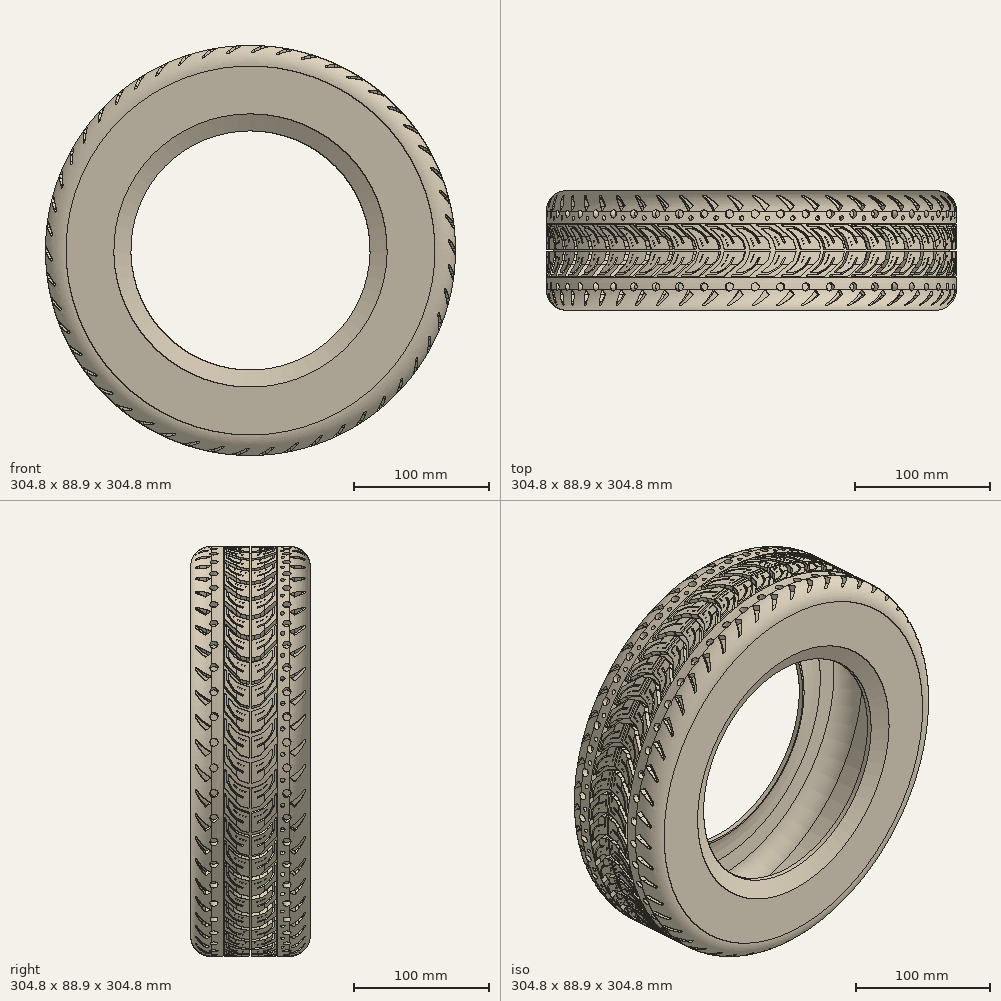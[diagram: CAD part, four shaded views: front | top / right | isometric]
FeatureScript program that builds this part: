
annotation { "Feature Type Name" : "Feature", "Feature Type Description" : "" }
export const myFeature = defineFeature(function(context is Context, id is Id, definition is map)
    precondition{}
    {
        {
            var Q0;
            Q0=qCreatedBy(makeId("Top.planeOp"),FACE);
            var sketch = newSketch(context, id + "F0", { "sketchPlane" : qUnion([Q0])});
            skLineSegment(sketch, "E0", {"start": v(-88.9, 0) * mm, "end": v(-101.6, 6.35) * mm});
            skLineSegment(sketch, "E1", {"start": v(-101.6, 6.35) * mm, "end": v(-152.4, 6.35) * mm});
            skLineSegment(sketch, "E2", {"start": v(-152.4, 6.35) * mm, "end": v(-152.4, -17.78) * mm});
            skLineSegment(sketch, "E3", {"start": v(-152.4, -82.55) * mm, "end": v(-101.6, -82.55) * mm});
            skLineSegment(sketch, "E4", {"start": v(-101.6, -82.55) * mm, "end": v(-88.9, -76.2) * mm});
            skLineSegment(sketch, "E5", {"start": v(-88.9, -76.2) * mm, "end": v(-88.9, -72.4) * mm});
            skLineSegment(sketch, "E6.bottom", {"start": v(-152.4, -37.47) * mm, "end": v(-147.32, -37.47) * mm});
            skLineSegment(sketch, "E6.top", {"start": v(-152.4, -38.74) * mm, "end": v(-147.32, -38.74) * mm});
            skLineSegment(sketch, "E6.left", {"start": v(-152.4, -37.47) * mm, "end": v(-152.4, -38.74) * mm, "construction": true});
            skLineSegment(sketch, "E6.right", {"start": v(-147.32, -37.47) * mm, "end": v(-147.32, -38.74) * mm});
            skLineSegment(sketch, "E7.bottom", {"start": v(-152.4, -57.15) * mm, "end": v(-147.32, -57.15) * mm});
            skLineSegment(sketch, "E7.top", {"start": v(-152.4, -58.42) * mm, "end": v(-147.32, -58.42) * mm});
            skLineSegment(sketch, "E7.left", {"start": v(-152.4, -57.15) * mm, "end": v(-152.4, -58.42) * mm, "construction": true});
            skLineSegment(sketch, "E7.right", {"start": v(-147.32, -57.15) * mm, "end": v(-147.32, -58.42) * mm});
            skLineSegment(sketch, "E8.bottom", {"start": v(-152.4, -17.78) * mm, "end": v(-147.32, -17.78) * mm});
            skLineSegment(sketch, "E8.top", {"start": v(-152.4, -19.05) * mm, "end": v(-147.32, -19.05) * mm});
            skLineSegment(sketch, "E8.left", {"start": v(-152.4, -17.78) * mm, "end": v(-152.4, -19.05) * mm, "construction": true});
            skLineSegment(sketch, "E8.right", {"start": v(-147.32, -17.78) * mm, "end": v(-147.32, -19.05) * mm});
            skPoint(sketch, "E9", {"position": v(-152.4, -38.1) * mm});
            skLineSegment(sketch, "E10.trimOffspring", {"start": v(-152.4, -19.05) * mm, "end": v(-152.4, -37.47) * mm});
            skLineSegment(sketch, "E11.trimOffspring", {"start": v(-152.4, -38.74) * mm, "end": v(-152.4, -57.15) * mm});
            skLineSegment(sketch, "E12.trimOffspring", {"start": v(-152.4, -58.42) * mm, "end": v(-152.4, -82.55) * mm});
            skLineSegment(sketch, "E13", {"start": v(-88.9, -3.81) * mm, "end": v(-91.31, -2.63) * mm});
            skLineSegment(sketch, "E14", {"start": v(-113.64, 2.54) * mm, "end": v(-128.27, 2.54) * mm});
            skLineSegment(sketch, "E15", {"start": v(-143.5, -12.7) * mm, "end": v(-143.5, -63.5) * mm});
            skLineSegment(sketch, "E16", {"start": v(-128.27, -78.74) * mm, "end": v(-113.64, -78.74) * mm});
            skLineSegment(sketch, "E17", {"start": v(-91.32, -73.57) * mm, "end": v(-88.9, -72.4) * mm});
            skPoint(sketch, "E18.visualSharp", {"position": v(-101.88, -78.74) * mm});
            skArc(sketch, "E18.filletArc", {"start": v(-113.64, -78.74) * mm, "mid": v(-102.18, -77.43) * mm, "end": v(-91.32, -73.57) * mm});
            skPoint(sketch, "E19.visualSharp", {"position": v(-101.88, 2.54) * mm});
            skArc(sketch, "E19.filletArc", {"start": v(-91.31, -2.63) * mm, "mid": v(-102.18, 1.23) * mm, "end": v(-113.64, 2.54) * mm});
            skPoint(sketch, "E20.visualSharp", {"position": v(-143.5, 2.54) * mm});
            skArc(sketch, "E20.filletArc", {"start": v(-128.27, 2.54) * mm, "mid": v(-139.05, -1.92) * mm, "end": v(-143.5, -12.7) * mm});
            skPoint(sketch, "E21.visualSharp", {"position": v(-143.5, -78.74) * mm});
            skArc(sketch, "E21.filletArc", {"start": v(-143.5, -63.5) * mm, "mid": v(-139.05, -74.28) * mm, "end": v(-128.27, -78.74) * mm});
            skLineSegment(sketch, "E22.trimOffspring", {"start": v(-88.9, -3.8) * mm, "end": v(-88.9, 0) * mm});
            skSolve(sketch);
        }
        {
            var Q0;
            Q0=qCreatedBy(makeId("Top.planeOp"),FACE);
            var sketch = newSketch(context, id + "F1", { "sketchPlane" : qUnion([Q0])});
            skLineSegment(sketch, "E23", {"start": v(0, 30.8) * mm, "end": v(0, -66.3) * mm});
            skSolve(sketch);
        }
        {
            var Q0;
            Q0=makeQuery(id+"F0.imprint","IMPRINT",FACE,{"disambiguationData":[TD([[makeQuery(id+"F0.imprint","IMPRINT",EDGE,{"derivedFrom":sQuery(id+"F0.wireOp",EDGE,"E0")}),1.0]])]});
            var Q1;
            Q1=sQuery(id+"F1.wireOp",EDGE,"E23");
            revolve(context, id + "F2", {"entities" : qUnion([Q0]), "axis" : qUnion([Q1]), "revolveType" : RevolveType.FULL});
        }
        {
            var Q0;
            Q0=qCreatedBy(makeId("Top.planeOp"),FACE);
            cPlane(context, id + "F3", {"entities" : qUnion([Q0]), "cplaneType" : CPlaneType.OFFSET, "offset" : 152.4 * mm, "width" : 152.4 * mm, "height" : 152.4 * mm});
        }
        {
            var Q0;
            Q0=qCreatedBy(id+"F3.planeOp",FACE);
            var sketch = newSketch(context, id + "F4", { "sketchPlane" : qUnion([Q0])});
            skLineSegment(sketch, "E24", {"start": v(3.28, -18.53) * mm, "end": v(5.87, -20.6) * mm});
            skLineSegment(sketch, "E25", {"start": v(16.2, -31.53) * mm, "end": v(18.35, -38.1) * mm});
            skLineSegment(sketch, "E26", {"start": v(18.35, -38.1) * mm, "end": v(14.54, -38.1) * mm});
            skLineSegment(sketch, "E27", {"start": v(14.54, -38.1) * mm, "end": v(13.73, -35.49) * mm});
            skLineSegment(sketch, "E28", {"start": v(12.18, -30.48) * mm, "end": v(-1.8, -18.53) * mm});
            skLineSegment(sketch, "E29", {"start": v(-1.8, -18.53) * mm, "end": v(3.28, -18.53) * mm});
            skLineSegment(sketch, "E30.0.MirrorCS", {"start": v(14.54, -38.1) * mm, "end": v(13.73, -40.71) * mm});
            skLineSegment(sketch, "E31.0.MirrorCS", {"start": v(12.18, -45.72) * mm, "end": v(-1.8, -57.67) * mm});
            skLineSegment(sketch, "E32.0.MirrorCS", {"start": v(-1.8, -57.67) * mm, "end": v(3.28, -57.67) * mm});
            skLineSegment(sketch, "E33.0.MirrorCS", {"start": v(3.28, -57.67) * mm, "end": v(5.87, -55.6) * mm});
            skLineSegment(sketch, "E34.0.MirrorCS", {"start": v(16.2, -44.67) * mm, "end": v(18.35, -38.1) * mm});
            skPoint(sketch, "E35.visualSharp", {"position": v(15.02, -27.94) * mm});
            skArc(sketch, "E35.filletArc", {"start": v(16.2, -31.53) * mm, "mid": v(14.57, -28.25) * mm, "end": v(12.07, -25.58) * mm});
            skPoint(sketch, "E36.visualSharp", {"position": v(15.02, -48.26) * mm});
            skArc(sketch, "E36.filletArc", {"start": v(12.07, -50.62) * mm, "mid": v(14.57, -47.95) * mm, "end": v(16.2, -44.67) * mm});
            skLineSegment(sketch, "E37", {"start": v(13.73, -35.49) * mm, "end": v(1.75, -35.49) * mm});
            skLineSegment(sketch, "E38", {"start": v(1.75, -35.49) * mm, "end": v(0.57, -32.03) * mm});
            skLineSegment(sketch, "E39", {"start": v(-2.43, -27.2) * mm, "end": v(-4.76, -24.84) * mm});
            skLineSegment(sketch, "E40", {"start": v(-4.76, -24.84) * mm, "end": v(-2.45, -26.92) * mm});
            skLineSegment(sketch, "E41", {"start": v(1.07, -32.25) * mm, "end": v(1.98, -34.92) * mm});
            skLineSegment(sketch, "E42", {"start": v(1.98, -34.92) * mm, "end": v(13.56, -34.92) * mm});
            skPoint(sketch, "E43.visualSharp", {"position": v(-0.38, -29.27) * mm});
            skArc(sketch, "E43.filletArc", {"start": v(0.57, -32.03) * mm, "mid": v(-0.66, -29.45) * mm, "end": v(-2.43, -27.2) * mm});
            skPoint(sketch, "E44.visualSharp", {"position": v(0, -29.13) * mm});
            skArc(sketch, "E44.filletArc", {"start": v(1.07, -32.25) * mm, "mid": v(-0.35, -29.36) * mm, "end": v(-2.45, -26.92) * mm});
            skLineSegment(sketch, "E45.trimOffspring", {"start": v(13.56, -34.92) * mm, "end": v(12.18, -30.48) * mm});
            skLineSegment(sketch, "E46.trimOffspring", {"start": v(7.15, -21.63) * mm, "end": v(12.07, -25.58) * mm});
            skLineSegment(sketch, "E47", {"start": v(7.15, -21.63) * mm, "end": v(9.7, -21.63) * mm});
            skLineSegment(sketch, "E48", {"start": v(16.06, -23.34) * mm, "end": v(17.68, -24.28) * mm});
            skLineSegment(sketch, "E49", {"start": v(22.64, -29.52) * mm, "end": v(24.47, -33.12) * mm});
            skLineSegment(sketch, "E50", {"start": v(24.47, -33.12) * mm, "end": v(25.78, -33.12) * mm});
            skLineSegment(sketch, "E51", {"start": v(25.78, -33.12) * mm, "end": v(23.67, -28.97) * mm});
            skLineSegment(sketch, "E52", {"start": v(18.6, -23.67) * mm, "end": v(13.2, -20.6) * mm});
            skLineSegment(sketch, "E53", {"start": v(13.2, -20.6) * mm, "end": v(5.87, -20.6) * mm});
            skPoint(sketch, "E54.visualSharp", {"position": v(20.94, -26.17) * mm});
            skArc(sketch, "E54.filletArc", {"start": v(22.64, -29.52) * mm, "mid": v(20.54, -26.54) * mm, "end": v(17.68, -24.28) * mm});
            skPoint(sketch, "E55.visualSharp", {"position": v(21.94, -25.56) * mm});
            skArc(sketch, "E55.filletArc", {"start": v(23.67, -28.97) * mm, "mid": v(23.4, -28.45) * mm, "end": v(23.1, -27.95) * mm});
            skPoint(sketch, "E56.visualSharp", {"position": v(13.1, -21.63) * mm});
            skArc(sketch, "E56.filletArc", {"start": v(16.06, -23.34) * mm, "mid": v(12.99, -22.07) * mm, "end": v(9.7, -21.63) * mm});
            skLineSegment(sketch, "E57", {"start": v(23.1, -27.95) * mm, "end": v(29.11, -27.95) * mm});
            skLineSegment(sketch, "E58", {"start": v(29.11, -27.95) * mm, "end": v(29.11, -27.6) * mm});
            skLineSegment(sketch, "E59", {"start": v(29.11, -27.6) * mm, "end": v(22.86, -27.6) * mm});
            skArc(sketch, "E60.trimOffspring", {"start": v(22.86, -27.6) * mm, "mid": v(20.96, -25.39) * mm, "end": v(18.6, -23.67) * mm});
            skLineSegment(sketch, "E61.0.MirrorCS", {"start": v(29.11, -48.25) * mm, "end": v(29.11, -48.6) * mm});
            skLineSegment(sketch, "E61.1.MirrorCS", {"start": v(23.1, -48.25) * mm, "end": v(29.11, -48.25) * mm});
            skLineSegment(sketch, "E61.2.MirrorCS", {"start": v(24.47, -43.08) * mm, "end": v(25.78, -43.08) * mm});
            skArc(sketch, "E61.3.MirrorCS", {"start": v(22.86, -48.6) * mm, "mid": v(20.96, -50.81) * mm, "end": v(18.6, -52.53) * mm});
            skLineSegment(sketch, "E61.4.MirrorCS", {"start": v(25.78, -43.08) * mm, "end": v(23.67, -47.23) * mm});
            skLineSegment(sketch, "E61.5.MirrorCS", {"start": v(29.11, -48.6) * mm, "end": v(22.86, -48.6) * mm});
            skArc(sketch, "E61.6.MirrorCS", {"start": v(22.64, -46.68) * mm, "mid": v(20.54, -49.66) * mm, "end": v(17.68, -51.92) * mm});
            skArc(sketch, "E61.7.MirrorCS", {"start": v(23.67, -47.23) * mm, "mid": v(23.4, -47.75) * mm, "end": v(23.1, -48.25) * mm});
            skPoint(sketch, "E61.8.MirrorP", {"position": v(21.94, -50.64) * mm});
            skPoint(sketch, "E61.9.MirrorP", {"position": v(20.94, -50.03) * mm});
            skLineSegment(sketch, "E61.10.MirrorCS", {"start": v(22.64, -46.68) * mm, "end": v(24.47, -43.08) * mm});
            skLineSegment(sketch, "E62.0.MirrorCS", {"start": v(16.06, -52.86) * mm, "end": v(17.68, -51.92) * mm});
            skPoint(sketch, "E62.1.MirrorP", {"position": v(13.1, -54.57) * mm});
            skLineSegment(sketch, "E62.2.MirrorCS", {"start": v(18.6, -52.53) * mm, "end": v(13.2, -55.6) * mm});
            skLineSegment(sketch, "E62.3.MirrorCS", {"start": v(13.2, -55.6) * mm, "end": v(5.87, -55.6) * mm});
            skArc(sketch, "E62.4.MirrorCS", {"start": v(16.06, -52.86) * mm, "mid": v(12.99, -54.13) * mm, "end": v(9.7, -54.57) * mm});
            skLineSegment(sketch, "E63.0.MirrorCS", {"start": v(7.15, -54.57) * mm, "end": v(9.7, -54.57) * mm});
            skPoint(sketch, "E64.0.MirrorP", {"position": v(0, -47.07) * mm});
            skArc(sketch, "E64.1.MirrorCS", {"start": v(1.07, -43.95) * mm, "mid": v(-0.35, -46.84) * mm, "end": v(-2.45, -49.28) * mm});
            skLineSegment(sketch, "E64.2.MirrorCS", {"start": v(-2.43, -49) * mm, "end": v(-4.76, -51.36) * mm});
            skLineSegment(sketch, "E64.3.MirrorCS", {"start": v(1.75, -40.71) * mm, "end": v(0.57, -44.17) * mm});
            skArc(sketch, "E64.4.MirrorCS", {"start": v(0.57, -44.17) * mm, "mid": v(-0.66, -46.75) * mm, "end": v(-2.43, -49) * mm});
            skLineSegment(sketch, "E64.5.MirrorCS", {"start": v(1.07, -43.95) * mm, "end": v(1.98, -41.28) * mm});
            skLineSegment(sketch, "E64.6.MirrorCS", {"start": v(-4.76, -51.36) * mm, "end": v(-2.45, -49.28) * mm});
            skPoint(sketch, "E64.7.MirrorP", {"position": v(-0.38, -46.93) * mm});
            skLineSegment(sketch, "E65.0.MirrorCS", {"start": v(13.73, -40.71) * mm, "end": v(1.75, -40.71) * mm});
            skLineSegment(sketch, "E66.0.MirrorCS", {"start": v(1.98, -41.28) * mm, "end": v(13.56, -41.28) * mm});
            skLineSegment(sketch, "E67.trimOffspring", {"start": v(13.56, -41.28) * mm, "end": v(12.18, -45.72) * mm});
            skLineSegment(sketch, "E68.trimOffspring", {"start": v(7.15, -54.57) * mm, "end": v(12.07, -50.62) * mm});
            skCircle(sketch, "E69", {"center": v(11.89, -14.08) * mm, "radius": 1.67 * mm});
            skCircle(sketch, "E70", {"center": v(2.74, -10.98) * mm, "radius": 3.03 * mm});
            skLineSegment(sketch, "E71", {"start": v(10.12, -9.06) * mm, "end": v(7.72, -5.31) * mm});
            skLineSegment(sketch, "E72", {"start": v(3.19, 0) * mm, "end": v(-5.38, 7.62) * mm});
            skLineSegment(sketch, "E73", {"start": v(-5.38, 7.62) * mm, "end": v(-4.52, 6.86) * mm});
            skLineSegment(sketch, "E74", {"start": v(-4.52, 6.86) * mm, "end": v(6.4, 0.45) * mm});
            skLineSegment(sketch, "E75", {"start": v(10.3, -2.38) * mm, "end": v(13.22, -4.93) * mm});
            skLineSegment(sketch, "E76", {"start": v(13.22, -4.93) * mm, "end": v(10.12, -9.06) * mm});
            skPoint(sketch, "E77.visualSharp", {"position": v(5.82, -2.34) * mm});
            skArc(sketch, "E77.filletArc", {"start": v(7.72, -5.31) * mm, "mid": v(5.64, -2.5) * mm, "end": v(3.19, 0) * mm});
            skPoint(sketch, "E78.visualSharp", {"position": v(8.49, -0.78) * mm});
            skArc(sketch, "E78.filletArc", {"start": v(10.3, -2.38) * mm, "mid": v(8.42, -0.87) * mm, "end": v(6.4, 0.45) * mm});
            skCircle(sketch, "E79.0.MirrorC", {"center": v(11.89, -62.12) * mm, "radius": 1.67 * mm});
            skCircle(sketch, "E80.0.MirrorC", {"center": v(2.74, -65.22) * mm, "radius": 3.03 * mm});
            skLineSegment(sketch, "E81.0.MirrorCS", {"start": v(13.22, -71.27) * mm, "end": v(10.12, -67.14) * mm});
            skLineSegment(sketch, "E82.0.MirrorCS", {"start": v(10.12, -67.14) * mm, "end": v(7.72, -70.89) * mm});
            skLineSegment(sketch, "E83.0.MirrorCS", {"start": v(10.3, -73.82) * mm, "end": v(13.22, -71.27) * mm});
            skArc(sketch, "E84.0.MirrorCS", {"start": v(10.3, -73.82) * mm, "mid": v(8.42, -75.33) * mm, "end": v(6.4, -76.65) * mm});
            skArc(sketch, "E85.0.MirrorCS", {"start": v(7.72, -70.89) * mm, "mid": v(5.64, -73.7) * mm, "end": v(3.19, -76.2) * mm});
            skLineSegment(sketch, "E86.0.MirrorCS", {"start": v(3.19, -76.2) * mm, "end": v(-5.38, -83.82) * mm});
            skLineSegment(sketch, "E87.0.MirrorCS", {"start": v(-4.52, -83.06) * mm, "end": v(6.4, -76.65) * mm});
            skLineSegment(sketch, "E88.0.MirrorCS", {"start": v(-5.38, -83.82) * mm, "end": v(-4.52, -83.06) * mm});
            skLineSegment(sketch, "E89", {"start": v(2.63, -62.2) * mm, "end": v(2.86, -62.2) * mm});
            skSolve(sketch);
        }
        {
            var Q0;
            Q0=makeQuery(id+"F4.imprint","IMPRINT",FACE,{"disambiguationData":[TD([[makeQuery(id+"F4.imprint","IMPRINT",EDGE,{"derivedFrom":sQuery(id+"F4.wireOp",EDGE,"E24")}),-1.0]])]});
            var Q1;
            Q1=makeQuery(id+"F4.imprint","IMPRINT",FACE,{"disambiguationData":[TD([[makeQuery(id+"F4.imprint","IMPRINT",EDGE,{"derivedFrom":sQuery(id+"F4.wireOp",EDGE,"E26")}),1.0]])]});
            var Q2;
            Q2=makeQuery(id+"F4.imprint","IMPRINT",FACE,{"disambiguationData":[TD([[makeQuery(id+"F4.imprint","IMPRINT",EDGE,{"derivedFrom":sQuery(id+"F4.wireOp",EDGE,"E70")}),1.0]])]});
            var Q3;
            Q3=makeQuery(id+"F4.imprint","IMPRINT",FACE,{"disambiguationData":[TD([[makeQuery(id+"F4.imprint","IMPRINT",EDGE,{"derivedFrom":sQuery(id+"F4.wireOp",EDGE,"E69")}),1.0]])]});
            var Q4;
            Q4=makeQuery(id+"F4.imprint","IMPRINT",FACE,{"disambiguationData":[TD([[makeQuery(id+"F4.imprint","IMPRINT",EDGE,{"derivedFrom":sQuery(id+"F4.wireOp",EDGE,"E71")}),-1.0]])]});
            var Q5;
            Q5=makeQuery(id+"F4.imprint","IMPRINT",FACE,{"disambiguationData":[TD([[makeQuery(id+"F4.imprint","IMPRINT",EDGE,{"derivedFrom":sQuery(id+"F4.wireOp",EDGE,"E79.0.MirrorC")}),-1.0]])]});
            var Q6;
            {var subQ0=sQuery(id+"F4.wireOp",EDGE,"E89");Q6=makeQuery(id+"F4.imprint","IMPRINT",FACE,{"disambiguationData":[TD([[makeQuery(id+"F4.imprint","IMPRINT",EDGE,{"derivedFrom":subQ0}),-1.0]])]});}
            var Q7;
            Q7=makeQuery(id+"F4.imprint","IMPRINT",FACE,{"disambiguationData":[TD([[makeQuery(id+"F4.imprint","IMPRINT",EDGE,{"derivedFrom":sQuery(id+"F4.wireOp",EDGE,"E81.0.MirrorCS")}),1.0]])]});
            var Q8;
            Q8=makeQuery(id+"F2.opRevolve","SWEPT_FACE",FACE,{"disambiguationData":[OSD([sQuery(id+"F0.wireOp",EDGE,"E6.right")])]});
            extrude(context, id + "F5", {"entities" : qUnion([Q0, Q1, Q2, Q3, Q4, Q5, Q6, Q7]), "endBound" : BoundingType.UP_TO_SURFACE, "oppositeDirection" : true, "endBoundEntityFace" : qUnion([Q8]), "depth" : 25.4 * mm});
        }
        {
            var Q0;
            Q0=makeQuery(id+"F5.opExtrude","SWEPT_BODY",BODY,{"disambiguationData":[OSD([sQuery(id+"F4.wireOp",EDGE,"E24"),sQuery(id+"F4.wireOp",EDGE,"E25"),sQuery(id+"F4.wireOp",EDGE,"E26"),sQuery(id+"F4.wireOp",EDGE,"E27"),sQuery(id+"F4.wireOp",EDGE,"E28"),sQuery(id+"F4.wireOp",EDGE,"E29")])]});
            var Q1;
            Q1=makeQuery(id+"F5.opExtrude","SWEPT_BODY",BODY,{"disambiguationData":[OSD([sQuery(id+"F4.wireOp",EDGE,"E71"),sQuery(id+"F4.wireOp",EDGE,"E72"),sQuery(id+"F4.wireOp",EDGE,"E74"),sQuery(id+"F4.wireOp",EDGE,"E75"),sQuery(id+"F4.wireOp",EDGE,"E76"),sQuery(id+"F4.wireOp",EDGE,"E77.filletArc"),sQuery(id+"F4.wireOp",EDGE,"E78.filletArc")])]});
            var Q2;
            Q2=makeQuery(id+"F5.opExtrude","SWEPT_BODY",BODY,{"disambiguationData":[OSD([sQuery(id+"F4.wireOp",EDGE,"E70")])]});
            var Q3;
            Q3=makeQuery(id+"F5.opExtrude","SWEPT_BODY",BODY,{"disambiguationData":[OSD([sQuery(id+"F4.wireOp",EDGE,"E69")])]});
            var Q4;
            Q4=makeQuery(id+"F5.opExtrude","SWEPT_BODY",BODY,{"disambiguationData":[OSD([sQuery(id+"F4.wireOp",EDGE,"E80.0.MirrorC"),sQuery(id+"F4.wireOp",EDGE,"E89")])]});
            var Q5;
            Q5=makeQuery(id+"F5.opExtrude","SWEPT_BODY",BODY,{"disambiguationData":[OSD([sQuery(id+"F4.wireOp",EDGE,"E79.0.MirrorC")])]});
            var Q6;
            Q6=makeQuery(id+"F5.opExtrude","SWEPT_BODY",BODY,{"disambiguationData":[OSD([sQuery(id+"F4.wireOp",EDGE,"E81.0.MirrorCS"),sQuery(id+"F4.wireOp",EDGE,"E82.0.MirrorCS"),sQuery(id+"F4.wireOp",EDGE,"E83.0.MirrorCS"),sQuery(id+"F4.wireOp",EDGE,"E84.0.MirrorCS"),sQuery(id+"F4.wireOp",EDGE,"E85.0.MirrorCS"),sQuery(id+"F4.wireOp",EDGE,"E86.0.MirrorCS"),sQuery(id+"F4.wireOp",EDGE,"E87.0.MirrorCS")])]});
            var Q7;
            Q7=sQuery(id+"F1.wireOp",EDGE,"E23");
            circularPattern(context, id + "F6", {"entities" : qUnion([Q0, Q1, Q2, Q3, Q4, Q5, Q6]), "axis" : qUnion([Q7]), "angle" : 360 * degree, "instanceCount" : 50, "equalSpace" : true});
        }
        {
            var Q0;
            Q0=makeQuery(id+"F5.opExtrude","SWEPT_BODY",BODY,{"disambiguationData":[OSD([sQuery(id+"F4.wireOp",EDGE,"E69")])]});
            var Q1;
            Q1=makeQuery(id+"F5.opExtrude","SWEPT_BODY",BODY,{"disambiguationData":[OSD([sQuery(id+"F4.wireOp",EDGE,"E70")])]});
            var Q2;
            Q2=makeQuery(id+"F5.opExtrude","SWEPT_BODY",BODY,{"disambiguationData":[OSD([sQuery(id+"F4.wireOp",EDGE,"E71"),sQuery(id+"F4.wireOp",EDGE,"E72"),sQuery(id+"F4.wireOp",EDGE,"E74"),sQuery(id+"F4.wireOp",EDGE,"E75"),sQuery(id+"F4.wireOp",EDGE,"E76"),sQuery(id+"F4.wireOp",EDGE,"E77.filletArc"),sQuery(id+"F4.wireOp",EDGE,"E78.filletArc")])]});
            var Q3;
            Q3=makeQuery(id+"F5.opExtrude","SWEPT_BODY",BODY,{"disambiguationData":[OSD([sQuery(id+"F4.wireOp",EDGE,"E79.0.MirrorC")])]});
            var Q4;
            Q4=makeQuery(id+"F5.opExtrude","SWEPT_BODY",BODY,{"disambiguationData":[OSD([sQuery(id+"F4.wireOp",EDGE,"E80.0.MirrorC"),sQuery(id+"F4.wireOp",EDGE,"E89")])]});
            var Q5;
            Q5=makeQuery(id+"F5.opExtrude","SWEPT_BODY",BODY,{"disambiguationData":[OSD([sQuery(id+"F4.wireOp",EDGE,"E81.0.MirrorCS"),sQuery(id+"F4.wireOp",EDGE,"E82.0.MirrorCS"),sQuery(id+"F4.wireOp",EDGE,"E83.0.MirrorCS"),sQuery(id+"F4.wireOp",EDGE,"E84.0.MirrorCS"),sQuery(id+"F4.wireOp",EDGE,"E85.0.MirrorCS"),sQuery(id+"F4.wireOp",EDGE,"E86.0.MirrorCS"),sQuery(id+"F4.wireOp",EDGE,"E87.0.MirrorCS")])]});
            var Q6;
            Q6=makeQuery(id+"F6.opPattern","COPY",BODY,{"derivedFrom":makeQuery(id+"F5.opExtrude","SWEPT_BODY",BODY,{"disambiguationData":[OSD([sQuery(id+"F4.wireOp",EDGE,"E69")])]}),"instanceName":"1"});
            var Q7;
            Q7=makeQuery(id+"F6.opPattern","COPY",BODY,{"derivedFrom":makeQuery(id+"F5.opExtrude","SWEPT_BODY",BODY,{"disambiguationData":[OSD([sQuery(id+"F4.wireOp",EDGE,"E70")])]}),"instanceName":"1"});
            var Q8;
            Q8=makeQuery(id+"F6.opPattern","COPY",BODY,{"derivedFrom":makeQuery(id+"F5.opExtrude","SWEPT_BODY",BODY,{"disambiguationData":[OSD([sQuery(id+"F4.wireOp",EDGE,"E71"),sQuery(id+"F4.wireOp",EDGE,"E72"),sQuery(id+"F4.wireOp",EDGE,"E74"),sQuery(id+"F4.wireOp",EDGE,"E75"),sQuery(id+"F4.wireOp",EDGE,"E76"),sQuery(id+"F4.wireOp",EDGE,"E77.filletArc"),sQuery(id+"F4.wireOp",EDGE,"E78.filletArc")])]}),"instanceName":"1"});
            var Q9;
            Q9=makeQuery(id+"F6.opPattern","COPY",BODY,{"derivedFrom":makeQuery(id+"F5.opExtrude","SWEPT_BODY",BODY,{"disambiguationData":[OSD([sQuery(id+"F4.wireOp",EDGE,"E79.0.MirrorC")])]}),"instanceName":"1"});
            var Q10;
            Q10=makeQuery(id+"F6.opPattern","COPY",BODY,{"derivedFrom":makeQuery(id+"F5.opExtrude","SWEPT_BODY",BODY,{"disambiguationData":[OSD([sQuery(id+"F4.wireOp",EDGE,"E80.0.MirrorC"),sQuery(id+"F4.wireOp",EDGE,"E89")])]}),"instanceName":"1"});
            var Q11;
            Q11=makeQuery(id+"F6.opPattern","COPY",BODY,{"derivedFrom":makeQuery(id+"F5.opExtrude","SWEPT_BODY",BODY,{"disambiguationData":[OSD([sQuery(id+"F4.wireOp",EDGE,"E81.0.MirrorCS"),sQuery(id+"F4.wireOp",EDGE,"E82.0.MirrorCS"),sQuery(id+"F4.wireOp",EDGE,"E83.0.MirrorCS"),sQuery(id+"F4.wireOp",EDGE,"E84.0.MirrorCS"),sQuery(id+"F4.wireOp",EDGE,"E85.0.MirrorCS"),sQuery(id+"F4.wireOp",EDGE,"E86.0.MirrorCS"),sQuery(id+"F4.wireOp",EDGE,"E87.0.MirrorCS")])]}),"instanceName":"1"});
            var Q12;
            Q12=makeQuery(id+"F6.opPattern","COPY",BODY,{"derivedFrom":makeQuery(id+"F5.opExtrude","SWEPT_BODY",BODY,{"disambiguationData":[OSD([sQuery(id+"F4.wireOp",EDGE,"E69")])]}),"instanceName":"2"});
            var Q13;
            Q13=makeQuery(id+"F6.opPattern","COPY",BODY,{"derivedFrom":makeQuery(id+"F5.opExtrude","SWEPT_BODY",BODY,{"disambiguationData":[OSD([sQuery(id+"F4.wireOp",EDGE,"E70")])]}),"instanceName":"2"});
            var Q14;
            Q14=makeQuery(id+"F6.opPattern","COPY",BODY,{"derivedFrom":makeQuery(id+"F5.opExtrude","SWEPT_BODY",BODY,{"disambiguationData":[OSD([sQuery(id+"F4.wireOp",EDGE,"E71"),sQuery(id+"F4.wireOp",EDGE,"E72"),sQuery(id+"F4.wireOp",EDGE,"E74"),sQuery(id+"F4.wireOp",EDGE,"E75"),sQuery(id+"F4.wireOp",EDGE,"E76"),sQuery(id+"F4.wireOp",EDGE,"E77.filletArc"),sQuery(id+"F4.wireOp",EDGE,"E78.filletArc")])]}),"instanceName":"2"});
            var Q15;
            Q15=makeQuery(id+"F6.opPattern","COPY",BODY,{"derivedFrom":makeQuery(id+"F5.opExtrude","SWEPT_BODY",BODY,{"disambiguationData":[OSD([sQuery(id+"F4.wireOp",EDGE,"E79.0.MirrorC")])]}),"instanceName":"2"});
            var Q16;
            Q16=makeQuery(id+"F6.opPattern","COPY",BODY,{"derivedFrom":makeQuery(id+"F5.opExtrude","SWEPT_BODY",BODY,{"disambiguationData":[OSD([sQuery(id+"F4.wireOp",EDGE,"E80.0.MirrorC"),sQuery(id+"F4.wireOp",EDGE,"E89")])]}),"instanceName":"2"});
            var Q17;
            Q17=makeQuery(id+"F6.opPattern","COPY",BODY,{"derivedFrom":makeQuery(id+"F5.opExtrude","SWEPT_BODY",BODY,{"disambiguationData":[OSD([sQuery(id+"F4.wireOp",EDGE,"E81.0.MirrorCS"),sQuery(id+"F4.wireOp",EDGE,"E82.0.MirrorCS"),sQuery(id+"F4.wireOp",EDGE,"E83.0.MirrorCS"),sQuery(id+"F4.wireOp",EDGE,"E84.0.MirrorCS"),sQuery(id+"F4.wireOp",EDGE,"E85.0.MirrorCS"),sQuery(id+"F4.wireOp",EDGE,"E86.0.MirrorCS"),sQuery(id+"F4.wireOp",EDGE,"E87.0.MirrorCS")])]}),"instanceName":"2"});
            var Q18;
            Q18=makeQuery(id+"F6.opPattern","COPY",BODY,{"derivedFrom":makeQuery(id+"F5.opExtrude","SWEPT_BODY",BODY,{"disambiguationData":[OSD([sQuery(id+"F4.wireOp",EDGE,"E69")])]}),"instanceName":"3"});
            var Q19;
            Q19=makeQuery(id+"F6.opPattern","COPY",BODY,{"derivedFrom":makeQuery(id+"F5.opExtrude","SWEPT_BODY",BODY,{"disambiguationData":[OSD([sQuery(id+"F4.wireOp",EDGE,"E70")])]}),"instanceName":"3"});
            var Q20;
            Q20=makeQuery(id+"F6.opPattern","COPY",BODY,{"derivedFrom":makeQuery(id+"F5.opExtrude","SWEPT_BODY",BODY,{"disambiguationData":[OSD([sQuery(id+"F4.wireOp",EDGE,"E71"),sQuery(id+"F4.wireOp",EDGE,"E72"),sQuery(id+"F4.wireOp",EDGE,"E74"),sQuery(id+"F4.wireOp",EDGE,"E75"),sQuery(id+"F4.wireOp",EDGE,"E76"),sQuery(id+"F4.wireOp",EDGE,"E77.filletArc"),sQuery(id+"F4.wireOp",EDGE,"E78.filletArc")])]}),"instanceName":"3"});
            var Q21;
            Q21=makeQuery(id+"F6.opPattern","COPY",BODY,{"derivedFrom":makeQuery(id+"F5.opExtrude","SWEPT_BODY",BODY,{"disambiguationData":[OSD([sQuery(id+"F4.wireOp",EDGE,"E79.0.MirrorC")])]}),"instanceName":"3"});
            var Q22;
            Q22=makeQuery(id+"F6.opPattern","COPY",BODY,{"derivedFrom":makeQuery(id+"F5.opExtrude","SWEPT_BODY",BODY,{"disambiguationData":[OSD([sQuery(id+"F4.wireOp",EDGE,"E80.0.MirrorC"),sQuery(id+"F4.wireOp",EDGE,"E89")])]}),"instanceName":"3"});
            var Q23;
            Q23=makeQuery(id+"F6.opPattern","COPY",BODY,{"derivedFrom":makeQuery(id+"F5.opExtrude","SWEPT_BODY",BODY,{"disambiguationData":[OSD([sQuery(id+"F4.wireOp",EDGE,"E81.0.MirrorCS"),sQuery(id+"F4.wireOp",EDGE,"E82.0.MirrorCS"),sQuery(id+"F4.wireOp",EDGE,"E83.0.MirrorCS"),sQuery(id+"F4.wireOp",EDGE,"E84.0.MirrorCS"),sQuery(id+"F4.wireOp",EDGE,"E85.0.MirrorCS"),sQuery(id+"F4.wireOp",EDGE,"E86.0.MirrorCS"),sQuery(id+"F4.wireOp",EDGE,"E87.0.MirrorCS")])]}),"instanceName":"3"});
            var Q24;
            Q24=makeQuery(id+"F6.opPattern","COPY",BODY,{"derivedFrom":makeQuery(id+"F5.opExtrude","SWEPT_BODY",BODY,{"disambiguationData":[OSD([sQuery(id+"F4.wireOp",EDGE,"E69")])]}),"instanceName":"4"});
            var Q25;
            Q25=makeQuery(id+"F6.opPattern","COPY",BODY,{"derivedFrom":makeQuery(id+"F5.opExtrude","SWEPT_BODY",BODY,{"disambiguationData":[OSD([sQuery(id+"F4.wireOp",EDGE,"E70")])]}),"instanceName":"4"});
            var Q26;
            Q26=makeQuery(id+"F6.opPattern","COPY",BODY,{"derivedFrom":makeQuery(id+"F5.opExtrude","SWEPT_BODY",BODY,{"disambiguationData":[OSD([sQuery(id+"F4.wireOp",EDGE,"E71"),sQuery(id+"F4.wireOp",EDGE,"E72"),sQuery(id+"F4.wireOp",EDGE,"E74"),sQuery(id+"F4.wireOp",EDGE,"E75"),sQuery(id+"F4.wireOp",EDGE,"E76"),sQuery(id+"F4.wireOp",EDGE,"E77.filletArc"),sQuery(id+"F4.wireOp",EDGE,"E78.filletArc")])]}),"instanceName":"4"});
            var Q27;
            Q27=makeQuery(id+"F6.opPattern","COPY",BODY,{"derivedFrom":makeQuery(id+"F5.opExtrude","SWEPT_BODY",BODY,{"disambiguationData":[OSD([sQuery(id+"F4.wireOp",EDGE,"E79.0.MirrorC")])]}),"instanceName":"4"});
            var Q28;
            Q28=makeQuery(id+"F6.opPattern","COPY",BODY,{"derivedFrom":makeQuery(id+"F5.opExtrude","SWEPT_BODY",BODY,{"disambiguationData":[OSD([sQuery(id+"F4.wireOp",EDGE,"E80.0.MirrorC"),sQuery(id+"F4.wireOp",EDGE,"E89")])]}),"instanceName":"4"});
            var Q29;
            Q29=makeQuery(id+"F6.opPattern","COPY",BODY,{"derivedFrom":makeQuery(id+"F5.opExtrude","SWEPT_BODY",BODY,{"disambiguationData":[OSD([sQuery(id+"F4.wireOp",EDGE,"E81.0.MirrorCS"),sQuery(id+"F4.wireOp",EDGE,"E82.0.MirrorCS"),sQuery(id+"F4.wireOp",EDGE,"E83.0.MirrorCS"),sQuery(id+"F4.wireOp",EDGE,"E84.0.MirrorCS"),sQuery(id+"F4.wireOp",EDGE,"E85.0.MirrorCS"),sQuery(id+"F4.wireOp",EDGE,"E86.0.MirrorCS"),sQuery(id+"F4.wireOp",EDGE,"E87.0.MirrorCS")])]}),"instanceName":"4"});
            var Q30;
            Q30=makeQuery(id+"F6.opPattern","COPY",BODY,{"derivedFrom":makeQuery(id+"F5.opExtrude","SWEPT_BODY",BODY,{"disambiguationData":[OSD([sQuery(id+"F4.wireOp",EDGE,"E69")])]}),"instanceName":"5"});
            var Q31;
            Q31=makeQuery(id+"F6.opPattern","COPY",BODY,{"derivedFrom":makeQuery(id+"F5.opExtrude","SWEPT_BODY",BODY,{"disambiguationData":[OSD([sQuery(id+"F4.wireOp",EDGE,"E70")])]}),"instanceName":"5"});
            var Q32;
            Q32=makeQuery(id+"F6.opPattern","COPY",BODY,{"derivedFrom":makeQuery(id+"F5.opExtrude","SWEPT_BODY",BODY,{"disambiguationData":[OSD([sQuery(id+"F4.wireOp",EDGE,"E71"),sQuery(id+"F4.wireOp",EDGE,"E72"),sQuery(id+"F4.wireOp",EDGE,"E74"),sQuery(id+"F4.wireOp",EDGE,"E75"),sQuery(id+"F4.wireOp",EDGE,"E76"),sQuery(id+"F4.wireOp",EDGE,"E77.filletArc"),sQuery(id+"F4.wireOp",EDGE,"E78.filletArc")])]}),"instanceName":"5"});
            var Q33;
            Q33=makeQuery(id+"F6.opPattern","COPY",BODY,{"derivedFrom":makeQuery(id+"F5.opExtrude","SWEPT_BODY",BODY,{"disambiguationData":[OSD([sQuery(id+"F4.wireOp",EDGE,"E79.0.MirrorC")])]}),"instanceName":"5"});
            var Q34;
            Q34=makeQuery(id+"F6.opPattern","COPY",BODY,{"derivedFrom":makeQuery(id+"F5.opExtrude","SWEPT_BODY",BODY,{"disambiguationData":[OSD([sQuery(id+"F4.wireOp",EDGE,"E80.0.MirrorC"),sQuery(id+"F4.wireOp",EDGE,"E89")])]}),"instanceName":"5"});
            var Q35;
            Q35=makeQuery(id+"F6.opPattern","COPY",BODY,{"derivedFrom":makeQuery(id+"F5.opExtrude","SWEPT_BODY",BODY,{"disambiguationData":[OSD([sQuery(id+"F4.wireOp",EDGE,"E81.0.MirrorCS"),sQuery(id+"F4.wireOp",EDGE,"E82.0.MirrorCS"),sQuery(id+"F4.wireOp",EDGE,"E83.0.MirrorCS"),sQuery(id+"F4.wireOp",EDGE,"E84.0.MirrorCS"),sQuery(id+"F4.wireOp",EDGE,"E85.0.MirrorCS"),sQuery(id+"F4.wireOp",EDGE,"E86.0.MirrorCS"),sQuery(id+"F4.wireOp",EDGE,"E87.0.MirrorCS")])]}),"instanceName":"5"});
            var Q36;
            Q36=makeQuery(id+"F6.opPattern","COPY",BODY,{"derivedFrom":makeQuery(id+"F5.opExtrude","SWEPT_BODY",BODY,{"disambiguationData":[OSD([sQuery(id+"F4.wireOp",EDGE,"E69")])]}),"instanceName":"6"});
            var Q37;
            Q37=makeQuery(id+"F6.opPattern","COPY",BODY,{"derivedFrom":makeQuery(id+"F5.opExtrude","SWEPT_BODY",BODY,{"disambiguationData":[OSD([sQuery(id+"F4.wireOp",EDGE,"E70")])]}),"instanceName":"6"});
            var Q38;
            Q38=makeQuery(id+"F6.opPattern","COPY",BODY,{"derivedFrom":makeQuery(id+"F5.opExtrude","SWEPT_BODY",BODY,{"disambiguationData":[OSD([sQuery(id+"F4.wireOp",EDGE,"E71"),sQuery(id+"F4.wireOp",EDGE,"E72"),sQuery(id+"F4.wireOp",EDGE,"E74"),sQuery(id+"F4.wireOp",EDGE,"E75"),sQuery(id+"F4.wireOp",EDGE,"E76"),sQuery(id+"F4.wireOp",EDGE,"E77.filletArc"),sQuery(id+"F4.wireOp",EDGE,"E78.filletArc")])]}),"instanceName":"6"});
            var Q39;
            Q39=makeQuery(id+"F6.opPattern","COPY",BODY,{"derivedFrom":makeQuery(id+"F5.opExtrude","SWEPT_BODY",BODY,{"disambiguationData":[OSD([sQuery(id+"F4.wireOp",EDGE,"E79.0.MirrorC")])]}),"instanceName":"6"});
            var Q40;
            Q40=makeQuery(id+"F6.opPattern","COPY",BODY,{"derivedFrom":makeQuery(id+"F5.opExtrude","SWEPT_BODY",BODY,{"disambiguationData":[OSD([sQuery(id+"F4.wireOp",EDGE,"E80.0.MirrorC"),sQuery(id+"F4.wireOp",EDGE,"E89")])]}),"instanceName":"6"});
            var Q41;
            Q41=makeQuery(id+"F6.opPattern","COPY",BODY,{"derivedFrom":makeQuery(id+"F5.opExtrude","SWEPT_BODY",BODY,{"disambiguationData":[OSD([sQuery(id+"F4.wireOp",EDGE,"E81.0.MirrorCS"),sQuery(id+"F4.wireOp",EDGE,"E82.0.MirrorCS"),sQuery(id+"F4.wireOp",EDGE,"E83.0.MirrorCS"),sQuery(id+"F4.wireOp",EDGE,"E84.0.MirrorCS"),sQuery(id+"F4.wireOp",EDGE,"E85.0.MirrorCS"),sQuery(id+"F4.wireOp",EDGE,"E86.0.MirrorCS"),sQuery(id+"F4.wireOp",EDGE,"E87.0.MirrorCS")])]}),"instanceName":"6"});
            var Q42;
            Q42=makeQuery(id+"F6.opPattern","COPY",BODY,{"derivedFrom":makeQuery(id+"F5.opExtrude","SWEPT_BODY",BODY,{"disambiguationData":[OSD([sQuery(id+"F4.wireOp",EDGE,"E69")])]}),"instanceName":"7"});
            var Q43;
            Q43=makeQuery(id+"F6.opPattern","COPY",BODY,{"derivedFrom":makeQuery(id+"F5.opExtrude","SWEPT_BODY",BODY,{"disambiguationData":[OSD([sQuery(id+"F4.wireOp",EDGE,"E70")])]}),"instanceName":"7"});
            var Q44;
            Q44=makeQuery(id+"F6.opPattern","COPY",BODY,{"derivedFrom":makeQuery(id+"F5.opExtrude","SWEPT_BODY",BODY,{"disambiguationData":[OSD([sQuery(id+"F4.wireOp",EDGE,"E71"),sQuery(id+"F4.wireOp",EDGE,"E72"),sQuery(id+"F4.wireOp",EDGE,"E74"),sQuery(id+"F4.wireOp",EDGE,"E75"),sQuery(id+"F4.wireOp",EDGE,"E76"),sQuery(id+"F4.wireOp",EDGE,"E77.filletArc"),sQuery(id+"F4.wireOp",EDGE,"E78.filletArc")])]}),"instanceName":"7"});
            var Q45;
            Q45=makeQuery(id+"F6.opPattern","COPY",BODY,{"derivedFrom":makeQuery(id+"F5.opExtrude","SWEPT_BODY",BODY,{"disambiguationData":[OSD([sQuery(id+"F4.wireOp",EDGE,"E79.0.MirrorC")])]}),"instanceName":"7"});
            var Q46;
            Q46=makeQuery(id+"F6.opPattern","COPY",BODY,{"derivedFrom":makeQuery(id+"F5.opExtrude","SWEPT_BODY",BODY,{"disambiguationData":[OSD([sQuery(id+"F4.wireOp",EDGE,"E80.0.MirrorC"),sQuery(id+"F4.wireOp",EDGE,"E89")])]}),"instanceName":"7"});
            var Q47;
            Q47=makeQuery(id+"F6.opPattern","COPY",BODY,{"derivedFrom":makeQuery(id+"F5.opExtrude","SWEPT_BODY",BODY,{"disambiguationData":[OSD([sQuery(id+"F4.wireOp",EDGE,"E81.0.MirrorCS"),sQuery(id+"F4.wireOp",EDGE,"E82.0.MirrorCS"),sQuery(id+"F4.wireOp",EDGE,"E83.0.MirrorCS"),sQuery(id+"F4.wireOp",EDGE,"E84.0.MirrorCS"),sQuery(id+"F4.wireOp",EDGE,"E85.0.MirrorCS"),sQuery(id+"F4.wireOp",EDGE,"E86.0.MirrorCS"),sQuery(id+"F4.wireOp",EDGE,"E87.0.MirrorCS")])]}),"instanceName":"7"});
            var Q48;
            Q48=makeQuery(id+"F6.opPattern","COPY",BODY,{"derivedFrom":makeQuery(id+"F5.opExtrude","SWEPT_BODY",BODY,{"disambiguationData":[OSD([sQuery(id+"F4.wireOp",EDGE,"E69")])]}),"instanceName":"8"});
            var Q49;
            Q49=makeQuery(id+"F6.opPattern","COPY",BODY,{"derivedFrom":makeQuery(id+"F5.opExtrude","SWEPT_BODY",BODY,{"disambiguationData":[OSD([sQuery(id+"F4.wireOp",EDGE,"E70")])]}),"instanceName":"8"});
            var Q50;
            Q50=makeQuery(id+"F6.opPattern","COPY",BODY,{"derivedFrom":makeQuery(id+"F5.opExtrude","SWEPT_BODY",BODY,{"disambiguationData":[OSD([sQuery(id+"F4.wireOp",EDGE,"E71"),sQuery(id+"F4.wireOp",EDGE,"E72"),sQuery(id+"F4.wireOp",EDGE,"E74"),sQuery(id+"F4.wireOp",EDGE,"E75"),sQuery(id+"F4.wireOp",EDGE,"E76"),sQuery(id+"F4.wireOp",EDGE,"E77.filletArc"),sQuery(id+"F4.wireOp",EDGE,"E78.filletArc")])]}),"instanceName":"8"});
            var Q51;
            Q51=makeQuery(id+"F6.opPattern","COPY",BODY,{"derivedFrom":makeQuery(id+"F5.opExtrude","SWEPT_BODY",BODY,{"disambiguationData":[OSD([sQuery(id+"F4.wireOp",EDGE,"E79.0.MirrorC")])]}),"instanceName":"8"});
            var Q52;
            Q52=makeQuery(id+"F6.opPattern","COPY",BODY,{"derivedFrom":makeQuery(id+"F5.opExtrude","SWEPT_BODY",BODY,{"disambiguationData":[OSD([sQuery(id+"F4.wireOp",EDGE,"E80.0.MirrorC"),sQuery(id+"F4.wireOp",EDGE,"E89")])]}),"instanceName":"8"});
            var Q53;
            Q53=makeQuery(id+"F6.opPattern","COPY",BODY,{"derivedFrom":makeQuery(id+"F5.opExtrude","SWEPT_BODY",BODY,{"disambiguationData":[OSD([sQuery(id+"F4.wireOp",EDGE,"E81.0.MirrorCS"),sQuery(id+"F4.wireOp",EDGE,"E82.0.MirrorCS"),sQuery(id+"F4.wireOp",EDGE,"E83.0.MirrorCS"),sQuery(id+"F4.wireOp",EDGE,"E84.0.MirrorCS"),sQuery(id+"F4.wireOp",EDGE,"E85.0.MirrorCS"),sQuery(id+"F4.wireOp",EDGE,"E86.0.MirrorCS"),sQuery(id+"F4.wireOp",EDGE,"E87.0.MirrorCS")])]}),"instanceName":"8"});
            var Q54;
            Q54=makeQuery(id+"F6.opPattern","COPY",BODY,{"derivedFrom":makeQuery(id+"F5.opExtrude","SWEPT_BODY",BODY,{"disambiguationData":[OSD([sQuery(id+"F4.wireOp",EDGE,"E69")])]}),"instanceName":"9"});
            var Q55;
            Q55=makeQuery(id+"F6.opPattern","COPY",BODY,{"derivedFrom":makeQuery(id+"F5.opExtrude","SWEPT_BODY",BODY,{"disambiguationData":[OSD([sQuery(id+"F4.wireOp",EDGE,"E70")])]}),"instanceName":"9"});
            var Q56;
            Q56=makeQuery(id+"F6.opPattern","COPY",BODY,{"derivedFrom":makeQuery(id+"F5.opExtrude","SWEPT_BODY",BODY,{"disambiguationData":[OSD([sQuery(id+"F4.wireOp",EDGE,"E71"),sQuery(id+"F4.wireOp",EDGE,"E72"),sQuery(id+"F4.wireOp",EDGE,"E74"),sQuery(id+"F4.wireOp",EDGE,"E75"),sQuery(id+"F4.wireOp",EDGE,"E76"),sQuery(id+"F4.wireOp",EDGE,"E77.filletArc"),sQuery(id+"F4.wireOp",EDGE,"E78.filletArc")])]}),"instanceName":"9"});
            var Q57;
            Q57=makeQuery(id+"F6.opPattern","COPY",BODY,{"derivedFrom":makeQuery(id+"F5.opExtrude","SWEPT_BODY",BODY,{"disambiguationData":[OSD([sQuery(id+"F4.wireOp",EDGE,"E79.0.MirrorC")])]}),"instanceName":"9"});
            var Q58;
            Q58=makeQuery(id+"F6.opPattern","COPY",BODY,{"derivedFrom":makeQuery(id+"F5.opExtrude","SWEPT_BODY",BODY,{"disambiguationData":[OSD([sQuery(id+"F4.wireOp",EDGE,"E80.0.MirrorC"),sQuery(id+"F4.wireOp",EDGE,"E89")])]}),"instanceName":"9"});
            var Q59;
            Q59=makeQuery(id+"F6.opPattern","COPY",BODY,{"derivedFrom":makeQuery(id+"F5.opExtrude","SWEPT_BODY",BODY,{"disambiguationData":[OSD([sQuery(id+"F4.wireOp",EDGE,"E81.0.MirrorCS"),sQuery(id+"F4.wireOp",EDGE,"E82.0.MirrorCS"),sQuery(id+"F4.wireOp",EDGE,"E83.0.MirrorCS"),sQuery(id+"F4.wireOp",EDGE,"E84.0.MirrorCS"),sQuery(id+"F4.wireOp",EDGE,"E85.0.MirrorCS"),sQuery(id+"F4.wireOp",EDGE,"E86.0.MirrorCS"),sQuery(id+"F4.wireOp",EDGE,"E87.0.MirrorCS")])]}),"instanceName":"9"});
            var Q60;
            Q60=makeQuery(id+"F6.opPattern","COPY",BODY,{"derivedFrom":makeQuery(id+"F5.opExtrude","SWEPT_BODY",BODY,{"disambiguationData":[OSD([sQuery(id+"F4.wireOp",EDGE,"E69")])]}),"instanceName":"10"});
            var Q61;
            Q61=makeQuery(id+"F6.opPattern","COPY",BODY,{"derivedFrom":makeQuery(id+"F5.opExtrude","SWEPT_BODY",BODY,{"disambiguationData":[OSD([sQuery(id+"F4.wireOp",EDGE,"E70")])]}),"instanceName":"10"});
            var Q62;
            Q62=makeQuery(id+"F6.opPattern","COPY",BODY,{"derivedFrom":makeQuery(id+"F5.opExtrude","SWEPT_BODY",BODY,{"disambiguationData":[OSD([sQuery(id+"F4.wireOp",EDGE,"E71"),sQuery(id+"F4.wireOp",EDGE,"E72"),sQuery(id+"F4.wireOp",EDGE,"E74"),sQuery(id+"F4.wireOp",EDGE,"E75"),sQuery(id+"F4.wireOp",EDGE,"E76"),sQuery(id+"F4.wireOp",EDGE,"E77.filletArc"),sQuery(id+"F4.wireOp",EDGE,"E78.filletArc")])]}),"instanceName":"10"});
            var Q63;
            Q63=makeQuery(id+"F6.opPattern","COPY",BODY,{"derivedFrom":makeQuery(id+"F5.opExtrude","SWEPT_BODY",BODY,{"disambiguationData":[OSD([sQuery(id+"F4.wireOp",EDGE,"E79.0.MirrorC")])]}),"instanceName":"10"});
            var Q64;
            Q64=makeQuery(id+"F6.opPattern","COPY",BODY,{"derivedFrom":makeQuery(id+"F5.opExtrude","SWEPT_BODY",BODY,{"disambiguationData":[OSD([sQuery(id+"F4.wireOp",EDGE,"E80.0.MirrorC"),sQuery(id+"F4.wireOp",EDGE,"E89")])]}),"instanceName":"10"});
            var Q65;
            Q65=makeQuery(id+"F6.opPattern","COPY",BODY,{"derivedFrom":makeQuery(id+"F5.opExtrude","SWEPT_BODY",BODY,{"disambiguationData":[OSD([sQuery(id+"F4.wireOp",EDGE,"E81.0.MirrorCS"),sQuery(id+"F4.wireOp",EDGE,"E82.0.MirrorCS"),sQuery(id+"F4.wireOp",EDGE,"E83.0.MirrorCS"),sQuery(id+"F4.wireOp",EDGE,"E84.0.MirrorCS"),sQuery(id+"F4.wireOp",EDGE,"E85.0.MirrorCS"),sQuery(id+"F4.wireOp",EDGE,"E86.0.MirrorCS"),sQuery(id+"F4.wireOp",EDGE,"E87.0.MirrorCS")])]}),"instanceName":"10"});
            var Q66;
            Q66=makeQuery(id+"F6.opPattern","COPY",BODY,{"derivedFrom":makeQuery(id+"F5.opExtrude","SWEPT_BODY",BODY,{"disambiguationData":[OSD([sQuery(id+"F4.wireOp",EDGE,"E69")])]}),"instanceName":"11"});
            var Q67;
            Q67=makeQuery(id+"F6.opPattern","COPY",BODY,{"derivedFrom":makeQuery(id+"F5.opExtrude","SWEPT_BODY",BODY,{"disambiguationData":[OSD([sQuery(id+"F4.wireOp",EDGE,"E70")])]}),"instanceName":"11"});
            var Q68;
            Q68=makeQuery(id+"F6.opPattern","COPY",BODY,{"derivedFrom":makeQuery(id+"F5.opExtrude","SWEPT_BODY",BODY,{"disambiguationData":[OSD([sQuery(id+"F4.wireOp",EDGE,"E71"),sQuery(id+"F4.wireOp",EDGE,"E72"),sQuery(id+"F4.wireOp",EDGE,"E74"),sQuery(id+"F4.wireOp",EDGE,"E75"),sQuery(id+"F4.wireOp",EDGE,"E76"),sQuery(id+"F4.wireOp",EDGE,"E77.filletArc"),sQuery(id+"F4.wireOp",EDGE,"E78.filletArc")])]}),"instanceName":"11"});
            var Q69;
            Q69=makeQuery(id+"F6.opPattern","COPY",BODY,{"derivedFrom":makeQuery(id+"F5.opExtrude","SWEPT_BODY",BODY,{"disambiguationData":[OSD([sQuery(id+"F4.wireOp",EDGE,"E79.0.MirrorC")])]}),"instanceName":"11"});
            var Q70;
            Q70=makeQuery(id+"F6.opPattern","COPY",BODY,{"derivedFrom":makeQuery(id+"F5.opExtrude","SWEPT_BODY",BODY,{"disambiguationData":[OSD([sQuery(id+"F4.wireOp",EDGE,"E80.0.MirrorC"),sQuery(id+"F4.wireOp",EDGE,"E89")])]}),"instanceName":"11"});
            var Q71;
            Q71=makeQuery(id+"F6.opPattern","COPY",BODY,{"derivedFrom":makeQuery(id+"F5.opExtrude","SWEPT_BODY",BODY,{"disambiguationData":[OSD([sQuery(id+"F4.wireOp",EDGE,"E81.0.MirrorCS"),sQuery(id+"F4.wireOp",EDGE,"E82.0.MirrorCS"),sQuery(id+"F4.wireOp",EDGE,"E83.0.MirrorCS"),sQuery(id+"F4.wireOp",EDGE,"E84.0.MirrorCS"),sQuery(id+"F4.wireOp",EDGE,"E85.0.MirrorCS"),sQuery(id+"F4.wireOp",EDGE,"E86.0.MirrorCS"),sQuery(id+"F4.wireOp",EDGE,"E87.0.MirrorCS")])]}),"instanceName":"11"});
            var Q72;
            Q72=makeQuery(id+"F6.opPattern","COPY",BODY,{"derivedFrom":makeQuery(id+"F5.opExtrude","SWEPT_BODY",BODY,{"disambiguationData":[OSD([sQuery(id+"F4.wireOp",EDGE,"E69")])]}),"instanceName":"12"});
            var Q73;
            Q73=makeQuery(id+"F6.opPattern","COPY",BODY,{"derivedFrom":makeQuery(id+"F5.opExtrude","SWEPT_BODY",BODY,{"disambiguationData":[OSD([sQuery(id+"F4.wireOp",EDGE,"E70")])]}),"instanceName":"12"});
            var Q74;
            Q74=makeQuery(id+"F6.opPattern","COPY",BODY,{"derivedFrom":makeQuery(id+"F5.opExtrude","SWEPT_BODY",BODY,{"disambiguationData":[OSD([sQuery(id+"F4.wireOp",EDGE,"E71"),sQuery(id+"F4.wireOp",EDGE,"E72"),sQuery(id+"F4.wireOp",EDGE,"E74"),sQuery(id+"F4.wireOp",EDGE,"E75"),sQuery(id+"F4.wireOp",EDGE,"E76"),sQuery(id+"F4.wireOp",EDGE,"E77.filletArc"),sQuery(id+"F4.wireOp",EDGE,"E78.filletArc")])]}),"instanceName":"12"});
            var Q75;
            Q75=makeQuery(id+"F6.opPattern","COPY",BODY,{"derivedFrom":makeQuery(id+"F5.opExtrude","SWEPT_BODY",BODY,{"disambiguationData":[OSD([sQuery(id+"F4.wireOp",EDGE,"E79.0.MirrorC")])]}),"instanceName":"12"});
            var Q76;
            Q76=makeQuery(id+"F6.opPattern","COPY",BODY,{"derivedFrom":makeQuery(id+"F5.opExtrude","SWEPT_BODY",BODY,{"disambiguationData":[OSD([sQuery(id+"F4.wireOp",EDGE,"E80.0.MirrorC"),sQuery(id+"F4.wireOp",EDGE,"E89")])]}),"instanceName":"12"});
            var Q77;
            Q77=makeQuery(id+"F6.opPattern","COPY",BODY,{"derivedFrom":makeQuery(id+"F5.opExtrude","SWEPT_BODY",BODY,{"disambiguationData":[OSD([sQuery(id+"F4.wireOp",EDGE,"E81.0.MirrorCS"),sQuery(id+"F4.wireOp",EDGE,"E82.0.MirrorCS"),sQuery(id+"F4.wireOp",EDGE,"E83.0.MirrorCS"),sQuery(id+"F4.wireOp",EDGE,"E84.0.MirrorCS"),sQuery(id+"F4.wireOp",EDGE,"E85.0.MirrorCS"),sQuery(id+"F4.wireOp",EDGE,"E86.0.MirrorCS"),sQuery(id+"F4.wireOp",EDGE,"E87.0.MirrorCS")])]}),"instanceName":"12"});
            var Q78;
            Q78=makeQuery(id+"F6.opPattern","COPY",BODY,{"derivedFrom":makeQuery(id+"F5.opExtrude","SWEPT_BODY",BODY,{"disambiguationData":[OSD([sQuery(id+"F4.wireOp",EDGE,"E69")])]}),"instanceName":"13"});
            var Q79;
            Q79=makeQuery(id+"F6.opPattern","COPY",BODY,{"derivedFrom":makeQuery(id+"F5.opExtrude","SWEPT_BODY",BODY,{"disambiguationData":[OSD([sQuery(id+"F4.wireOp",EDGE,"E70")])]}),"instanceName":"13"});
            var Q80;
            Q80=makeQuery(id+"F6.opPattern","COPY",BODY,{"derivedFrom":makeQuery(id+"F5.opExtrude","SWEPT_BODY",BODY,{"disambiguationData":[OSD([sQuery(id+"F4.wireOp",EDGE,"E71"),sQuery(id+"F4.wireOp",EDGE,"E72"),sQuery(id+"F4.wireOp",EDGE,"E74"),sQuery(id+"F4.wireOp",EDGE,"E75"),sQuery(id+"F4.wireOp",EDGE,"E76"),sQuery(id+"F4.wireOp",EDGE,"E77.filletArc"),sQuery(id+"F4.wireOp",EDGE,"E78.filletArc")])]}),"instanceName":"13"});
            var Q81;
            Q81=makeQuery(id+"F6.opPattern","COPY",BODY,{"derivedFrom":makeQuery(id+"F5.opExtrude","SWEPT_BODY",BODY,{"disambiguationData":[OSD([sQuery(id+"F4.wireOp",EDGE,"E79.0.MirrorC")])]}),"instanceName":"13"});
            var Q82;
            Q82=makeQuery(id+"F6.opPattern","COPY",BODY,{"derivedFrom":makeQuery(id+"F5.opExtrude","SWEPT_BODY",BODY,{"disambiguationData":[OSD([sQuery(id+"F4.wireOp",EDGE,"E80.0.MirrorC"),sQuery(id+"F4.wireOp",EDGE,"E89")])]}),"instanceName":"13"});
            var Q83;
            Q83=makeQuery(id+"F6.opPattern","COPY",BODY,{"derivedFrom":makeQuery(id+"F5.opExtrude","SWEPT_BODY",BODY,{"disambiguationData":[OSD([sQuery(id+"F4.wireOp",EDGE,"E81.0.MirrorCS"),sQuery(id+"F4.wireOp",EDGE,"E82.0.MirrorCS"),sQuery(id+"F4.wireOp",EDGE,"E83.0.MirrorCS"),sQuery(id+"F4.wireOp",EDGE,"E84.0.MirrorCS"),sQuery(id+"F4.wireOp",EDGE,"E85.0.MirrorCS"),sQuery(id+"F4.wireOp",EDGE,"E86.0.MirrorCS"),sQuery(id+"F4.wireOp",EDGE,"E87.0.MirrorCS")])]}),"instanceName":"13"});
            var Q84;
            Q84=makeQuery(id+"F6.opPattern","COPY",BODY,{"derivedFrom":makeQuery(id+"F5.opExtrude","SWEPT_BODY",BODY,{"disambiguationData":[OSD([sQuery(id+"F4.wireOp",EDGE,"E69")])]}),"instanceName":"14"});
            var Q85;
            Q85=makeQuery(id+"F6.opPattern","COPY",BODY,{"derivedFrom":makeQuery(id+"F5.opExtrude","SWEPT_BODY",BODY,{"disambiguationData":[OSD([sQuery(id+"F4.wireOp",EDGE,"E70")])]}),"instanceName":"14"});
            var Q86;
            Q86=makeQuery(id+"F6.opPattern","COPY",BODY,{"derivedFrom":makeQuery(id+"F5.opExtrude","SWEPT_BODY",BODY,{"disambiguationData":[OSD([sQuery(id+"F4.wireOp",EDGE,"E71"),sQuery(id+"F4.wireOp",EDGE,"E72"),sQuery(id+"F4.wireOp",EDGE,"E74"),sQuery(id+"F4.wireOp",EDGE,"E75"),sQuery(id+"F4.wireOp",EDGE,"E76"),sQuery(id+"F4.wireOp",EDGE,"E77.filletArc"),sQuery(id+"F4.wireOp",EDGE,"E78.filletArc")])]}),"instanceName":"14"});
            var Q87;
            Q87=makeQuery(id+"F6.opPattern","COPY",BODY,{"derivedFrom":makeQuery(id+"F5.opExtrude","SWEPT_BODY",BODY,{"disambiguationData":[OSD([sQuery(id+"F4.wireOp",EDGE,"E79.0.MirrorC")])]}),"instanceName":"14"});
            var Q88;
            Q88=makeQuery(id+"F6.opPattern","COPY",BODY,{"derivedFrom":makeQuery(id+"F5.opExtrude","SWEPT_BODY",BODY,{"disambiguationData":[OSD([sQuery(id+"F4.wireOp",EDGE,"E80.0.MirrorC"),sQuery(id+"F4.wireOp",EDGE,"E89")])]}),"instanceName":"14"});
            var Q89;
            Q89=makeQuery(id+"F6.opPattern","COPY",BODY,{"derivedFrom":makeQuery(id+"F5.opExtrude","SWEPT_BODY",BODY,{"disambiguationData":[OSD([sQuery(id+"F4.wireOp",EDGE,"E81.0.MirrorCS"),sQuery(id+"F4.wireOp",EDGE,"E82.0.MirrorCS"),sQuery(id+"F4.wireOp",EDGE,"E83.0.MirrorCS"),sQuery(id+"F4.wireOp",EDGE,"E84.0.MirrorCS"),sQuery(id+"F4.wireOp",EDGE,"E85.0.MirrorCS"),sQuery(id+"F4.wireOp",EDGE,"E86.0.MirrorCS"),sQuery(id+"F4.wireOp",EDGE,"E87.0.MirrorCS")])]}),"instanceName":"14"});
            var Q90;
            Q90=makeQuery(id+"F6.opPattern","COPY",BODY,{"derivedFrom":makeQuery(id+"F5.opExtrude","SWEPT_BODY",BODY,{"disambiguationData":[OSD([sQuery(id+"F4.wireOp",EDGE,"E69")])]}),"instanceName":"15"});
            var Q91;
            Q91=makeQuery(id+"F6.opPattern","COPY",BODY,{"derivedFrom":makeQuery(id+"F5.opExtrude","SWEPT_BODY",BODY,{"disambiguationData":[OSD([sQuery(id+"F4.wireOp",EDGE,"E70")])]}),"instanceName":"15"});
            var Q92;
            Q92=makeQuery(id+"F6.opPattern","COPY",BODY,{"derivedFrom":makeQuery(id+"F5.opExtrude","SWEPT_BODY",BODY,{"disambiguationData":[OSD([sQuery(id+"F4.wireOp",EDGE,"E71"),sQuery(id+"F4.wireOp",EDGE,"E72"),sQuery(id+"F4.wireOp",EDGE,"E74"),sQuery(id+"F4.wireOp",EDGE,"E75"),sQuery(id+"F4.wireOp",EDGE,"E76"),sQuery(id+"F4.wireOp",EDGE,"E77.filletArc"),sQuery(id+"F4.wireOp",EDGE,"E78.filletArc")])]}),"instanceName":"15"});
            var Q93;
            Q93=makeQuery(id+"F6.opPattern","COPY",BODY,{"derivedFrom":makeQuery(id+"F5.opExtrude","SWEPT_BODY",BODY,{"disambiguationData":[OSD([sQuery(id+"F4.wireOp",EDGE,"E79.0.MirrorC")])]}),"instanceName":"15"});
            var Q94;
            Q94=makeQuery(id+"F6.opPattern","COPY",BODY,{"derivedFrom":makeQuery(id+"F5.opExtrude","SWEPT_BODY",BODY,{"disambiguationData":[OSD([sQuery(id+"F4.wireOp",EDGE,"E80.0.MirrorC"),sQuery(id+"F4.wireOp",EDGE,"E89")])]}),"instanceName":"15"});
            var Q95;
            Q95=makeQuery(id+"F6.opPattern","COPY",BODY,{"derivedFrom":makeQuery(id+"F5.opExtrude","SWEPT_BODY",BODY,{"disambiguationData":[OSD([sQuery(id+"F4.wireOp",EDGE,"E81.0.MirrorCS"),sQuery(id+"F4.wireOp",EDGE,"E82.0.MirrorCS"),sQuery(id+"F4.wireOp",EDGE,"E83.0.MirrorCS"),sQuery(id+"F4.wireOp",EDGE,"E84.0.MirrorCS"),sQuery(id+"F4.wireOp",EDGE,"E85.0.MirrorCS"),sQuery(id+"F4.wireOp",EDGE,"E86.0.MirrorCS"),sQuery(id+"F4.wireOp",EDGE,"E87.0.MirrorCS")])]}),"instanceName":"15"});
            var Q96;
            Q96=makeQuery(id+"F6.opPattern","COPY",BODY,{"derivedFrom":makeQuery(id+"F5.opExtrude","SWEPT_BODY",BODY,{"disambiguationData":[OSD([sQuery(id+"F4.wireOp",EDGE,"E69")])]}),"instanceName":"16"});
            var Q97;
            Q97=makeQuery(id+"F6.opPattern","COPY",BODY,{"derivedFrom":makeQuery(id+"F5.opExtrude","SWEPT_BODY",BODY,{"disambiguationData":[OSD([sQuery(id+"F4.wireOp",EDGE,"E70")])]}),"instanceName":"16"});
            var Q98;
            Q98=makeQuery(id+"F6.opPattern","COPY",BODY,{"derivedFrom":makeQuery(id+"F5.opExtrude","SWEPT_BODY",BODY,{"disambiguationData":[OSD([sQuery(id+"F4.wireOp",EDGE,"E71"),sQuery(id+"F4.wireOp",EDGE,"E72"),sQuery(id+"F4.wireOp",EDGE,"E74"),sQuery(id+"F4.wireOp",EDGE,"E75"),sQuery(id+"F4.wireOp",EDGE,"E76"),sQuery(id+"F4.wireOp",EDGE,"E77.filletArc"),sQuery(id+"F4.wireOp",EDGE,"E78.filletArc")])]}),"instanceName":"16"});
            var Q99;
            Q99=makeQuery(id+"F6.opPattern","COPY",BODY,{"derivedFrom":makeQuery(id+"F5.opExtrude","SWEPT_BODY",BODY,{"disambiguationData":[OSD([sQuery(id+"F4.wireOp",EDGE,"E79.0.MirrorC")])]}),"instanceName":"16"});
            var Q100;
            Q100=makeQuery(id+"F6.opPattern","COPY",BODY,{"derivedFrom":makeQuery(id+"F5.opExtrude","SWEPT_BODY",BODY,{"disambiguationData":[OSD([sQuery(id+"F4.wireOp",EDGE,"E80.0.MirrorC"),sQuery(id+"F4.wireOp",EDGE,"E89")])]}),"instanceName":"16"});
            var Q101;
            Q101=makeQuery(id+"F6.opPattern","COPY",BODY,{"derivedFrom":makeQuery(id+"F5.opExtrude","SWEPT_BODY",BODY,{"disambiguationData":[OSD([sQuery(id+"F4.wireOp",EDGE,"E81.0.MirrorCS"),sQuery(id+"F4.wireOp",EDGE,"E82.0.MirrorCS"),sQuery(id+"F4.wireOp",EDGE,"E83.0.MirrorCS"),sQuery(id+"F4.wireOp",EDGE,"E84.0.MirrorCS"),sQuery(id+"F4.wireOp",EDGE,"E85.0.MirrorCS"),sQuery(id+"F4.wireOp",EDGE,"E86.0.MirrorCS"),sQuery(id+"F4.wireOp",EDGE,"E87.0.MirrorCS")])]}),"instanceName":"16"});
            var Q102;
            Q102=makeQuery(id+"F6.opPattern","COPY",BODY,{"derivedFrom":makeQuery(id+"F5.opExtrude","SWEPT_BODY",BODY,{"disambiguationData":[OSD([sQuery(id+"F4.wireOp",EDGE,"E69")])]}),"instanceName":"17"});
            var Q103;
            Q103=makeQuery(id+"F6.opPattern","COPY",BODY,{"derivedFrom":makeQuery(id+"F5.opExtrude","SWEPT_BODY",BODY,{"disambiguationData":[OSD([sQuery(id+"F4.wireOp",EDGE,"E70")])]}),"instanceName":"17"});
            var Q104;
            Q104=makeQuery(id+"F6.opPattern","COPY",BODY,{"derivedFrom":makeQuery(id+"F5.opExtrude","SWEPT_BODY",BODY,{"disambiguationData":[OSD([sQuery(id+"F4.wireOp",EDGE,"E71"),sQuery(id+"F4.wireOp",EDGE,"E72"),sQuery(id+"F4.wireOp",EDGE,"E74"),sQuery(id+"F4.wireOp",EDGE,"E75"),sQuery(id+"F4.wireOp",EDGE,"E76"),sQuery(id+"F4.wireOp",EDGE,"E77.filletArc"),sQuery(id+"F4.wireOp",EDGE,"E78.filletArc")])]}),"instanceName":"17"});
            var Q105;
            Q105=makeQuery(id+"F6.opPattern","COPY",BODY,{"derivedFrom":makeQuery(id+"F5.opExtrude","SWEPT_BODY",BODY,{"disambiguationData":[OSD([sQuery(id+"F4.wireOp",EDGE,"E79.0.MirrorC")])]}),"instanceName":"17"});
            var Q106;
            Q106=makeQuery(id+"F6.opPattern","COPY",BODY,{"derivedFrom":makeQuery(id+"F5.opExtrude","SWEPT_BODY",BODY,{"disambiguationData":[OSD([sQuery(id+"F4.wireOp",EDGE,"E80.0.MirrorC"),sQuery(id+"F4.wireOp",EDGE,"E89")])]}),"instanceName":"17"});
            var Q107;
            Q107=makeQuery(id+"F6.opPattern","COPY",BODY,{"derivedFrom":makeQuery(id+"F5.opExtrude","SWEPT_BODY",BODY,{"disambiguationData":[OSD([sQuery(id+"F4.wireOp",EDGE,"E81.0.MirrorCS"),sQuery(id+"F4.wireOp",EDGE,"E82.0.MirrorCS"),sQuery(id+"F4.wireOp",EDGE,"E83.0.MirrorCS"),sQuery(id+"F4.wireOp",EDGE,"E84.0.MirrorCS"),sQuery(id+"F4.wireOp",EDGE,"E85.0.MirrorCS"),sQuery(id+"F4.wireOp",EDGE,"E86.0.MirrorCS"),sQuery(id+"F4.wireOp",EDGE,"E87.0.MirrorCS")])]}),"instanceName":"17"});
            var Q108;
            Q108=makeQuery(id+"F6.opPattern","COPY",BODY,{"derivedFrom":makeQuery(id+"F5.opExtrude","SWEPT_BODY",BODY,{"disambiguationData":[OSD([sQuery(id+"F4.wireOp",EDGE,"E69")])]}),"instanceName":"18"});
            var Q109;
            Q109=makeQuery(id+"F6.opPattern","COPY",BODY,{"derivedFrom":makeQuery(id+"F5.opExtrude","SWEPT_BODY",BODY,{"disambiguationData":[OSD([sQuery(id+"F4.wireOp",EDGE,"E70")])]}),"instanceName":"18"});
            var Q110;
            Q110=makeQuery(id+"F6.opPattern","COPY",BODY,{"derivedFrom":makeQuery(id+"F5.opExtrude","SWEPT_BODY",BODY,{"disambiguationData":[OSD([sQuery(id+"F4.wireOp",EDGE,"E71"),sQuery(id+"F4.wireOp",EDGE,"E72"),sQuery(id+"F4.wireOp",EDGE,"E74"),sQuery(id+"F4.wireOp",EDGE,"E75"),sQuery(id+"F4.wireOp",EDGE,"E76"),sQuery(id+"F4.wireOp",EDGE,"E77.filletArc"),sQuery(id+"F4.wireOp",EDGE,"E78.filletArc")])]}),"instanceName":"18"});
            var Q111;
            Q111=makeQuery(id+"F6.opPattern","COPY",BODY,{"derivedFrom":makeQuery(id+"F5.opExtrude","SWEPT_BODY",BODY,{"disambiguationData":[OSD([sQuery(id+"F4.wireOp",EDGE,"E79.0.MirrorC")])]}),"instanceName":"18"});
            var Q112;
            Q112=makeQuery(id+"F6.opPattern","COPY",BODY,{"derivedFrom":makeQuery(id+"F5.opExtrude","SWEPT_BODY",BODY,{"disambiguationData":[OSD([sQuery(id+"F4.wireOp",EDGE,"E80.0.MirrorC"),sQuery(id+"F4.wireOp",EDGE,"E89")])]}),"instanceName":"18"});
            var Q113;
            Q113=makeQuery(id+"F6.opPattern","COPY",BODY,{"derivedFrom":makeQuery(id+"F5.opExtrude","SWEPT_BODY",BODY,{"disambiguationData":[OSD([sQuery(id+"F4.wireOp",EDGE,"E81.0.MirrorCS"),sQuery(id+"F4.wireOp",EDGE,"E82.0.MirrorCS"),sQuery(id+"F4.wireOp",EDGE,"E83.0.MirrorCS"),sQuery(id+"F4.wireOp",EDGE,"E84.0.MirrorCS"),sQuery(id+"F4.wireOp",EDGE,"E85.0.MirrorCS"),sQuery(id+"F4.wireOp",EDGE,"E86.0.MirrorCS"),sQuery(id+"F4.wireOp",EDGE,"E87.0.MirrorCS")])]}),"instanceName":"18"});
            var Q114;
            Q114=makeQuery(id+"F6.opPattern","COPY",BODY,{"derivedFrom":makeQuery(id+"F5.opExtrude","SWEPT_BODY",BODY,{"disambiguationData":[OSD([sQuery(id+"F4.wireOp",EDGE,"E69")])]}),"instanceName":"19"});
            var Q115;
            Q115=makeQuery(id+"F6.opPattern","COPY",BODY,{"derivedFrom":makeQuery(id+"F5.opExtrude","SWEPT_BODY",BODY,{"disambiguationData":[OSD([sQuery(id+"F4.wireOp",EDGE,"E70")])]}),"instanceName":"19"});
            var Q116;
            Q116=makeQuery(id+"F6.opPattern","COPY",BODY,{"derivedFrom":makeQuery(id+"F5.opExtrude","SWEPT_BODY",BODY,{"disambiguationData":[OSD([sQuery(id+"F4.wireOp",EDGE,"E71"),sQuery(id+"F4.wireOp",EDGE,"E72"),sQuery(id+"F4.wireOp",EDGE,"E74"),sQuery(id+"F4.wireOp",EDGE,"E75"),sQuery(id+"F4.wireOp",EDGE,"E76"),sQuery(id+"F4.wireOp",EDGE,"E77.filletArc"),sQuery(id+"F4.wireOp",EDGE,"E78.filletArc")])]}),"instanceName":"19"});
            var Q117;
            Q117=makeQuery(id+"F6.opPattern","COPY",BODY,{"derivedFrom":makeQuery(id+"F5.opExtrude","SWEPT_BODY",BODY,{"disambiguationData":[OSD([sQuery(id+"F4.wireOp",EDGE,"E79.0.MirrorC")])]}),"instanceName":"19"});
            var Q118;
            Q118=makeQuery(id+"F6.opPattern","COPY",BODY,{"derivedFrom":makeQuery(id+"F5.opExtrude","SWEPT_BODY",BODY,{"disambiguationData":[OSD([sQuery(id+"F4.wireOp",EDGE,"E80.0.MirrorC"),sQuery(id+"F4.wireOp",EDGE,"E89")])]}),"instanceName":"19"});
            var Q119;
            Q119=makeQuery(id+"F6.opPattern","COPY",BODY,{"derivedFrom":makeQuery(id+"F5.opExtrude","SWEPT_BODY",BODY,{"disambiguationData":[OSD([sQuery(id+"F4.wireOp",EDGE,"E81.0.MirrorCS"),sQuery(id+"F4.wireOp",EDGE,"E82.0.MirrorCS"),sQuery(id+"F4.wireOp",EDGE,"E83.0.MirrorCS"),sQuery(id+"F4.wireOp",EDGE,"E84.0.MirrorCS"),sQuery(id+"F4.wireOp",EDGE,"E85.0.MirrorCS"),sQuery(id+"F4.wireOp",EDGE,"E86.0.MirrorCS"),sQuery(id+"F4.wireOp",EDGE,"E87.0.MirrorCS")])]}),"instanceName":"19"});
            var Q120;
            Q120=makeQuery(id+"F6.opPattern","COPY",BODY,{"derivedFrom":makeQuery(id+"F5.opExtrude","SWEPT_BODY",BODY,{"disambiguationData":[OSD([sQuery(id+"F4.wireOp",EDGE,"E69")])]}),"instanceName":"20"});
            var Q121;
            Q121=makeQuery(id+"F6.opPattern","COPY",BODY,{"derivedFrom":makeQuery(id+"F5.opExtrude","SWEPT_BODY",BODY,{"disambiguationData":[OSD([sQuery(id+"F4.wireOp",EDGE,"E70")])]}),"instanceName":"20"});
            var Q122;
            Q122=makeQuery(id+"F6.opPattern","COPY",BODY,{"derivedFrom":makeQuery(id+"F5.opExtrude","SWEPT_BODY",BODY,{"disambiguationData":[OSD([sQuery(id+"F4.wireOp",EDGE,"E71"),sQuery(id+"F4.wireOp",EDGE,"E72"),sQuery(id+"F4.wireOp",EDGE,"E74"),sQuery(id+"F4.wireOp",EDGE,"E75"),sQuery(id+"F4.wireOp",EDGE,"E76"),sQuery(id+"F4.wireOp",EDGE,"E77.filletArc"),sQuery(id+"F4.wireOp",EDGE,"E78.filletArc")])]}),"instanceName":"20"});
            var Q123;
            Q123=makeQuery(id+"F6.opPattern","COPY",BODY,{"derivedFrom":makeQuery(id+"F5.opExtrude","SWEPT_BODY",BODY,{"disambiguationData":[OSD([sQuery(id+"F4.wireOp",EDGE,"E79.0.MirrorC")])]}),"instanceName":"20"});
            var Q124;
            Q124=makeQuery(id+"F6.opPattern","COPY",BODY,{"derivedFrom":makeQuery(id+"F5.opExtrude","SWEPT_BODY",BODY,{"disambiguationData":[OSD([sQuery(id+"F4.wireOp",EDGE,"E80.0.MirrorC"),sQuery(id+"F4.wireOp",EDGE,"E89")])]}),"instanceName":"20"});
            var Q125;
            Q125=makeQuery(id+"F6.opPattern","COPY",BODY,{"derivedFrom":makeQuery(id+"F5.opExtrude","SWEPT_BODY",BODY,{"disambiguationData":[OSD([sQuery(id+"F4.wireOp",EDGE,"E81.0.MirrorCS"),sQuery(id+"F4.wireOp",EDGE,"E82.0.MirrorCS"),sQuery(id+"F4.wireOp",EDGE,"E83.0.MirrorCS"),sQuery(id+"F4.wireOp",EDGE,"E84.0.MirrorCS"),sQuery(id+"F4.wireOp",EDGE,"E85.0.MirrorCS"),sQuery(id+"F4.wireOp",EDGE,"E86.0.MirrorCS"),sQuery(id+"F4.wireOp",EDGE,"E87.0.MirrorCS")])]}),"instanceName":"20"});
            var Q126;
            Q126=makeQuery(id+"F6.opPattern","COPY",BODY,{"derivedFrom":makeQuery(id+"F5.opExtrude","SWEPT_BODY",BODY,{"disambiguationData":[OSD([sQuery(id+"F4.wireOp",EDGE,"E69")])]}),"instanceName":"21"});
            var Q127;
            Q127=makeQuery(id+"F6.opPattern","COPY",BODY,{"derivedFrom":makeQuery(id+"F5.opExtrude","SWEPT_BODY",BODY,{"disambiguationData":[OSD([sQuery(id+"F4.wireOp",EDGE,"E70")])]}),"instanceName":"21"});
            var Q128;
            Q128=makeQuery(id+"F6.opPattern","COPY",BODY,{"derivedFrom":makeQuery(id+"F5.opExtrude","SWEPT_BODY",BODY,{"disambiguationData":[OSD([sQuery(id+"F4.wireOp",EDGE,"E71"),sQuery(id+"F4.wireOp",EDGE,"E72"),sQuery(id+"F4.wireOp",EDGE,"E74"),sQuery(id+"F4.wireOp",EDGE,"E75"),sQuery(id+"F4.wireOp",EDGE,"E76"),sQuery(id+"F4.wireOp",EDGE,"E77.filletArc"),sQuery(id+"F4.wireOp",EDGE,"E78.filletArc")])]}),"instanceName":"21"});
            var Q129;
            Q129=makeQuery(id+"F6.opPattern","COPY",BODY,{"derivedFrom":makeQuery(id+"F5.opExtrude","SWEPT_BODY",BODY,{"disambiguationData":[OSD([sQuery(id+"F4.wireOp",EDGE,"E79.0.MirrorC")])]}),"instanceName":"21"});
            var Q130;
            Q130=makeQuery(id+"F6.opPattern","COPY",BODY,{"derivedFrom":makeQuery(id+"F5.opExtrude","SWEPT_BODY",BODY,{"disambiguationData":[OSD([sQuery(id+"F4.wireOp",EDGE,"E80.0.MirrorC"),sQuery(id+"F4.wireOp",EDGE,"E89")])]}),"instanceName":"21"});
            var Q131;
            Q131=makeQuery(id+"F6.opPattern","COPY",BODY,{"derivedFrom":makeQuery(id+"F5.opExtrude","SWEPT_BODY",BODY,{"disambiguationData":[OSD([sQuery(id+"F4.wireOp",EDGE,"E81.0.MirrorCS"),sQuery(id+"F4.wireOp",EDGE,"E82.0.MirrorCS"),sQuery(id+"F4.wireOp",EDGE,"E83.0.MirrorCS"),sQuery(id+"F4.wireOp",EDGE,"E84.0.MirrorCS"),sQuery(id+"F4.wireOp",EDGE,"E85.0.MirrorCS"),sQuery(id+"F4.wireOp",EDGE,"E86.0.MirrorCS"),sQuery(id+"F4.wireOp",EDGE,"E87.0.MirrorCS")])]}),"instanceName":"21"});
            var Q132;
            Q132=makeQuery(id+"F6.opPattern","COPY",BODY,{"derivedFrom":makeQuery(id+"F5.opExtrude","SWEPT_BODY",BODY,{"disambiguationData":[OSD([sQuery(id+"F4.wireOp",EDGE,"E69")])]}),"instanceName":"22"});
            var Q133;
            Q133=makeQuery(id+"F6.opPattern","COPY",BODY,{"derivedFrom":makeQuery(id+"F5.opExtrude","SWEPT_BODY",BODY,{"disambiguationData":[OSD([sQuery(id+"F4.wireOp",EDGE,"E70")])]}),"instanceName":"22"});
            var Q134;
            Q134=makeQuery(id+"F6.opPattern","COPY",BODY,{"derivedFrom":makeQuery(id+"F5.opExtrude","SWEPT_BODY",BODY,{"disambiguationData":[OSD([sQuery(id+"F4.wireOp",EDGE,"E71"),sQuery(id+"F4.wireOp",EDGE,"E72"),sQuery(id+"F4.wireOp",EDGE,"E74"),sQuery(id+"F4.wireOp",EDGE,"E75"),sQuery(id+"F4.wireOp",EDGE,"E76"),sQuery(id+"F4.wireOp",EDGE,"E77.filletArc"),sQuery(id+"F4.wireOp",EDGE,"E78.filletArc")])]}),"instanceName":"22"});
            var Q135;
            Q135=makeQuery(id+"F6.opPattern","COPY",BODY,{"derivedFrom":makeQuery(id+"F5.opExtrude","SWEPT_BODY",BODY,{"disambiguationData":[OSD([sQuery(id+"F4.wireOp",EDGE,"E79.0.MirrorC")])]}),"instanceName":"22"});
            var Q136;
            Q136=makeQuery(id+"F6.opPattern","COPY",BODY,{"derivedFrom":makeQuery(id+"F5.opExtrude","SWEPT_BODY",BODY,{"disambiguationData":[OSD([sQuery(id+"F4.wireOp",EDGE,"E80.0.MirrorC"),sQuery(id+"F4.wireOp",EDGE,"E89")])]}),"instanceName":"22"});
            var Q137;
            Q137=makeQuery(id+"F6.opPattern","COPY",BODY,{"derivedFrom":makeQuery(id+"F5.opExtrude","SWEPT_BODY",BODY,{"disambiguationData":[OSD([sQuery(id+"F4.wireOp",EDGE,"E81.0.MirrorCS"),sQuery(id+"F4.wireOp",EDGE,"E82.0.MirrorCS"),sQuery(id+"F4.wireOp",EDGE,"E83.0.MirrorCS"),sQuery(id+"F4.wireOp",EDGE,"E84.0.MirrorCS"),sQuery(id+"F4.wireOp",EDGE,"E85.0.MirrorCS"),sQuery(id+"F4.wireOp",EDGE,"E86.0.MirrorCS"),sQuery(id+"F4.wireOp",EDGE,"E87.0.MirrorCS")])]}),"instanceName":"22"});
            var Q138;
            Q138=makeQuery(id+"F6.opPattern","COPY",BODY,{"derivedFrom":makeQuery(id+"F5.opExtrude","SWEPT_BODY",BODY,{"disambiguationData":[OSD([sQuery(id+"F4.wireOp",EDGE,"E69")])]}),"instanceName":"23"});
            var Q139;
            Q139=makeQuery(id+"F6.opPattern","COPY",BODY,{"derivedFrom":makeQuery(id+"F5.opExtrude","SWEPT_BODY",BODY,{"disambiguationData":[OSD([sQuery(id+"F4.wireOp",EDGE,"E70")])]}),"instanceName":"23"});
            var Q140;
            Q140=makeQuery(id+"F6.opPattern","COPY",BODY,{"derivedFrom":makeQuery(id+"F5.opExtrude","SWEPT_BODY",BODY,{"disambiguationData":[OSD([sQuery(id+"F4.wireOp",EDGE,"E71"),sQuery(id+"F4.wireOp",EDGE,"E72"),sQuery(id+"F4.wireOp",EDGE,"E74"),sQuery(id+"F4.wireOp",EDGE,"E75"),sQuery(id+"F4.wireOp",EDGE,"E76"),sQuery(id+"F4.wireOp",EDGE,"E77.filletArc"),sQuery(id+"F4.wireOp",EDGE,"E78.filletArc")])]}),"instanceName":"23"});
            var Q141;
            Q141=makeQuery(id+"F6.opPattern","COPY",BODY,{"derivedFrom":makeQuery(id+"F5.opExtrude","SWEPT_BODY",BODY,{"disambiguationData":[OSD([sQuery(id+"F4.wireOp",EDGE,"E79.0.MirrorC")])]}),"instanceName":"23"});
            var Q142;
            Q142=makeQuery(id+"F6.opPattern","COPY",BODY,{"derivedFrom":makeQuery(id+"F5.opExtrude","SWEPT_BODY",BODY,{"disambiguationData":[OSD([sQuery(id+"F4.wireOp",EDGE,"E80.0.MirrorC"),sQuery(id+"F4.wireOp",EDGE,"E89")])]}),"instanceName":"23"});
            var Q143;
            Q143=makeQuery(id+"F6.opPattern","COPY",BODY,{"derivedFrom":makeQuery(id+"F5.opExtrude","SWEPT_BODY",BODY,{"disambiguationData":[OSD([sQuery(id+"F4.wireOp",EDGE,"E81.0.MirrorCS"),sQuery(id+"F4.wireOp",EDGE,"E82.0.MirrorCS"),sQuery(id+"F4.wireOp",EDGE,"E83.0.MirrorCS"),sQuery(id+"F4.wireOp",EDGE,"E84.0.MirrorCS"),sQuery(id+"F4.wireOp",EDGE,"E85.0.MirrorCS"),sQuery(id+"F4.wireOp",EDGE,"E86.0.MirrorCS"),sQuery(id+"F4.wireOp",EDGE,"E87.0.MirrorCS")])]}),"instanceName":"23"});
            var Q144;
            Q144=makeQuery(id+"F6.opPattern","COPY",BODY,{"derivedFrom":makeQuery(id+"F5.opExtrude","SWEPT_BODY",BODY,{"disambiguationData":[OSD([sQuery(id+"F4.wireOp",EDGE,"E69")])]}),"instanceName":"24"});
            var Q145;
            Q145=makeQuery(id+"F6.opPattern","COPY",BODY,{"derivedFrom":makeQuery(id+"F5.opExtrude","SWEPT_BODY",BODY,{"disambiguationData":[OSD([sQuery(id+"F4.wireOp",EDGE,"E70")])]}),"instanceName":"24"});
            var Q146;
            Q146=makeQuery(id+"F6.opPattern","COPY",BODY,{"derivedFrom":makeQuery(id+"F5.opExtrude","SWEPT_BODY",BODY,{"disambiguationData":[OSD([sQuery(id+"F4.wireOp",EDGE,"E71"),sQuery(id+"F4.wireOp",EDGE,"E72"),sQuery(id+"F4.wireOp",EDGE,"E74"),sQuery(id+"F4.wireOp",EDGE,"E75"),sQuery(id+"F4.wireOp",EDGE,"E76"),sQuery(id+"F4.wireOp",EDGE,"E77.filletArc"),sQuery(id+"F4.wireOp",EDGE,"E78.filletArc")])]}),"instanceName":"24"});
            var Q147;
            Q147=makeQuery(id+"F6.opPattern","COPY",BODY,{"derivedFrom":makeQuery(id+"F5.opExtrude","SWEPT_BODY",BODY,{"disambiguationData":[OSD([sQuery(id+"F4.wireOp",EDGE,"E79.0.MirrorC")])]}),"instanceName":"24"});
            var Q148;
            Q148=makeQuery(id+"F6.opPattern","COPY",BODY,{"derivedFrom":makeQuery(id+"F5.opExtrude","SWEPT_BODY",BODY,{"disambiguationData":[OSD([sQuery(id+"F4.wireOp",EDGE,"E80.0.MirrorC"),sQuery(id+"F4.wireOp",EDGE,"E89")])]}),"instanceName":"24"});
            var Q149;
            Q149=makeQuery(id+"F6.opPattern","COPY",BODY,{"derivedFrom":makeQuery(id+"F5.opExtrude","SWEPT_BODY",BODY,{"disambiguationData":[OSD([sQuery(id+"F4.wireOp",EDGE,"E81.0.MirrorCS"),sQuery(id+"F4.wireOp",EDGE,"E82.0.MirrorCS"),sQuery(id+"F4.wireOp",EDGE,"E83.0.MirrorCS"),sQuery(id+"F4.wireOp",EDGE,"E84.0.MirrorCS"),sQuery(id+"F4.wireOp",EDGE,"E85.0.MirrorCS"),sQuery(id+"F4.wireOp",EDGE,"E86.0.MirrorCS"),sQuery(id+"F4.wireOp",EDGE,"E87.0.MirrorCS")])]}),"instanceName":"24"});
            var Q150;
            Q150=makeQuery(id+"F6.opPattern","COPY",BODY,{"derivedFrom":makeQuery(id+"F5.opExtrude","SWEPT_BODY",BODY,{"disambiguationData":[OSD([sQuery(id+"F4.wireOp",EDGE,"E69")])]}),"instanceName":"25"});
            var Q151;
            Q151=makeQuery(id+"F6.opPattern","COPY",BODY,{"derivedFrom":makeQuery(id+"F5.opExtrude","SWEPT_BODY",BODY,{"disambiguationData":[OSD([sQuery(id+"F4.wireOp",EDGE,"E70")])]}),"instanceName":"25"});
            var Q152;
            Q152=makeQuery(id+"F6.opPattern","COPY",BODY,{"derivedFrom":makeQuery(id+"F5.opExtrude","SWEPT_BODY",BODY,{"disambiguationData":[OSD([sQuery(id+"F4.wireOp",EDGE,"E71"),sQuery(id+"F4.wireOp",EDGE,"E72"),sQuery(id+"F4.wireOp",EDGE,"E74"),sQuery(id+"F4.wireOp",EDGE,"E75"),sQuery(id+"F4.wireOp",EDGE,"E76"),sQuery(id+"F4.wireOp",EDGE,"E77.filletArc"),sQuery(id+"F4.wireOp",EDGE,"E78.filletArc")])]}),"instanceName":"25"});
            var Q153;
            Q153=makeQuery(id+"F6.opPattern","COPY",BODY,{"derivedFrom":makeQuery(id+"F5.opExtrude","SWEPT_BODY",BODY,{"disambiguationData":[OSD([sQuery(id+"F4.wireOp",EDGE,"E79.0.MirrorC")])]}),"instanceName":"25"});
            var Q154;
            Q154=makeQuery(id+"F6.opPattern","COPY",BODY,{"derivedFrom":makeQuery(id+"F5.opExtrude","SWEPT_BODY",BODY,{"disambiguationData":[OSD([sQuery(id+"F4.wireOp",EDGE,"E80.0.MirrorC"),sQuery(id+"F4.wireOp",EDGE,"E89")])]}),"instanceName":"25"});
            var Q155;
            Q155=makeQuery(id+"F6.opPattern","COPY",BODY,{"derivedFrom":makeQuery(id+"F5.opExtrude","SWEPT_BODY",BODY,{"disambiguationData":[OSD([sQuery(id+"F4.wireOp",EDGE,"E81.0.MirrorCS"),sQuery(id+"F4.wireOp",EDGE,"E82.0.MirrorCS"),sQuery(id+"F4.wireOp",EDGE,"E83.0.MirrorCS"),sQuery(id+"F4.wireOp",EDGE,"E84.0.MirrorCS"),sQuery(id+"F4.wireOp",EDGE,"E85.0.MirrorCS"),sQuery(id+"F4.wireOp",EDGE,"E86.0.MirrorCS"),sQuery(id+"F4.wireOp",EDGE,"E87.0.MirrorCS")])]}),"instanceName":"25"});
            var Q156;
            Q156=makeQuery(id+"F6.opPattern","COPY",BODY,{"derivedFrom":makeQuery(id+"F5.opExtrude","SWEPT_BODY",BODY,{"disambiguationData":[OSD([sQuery(id+"F4.wireOp",EDGE,"E69")])]}),"instanceName":"26"});
            var Q157;
            Q157=makeQuery(id+"F6.opPattern","COPY",BODY,{"derivedFrom":makeQuery(id+"F5.opExtrude","SWEPT_BODY",BODY,{"disambiguationData":[OSD([sQuery(id+"F4.wireOp",EDGE,"E70")])]}),"instanceName":"26"});
            var Q158;
            Q158=makeQuery(id+"F6.opPattern","COPY",BODY,{"derivedFrom":makeQuery(id+"F5.opExtrude","SWEPT_BODY",BODY,{"disambiguationData":[OSD([sQuery(id+"F4.wireOp",EDGE,"E71"),sQuery(id+"F4.wireOp",EDGE,"E72"),sQuery(id+"F4.wireOp",EDGE,"E74"),sQuery(id+"F4.wireOp",EDGE,"E75"),sQuery(id+"F4.wireOp",EDGE,"E76"),sQuery(id+"F4.wireOp",EDGE,"E77.filletArc"),sQuery(id+"F4.wireOp",EDGE,"E78.filletArc")])]}),"instanceName":"26"});
            var Q159;
            Q159=makeQuery(id+"F6.opPattern","COPY",BODY,{"derivedFrom":makeQuery(id+"F5.opExtrude","SWEPT_BODY",BODY,{"disambiguationData":[OSD([sQuery(id+"F4.wireOp",EDGE,"E79.0.MirrorC")])]}),"instanceName":"26"});
            var Q160;
            Q160=makeQuery(id+"F6.opPattern","COPY",BODY,{"derivedFrom":makeQuery(id+"F5.opExtrude","SWEPT_BODY",BODY,{"disambiguationData":[OSD([sQuery(id+"F4.wireOp",EDGE,"E80.0.MirrorC"),sQuery(id+"F4.wireOp",EDGE,"E89")])]}),"instanceName":"26"});
            var Q161;
            Q161=makeQuery(id+"F6.opPattern","COPY",BODY,{"derivedFrom":makeQuery(id+"F5.opExtrude","SWEPT_BODY",BODY,{"disambiguationData":[OSD([sQuery(id+"F4.wireOp",EDGE,"E81.0.MirrorCS"),sQuery(id+"F4.wireOp",EDGE,"E82.0.MirrorCS"),sQuery(id+"F4.wireOp",EDGE,"E83.0.MirrorCS"),sQuery(id+"F4.wireOp",EDGE,"E84.0.MirrorCS"),sQuery(id+"F4.wireOp",EDGE,"E85.0.MirrorCS"),sQuery(id+"F4.wireOp",EDGE,"E86.0.MirrorCS"),sQuery(id+"F4.wireOp",EDGE,"E87.0.MirrorCS")])]}),"instanceName":"26"});
            var Q162;
            Q162=makeQuery(id+"F6.opPattern","COPY",BODY,{"derivedFrom":makeQuery(id+"F5.opExtrude","SWEPT_BODY",BODY,{"disambiguationData":[OSD([sQuery(id+"F4.wireOp",EDGE,"E69")])]}),"instanceName":"27"});
            var Q163;
            Q163=makeQuery(id+"F6.opPattern","COPY",BODY,{"derivedFrom":makeQuery(id+"F5.opExtrude","SWEPT_BODY",BODY,{"disambiguationData":[OSD([sQuery(id+"F4.wireOp",EDGE,"E70")])]}),"instanceName":"27"});
            var Q164;
            Q164=makeQuery(id+"F6.opPattern","COPY",BODY,{"derivedFrom":makeQuery(id+"F5.opExtrude","SWEPT_BODY",BODY,{"disambiguationData":[OSD([sQuery(id+"F4.wireOp",EDGE,"E71"),sQuery(id+"F4.wireOp",EDGE,"E72"),sQuery(id+"F4.wireOp",EDGE,"E74"),sQuery(id+"F4.wireOp",EDGE,"E75"),sQuery(id+"F4.wireOp",EDGE,"E76"),sQuery(id+"F4.wireOp",EDGE,"E77.filletArc"),sQuery(id+"F4.wireOp",EDGE,"E78.filletArc")])]}),"instanceName":"27"});
            var Q165;
            Q165=makeQuery(id+"F6.opPattern","COPY",BODY,{"derivedFrom":makeQuery(id+"F5.opExtrude","SWEPT_BODY",BODY,{"disambiguationData":[OSD([sQuery(id+"F4.wireOp",EDGE,"E79.0.MirrorC")])]}),"instanceName":"27"});
            var Q166;
            Q166=makeQuery(id+"F6.opPattern","COPY",BODY,{"derivedFrom":makeQuery(id+"F5.opExtrude","SWEPT_BODY",BODY,{"disambiguationData":[OSD([sQuery(id+"F4.wireOp",EDGE,"E80.0.MirrorC"),sQuery(id+"F4.wireOp",EDGE,"E89")])]}),"instanceName":"27"});
            var Q167;
            Q167=makeQuery(id+"F6.opPattern","COPY",BODY,{"derivedFrom":makeQuery(id+"F5.opExtrude","SWEPT_BODY",BODY,{"disambiguationData":[OSD([sQuery(id+"F4.wireOp",EDGE,"E81.0.MirrorCS"),sQuery(id+"F4.wireOp",EDGE,"E82.0.MirrorCS"),sQuery(id+"F4.wireOp",EDGE,"E83.0.MirrorCS"),sQuery(id+"F4.wireOp",EDGE,"E84.0.MirrorCS"),sQuery(id+"F4.wireOp",EDGE,"E85.0.MirrorCS"),sQuery(id+"F4.wireOp",EDGE,"E86.0.MirrorCS"),sQuery(id+"F4.wireOp",EDGE,"E87.0.MirrorCS")])]}),"instanceName":"27"});
            var Q168;
            Q168=makeQuery(id+"F6.opPattern","COPY",BODY,{"derivedFrom":makeQuery(id+"F5.opExtrude","SWEPT_BODY",BODY,{"disambiguationData":[OSD([sQuery(id+"F4.wireOp",EDGE,"E69")])]}),"instanceName":"28"});
            var Q169;
            Q169=makeQuery(id+"F6.opPattern","COPY",BODY,{"derivedFrom":makeQuery(id+"F5.opExtrude","SWEPT_BODY",BODY,{"disambiguationData":[OSD([sQuery(id+"F4.wireOp",EDGE,"E70")])]}),"instanceName":"28"});
            var Q170;
            Q170=makeQuery(id+"F6.opPattern","COPY",BODY,{"derivedFrom":makeQuery(id+"F5.opExtrude","SWEPT_BODY",BODY,{"disambiguationData":[OSD([sQuery(id+"F4.wireOp",EDGE,"E71"),sQuery(id+"F4.wireOp",EDGE,"E72"),sQuery(id+"F4.wireOp",EDGE,"E74"),sQuery(id+"F4.wireOp",EDGE,"E75"),sQuery(id+"F4.wireOp",EDGE,"E76"),sQuery(id+"F4.wireOp",EDGE,"E77.filletArc"),sQuery(id+"F4.wireOp",EDGE,"E78.filletArc")])]}),"instanceName":"28"});
            var Q171;
            Q171=makeQuery(id+"F6.opPattern","COPY",BODY,{"derivedFrom":makeQuery(id+"F5.opExtrude","SWEPT_BODY",BODY,{"disambiguationData":[OSD([sQuery(id+"F4.wireOp",EDGE,"E79.0.MirrorC")])]}),"instanceName":"28"});
            var Q172;
            Q172=makeQuery(id+"F6.opPattern","COPY",BODY,{"derivedFrom":makeQuery(id+"F5.opExtrude","SWEPT_BODY",BODY,{"disambiguationData":[OSD([sQuery(id+"F4.wireOp",EDGE,"E80.0.MirrorC"),sQuery(id+"F4.wireOp",EDGE,"E89")])]}),"instanceName":"28"});
            var Q173;
            Q173=makeQuery(id+"F6.opPattern","COPY",BODY,{"derivedFrom":makeQuery(id+"F5.opExtrude","SWEPT_BODY",BODY,{"disambiguationData":[OSD([sQuery(id+"F4.wireOp",EDGE,"E81.0.MirrorCS"),sQuery(id+"F4.wireOp",EDGE,"E82.0.MirrorCS"),sQuery(id+"F4.wireOp",EDGE,"E83.0.MirrorCS"),sQuery(id+"F4.wireOp",EDGE,"E84.0.MirrorCS"),sQuery(id+"F4.wireOp",EDGE,"E85.0.MirrorCS"),sQuery(id+"F4.wireOp",EDGE,"E86.0.MirrorCS"),sQuery(id+"F4.wireOp",EDGE,"E87.0.MirrorCS")])]}),"instanceName":"28"});
            var Q174;
            Q174=makeQuery(id+"F6.opPattern","COPY",BODY,{"derivedFrom":makeQuery(id+"F5.opExtrude","SWEPT_BODY",BODY,{"disambiguationData":[OSD([sQuery(id+"F4.wireOp",EDGE,"E69")])]}),"instanceName":"29"});
            var Q175;
            Q175=makeQuery(id+"F6.opPattern","COPY",BODY,{"derivedFrom":makeQuery(id+"F5.opExtrude","SWEPT_BODY",BODY,{"disambiguationData":[OSD([sQuery(id+"F4.wireOp",EDGE,"E70")])]}),"instanceName":"29"});
            var Q176;
            Q176=makeQuery(id+"F6.opPattern","COPY",BODY,{"derivedFrom":makeQuery(id+"F5.opExtrude","SWEPT_BODY",BODY,{"disambiguationData":[OSD([sQuery(id+"F4.wireOp",EDGE,"E71"),sQuery(id+"F4.wireOp",EDGE,"E72"),sQuery(id+"F4.wireOp",EDGE,"E74"),sQuery(id+"F4.wireOp",EDGE,"E75"),sQuery(id+"F4.wireOp",EDGE,"E76"),sQuery(id+"F4.wireOp",EDGE,"E77.filletArc"),sQuery(id+"F4.wireOp",EDGE,"E78.filletArc")])]}),"instanceName":"29"});
            var Q177;
            Q177=makeQuery(id+"F6.opPattern","COPY",BODY,{"derivedFrom":makeQuery(id+"F5.opExtrude","SWEPT_BODY",BODY,{"disambiguationData":[OSD([sQuery(id+"F4.wireOp",EDGE,"E79.0.MirrorC")])]}),"instanceName":"29"});
            var Q178;
            Q178=makeQuery(id+"F6.opPattern","COPY",BODY,{"derivedFrom":makeQuery(id+"F5.opExtrude","SWEPT_BODY",BODY,{"disambiguationData":[OSD([sQuery(id+"F4.wireOp",EDGE,"E80.0.MirrorC"),sQuery(id+"F4.wireOp",EDGE,"E89")])]}),"instanceName":"29"});
            var Q179;
            Q179=makeQuery(id+"F6.opPattern","COPY",BODY,{"derivedFrom":makeQuery(id+"F5.opExtrude","SWEPT_BODY",BODY,{"disambiguationData":[OSD([sQuery(id+"F4.wireOp",EDGE,"E81.0.MirrorCS"),sQuery(id+"F4.wireOp",EDGE,"E82.0.MirrorCS"),sQuery(id+"F4.wireOp",EDGE,"E83.0.MirrorCS"),sQuery(id+"F4.wireOp",EDGE,"E84.0.MirrorCS"),sQuery(id+"F4.wireOp",EDGE,"E85.0.MirrorCS"),sQuery(id+"F4.wireOp",EDGE,"E86.0.MirrorCS"),sQuery(id+"F4.wireOp",EDGE,"E87.0.MirrorCS")])]}),"instanceName":"29"});
            var Q180;
            Q180=makeQuery(id+"F6.opPattern","COPY",BODY,{"derivedFrom":makeQuery(id+"F5.opExtrude","SWEPT_BODY",BODY,{"disambiguationData":[OSD([sQuery(id+"F4.wireOp",EDGE,"E69")])]}),"instanceName":"30"});
            var Q181;
            Q181=makeQuery(id+"F6.opPattern","COPY",BODY,{"derivedFrom":makeQuery(id+"F5.opExtrude","SWEPT_BODY",BODY,{"disambiguationData":[OSD([sQuery(id+"F4.wireOp",EDGE,"E70")])]}),"instanceName":"30"});
            var Q182;
            Q182=makeQuery(id+"F6.opPattern","COPY",BODY,{"derivedFrom":makeQuery(id+"F5.opExtrude","SWEPT_BODY",BODY,{"disambiguationData":[OSD([sQuery(id+"F4.wireOp",EDGE,"E71"),sQuery(id+"F4.wireOp",EDGE,"E72"),sQuery(id+"F4.wireOp",EDGE,"E74"),sQuery(id+"F4.wireOp",EDGE,"E75"),sQuery(id+"F4.wireOp",EDGE,"E76"),sQuery(id+"F4.wireOp",EDGE,"E77.filletArc"),sQuery(id+"F4.wireOp",EDGE,"E78.filletArc")])]}),"instanceName":"30"});
            var Q183;
            Q183=makeQuery(id+"F6.opPattern","COPY",BODY,{"derivedFrom":makeQuery(id+"F5.opExtrude","SWEPT_BODY",BODY,{"disambiguationData":[OSD([sQuery(id+"F4.wireOp",EDGE,"E79.0.MirrorC")])]}),"instanceName":"30"});
            var Q184;
            Q184=makeQuery(id+"F6.opPattern","COPY",BODY,{"derivedFrom":makeQuery(id+"F5.opExtrude","SWEPT_BODY",BODY,{"disambiguationData":[OSD([sQuery(id+"F4.wireOp",EDGE,"E80.0.MirrorC"),sQuery(id+"F4.wireOp",EDGE,"E89")])]}),"instanceName":"30"});
            var Q185;
            Q185=makeQuery(id+"F6.opPattern","COPY",BODY,{"derivedFrom":makeQuery(id+"F5.opExtrude","SWEPT_BODY",BODY,{"disambiguationData":[OSD([sQuery(id+"F4.wireOp",EDGE,"E81.0.MirrorCS"),sQuery(id+"F4.wireOp",EDGE,"E82.0.MirrorCS"),sQuery(id+"F4.wireOp",EDGE,"E83.0.MirrorCS"),sQuery(id+"F4.wireOp",EDGE,"E84.0.MirrorCS"),sQuery(id+"F4.wireOp",EDGE,"E85.0.MirrorCS"),sQuery(id+"F4.wireOp",EDGE,"E86.0.MirrorCS"),sQuery(id+"F4.wireOp",EDGE,"E87.0.MirrorCS")])]}),"instanceName":"30"});
            var Q186;
            Q186=makeQuery(id+"F6.opPattern","COPY",BODY,{"derivedFrom":makeQuery(id+"F5.opExtrude","SWEPT_BODY",BODY,{"disambiguationData":[OSD([sQuery(id+"F4.wireOp",EDGE,"E69")])]}),"instanceName":"31"});
            var Q187;
            Q187=makeQuery(id+"F6.opPattern","COPY",BODY,{"derivedFrom":makeQuery(id+"F5.opExtrude","SWEPT_BODY",BODY,{"disambiguationData":[OSD([sQuery(id+"F4.wireOp",EDGE,"E70")])]}),"instanceName":"31"});
            var Q188;
            Q188=makeQuery(id+"F6.opPattern","COPY",BODY,{"derivedFrom":makeQuery(id+"F5.opExtrude","SWEPT_BODY",BODY,{"disambiguationData":[OSD([sQuery(id+"F4.wireOp",EDGE,"E71"),sQuery(id+"F4.wireOp",EDGE,"E72"),sQuery(id+"F4.wireOp",EDGE,"E74"),sQuery(id+"F4.wireOp",EDGE,"E75"),sQuery(id+"F4.wireOp",EDGE,"E76"),sQuery(id+"F4.wireOp",EDGE,"E77.filletArc"),sQuery(id+"F4.wireOp",EDGE,"E78.filletArc")])]}),"instanceName":"31"});
            var Q189;
            Q189=makeQuery(id+"F6.opPattern","COPY",BODY,{"derivedFrom":makeQuery(id+"F5.opExtrude","SWEPT_BODY",BODY,{"disambiguationData":[OSD([sQuery(id+"F4.wireOp",EDGE,"E79.0.MirrorC")])]}),"instanceName":"31"});
            var Q190;
            Q190=makeQuery(id+"F6.opPattern","COPY",BODY,{"derivedFrom":makeQuery(id+"F5.opExtrude","SWEPT_BODY",BODY,{"disambiguationData":[OSD([sQuery(id+"F4.wireOp",EDGE,"E80.0.MirrorC"),sQuery(id+"F4.wireOp",EDGE,"E89")])]}),"instanceName":"31"});
            var Q191;
            Q191=makeQuery(id+"F6.opPattern","COPY",BODY,{"derivedFrom":makeQuery(id+"F5.opExtrude","SWEPT_BODY",BODY,{"disambiguationData":[OSD([sQuery(id+"F4.wireOp",EDGE,"E81.0.MirrorCS"),sQuery(id+"F4.wireOp",EDGE,"E82.0.MirrorCS"),sQuery(id+"F4.wireOp",EDGE,"E83.0.MirrorCS"),sQuery(id+"F4.wireOp",EDGE,"E84.0.MirrorCS"),sQuery(id+"F4.wireOp",EDGE,"E85.0.MirrorCS"),sQuery(id+"F4.wireOp",EDGE,"E86.0.MirrorCS"),sQuery(id+"F4.wireOp",EDGE,"E87.0.MirrorCS")])]}),"instanceName":"31"});
            var Q192;
            Q192=makeQuery(id+"F6.opPattern","COPY",BODY,{"derivedFrom":makeQuery(id+"F5.opExtrude","SWEPT_BODY",BODY,{"disambiguationData":[OSD([sQuery(id+"F4.wireOp",EDGE,"E69")])]}),"instanceName":"32"});
            var Q193;
            Q193=makeQuery(id+"F6.opPattern","COPY",BODY,{"derivedFrom":makeQuery(id+"F5.opExtrude","SWEPT_BODY",BODY,{"disambiguationData":[OSD([sQuery(id+"F4.wireOp",EDGE,"E70")])]}),"instanceName":"32"});
            var Q194;
            Q194=makeQuery(id+"F6.opPattern","COPY",BODY,{"derivedFrom":makeQuery(id+"F5.opExtrude","SWEPT_BODY",BODY,{"disambiguationData":[OSD([sQuery(id+"F4.wireOp",EDGE,"E71"),sQuery(id+"F4.wireOp",EDGE,"E72"),sQuery(id+"F4.wireOp",EDGE,"E74"),sQuery(id+"F4.wireOp",EDGE,"E75"),sQuery(id+"F4.wireOp",EDGE,"E76"),sQuery(id+"F4.wireOp",EDGE,"E77.filletArc"),sQuery(id+"F4.wireOp",EDGE,"E78.filletArc")])]}),"instanceName":"32"});
            var Q195;
            Q195=makeQuery(id+"F6.opPattern","COPY",BODY,{"derivedFrom":makeQuery(id+"F5.opExtrude","SWEPT_BODY",BODY,{"disambiguationData":[OSD([sQuery(id+"F4.wireOp",EDGE,"E79.0.MirrorC")])]}),"instanceName":"32"});
            var Q196;
            Q196=makeQuery(id+"F6.opPattern","COPY",BODY,{"derivedFrom":makeQuery(id+"F5.opExtrude","SWEPT_BODY",BODY,{"disambiguationData":[OSD([sQuery(id+"F4.wireOp",EDGE,"E80.0.MirrorC"),sQuery(id+"F4.wireOp",EDGE,"E89")])]}),"instanceName":"32"});
            var Q197;
            Q197=makeQuery(id+"F6.opPattern","COPY",BODY,{"derivedFrom":makeQuery(id+"F5.opExtrude","SWEPT_BODY",BODY,{"disambiguationData":[OSD([sQuery(id+"F4.wireOp",EDGE,"E81.0.MirrorCS"),sQuery(id+"F4.wireOp",EDGE,"E82.0.MirrorCS"),sQuery(id+"F4.wireOp",EDGE,"E83.0.MirrorCS"),sQuery(id+"F4.wireOp",EDGE,"E84.0.MirrorCS"),sQuery(id+"F4.wireOp",EDGE,"E85.0.MirrorCS"),sQuery(id+"F4.wireOp",EDGE,"E86.0.MirrorCS"),sQuery(id+"F4.wireOp",EDGE,"E87.0.MirrorCS")])]}),"instanceName":"32"});
            var Q198;
            Q198=makeQuery(id+"F6.opPattern","COPY",BODY,{"derivedFrom":makeQuery(id+"F5.opExtrude","SWEPT_BODY",BODY,{"disambiguationData":[OSD([sQuery(id+"F4.wireOp",EDGE,"E69")])]}),"instanceName":"33"});
            var Q199;
            Q199=makeQuery(id+"F6.opPattern","COPY",BODY,{"derivedFrom":makeQuery(id+"F5.opExtrude","SWEPT_BODY",BODY,{"disambiguationData":[OSD([sQuery(id+"F4.wireOp",EDGE,"E70")])]}),"instanceName":"33"});
            var Q200;
            Q200=makeQuery(id+"F6.opPattern","COPY",BODY,{"derivedFrom":makeQuery(id+"F5.opExtrude","SWEPT_BODY",BODY,{"disambiguationData":[OSD([sQuery(id+"F4.wireOp",EDGE,"E71"),sQuery(id+"F4.wireOp",EDGE,"E72"),sQuery(id+"F4.wireOp",EDGE,"E74"),sQuery(id+"F4.wireOp",EDGE,"E75"),sQuery(id+"F4.wireOp",EDGE,"E76"),sQuery(id+"F4.wireOp",EDGE,"E77.filletArc"),sQuery(id+"F4.wireOp",EDGE,"E78.filletArc")])]}),"instanceName":"33"});
            var Q201;
            Q201=makeQuery(id+"F6.opPattern","COPY",BODY,{"derivedFrom":makeQuery(id+"F5.opExtrude","SWEPT_BODY",BODY,{"disambiguationData":[OSD([sQuery(id+"F4.wireOp",EDGE,"E79.0.MirrorC")])]}),"instanceName":"33"});
            var Q202;
            Q202=makeQuery(id+"F6.opPattern","COPY",BODY,{"derivedFrom":makeQuery(id+"F5.opExtrude","SWEPT_BODY",BODY,{"disambiguationData":[OSD([sQuery(id+"F4.wireOp",EDGE,"E80.0.MirrorC"),sQuery(id+"F4.wireOp",EDGE,"E89")])]}),"instanceName":"33"});
            var Q203;
            Q203=makeQuery(id+"F6.opPattern","COPY",BODY,{"derivedFrom":makeQuery(id+"F5.opExtrude","SWEPT_BODY",BODY,{"disambiguationData":[OSD([sQuery(id+"F4.wireOp",EDGE,"E81.0.MirrorCS"),sQuery(id+"F4.wireOp",EDGE,"E82.0.MirrorCS"),sQuery(id+"F4.wireOp",EDGE,"E83.0.MirrorCS"),sQuery(id+"F4.wireOp",EDGE,"E84.0.MirrorCS"),sQuery(id+"F4.wireOp",EDGE,"E85.0.MirrorCS"),sQuery(id+"F4.wireOp",EDGE,"E86.0.MirrorCS"),sQuery(id+"F4.wireOp",EDGE,"E87.0.MirrorCS")])]}),"instanceName":"33"});
            var Q204;
            Q204=makeQuery(id+"F6.opPattern","COPY",BODY,{"derivedFrom":makeQuery(id+"F5.opExtrude","SWEPT_BODY",BODY,{"disambiguationData":[OSD([sQuery(id+"F4.wireOp",EDGE,"E69")])]}),"instanceName":"34"});
            var Q205;
            Q205=makeQuery(id+"F6.opPattern","COPY",BODY,{"derivedFrom":makeQuery(id+"F5.opExtrude","SWEPT_BODY",BODY,{"disambiguationData":[OSD([sQuery(id+"F4.wireOp",EDGE,"E70")])]}),"instanceName":"34"});
            var Q206;
            Q206=makeQuery(id+"F6.opPattern","COPY",BODY,{"derivedFrom":makeQuery(id+"F5.opExtrude","SWEPT_BODY",BODY,{"disambiguationData":[OSD([sQuery(id+"F4.wireOp",EDGE,"E71"),sQuery(id+"F4.wireOp",EDGE,"E72"),sQuery(id+"F4.wireOp",EDGE,"E74"),sQuery(id+"F4.wireOp",EDGE,"E75"),sQuery(id+"F4.wireOp",EDGE,"E76"),sQuery(id+"F4.wireOp",EDGE,"E77.filletArc"),sQuery(id+"F4.wireOp",EDGE,"E78.filletArc")])]}),"instanceName":"34"});
            var Q207;
            Q207=makeQuery(id+"F6.opPattern","COPY",BODY,{"derivedFrom":makeQuery(id+"F5.opExtrude","SWEPT_BODY",BODY,{"disambiguationData":[OSD([sQuery(id+"F4.wireOp",EDGE,"E79.0.MirrorC")])]}),"instanceName":"34"});
            var Q208;
            Q208=makeQuery(id+"F6.opPattern","COPY",BODY,{"derivedFrom":makeQuery(id+"F5.opExtrude","SWEPT_BODY",BODY,{"disambiguationData":[OSD([sQuery(id+"F4.wireOp",EDGE,"E80.0.MirrorC"),sQuery(id+"F4.wireOp",EDGE,"E89")])]}),"instanceName":"34"});
            var Q209;
            Q209=makeQuery(id+"F6.opPattern","COPY",BODY,{"derivedFrom":makeQuery(id+"F5.opExtrude","SWEPT_BODY",BODY,{"disambiguationData":[OSD([sQuery(id+"F4.wireOp",EDGE,"E81.0.MirrorCS"),sQuery(id+"F4.wireOp",EDGE,"E82.0.MirrorCS"),sQuery(id+"F4.wireOp",EDGE,"E83.0.MirrorCS"),sQuery(id+"F4.wireOp",EDGE,"E84.0.MirrorCS"),sQuery(id+"F4.wireOp",EDGE,"E85.0.MirrorCS"),sQuery(id+"F4.wireOp",EDGE,"E86.0.MirrorCS"),sQuery(id+"F4.wireOp",EDGE,"E87.0.MirrorCS")])]}),"instanceName":"34"});
            var Q210;
            Q210=makeQuery(id+"F6.opPattern","COPY",BODY,{"derivedFrom":makeQuery(id+"F5.opExtrude","SWEPT_BODY",BODY,{"disambiguationData":[OSD([sQuery(id+"F4.wireOp",EDGE,"E69")])]}),"instanceName":"35"});
            var Q211;
            Q211=makeQuery(id+"F6.opPattern","COPY",BODY,{"derivedFrom":makeQuery(id+"F5.opExtrude","SWEPT_BODY",BODY,{"disambiguationData":[OSD([sQuery(id+"F4.wireOp",EDGE,"E70")])]}),"instanceName":"35"});
            var Q212;
            Q212=makeQuery(id+"F6.opPattern","COPY",BODY,{"derivedFrom":makeQuery(id+"F5.opExtrude","SWEPT_BODY",BODY,{"disambiguationData":[OSD([sQuery(id+"F4.wireOp",EDGE,"E71"),sQuery(id+"F4.wireOp",EDGE,"E72"),sQuery(id+"F4.wireOp",EDGE,"E74"),sQuery(id+"F4.wireOp",EDGE,"E75"),sQuery(id+"F4.wireOp",EDGE,"E76"),sQuery(id+"F4.wireOp",EDGE,"E77.filletArc"),sQuery(id+"F4.wireOp",EDGE,"E78.filletArc")])]}),"instanceName":"35"});
            var Q213;
            Q213=makeQuery(id+"F6.opPattern","COPY",BODY,{"derivedFrom":makeQuery(id+"F5.opExtrude","SWEPT_BODY",BODY,{"disambiguationData":[OSD([sQuery(id+"F4.wireOp",EDGE,"E79.0.MirrorC")])]}),"instanceName":"35"});
            var Q214;
            Q214=makeQuery(id+"F6.opPattern","COPY",BODY,{"derivedFrom":makeQuery(id+"F5.opExtrude","SWEPT_BODY",BODY,{"disambiguationData":[OSD([sQuery(id+"F4.wireOp",EDGE,"E80.0.MirrorC"),sQuery(id+"F4.wireOp",EDGE,"E89")])]}),"instanceName":"35"});
            var Q215;
            Q215=makeQuery(id+"F6.opPattern","COPY",BODY,{"derivedFrom":makeQuery(id+"F5.opExtrude","SWEPT_BODY",BODY,{"disambiguationData":[OSD([sQuery(id+"F4.wireOp",EDGE,"E81.0.MirrorCS"),sQuery(id+"F4.wireOp",EDGE,"E82.0.MirrorCS"),sQuery(id+"F4.wireOp",EDGE,"E83.0.MirrorCS"),sQuery(id+"F4.wireOp",EDGE,"E84.0.MirrorCS"),sQuery(id+"F4.wireOp",EDGE,"E85.0.MirrorCS"),sQuery(id+"F4.wireOp",EDGE,"E86.0.MirrorCS"),sQuery(id+"F4.wireOp",EDGE,"E87.0.MirrorCS")])]}),"instanceName":"35"});
            var Q216;
            Q216=makeQuery(id+"F6.opPattern","COPY",BODY,{"derivedFrom":makeQuery(id+"F5.opExtrude","SWEPT_BODY",BODY,{"disambiguationData":[OSD([sQuery(id+"F4.wireOp",EDGE,"E69")])]}),"instanceName":"36"});
            var Q217;
            Q217=makeQuery(id+"F6.opPattern","COPY",BODY,{"derivedFrom":makeQuery(id+"F5.opExtrude","SWEPT_BODY",BODY,{"disambiguationData":[OSD([sQuery(id+"F4.wireOp",EDGE,"E70")])]}),"instanceName":"36"});
            var Q218;
            Q218=makeQuery(id+"F6.opPattern","COPY",BODY,{"derivedFrom":makeQuery(id+"F5.opExtrude","SWEPT_BODY",BODY,{"disambiguationData":[OSD([sQuery(id+"F4.wireOp",EDGE,"E71"),sQuery(id+"F4.wireOp",EDGE,"E72"),sQuery(id+"F4.wireOp",EDGE,"E74"),sQuery(id+"F4.wireOp",EDGE,"E75"),sQuery(id+"F4.wireOp",EDGE,"E76"),sQuery(id+"F4.wireOp",EDGE,"E77.filletArc"),sQuery(id+"F4.wireOp",EDGE,"E78.filletArc")])]}),"instanceName":"36"});
            var Q219;
            Q219=makeQuery(id+"F6.opPattern","COPY",BODY,{"derivedFrom":makeQuery(id+"F5.opExtrude","SWEPT_BODY",BODY,{"disambiguationData":[OSD([sQuery(id+"F4.wireOp",EDGE,"E79.0.MirrorC")])]}),"instanceName":"36"});
            var Q220;
            Q220=makeQuery(id+"F6.opPattern","COPY",BODY,{"derivedFrom":makeQuery(id+"F5.opExtrude","SWEPT_BODY",BODY,{"disambiguationData":[OSD([sQuery(id+"F4.wireOp",EDGE,"E80.0.MirrorC"),sQuery(id+"F4.wireOp",EDGE,"E89")])]}),"instanceName":"36"});
            var Q221;
            Q221=makeQuery(id+"F6.opPattern","COPY",BODY,{"derivedFrom":makeQuery(id+"F5.opExtrude","SWEPT_BODY",BODY,{"disambiguationData":[OSD([sQuery(id+"F4.wireOp",EDGE,"E81.0.MirrorCS"),sQuery(id+"F4.wireOp",EDGE,"E82.0.MirrorCS"),sQuery(id+"F4.wireOp",EDGE,"E83.0.MirrorCS"),sQuery(id+"F4.wireOp",EDGE,"E84.0.MirrorCS"),sQuery(id+"F4.wireOp",EDGE,"E85.0.MirrorCS"),sQuery(id+"F4.wireOp",EDGE,"E86.0.MirrorCS"),sQuery(id+"F4.wireOp",EDGE,"E87.0.MirrorCS")])]}),"instanceName":"36"});
            var Q222;
            Q222=makeQuery(id+"F6.opPattern","COPY",BODY,{"derivedFrom":makeQuery(id+"F5.opExtrude","SWEPT_BODY",BODY,{"disambiguationData":[OSD([sQuery(id+"F4.wireOp",EDGE,"E69")])]}),"instanceName":"37"});
            var Q223;
            Q223=makeQuery(id+"F6.opPattern","COPY",BODY,{"derivedFrom":makeQuery(id+"F5.opExtrude","SWEPT_BODY",BODY,{"disambiguationData":[OSD([sQuery(id+"F4.wireOp",EDGE,"E70")])]}),"instanceName":"37"});
            var Q224;
            Q224=makeQuery(id+"F6.opPattern","COPY",BODY,{"derivedFrom":makeQuery(id+"F5.opExtrude","SWEPT_BODY",BODY,{"disambiguationData":[OSD([sQuery(id+"F4.wireOp",EDGE,"E71"),sQuery(id+"F4.wireOp",EDGE,"E72"),sQuery(id+"F4.wireOp",EDGE,"E74"),sQuery(id+"F4.wireOp",EDGE,"E75"),sQuery(id+"F4.wireOp",EDGE,"E76"),sQuery(id+"F4.wireOp",EDGE,"E77.filletArc"),sQuery(id+"F4.wireOp",EDGE,"E78.filletArc")])]}),"instanceName":"37"});
            var Q225;
            Q225=makeQuery(id+"F6.opPattern","COPY",BODY,{"derivedFrom":makeQuery(id+"F5.opExtrude","SWEPT_BODY",BODY,{"disambiguationData":[OSD([sQuery(id+"F4.wireOp",EDGE,"E79.0.MirrorC")])]}),"instanceName":"37"});
            var Q226;
            Q226=makeQuery(id+"F6.opPattern","COPY",BODY,{"derivedFrom":makeQuery(id+"F5.opExtrude","SWEPT_BODY",BODY,{"disambiguationData":[OSD([sQuery(id+"F4.wireOp",EDGE,"E80.0.MirrorC"),sQuery(id+"F4.wireOp",EDGE,"E89")])]}),"instanceName":"37"});
            var Q227;
            Q227=makeQuery(id+"F6.opPattern","COPY",BODY,{"derivedFrom":makeQuery(id+"F5.opExtrude","SWEPT_BODY",BODY,{"disambiguationData":[OSD([sQuery(id+"F4.wireOp",EDGE,"E81.0.MirrorCS"),sQuery(id+"F4.wireOp",EDGE,"E82.0.MirrorCS"),sQuery(id+"F4.wireOp",EDGE,"E83.0.MirrorCS"),sQuery(id+"F4.wireOp",EDGE,"E84.0.MirrorCS"),sQuery(id+"F4.wireOp",EDGE,"E85.0.MirrorCS"),sQuery(id+"F4.wireOp",EDGE,"E86.0.MirrorCS"),sQuery(id+"F4.wireOp",EDGE,"E87.0.MirrorCS")])]}),"instanceName":"37"});
            var Q228;
            Q228=makeQuery(id+"F6.opPattern","COPY",BODY,{"derivedFrom":makeQuery(id+"F5.opExtrude","SWEPT_BODY",BODY,{"disambiguationData":[OSD([sQuery(id+"F4.wireOp",EDGE,"E69")])]}),"instanceName":"38"});
            var Q229;
            Q229=makeQuery(id+"F6.opPattern","COPY",BODY,{"derivedFrom":makeQuery(id+"F5.opExtrude","SWEPT_BODY",BODY,{"disambiguationData":[OSD([sQuery(id+"F4.wireOp",EDGE,"E70")])]}),"instanceName":"38"});
            var Q230;
            Q230=makeQuery(id+"F6.opPattern","COPY",BODY,{"derivedFrom":makeQuery(id+"F5.opExtrude","SWEPT_BODY",BODY,{"disambiguationData":[OSD([sQuery(id+"F4.wireOp",EDGE,"E71"),sQuery(id+"F4.wireOp",EDGE,"E72"),sQuery(id+"F4.wireOp",EDGE,"E74"),sQuery(id+"F4.wireOp",EDGE,"E75"),sQuery(id+"F4.wireOp",EDGE,"E76"),sQuery(id+"F4.wireOp",EDGE,"E77.filletArc"),sQuery(id+"F4.wireOp",EDGE,"E78.filletArc")])]}),"instanceName":"38"});
            var Q231;
            Q231=makeQuery(id+"F6.opPattern","COPY",BODY,{"derivedFrom":makeQuery(id+"F5.opExtrude","SWEPT_BODY",BODY,{"disambiguationData":[OSD([sQuery(id+"F4.wireOp",EDGE,"E79.0.MirrorC")])]}),"instanceName":"38"});
            var Q232;
            Q232=makeQuery(id+"F6.opPattern","COPY",BODY,{"derivedFrom":makeQuery(id+"F5.opExtrude","SWEPT_BODY",BODY,{"disambiguationData":[OSD([sQuery(id+"F4.wireOp",EDGE,"E80.0.MirrorC"),sQuery(id+"F4.wireOp",EDGE,"E89")])]}),"instanceName":"38"});
            var Q233;
            Q233=makeQuery(id+"F6.opPattern","COPY",BODY,{"derivedFrom":makeQuery(id+"F5.opExtrude","SWEPT_BODY",BODY,{"disambiguationData":[OSD([sQuery(id+"F4.wireOp",EDGE,"E81.0.MirrorCS"),sQuery(id+"F4.wireOp",EDGE,"E82.0.MirrorCS"),sQuery(id+"F4.wireOp",EDGE,"E83.0.MirrorCS"),sQuery(id+"F4.wireOp",EDGE,"E84.0.MirrorCS"),sQuery(id+"F4.wireOp",EDGE,"E85.0.MirrorCS"),sQuery(id+"F4.wireOp",EDGE,"E86.0.MirrorCS"),sQuery(id+"F4.wireOp",EDGE,"E87.0.MirrorCS")])]}),"instanceName":"38"});
            var Q234;
            Q234=makeQuery(id+"F6.opPattern","COPY",BODY,{"derivedFrom":makeQuery(id+"F5.opExtrude","SWEPT_BODY",BODY,{"disambiguationData":[OSD([sQuery(id+"F4.wireOp",EDGE,"E69")])]}),"instanceName":"39"});
            var Q235;
            Q235=makeQuery(id+"F6.opPattern","COPY",BODY,{"derivedFrom":makeQuery(id+"F5.opExtrude","SWEPT_BODY",BODY,{"disambiguationData":[OSD([sQuery(id+"F4.wireOp",EDGE,"E70")])]}),"instanceName":"39"});
            var Q236;
            Q236=makeQuery(id+"F6.opPattern","COPY",BODY,{"derivedFrom":makeQuery(id+"F5.opExtrude","SWEPT_BODY",BODY,{"disambiguationData":[OSD([sQuery(id+"F4.wireOp",EDGE,"E71"),sQuery(id+"F4.wireOp",EDGE,"E72"),sQuery(id+"F4.wireOp",EDGE,"E74"),sQuery(id+"F4.wireOp",EDGE,"E75"),sQuery(id+"F4.wireOp",EDGE,"E76"),sQuery(id+"F4.wireOp",EDGE,"E77.filletArc"),sQuery(id+"F4.wireOp",EDGE,"E78.filletArc")])]}),"instanceName":"39"});
            var Q237;
            Q237=makeQuery(id+"F6.opPattern","COPY",BODY,{"derivedFrom":makeQuery(id+"F5.opExtrude","SWEPT_BODY",BODY,{"disambiguationData":[OSD([sQuery(id+"F4.wireOp",EDGE,"E79.0.MirrorC")])]}),"instanceName":"39"});
            var Q238;
            Q238=makeQuery(id+"F6.opPattern","COPY",BODY,{"derivedFrom":makeQuery(id+"F5.opExtrude","SWEPT_BODY",BODY,{"disambiguationData":[OSD([sQuery(id+"F4.wireOp",EDGE,"E80.0.MirrorC"),sQuery(id+"F4.wireOp",EDGE,"E89")])]}),"instanceName":"39"});
            var Q239;
            Q239=makeQuery(id+"F6.opPattern","COPY",BODY,{"derivedFrom":makeQuery(id+"F5.opExtrude","SWEPT_BODY",BODY,{"disambiguationData":[OSD([sQuery(id+"F4.wireOp",EDGE,"E81.0.MirrorCS"),sQuery(id+"F4.wireOp",EDGE,"E82.0.MirrorCS"),sQuery(id+"F4.wireOp",EDGE,"E83.0.MirrorCS"),sQuery(id+"F4.wireOp",EDGE,"E84.0.MirrorCS"),sQuery(id+"F4.wireOp",EDGE,"E85.0.MirrorCS"),sQuery(id+"F4.wireOp",EDGE,"E86.0.MirrorCS"),sQuery(id+"F4.wireOp",EDGE,"E87.0.MirrorCS")])]}),"instanceName":"39"});
            var Q240;
            Q240=makeQuery(id+"F6.opPattern","COPY",BODY,{"derivedFrom":makeQuery(id+"F5.opExtrude","SWEPT_BODY",BODY,{"disambiguationData":[OSD([sQuery(id+"F4.wireOp",EDGE,"E69")])]}),"instanceName":"40"});
            var Q241;
            Q241=makeQuery(id+"F6.opPattern","COPY",BODY,{"derivedFrom":makeQuery(id+"F5.opExtrude","SWEPT_BODY",BODY,{"disambiguationData":[OSD([sQuery(id+"F4.wireOp",EDGE,"E70")])]}),"instanceName":"40"});
            var Q242;
            Q242=makeQuery(id+"F6.opPattern","COPY",BODY,{"derivedFrom":makeQuery(id+"F5.opExtrude","SWEPT_BODY",BODY,{"disambiguationData":[OSD([sQuery(id+"F4.wireOp",EDGE,"E71"),sQuery(id+"F4.wireOp",EDGE,"E72"),sQuery(id+"F4.wireOp",EDGE,"E74"),sQuery(id+"F4.wireOp",EDGE,"E75"),sQuery(id+"F4.wireOp",EDGE,"E76"),sQuery(id+"F4.wireOp",EDGE,"E77.filletArc"),sQuery(id+"F4.wireOp",EDGE,"E78.filletArc")])]}),"instanceName":"40"});
            var Q243;
            Q243=makeQuery(id+"F6.opPattern","COPY",BODY,{"derivedFrom":makeQuery(id+"F5.opExtrude","SWEPT_BODY",BODY,{"disambiguationData":[OSD([sQuery(id+"F4.wireOp",EDGE,"E79.0.MirrorC")])]}),"instanceName":"40"});
            var Q244;
            Q244=makeQuery(id+"F6.opPattern","COPY",BODY,{"derivedFrom":makeQuery(id+"F5.opExtrude","SWEPT_BODY",BODY,{"disambiguationData":[OSD([sQuery(id+"F4.wireOp",EDGE,"E80.0.MirrorC"),sQuery(id+"F4.wireOp",EDGE,"E89")])]}),"instanceName":"40"});
            var Q245;
            Q245=makeQuery(id+"F6.opPattern","COPY",BODY,{"derivedFrom":makeQuery(id+"F5.opExtrude","SWEPT_BODY",BODY,{"disambiguationData":[OSD([sQuery(id+"F4.wireOp",EDGE,"E81.0.MirrorCS"),sQuery(id+"F4.wireOp",EDGE,"E82.0.MirrorCS"),sQuery(id+"F4.wireOp",EDGE,"E83.0.MirrorCS"),sQuery(id+"F4.wireOp",EDGE,"E84.0.MirrorCS"),sQuery(id+"F4.wireOp",EDGE,"E85.0.MirrorCS"),sQuery(id+"F4.wireOp",EDGE,"E86.0.MirrorCS"),sQuery(id+"F4.wireOp",EDGE,"E87.0.MirrorCS")])]}),"instanceName":"40"});
            var Q246;
            Q246=makeQuery(id+"F6.opPattern","COPY",BODY,{"derivedFrom":makeQuery(id+"F5.opExtrude","SWEPT_BODY",BODY,{"disambiguationData":[OSD([sQuery(id+"F4.wireOp",EDGE,"E69")])]}),"instanceName":"41"});
            var Q247;
            Q247=makeQuery(id+"F6.opPattern","COPY",BODY,{"derivedFrom":makeQuery(id+"F5.opExtrude","SWEPT_BODY",BODY,{"disambiguationData":[OSD([sQuery(id+"F4.wireOp",EDGE,"E70")])]}),"instanceName":"41"});
            var Q248;
            Q248=makeQuery(id+"F6.opPattern","COPY",BODY,{"derivedFrom":makeQuery(id+"F5.opExtrude","SWEPT_BODY",BODY,{"disambiguationData":[OSD([sQuery(id+"F4.wireOp",EDGE,"E71"),sQuery(id+"F4.wireOp",EDGE,"E72"),sQuery(id+"F4.wireOp",EDGE,"E74"),sQuery(id+"F4.wireOp",EDGE,"E75"),sQuery(id+"F4.wireOp",EDGE,"E76"),sQuery(id+"F4.wireOp",EDGE,"E77.filletArc"),sQuery(id+"F4.wireOp",EDGE,"E78.filletArc")])]}),"instanceName":"41"});
            var Q249;
            Q249=makeQuery(id+"F6.opPattern","COPY",BODY,{"derivedFrom":makeQuery(id+"F5.opExtrude","SWEPT_BODY",BODY,{"disambiguationData":[OSD([sQuery(id+"F4.wireOp",EDGE,"E79.0.MirrorC")])]}),"instanceName":"41"});
            var Q250;
            Q250=makeQuery(id+"F6.opPattern","COPY",BODY,{"derivedFrom":makeQuery(id+"F5.opExtrude","SWEPT_BODY",BODY,{"disambiguationData":[OSD([sQuery(id+"F4.wireOp",EDGE,"E80.0.MirrorC"),sQuery(id+"F4.wireOp",EDGE,"E89")])]}),"instanceName":"41"});
            var Q251;
            Q251=makeQuery(id+"F6.opPattern","COPY",BODY,{"derivedFrom":makeQuery(id+"F5.opExtrude","SWEPT_BODY",BODY,{"disambiguationData":[OSD([sQuery(id+"F4.wireOp",EDGE,"E81.0.MirrorCS"),sQuery(id+"F4.wireOp",EDGE,"E82.0.MirrorCS"),sQuery(id+"F4.wireOp",EDGE,"E83.0.MirrorCS"),sQuery(id+"F4.wireOp",EDGE,"E84.0.MirrorCS"),sQuery(id+"F4.wireOp",EDGE,"E85.0.MirrorCS"),sQuery(id+"F4.wireOp",EDGE,"E86.0.MirrorCS"),sQuery(id+"F4.wireOp",EDGE,"E87.0.MirrorCS")])]}),"instanceName":"41"});
            var Q252;
            Q252=makeQuery(id+"F6.opPattern","COPY",BODY,{"derivedFrom":makeQuery(id+"F5.opExtrude","SWEPT_BODY",BODY,{"disambiguationData":[OSD([sQuery(id+"F4.wireOp",EDGE,"E69")])]}),"instanceName":"42"});
            var Q253;
            Q253=makeQuery(id+"F6.opPattern","COPY",BODY,{"derivedFrom":makeQuery(id+"F5.opExtrude","SWEPT_BODY",BODY,{"disambiguationData":[OSD([sQuery(id+"F4.wireOp",EDGE,"E70")])]}),"instanceName":"42"});
            var Q254;
            Q254=makeQuery(id+"F6.opPattern","COPY",BODY,{"derivedFrom":makeQuery(id+"F5.opExtrude","SWEPT_BODY",BODY,{"disambiguationData":[OSD([sQuery(id+"F4.wireOp",EDGE,"E71"),sQuery(id+"F4.wireOp",EDGE,"E72"),sQuery(id+"F4.wireOp",EDGE,"E74"),sQuery(id+"F4.wireOp",EDGE,"E75"),sQuery(id+"F4.wireOp",EDGE,"E76"),sQuery(id+"F4.wireOp",EDGE,"E77.filletArc"),sQuery(id+"F4.wireOp",EDGE,"E78.filletArc")])]}),"instanceName":"42"});
            var Q255;
            Q255=makeQuery(id+"F6.opPattern","COPY",BODY,{"derivedFrom":makeQuery(id+"F5.opExtrude","SWEPT_BODY",BODY,{"disambiguationData":[OSD([sQuery(id+"F4.wireOp",EDGE,"E79.0.MirrorC")])]}),"instanceName":"42"});
            var Q256;
            Q256=makeQuery(id+"F6.opPattern","COPY",BODY,{"derivedFrom":makeQuery(id+"F5.opExtrude","SWEPT_BODY",BODY,{"disambiguationData":[OSD([sQuery(id+"F4.wireOp",EDGE,"E80.0.MirrorC"),sQuery(id+"F4.wireOp",EDGE,"E89")])]}),"instanceName":"42"});
            var Q257;
            Q257=makeQuery(id+"F6.opPattern","COPY",BODY,{"derivedFrom":makeQuery(id+"F5.opExtrude","SWEPT_BODY",BODY,{"disambiguationData":[OSD([sQuery(id+"F4.wireOp",EDGE,"E81.0.MirrorCS"),sQuery(id+"F4.wireOp",EDGE,"E82.0.MirrorCS"),sQuery(id+"F4.wireOp",EDGE,"E83.0.MirrorCS"),sQuery(id+"F4.wireOp",EDGE,"E84.0.MirrorCS"),sQuery(id+"F4.wireOp",EDGE,"E85.0.MirrorCS"),sQuery(id+"F4.wireOp",EDGE,"E86.0.MirrorCS"),sQuery(id+"F4.wireOp",EDGE,"E87.0.MirrorCS")])]}),"instanceName":"42"});
            var Q258;
            Q258=makeQuery(id+"F6.opPattern","COPY",BODY,{"derivedFrom":makeQuery(id+"F5.opExtrude","SWEPT_BODY",BODY,{"disambiguationData":[OSD([sQuery(id+"F4.wireOp",EDGE,"E69")])]}),"instanceName":"43"});
            var Q259;
            Q259=makeQuery(id+"F6.opPattern","COPY",BODY,{"derivedFrom":makeQuery(id+"F5.opExtrude","SWEPT_BODY",BODY,{"disambiguationData":[OSD([sQuery(id+"F4.wireOp",EDGE,"E70")])]}),"instanceName":"43"});
            var Q260;
            Q260=makeQuery(id+"F6.opPattern","COPY",BODY,{"derivedFrom":makeQuery(id+"F5.opExtrude","SWEPT_BODY",BODY,{"disambiguationData":[OSD([sQuery(id+"F4.wireOp",EDGE,"E71"),sQuery(id+"F4.wireOp",EDGE,"E72"),sQuery(id+"F4.wireOp",EDGE,"E74"),sQuery(id+"F4.wireOp",EDGE,"E75"),sQuery(id+"F4.wireOp",EDGE,"E76"),sQuery(id+"F4.wireOp",EDGE,"E77.filletArc"),sQuery(id+"F4.wireOp",EDGE,"E78.filletArc")])]}),"instanceName":"43"});
            var Q261;
            Q261=makeQuery(id+"F6.opPattern","COPY",BODY,{"derivedFrom":makeQuery(id+"F5.opExtrude","SWEPT_BODY",BODY,{"disambiguationData":[OSD([sQuery(id+"F4.wireOp",EDGE,"E79.0.MirrorC")])]}),"instanceName":"43"});
            var Q262;
            Q262=makeQuery(id+"F6.opPattern","COPY",BODY,{"derivedFrom":makeQuery(id+"F5.opExtrude","SWEPT_BODY",BODY,{"disambiguationData":[OSD([sQuery(id+"F4.wireOp",EDGE,"E80.0.MirrorC"),sQuery(id+"F4.wireOp",EDGE,"E89")])]}),"instanceName":"43"});
            var Q263;
            Q263=makeQuery(id+"F6.opPattern","COPY",BODY,{"derivedFrom":makeQuery(id+"F5.opExtrude","SWEPT_BODY",BODY,{"disambiguationData":[OSD([sQuery(id+"F4.wireOp",EDGE,"E81.0.MirrorCS"),sQuery(id+"F4.wireOp",EDGE,"E82.0.MirrorCS"),sQuery(id+"F4.wireOp",EDGE,"E83.0.MirrorCS"),sQuery(id+"F4.wireOp",EDGE,"E84.0.MirrorCS"),sQuery(id+"F4.wireOp",EDGE,"E85.0.MirrorCS"),sQuery(id+"F4.wireOp",EDGE,"E86.0.MirrorCS"),sQuery(id+"F4.wireOp",EDGE,"E87.0.MirrorCS")])]}),"instanceName":"43"});
            var Q264;
            Q264=makeQuery(id+"F6.opPattern","COPY",BODY,{"derivedFrom":makeQuery(id+"F5.opExtrude","SWEPT_BODY",BODY,{"disambiguationData":[OSD([sQuery(id+"F4.wireOp",EDGE,"E69")])]}),"instanceName":"44"});
            var Q265;
            Q265=makeQuery(id+"F6.opPattern","COPY",BODY,{"derivedFrom":makeQuery(id+"F5.opExtrude","SWEPT_BODY",BODY,{"disambiguationData":[OSD([sQuery(id+"F4.wireOp",EDGE,"E70")])]}),"instanceName":"44"});
            var Q266;
            Q266=makeQuery(id+"F6.opPattern","COPY",BODY,{"derivedFrom":makeQuery(id+"F5.opExtrude","SWEPT_BODY",BODY,{"disambiguationData":[OSD([sQuery(id+"F4.wireOp",EDGE,"E71"),sQuery(id+"F4.wireOp",EDGE,"E72"),sQuery(id+"F4.wireOp",EDGE,"E74"),sQuery(id+"F4.wireOp",EDGE,"E75"),sQuery(id+"F4.wireOp",EDGE,"E76"),sQuery(id+"F4.wireOp",EDGE,"E77.filletArc"),sQuery(id+"F4.wireOp",EDGE,"E78.filletArc")])]}),"instanceName":"44"});
            var Q267;
            Q267=makeQuery(id+"F6.opPattern","COPY",BODY,{"derivedFrom":makeQuery(id+"F5.opExtrude","SWEPT_BODY",BODY,{"disambiguationData":[OSD([sQuery(id+"F4.wireOp",EDGE,"E79.0.MirrorC")])]}),"instanceName":"44"});
            var Q268;
            Q268=makeQuery(id+"F6.opPattern","COPY",BODY,{"derivedFrom":makeQuery(id+"F5.opExtrude","SWEPT_BODY",BODY,{"disambiguationData":[OSD([sQuery(id+"F4.wireOp",EDGE,"E80.0.MirrorC"),sQuery(id+"F4.wireOp",EDGE,"E89")])]}),"instanceName":"44"});
            var Q269;
            Q269=makeQuery(id+"F6.opPattern","COPY",BODY,{"derivedFrom":makeQuery(id+"F5.opExtrude","SWEPT_BODY",BODY,{"disambiguationData":[OSD([sQuery(id+"F4.wireOp",EDGE,"E81.0.MirrorCS"),sQuery(id+"F4.wireOp",EDGE,"E82.0.MirrorCS"),sQuery(id+"F4.wireOp",EDGE,"E83.0.MirrorCS"),sQuery(id+"F4.wireOp",EDGE,"E84.0.MirrorCS"),sQuery(id+"F4.wireOp",EDGE,"E85.0.MirrorCS"),sQuery(id+"F4.wireOp",EDGE,"E86.0.MirrorCS"),sQuery(id+"F4.wireOp",EDGE,"E87.0.MirrorCS")])]}),"instanceName":"44"});
            var Q270;
            Q270=makeQuery(id+"F6.opPattern","COPY",BODY,{"derivedFrom":makeQuery(id+"F5.opExtrude","SWEPT_BODY",BODY,{"disambiguationData":[OSD([sQuery(id+"F4.wireOp",EDGE,"E69")])]}),"instanceName":"45"});
            var Q271;
            Q271=makeQuery(id+"F6.opPattern","COPY",BODY,{"derivedFrom":makeQuery(id+"F5.opExtrude","SWEPT_BODY",BODY,{"disambiguationData":[OSD([sQuery(id+"F4.wireOp",EDGE,"E70")])]}),"instanceName":"45"});
            var Q272;
            Q272=makeQuery(id+"F6.opPattern","COPY",BODY,{"derivedFrom":makeQuery(id+"F5.opExtrude","SWEPT_BODY",BODY,{"disambiguationData":[OSD([sQuery(id+"F4.wireOp",EDGE,"E71"),sQuery(id+"F4.wireOp",EDGE,"E72"),sQuery(id+"F4.wireOp",EDGE,"E74"),sQuery(id+"F4.wireOp",EDGE,"E75"),sQuery(id+"F4.wireOp",EDGE,"E76"),sQuery(id+"F4.wireOp",EDGE,"E77.filletArc"),sQuery(id+"F4.wireOp",EDGE,"E78.filletArc")])]}),"instanceName":"45"});
            var Q273;
            Q273=makeQuery(id+"F6.opPattern","COPY",BODY,{"derivedFrom":makeQuery(id+"F5.opExtrude","SWEPT_BODY",BODY,{"disambiguationData":[OSD([sQuery(id+"F4.wireOp",EDGE,"E79.0.MirrorC")])]}),"instanceName":"45"});
            var Q274;
            Q274=makeQuery(id+"F6.opPattern","COPY",BODY,{"derivedFrom":makeQuery(id+"F5.opExtrude","SWEPT_BODY",BODY,{"disambiguationData":[OSD([sQuery(id+"F4.wireOp",EDGE,"E80.0.MirrorC"),sQuery(id+"F4.wireOp",EDGE,"E89")])]}),"instanceName":"45"});
            var Q275;
            Q275=makeQuery(id+"F6.opPattern","COPY",BODY,{"derivedFrom":makeQuery(id+"F5.opExtrude","SWEPT_BODY",BODY,{"disambiguationData":[OSD([sQuery(id+"F4.wireOp",EDGE,"E81.0.MirrorCS"),sQuery(id+"F4.wireOp",EDGE,"E82.0.MirrorCS"),sQuery(id+"F4.wireOp",EDGE,"E83.0.MirrorCS"),sQuery(id+"F4.wireOp",EDGE,"E84.0.MirrorCS"),sQuery(id+"F4.wireOp",EDGE,"E85.0.MirrorCS"),sQuery(id+"F4.wireOp",EDGE,"E86.0.MirrorCS"),sQuery(id+"F4.wireOp",EDGE,"E87.0.MirrorCS")])]}),"instanceName":"45"});
            var Q276;
            Q276=makeQuery(id+"F6.opPattern","COPY",BODY,{"derivedFrom":makeQuery(id+"F5.opExtrude","SWEPT_BODY",BODY,{"disambiguationData":[OSD([sQuery(id+"F4.wireOp",EDGE,"E69")])]}),"instanceName":"46"});
            var Q277;
            Q277=makeQuery(id+"F6.opPattern","COPY",BODY,{"derivedFrom":makeQuery(id+"F5.opExtrude","SWEPT_BODY",BODY,{"disambiguationData":[OSD([sQuery(id+"F4.wireOp",EDGE,"E70")])]}),"instanceName":"46"});
            var Q278;
            Q278=makeQuery(id+"F6.opPattern","COPY",BODY,{"derivedFrom":makeQuery(id+"F5.opExtrude","SWEPT_BODY",BODY,{"disambiguationData":[OSD([sQuery(id+"F4.wireOp",EDGE,"E71"),sQuery(id+"F4.wireOp",EDGE,"E72"),sQuery(id+"F4.wireOp",EDGE,"E74"),sQuery(id+"F4.wireOp",EDGE,"E75"),sQuery(id+"F4.wireOp",EDGE,"E76"),sQuery(id+"F4.wireOp",EDGE,"E77.filletArc"),sQuery(id+"F4.wireOp",EDGE,"E78.filletArc")])]}),"instanceName":"46"});
            var Q279;
            Q279=makeQuery(id+"F6.opPattern","COPY",BODY,{"derivedFrom":makeQuery(id+"F5.opExtrude","SWEPT_BODY",BODY,{"disambiguationData":[OSD([sQuery(id+"F4.wireOp",EDGE,"E79.0.MirrorC")])]}),"instanceName":"46"});
            var Q280;
            Q280=makeQuery(id+"F6.opPattern","COPY",BODY,{"derivedFrom":makeQuery(id+"F5.opExtrude","SWEPT_BODY",BODY,{"disambiguationData":[OSD([sQuery(id+"F4.wireOp",EDGE,"E80.0.MirrorC"),sQuery(id+"F4.wireOp",EDGE,"E89")])]}),"instanceName":"46"});
            var Q281;
            Q281=makeQuery(id+"F6.opPattern","COPY",BODY,{"derivedFrom":makeQuery(id+"F5.opExtrude","SWEPT_BODY",BODY,{"disambiguationData":[OSD([sQuery(id+"F4.wireOp",EDGE,"E81.0.MirrorCS"),sQuery(id+"F4.wireOp",EDGE,"E82.0.MirrorCS"),sQuery(id+"F4.wireOp",EDGE,"E83.0.MirrorCS"),sQuery(id+"F4.wireOp",EDGE,"E84.0.MirrorCS"),sQuery(id+"F4.wireOp",EDGE,"E85.0.MirrorCS"),sQuery(id+"F4.wireOp",EDGE,"E86.0.MirrorCS"),sQuery(id+"F4.wireOp",EDGE,"E87.0.MirrorCS")])]}),"instanceName":"46"});
            var Q282;
            Q282=makeQuery(id+"F6.opPattern","COPY",BODY,{"derivedFrom":makeQuery(id+"F5.opExtrude","SWEPT_BODY",BODY,{"disambiguationData":[OSD([sQuery(id+"F4.wireOp",EDGE,"E69")])]}),"instanceName":"47"});
            var Q283;
            Q283=makeQuery(id+"F6.opPattern","COPY",BODY,{"derivedFrom":makeQuery(id+"F5.opExtrude","SWEPT_BODY",BODY,{"disambiguationData":[OSD([sQuery(id+"F4.wireOp",EDGE,"E70")])]}),"instanceName":"47"});
            var Q284;
            Q284=makeQuery(id+"F6.opPattern","COPY",BODY,{"derivedFrom":makeQuery(id+"F5.opExtrude","SWEPT_BODY",BODY,{"disambiguationData":[OSD([sQuery(id+"F4.wireOp",EDGE,"E71"),sQuery(id+"F4.wireOp",EDGE,"E72"),sQuery(id+"F4.wireOp",EDGE,"E74"),sQuery(id+"F4.wireOp",EDGE,"E75"),sQuery(id+"F4.wireOp",EDGE,"E76"),sQuery(id+"F4.wireOp",EDGE,"E77.filletArc"),sQuery(id+"F4.wireOp",EDGE,"E78.filletArc")])]}),"instanceName":"47"});
            var Q285;
            Q285=makeQuery(id+"F6.opPattern","COPY",BODY,{"derivedFrom":makeQuery(id+"F5.opExtrude","SWEPT_BODY",BODY,{"disambiguationData":[OSD([sQuery(id+"F4.wireOp",EDGE,"E79.0.MirrorC")])]}),"instanceName":"47"});
            var Q286;
            Q286=makeQuery(id+"F6.opPattern","COPY",BODY,{"derivedFrom":makeQuery(id+"F5.opExtrude","SWEPT_BODY",BODY,{"disambiguationData":[OSD([sQuery(id+"F4.wireOp",EDGE,"E80.0.MirrorC"),sQuery(id+"F4.wireOp",EDGE,"E89")])]}),"instanceName":"47"});
            var Q287;
            Q287=makeQuery(id+"F6.opPattern","COPY",BODY,{"derivedFrom":makeQuery(id+"F5.opExtrude","SWEPT_BODY",BODY,{"disambiguationData":[OSD([sQuery(id+"F4.wireOp",EDGE,"E81.0.MirrorCS"),sQuery(id+"F4.wireOp",EDGE,"E82.0.MirrorCS"),sQuery(id+"F4.wireOp",EDGE,"E83.0.MirrorCS"),sQuery(id+"F4.wireOp",EDGE,"E84.0.MirrorCS"),sQuery(id+"F4.wireOp",EDGE,"E85.0.MirrorCS"),sQuery(id+"F4.wireOp",EDGE,"E86.0.MirrorCS"),sQuery(id+"F4.wireOp",EDGE,"E87.0.MirrorCS")])]}),"instanceName":"47"});
            var Q288;
            Q288=makeQuery(id+"F6.opPattern","COPY",BODY,{"derivedFrom":makeQuery(id+"F5.opExtrude","SWEPT_BODY",BODY,{"disambiguationData":[OSD([sQuery(id+"F4.wireOp",EDGE,"E69")])]}),"instanceName":"48"});
            var Q289;
            Q289=makeQuery(id+"F6.opPattern","COPY",BODY,{"derivedFrom":makeQuery(id+"F5.opExtrude","SWEPT_BODY",BODY,{"disambiguationData":[OSD([sQuery(id+"F4.wireOp",EDGE,"E70")])]}),"instanceName":"48"});
            var Q290;
            Q290=makeQuery(id+"F6.opPattern","COPY",BODY,{"derivedFrom":makeQuery(id+"F5.opExtrude","SWEPT_BODY",BODY,{"disambiguationData":[OSD([sQuery(id+"F4.wireOp",EDGE,"E71"),sQuery(id+"F4.wireOp",EDGE,"E72"),sQuery(id+"F4.wireOp",EDGE,"E74"),sQuery(id+"F4.wireOp",EDGE,"E75"),sQuery(id+"F4.wireOp",EDGE,"E76"),sQuery(id+"F4.wireOp",EDGE,"E77.filletArc"),sQuery(id+"F4.wireOp",EDGE,"E78.filletArc")])]}),"instanceName":"48"});
            var Q291;
            Q291=makeQuery(id+"F6.opPattern","COPY",BODY,{"derivedFrom":makeQuery(id+"F5.opExtrude","SWEPT_BODY",BODY,{"disambiguationData":[OSD([sQuery(id+"F4.wireOp",EDGE,"E79.0.MirrorC")])]}),"instanceName":"48"});
            var Q292;
            Q292=makeQuery(id+"F6.opPattern","COPY",BODY,{"derivedFrom":makeQuery(id+"F5.opExtrude","SWEPT_BODY",BODY,{"disambiguationData":[OSD([sQuery(id+"F4.wireOp",EDGE,"E80.0.MirrorC"),sQuery(id+"F4.wireOp",EDGE,"E89")])]}),"instanceName":"48"});
            var Q293;
            Q293=makeQuery(id+"F6.opPattern","COPY",BODY,{"derivedFrom":makeQuery(id+"F5.opExtrude","SWEPT_BODY",BODY,{"disambiguationData":[OSD([sQuery(id+"F4.wireOp",EDGE,"E81.0.MirrorCS"),sQuery(id+"F4.wireOp",EDGE,"E82.0.MirrorCS"),sQuery(id+"F4.wireOp",EDGE,"E83.0.MirrorCS"),sQuery(id+"F4.wireOp",EDGE,"E84.0.MirrorCS"),sQuery(id+"F4.wireOp",EDGE,"E85.0.MirrorCS"),sQuery(id+"F4.wireOp",EDGE,"E86.0.MirrorCS"),sQuery(id+"F4.wireOp",EDGE,"E87.0.MirrorCS")])]}),"instanceName":"48"});
            var Q294;
            Q294=makeQuery(id+"F6.opPattern","COPY",BODY,{"derivedFrom":makeQuery(id+"F5.opExtrude","SWEPT_BODY",BODY,{"disambiguationData":[OSD([sQuery(id+"F4.wireOp",EDGE,"E69")])]}),"instanceName":"49"});
            var Q295;
            Q295=makeQuery(id+"F6.opPattern","COPY",BODY,{"derivedFrom":makeQuery(id+"F5.opExtrude","SWEPT_BODY",BODY,{"disambiguationData":[OSD([sQuery(id+"F4.wireOp",EDGE,"E70")])]}),"instanceName":"49"});
            var Q296;
            Q296=makeQuery(id+"F6.opPattern","COPY",BODY,{"derivedFrom":makeQuery(id+"F5.opExtrude","SWEPT_BODY",BODY,{"disambiguationData":[OSD([sQuery(id+"F4.wireOp",EDGE,"E71"),sQuery(id+"F4.wireOp",EDGE,"E72"),sQuery(id+"F4.wireOp",EDGE,"E74"),sQuery(id+"F4.wireOp",EDGE,"E75"),sQuery(id+"F4.wireOp",EDGE,"E76"),sQuery(id+"F4.wireOp",EDGE,"E77.filletArc"),sQuery(id+"F4.wireOp",EDGE,"E78.filletArc")])]}),"instanceName":"49"});
            var Q297;
            Q297=makeQuery(id+"F6.opPattern","COPY",BODY,{"derivedFrom":makeQuery(id+"F5.opExtrude","SWEPT_BODY",BODY,{"disambiguationData":[OSD([sQuery(id+"F4.wireOp",EDGE,"E79.0.MirrorC")])]}),"instanceName":"49"});
            var Q298;
            Q298=makeQuery(id+"F6.opPattern","COPY",BODY,{"derivedFrom":makeQuery(id+"F5.opExtrude","SWEPT_BODY",BODY,{"disambiguationData":[OSD([sQuery(id+"F4.wireOp",EDGE,"E80.0.MirrorC"),sQuery(id+"F4.wireOp",EDGE,"E89")])]}),"instanceName":"49"});
            var Q299;
            Q299=makeQuery(id+"F6.opPattern","COPY",BODY,{"derivedFrom":makeQuery(id+"F5.opExtrude","SWEPT_BODY",BODY,{"disambiguationData":[OSD([sQuery(id+"F4.wireOp",EDGE,"E81.0.MirrorCS"),sQuery(id+"F4.wireOp",EDGE,"E82.0.MirrorCS"),sQuery(id+"F4.wireOp",EDGE,"E83.0.MirrorCS"),sQuery(id+"F4.wireOp",EDGE,"E84.0.MirrorCS"),sQuery(id+"F4.wireOp",EDGE,"E85.0.MirrorCS"),sQuery(id+"F4.wireOp",EDGE,"E86.0.MirrorCS"),sQuery(id+"F4.wireOp",EDGE,"E87.0.MirrorCS")])]}),"instanceName":"49"});
            var Q300;
            Q300=makeQuery(id+"F6.opPattern","COPY",BODY,{"derivedFrom":makeQuery(id+"F5.opExtrude","SWEPT_BODY",BODY,{"disambiguationData":[OSD([sQuery(id+"F4.wireOp",EDGE,"E24"),sQuery(id+"F4.wireOp",EDGE,"E25"),sQuery(id+"F4.wireOp",EDGE,"E27"),sQuery(id+"F4.wireOp",EDGE,"E28"),sQuery(id+"F4.wireOp",EDGE,"E29"),sQuery(id+"F4.wireOp",EDGE,"E30.0.MirrorCS"),sQuery(id+"F4.wireOp",EDGE,"E31.0.MirrorCS"),sQuery(id+"F4.wireOp",EDGE,"E32.0.MirrorCS"),sQuery(id+"F4.wireOp",EDGE,"E33.0.MirrorCS"),sQuery(id+"F4.wireOp",EDGE,"E34.0.MirrorCS"),sQuery(id+"F4.wireOp",EDGE,"E35.filletArc"),sQuery(id+"F4.wireOp",EDGE,"E36.filletArc"),sQuery(id+"F4.wireOp",EDGE,"E37"),sQuery(id+"F4.wireOp",EDGE,"E38"),sQuery(id+"F4.wireOp",EDGE,"E39"),sQuery(id+"F4.wireOp",EDGE,"E40"),sQuery(id+"F4.wireOp",EDGE,"E41"),sQuery(id+"F4.wireOp",EDGE,"E42"),sQuery(id+"F4.wireOp",EDGE,"E43.filletArc"),sQuery(id+"F4.wireOp",EDGE,"E44.filletArc"),sQuery(id+"F4.wireOp",EDGE,"E45.trimOffspring"),sQuery(id+"F4.wireOp",EDGE,"E46.trimOffspring"),sQuery(id+"F4.wireOp",EDGE,"E47"),sQuery(id+"F4.wireOp",EDGE,"E48"),sQuery(id+"F4.wireOp",EDGE,"E49"),sQuery(id+"F4.wireOp",EDGE,"E50"),sQuery(id+"F4.wireOp",EDGE,"E51"),sQuery(id+"F4.wireOp",EDGE,"E52"),sQuery(id+"F4.wireOp",EDGE,"E53"),sQuery(id+"F4.wireOp",EDGE,"E54.filletArc"),sQuery(id+"F4.wireOp",EDGE,"E55.filletArc"),sQuery(id+"F4.wireOp",EDGE,"E56.filletArc"),sQuery(id+"F4.wireOp",EDGE,"E57"),sQuery(id+"F4.wireOp",EDGE,"E58"),sQuery(id+"F4.wireOp",EDGE,"E59"),sQuery(id+"F4.wireOp",EDGE,"E60.trimOffspring"),sQuery(id+"F4.wireOp",EDGE,"E61.0.MirrorCS"),sQuery(id+"F4.wireOp",EDGE,"E61.1.MirrorCS"),sQuery(id+"F4.wireOp",EDGE,"E61.2.MirrorCS"),sQuery(id+"F4.wireOp",EDGE,"E61.4.MirrorCS"),sQuery(id+"F4.wireOp",EDGE,"E61.5.MirrorCS"),sQuery(id+"F4.wireOp",EDGE,"E61.7.MirrorCS"),sQuery(id+"F4.wireOp",EDGE,"E61.10.MirrorCS"),sQuery(id+"F4.wireOp",EDGE,"E62.0.MirrorCS"),sQuery(id+"F4.wireOp",EDGE,"E62.2.MirrorCS"),sQuery(id+"F4.wireOp",EDGE,"E62.3.MirrorCS"),sQuery(id+"F4.wireOp",EDGE,"E62.4.MirrorCS"),sQuery(id+"F4.wireOp",EDGE,"E61.3.MirrorCS"),sQuery(id+"F4.wireOp",EDGE,"E61.6.MirrorCS"),sQuery(id+"F4.wireOp",EDGE,"E63.0.MirrorCS"),sQuery(id+"F4.wireOp",EDGE,"E64.1.MirrorCS"),sQuery(id+"F4.wireOp",EDGE,"E64.2.MirrorCS"),sQuery(id+"F4.wireOp",EDGE,"E64.3.MirrorCS"),sQuery(id+"F4.wireOp",EDGE,"E64.4.MirrorCS"),sQuery(id+"F4.wireOp",EDGE,"E64.5.MirrorCS"),sQuery(id+"F4.wireOp",EDGE,"E64.6.MirrorCS"),sQuery(id+"F4.wireOp",EDGE,"E65.0.MirrorCS"),sQuery(id+"F4.wireOp",EDGE,"E66.0.MirrorCS"),sQuery(id+"F4.wireOp",EDGE,"E67.trimOffspring"),sQuery(id+"F4.wireOp",EDGE,"E68.trimOffspring")])]}),"instanceName":"1"});
            var Q301;
            Q301=makeQuery(id+"F5.opExtrude","SWEPT_BODY",BODY,{"disambiguationData":[OSD([sQuery(id+"F4.wireOp",EDGE,"E24"),sQuery(id+"F4.wireOp",EDGE,"E25"),sQuery(id+"F4.wireOp",EDGE,"E27"),sQuery(id+"F4.wireOp",EDGE,"E28"),sQuery(id+"F4.wireOp",EDGE,"E29"),sQuery(id+"F4.wireOp",EDGE,"E30.0.MirrorCS"),sQuery(id+"F4.wireOp",EDGE,"E31.0.MirrorCS"),sQuery(id+"F4.wireOp",EDGE,"E32.0.MirrorCS"),sQuery(id+"F4.wireOp",EDGE,"E33.0.MirrorCS"),sQuery(id+"F4.wireOp",EDGE,"E34.0.MirrorCS"),sQuery(id+"F4.wireOp",EDGE,"E35.filletArc"),sQuery(id+"F4.wireOp",EDGE,"E36.filletArc"),sQuery(id+"F4.wireOp",EDGE,"E37"),sQuery(id+"F4.wireOp",EDGE,"E38"),sQuery(id+"F4.wireOp",EDGE,"E39"),sQuery(id+"F4.wireOp",EDGE,"E40"),sQuery(id+"F4.wireOp",EDGE,"E41"),sQuery(id+"F4.wireOp",EDGE,"E42"),sQuery(id+"F4.wireOp",EDGE,"E43.filletArc"),sQuery(id+"F4.wireOp",EDGE,"E44.filletArc"),sQuery(id+"F4.wireOp",EDGE,"E45.trimOffspring"),sQuery(id+"F4.wireOp",EDGE,"E46.trimOffspring"),sQuery(id+"F4.wireOp",EDGE,"E47"),sQuery(id+"F4.wireOp",EDGE,"E48"),sQuery(id+"F4.wireOp",EDGE,"E49"),sQuery(id+"F4.wireOp",EDGE,"E50"),sQuery(id+"F4.wireOp",EDGE,"E51"),sQuery(id+"F4.wireOp",EDGE,"E52"),sQuery(id+"F4.wireOp",EDGE,"E53"),sQuery(id+"F4.wireOp",EDGE,"E54.filletArc"),sQuery(id+"F4.wireOp",EDGE,"E55.filletArc"),sQuery(id+"F4.wireOp",EDGE,"E56.filletArc"),sQuery(id+"F4.wireOp",EDGE,"E57"),sQuery(id+"F4.wireOp",EDGE,"E58"),sQuery(id+"F4.wireOp",EDGE,"E59"),sQuery(id+"F4.wireOp",EDGE,"E60.trimOffspring"),sQuery(id+"F4.wireOp",EDGE,"E61.0.MirrorCS"),sQuery(id+"F4.wireOp",EDGE,"E61.1.MirrorCS"),sQuery(id+"F4.wireOp",EDGE,"E61.2.MirrorCS"),sQuery(id+"F4.wireOp",EDGE,"E61.4.MirrorCS"),sQuery(id+"F4.wireOp",EDGE,"E61.5.MirrorCS"),sQuery(id+"F4.wireOp",EDGE,"E61.7.MirrorCS"),sQuery(id+"F4.wireOp",EDGE,"E61.10.MirrorCS"),sQuery(id+"F4.wireOp",EDGE,"E62.0.MirrorCS"),sQuery(id+"F4.wireOp",EDGE,"E62.2.MirrorCS"),sQuery(id+"F4.wireOp",EDGE,"E62.3.MirrorCS"),sQuery(id+"F4.wireOp",EDGE,"E62.4.MirrorCS"),sQuery(id+"F4.wireOp",EDGE,"E61.3.MirrorCS"),sQuery(id+"F4.wireOp",EDGE,"E61.6.MirrorCS"),sQuery(id+"F4.wireOp",EDGE,"E63.0.MirrorCS"),sQuery(id+"F4.wireOp",EDGE,"E64.1.MirrorCS"),sQuery(id+"F4.wireOp",EDGE,"E64.2.MirrorCS"),sQuery(id+"F4.wireOp",EDGE,"E64.3.MirrorCS"),sQuery(id+"F4.wireOp",EDGE,"E64.4.MirrorCS"),sQuery(id+"F4.wireOp",EDGE,"E64.5.MirrorCS"),sQuery(id+"F4.wireOp",EDGE,"E64.6.MirrorCS"),sQuery(id+"F4.wireOp",EDGE,"E65.0.MirrorCS"),sQuery(id+"F4.wireOp",EDGE,"E66.0.MirrorCS"),sQuery(id+"F4.wireOp",EDGE,"E67.trimOffspring"),sQuery(id+"F4.wireOp",EDGE,"E68.trimOffspring")])]});
            var Q302;
            Q302=makeQuery(id+"F6.opPattern","COPY",BODY,{"derivedFrom":makeQuery(id+"F5.opExtrude","SWEPT_BODY",BODY,{"disambiguationData":[OSD([sQuery(id+"F4.wireOp",EDGE,"E24"),sQuery(id+"F4.wireOp",EDGE,"E25"),sQuery(id+"F4.wireOp",EDGE,"E27"),sQuery(id+"F4.wireOp",EDGE,"E28"),sQuery(id+"F4.wireOp",EDGE,"E29"),sQuery(id+"F4.wireOp",EDGE,"E30.0.MirrorCS"),sQuery(id+"F4.wireOp",EDGE,"E31.0.MirrorCS"),sQuery(id+"F4.wireOp",EDGE,"E32.0.MirrorCS"),sQuery(id+"F4.wireOp",EDGE,"E33.0.MirrorCS"),sQuery(id+"F4.wireOp",EDGE,"E34.0.MirrorCS"),sQuery(id+"F4.wireOp",EDGE,"E35.filletArc"),sQuery(id+"F4.wireOp",EDGE,"E36.filletArc"),sQuery(id+"F4.wireOp",EDGE,"E37"),sQuery(id+"F4.wireOp",EDGE,"E38"),sQuery(id+"F4.wireOp",EDGE,"E39"),sQuery(id+"F4.wireOp",EDGE,"E40"),sQuery(id+"F4.wireOp",EDGE,"E41"),sQuery(id+"F4.wireOp",EDGE,"E42"),sQuery(id+"F4.wireOp",EDGE,"E43.filletArc"),sQuery(id+"F4.wireOp",EDGE,"E44.filletArc"),sQuery(id+"F4.wireOp",EDGE,"E45.trimOffspring"),sQuery(id+"F4.wireOp",EDGE,"E46.trimOffspring"),sQuery(id+"F4.wireOp",EDGE,"E47"),sQuery(id+"F4.wireOp",EDGE,"E48"),sQuery(id+"F4.wireOp",EDGE,"E49"),sQuery(id+"F4.wireOp",EDGE,"E50"),sQuery(id+"F4.wireOp",EDGE,"E51"),sQuery(id+"F4.wireOp",EDGE,"E52"),sQuery(id+"F4.wireOp",EDGE,"E53"),sQuery(id+"F4.wireOp",EDGE,"E54.filletArc"),sQuery(id+"F4.wireOp",EDGE,"E55.filletArc"),sQuery(id+"F4.wireOp",EDGE,"E56.filletArc"),sQuery(id+"F4.wireOp",EDGE,"E57"),sQuery(id+"F4.wireOp",EDGE,"E58"),sQuery(id+"F4.wireOp",EDGE,"E59"),sQuery(id+"F4.wireOp",EDGE,"E60.trimOffspring"),sQuery(id+"F4.wireOp",EDGE,"E61.0.MirrorCS"),sQuery(id+"F4.wireOp",EDGE,"E61.1.MirrorCS"),sQuery(id+"F4.wireOp",EDGE,"E61.2.MirrorCS"),sQuery(id+"F4.wireOp",EDGE,"E61.4.MirrorCS"),sQuery(id+"F4.wireOp",EDGE,"E61.5.MirrorCS"),sQuery(id+"F4.wireOp",EDGE,"E61.7.MirrorCS"),sQuery(id+"F4.wireOp",EDGE,"E61.10.MirrorCS"),sQuery(id+"F4.wireOp",EDGE,"E62.0.MirrorCS"),sQuery(id+"F4.wireOp",EDGE,"E62.2.MirrorCS"),sQuery(id+"F4.wireOp",EDGE,"E62.3.MirrorCS"),sQuery(id+"F4.wireOp",EDGE,"E62.4.MirrorCS"),sQuery(id+"F4.wireOp",EDGE,"E61.3.MirrorCS"),sQuery(id+"F4.wireOp",EDGE,"E61.6.MirrorCS"),sQuery(id+"F4.wireOp",EDGE,"E63.0.MirrorCS"),sQuery(id+"F4.wireOp",EDGE,"E64.1.MirrorCS"),sQuery(id+"F4.wireOp",EDGE,"E64.2.MirrorCS"),sQuery(id+"F4.wireOp",EDGE,"E64.3.MirrorCS"),sQuery(id+"F4.wireOp",EDGE,"E64.4.MirrorCS"),sQuery(id+"F4.wireOp",EDGE,"E64.5.MirrorCS"),sQuery(id+"F4.wireOp",EDGE,"E64.6.MirrorCS"),sQuery(id+"F4.wireOp",EDGE,"E65.0.MirrorCS"),sQuery(id+"F4.wireOp",EDGE,"E66.0.MirrorCS"),sQuery(id+"F4.wireOp",EDGE,"E67.trimOffspring"),sQuery(id+"F4.wireOp",EDGE,"E68.trimOffspring")])]}),"instanceName":"49"});
            var Q303;
            Q303=makeQuery(id+"F6.opPattern","COPY",BODY,{"derivedFrom":makeQuery(id+"F5.opExtrude","SWEPT_BODY",BODY,{"disambiguationData":[OSD([sQuery(id+"F4.wireOp",EDGE,"E24"),sQuery(id+"F4.wireOp",EDGE,"E25"),sQuery(id+"F4.wireOp",EDGE,"E27"),sQuery(id+"F4.wireOp",EDGE,"E28"),sQuery(id+"F4.wireOp",EDGE,"E29"),sQuery(id+"F4.wireOp",EDGE,"E30.0.MirrorCS"),sQuery(id+"F4.wireOp",EDGE,"E31.0.MirrorCS"),sQuery(id+"F4.wireOp",EDGE,"E32.0.MirrorCS"),sQuery(id+"F4.wireOp",EDGE,"E33.0.MirrorCS"),sQuery(id+"F4.wireOp",EDGE,"E34.0.MirrorCS"),sQuery(id+"F4.wireOp",EDGE,"E35.filletArc"),sQuery(id+"F4.wireOp",EDGE,"E36.filletArc"),sQuery(id+"F4.wireOp",EDGE,"E37"),sQuery(id+"F4.wireOp",EDGE,"E38"),sQuery(id+"F4.wireOp",EDGE,"E39"),sQuery(id+"F4.wireOp",EDGE,"E40"),sQuery(id+"F4.wireOp",EDGE,"E41"),sQuery(id+"F4.wireOp",EDGE,"E42"),sQuery(id+"F4.wireOp",EDGE,"E43.filletArc"),sQuery(id+"F4.wireOp",EDGE,"E44.filletArc"),sQuery(id+"F4.wireOp",EDGE,"E45.trimOffspring"),sQuery(id+"F4.wireOp",EDGE,"E46.trimOffspring"),sQuery(id+"F4.wireOp",EDGE,"E47"),sQuery(id+"F4.wireOp",EDGE,"E48"),sQuery(id+"F4.wireOp",EDGE,"E49"),sQuery(id+"F4.wireOp",EDGE,"E50"),sQuery(id+"F4.wireOp",EDGE,"E51"),sQuery(id+"F4.wireOp",EDGE,"E52"),sQuery(id+"F4.wireOp",EDGE,"E53"),sQuery(id+"F4.wireOp",EDGE,"E54.filletArc"),sQuery(id+"F4.wireOp",EDGE,"E55.filletArc"),sQuery(id+"F4.wireOp",EDGE,"E56.filletArc"),sQuery(id+"F4.wireOp",EDGE,"E57"),sQuery(id+"F4.wireOp",EDGE,"E58"),sQuery(id+"F4.wireOp",EDGE,"E59"),sQuery(id+"F4.wireOp",EDGE,"E60.trimOffspring"),sQuery(id+"F4.wireOp",EDGE,"E61.0.MirrorCS"),sQuery(id+"F4.wireOp",EDGE,"E61.1.MirrorCS"),sQuery(id+"F4.wireOp",EDGE,"E61.2.MirrorCS"),sQuery(id+"F4.wireOp",EDGE,"E61.4.MirrorCS"),sQuery(id+"F4.wireOp",EDGE,"E61.5.MirrorCS"),sQuery(id+"F4.wireOp",EDGE,"E61.7.MirrorCS"),sQuery(id+"F4.wireOp",EDGE,"E61.10.MirrorCS"),sQuery(id+"F4.wireOp",EDGE,"E62.0.MirrorCS"),sQuery(id+"F4.wireOp",EDGE,"E62.2.MirrorCS"),sQuery(id+"F4.wireOp",EDGE,"E62.3.MirrorCS"),sQuery(id+"F4.wireOp",EDGE,"E62.4.MirrorCS"),sQuery(id+"F4.wireOp",EDGE,"E61.3.MirrorCS"),sQuery(id+"F4.wireOp",EDGE,"E61.6.MirrorCS"),sQuery(id+"F4.wireOp",EDGE,"E63.0.MirrorCS"),sQuery(id+"F4.wireOp",EDGE,"E64.1.MirrorCS"),sQuery(id+"F4.wireOp",EDGE,"E64.2.MirrorCS"),sQuery(id+"F4.wireOp",EDGE,"E64.3.MirrorCS"),sQuery(id+"F4.wireOp",EDGE,"E64.4.MirrorCS"),sQuery(id+"F4.wireOp",EDGE,"E64.5.MirrorCS"),sQuery(id+"F4.wireOp",EDGE,"E64.6.MirrorCS"),sQuery(id+"F4.wireOp",EDGE,"E65.0.MirrorCS"),sQuery(id+"F4.wireOp",EDGE,"E66.0.MirrorCS"),sQuery(id+"F4.wireOp",EDGE,"E67.trimOffspring"),sQuery(id+"F4.wireOp",EDGE,"E68.trimOffspring")])]}),"instanceName":"48"});
            var Q304;
            Q304=makeQuery(id+"F6.opPattern","COPY",BODY,{"derivedFrom":makeQuery(id+"F5.opExtrude","SWEPT_BODY",BODY,{"disambiguationData":[OSD([sQuery(id+"F4.wireOp",EDGE,"E24"),sQuery(id+"F4.wireOp",EDGE,"E25"),sQuery(id+"F4.wireOp",EDGE,"E27"),sQuery(id+"F4.wireOp",EDGE,"E28"),sQuery(id+"F4.wireOp",EDGE,"E29"),sQuery(id+"F4.wireOp",EDGE,"E30.0.MirrorCS"),sQuery(id+"F4.wireOp",EDGE,"E31.0.MirrorCS"),sQuery(id+"F4.wireOp",EDGE,"E32.0.MirrorCS"),sQuery(id+"F4.wireOp",EDGE,"E33.0.MirrorCS"),sQuery(id+"F4.wireOp",EDGE,"E34.0.MirrorCS"),sQuery(id+"F4.wireOp",EDGE,"E35.filletArc"),sQuery(id+"F4.wireOp",EDGE,"E36.filletArc"),sQuery(id+"F4.wireOp",EDGE,"E37"),sQuery(id+"F4.wireOp",EDGE,"E38"),sQuery(id+"F4.wireOp",EDGE,"E39"),sQuery(id+"F4.wireOp",EDGE,"E40"),sQuery(id+"F4.wireOp",EDGE,"E41"),sQuery(id+"F4.wireOp",EDGE,"E42"),sQuery(id+"F4.wireOp",EDGE,"E43.filletArc"),sQuery(id+"F4.wireOp",EDGE,"E44.filletArc"),sQuery(id+"F4.wireOp",EDGE,"E45.trimOffspring"),sQuery(id+"F4.wireOp",EDGE,"E46.trimOffspring"),sQuery(id+"F4.wireOp",EDGE,"E47"),sQuery(id+"F4.wireOp",EDGE,"E48"),sQuery(id+"F4.wireOp",EDGE,"E49"),sQuery(id+"F4.wireOp",EDGE,"E50"),sQuery(id+"F4.wireOp",EDGE,"E51"),sQuery(id+"F4.wireOp",EDGE,"E52"),sQuery(id+"F4.wireOp",EDGE,"E53"),sQuery(id+"F4.wireOp",EDGE,"E54.filletArc"),sQuery(id+"F4.wireOp",EDGE,"E55.filletArc"),sQuery(id+"F4.wireOp",EDGE,"E56.filletArc"),sQuery(id+"F4.wireOp",EDGE,"E57"),sQuery(id+"F4.wireOp",EDGE,"E58"),sQuery(id+"F4.wireOp",EDGE,"E59"),sQuery(id+"F4.wireOp",EDGE,"E60.trimOffspring"),sQuery(id+"F4.wireOp",EDGE,"E61.0.MirrorCS"),sQuery(id+"F4.wireOp",EDGE,"E61.1.MirrorCS"),sQuery(id+"F4.wireOp",EDGE,"E61.2.MirrorCS"),sQuery(id+"F4.wireOp",EDGE,"E61.4.MirrorCS"),sQuery(id+"F4.wireOp",EDGE,"E61.5.MirrorCS"),sQuery(id+"F4.wireOp",EDGE,"E61.7.MirrorCS"),sQuery(id+"F4.wireOp",EDGE,"E61.10.MirrorCS"),sQuery(id+"F4.wireOp",EDGE,"E62.0.MirrorCS"),sQuery(id+"F4.wireOp",EDGE,"E62.2.MirrorCS"),sQuery(id+"F4.wireOp",EDGE,"E62.3.MirrorCS"),sQuery(id+"F4.wireOp",EDGE,"E62.4.MirrorCS"),sQuery(id+"F4.wireOp",EDGE,"E61.3.MirrorCS"),sQuery(id+"F4.wireOp",EDGE,"E61.6.MirrorCS"),sQuery(id+"F4.wireOp",EDGE,"E63.0.MirrorCS"),sQuery(id+"F4.wireOp",EDGE,"E64.1.MirrorCS"),sQuery(id+"F4.wireOp",EDGE,"E64.2.MirrorCS"),sQuery(id+"F4.wireOp",EDGE,"E64.3.MirrorCS"),sQuery(id+"F4.wireOp",EDGE,"E64.4.MirrorCS"),sQuery(id+"F4.wireOp",EDGE,"E64.5.MirrorCS"),sQuery(id+"F4.wireOp",EDGE,"E64.6.MirrorCS"),sQuery(id+"F4.wireOp",EDGE,"E65.0.MirrorCS"),sQuery(id+"F4.wireOp",EDGE,"E66.0.MirrorCS"),sQuery(id+"F4.wireOp",EDGE,"E67.trimOffspring"),sQuery(id+"F4.wireOp",EDGE,"E68.trimOffspring")])]}),"instanceName":"47"});
            var Q305;
            Q305=makeQuery(id+"F6.opPattern","COPY",BODY,{"derivedFrom":makeQuery(id+"F5.opExtrude","SWEPT_BODY",BODY,{"disambiguationData":[OSD([sQuery(id+"F4.wireOp",EDGE,"E24"),sQuery(id+"F4.wireOp",EDGE,"E25"),sQuery(id+"F4.wireOp",EDGE,"E27"),sQuery(id+"F4.wireOp",EDGE,"E28"),sQuery(id+"F4.wireOp",EDGE,"E29"),sQuery(id+"F4.wireOp",EDGE,"E30.0.MirrorCS"),sQuery(id+"F4.wireOp",EDGE,"E31.0.MirrorCS"),sQuery(id+"F4.wireOp",EDGE,"E32.0.MirrorCS"),sQuery(id+"F4.wireOp",EDGE,"E33.0.MirrorCS"),sQuery(id+"F4.wireOp",EDGE,"E34.0.MirrorCS"),sQuery(id+"F4.wireOp",EDGE,"E35.filletArc"),sQuery(id+"F4.wireOp",EDGE,"E36.filletArc"),sQuery(id+"F4.wireOp",EDGE,"E37"),sQuery(id+"F4.wireOp",EDGE,"E38"),sQuery(id+"F4.wireOp",EDGE,"E39"),sQuery(id+"F4.wireOp",EDGE,"E40"),sQuery(id+"F4.wireOp",EDGE,"E41"),sQuery(id+"F4.wireOp",EDGE,"E42"),sQuery(id+"F4.wireOp",EDGE,"E43.filletArc"),sQuery(id+"F4.wireOp",EDGE,"E44.filletArc"),sQuery(id+"F4.wireOp",EDGE,"E45.trimOffspring"),sQuery(id+"F4.wireOp",EDGE,"E46.trimOffspring"),sQuery(id+"F4.wireOp",EDGE,"E47"),sQuery(id+"F4.wireOp",EDGE,"E48"),sQuery(id+"F4.wireOp",EDGE,"E49"),sQuery(id+"F4.wireOp",EDGE,"E50"),sQuery(id+"F4.wireOp",EDGE,"E51"),sQuery(id+"F4.wireOp",EDGE,"E52"),sQuery(id+"F4.wireOp",EDGE,"E53"),sQuery(id+"F4.wireOp",EDGE,"E54.filletArc"),sQuery(id+"F4.wireOp",EDGE,"E55.filletArc"),sQuery(id+"F4.wireOp",EDGE,"E56.filletArc"),sQuery(id+"F4.wireOp",EDGE,"E57"),sQuery(id+"F4.wireOp",EDGE,"E58"),sQuery(id+"F4.wireOp",EDGE,"E59"),sQuery(id+"F4.wireOp",EDGE,"E60.trimOffspring"),sQuery(id+"F4.wireOp",EDGE,"E61.0.MirrorCS"),sQuery(id+"F4.wireOp",EDGE,"E61.1.MirrorCS"),sQuery(id+"F4.wireOp",EDGE,"E61.2.MirrorCS"),sQuery(id+"F4.wireOp",EDGE,"E61.4.MirrorCS"),sQuery(id+"F4.wireOp",EDGE,"E61.5.MirrorCS"),sQuery(id+"F4.wireOp",EDGE,"E61.7.MirrorCS"),sQuery(id+"F4.wireOp",EDGE,"E61.10.MirrorCS"),sQuery(id+"F4.wireOp",EDGE,"E62.0.MirrorCS"),sQuery(id+"F4.wireOp",EDGE,"E62.2.MirrorCS"),sQuery(id+"F4.wireOp",EDGE,"E62.3.MirrorCS"),sQuery(id+"F4.wireOp",EDGE,"E62.4.MirrorCS"),sQuery(id+"F4.wireOp",EDGE,"E61.3.MirrorCS"),sQuery(id+"F4.wireOp",EDGE,"E61.6.MirrorCS"),sQuery(id+"F4.wireOp",EDGE,"E63.0.MirrorCS"),sQuery(id+"F4.wireOp",EDGE,"E64.1.MirrorCS"),sQuery(id+"F4.wireOp",EDGE,"E64.2.MirrorCS"),sQuery(id+"F4.wireOp",EDGE,"E64.3.MirrorCS"),sQuery(id+"F4.wireOp",EDGE,"E64.4.MirrorCS"),sQuery(id+"F4.wireOp",EDGE,"E64.5.MirrorCS"),sQuery(id+"F4.wireOp",EDGE,"E64.6.MirrorCS"),sQuery(id+"F4.wireOp",EDGE,"E65.0.MirrorCS"),sQuery(id+"F4.wireOp",EDGE,"E66.0.MirrorCS"),sQuery(id+"F4.wireOp",EDGE,"E67.trimOffspring"),sQuery(id+"F4.wireOp",EDGE,"E68.trimOffspring")])]}),"instanceName":"46"});
            var Q306;
            Q306=makeQuery(id+"F6.opPattern","COPY",BODY,{"derivedFrom":makeQuery(id+"F5.opExtrude","SWEPT_BODY",BODY,{"disambiguationData":[OSD([sQuery(id+"F4.wireOp",EDGE,"E24"),sQuery(id+"F4.wireOp",EDGE,"E25"),sQuery(id+"F4.wireOp",EDGE,"E27"),sQuery(id+"F4.wireOp",EDGE,"E28"),sQuery(id+"F4.wireOp",EDGE,"E29"),sQuery(id+"F4.wireOp",EDGE,"E30.0.MirrorCS"),sQuery(id+"F4.wireOp",EDGE,"E31.0.MirrorCS"),sQuery(id+"F4.wireOp",EDGE,"E32.0.MirrorCS"),sQuery(id+"F4.wireOp",EDGE,"E33.0.MirrorCS"),sQuery(id+"F4.wireOp",EDGE,"E34.0.MirrorCS"),sQuery(id+"F4.wireOp",EDGE,"E35.filletArc"),sQuery(id+"F4.wireOp",EDGE,"E36.filletArc"),sQuery(id+"F4.wireOp",EDGE,"E37"),sQuery(id+"F4.wireOp",EDGE,"E38"),sQuery(id+"F4.wireOp",EDGE,"E39"),sQuery(id+"F4.wireOp",EDGE,"E40"),sQuery(id+"F4.wireOp",EDGE,"E41"),sQuery(id+"F4.wireOp",EDGE,"E42"),sQuery(id+"F4.wireOp",EDGE,"E43.filletArc"),sQuery(id+"F4.wireOp",EDGE,"E44.filletArc"),sQuery(id+"F4.wireOp",EDGE,"E45.trimOffspring"),sQuery(id+"F4.wireOp",EDGE,"E46.trimOffspring"),sQuery(id+"F4.wireOp",EDGE,"E47"),sQuery(id+"F4.wireOp",EDGE,"E48"),sQuery(id+"F4.wireOp",EDGE,"E49"),sQuery(id+"F4.wireOp",EDGE,"E50"),sQuery(id+"F4.wireOp",EDGE,"E51"),sQuery(id+"F4.wireOp",EDGE,"E52"),sQuery(id+"F4.wireOp",EDGE,"E53"),sQuery(id+"F4.wireOp",EDGE,"E54.filletArc"),sQuery(id+"F4.wireOp",EDGE,"E55.filletArc"),sQuery(id+"F4.wireOp",EDGE,"E56.filletArc"),sQuery(id+"F4.wireOp",EDGE,"E57"),sQuery(id+"F4.wireOp",EDGE,"E58"),sQuery(id+"F4.wireOp",EDGE,"E59"),sQuery(id+"F4.wireOp",EDGE,"E60.trimOffspring"),sQuery(id+"F4.wireOp",EDGE,"E61.0.MirrorCS"),sQuery(id+"F4.wireOp",EDGE,"E61.1.MirrorCS"),sQuery(id+"F4.wireOp",EDGE,"E61.2.MirrorCS"),sQuery(id+"F4.wireOp",EDGE,"E61.4.MirrorCS"),sQuery(id+"F4.wireOp",EDGE,"E61.5.MirrorCS"),sQuery(id+"F4.wireOp",EDGE,"E61.7.MirrorCS"),sQuery(id+"F4.wireOp",EDGE,"E61.10.MirrorCS"),sQuery(id+"F4.wireOp",EDGE,"E62.0.MirrorCS"),sQuery(id+"F4.wireOp",EDGE,"E62.2.MirrorCS"),sQuery(id+"F4.wireOp",EDGE,"E62.3.MirrorCS"),sQuery(id+"F4.wireOp",EDGE,"E62.4.MirrorCS"),sQuery(id+"F4.wireOp",EDGE,"E61.3.MirrorCS"),sQuery(id+"F4.wireOp",EDGE,"E61.6.MirrorCS"),sQuery(id+"F4.wireOp",EDGE,"E63.0.MirrorCS"),sQuery(id+"F4.wireOp",EDGE,"E64.1.MirrorCS"),sQuery(id+"F4.wireOp",EDGE,"E64.2.MirrorCS"),sQuery(id+"F4.wireOp",EDGE,"E64.3.MirrorCS"),sQuery(id+"F4.wireOp",EDGE,"E64.4.MirrorCS"),sQuery(id+"F4.wireOp",EDGE,"E64.5.MirrorCS"),sQuery(id+"F4.wireOp",EDGE,"E64.6.MirrorCS"),sQuery(id+"F4.wireOp",EDGE,"E65.0.MirrorCS"),sQuery(id+"F4.wireOp",EDGE,"E66.0.MirrorCS"),sQuery(id+"F4.wireOp",EDGE,"E67.trimOffspring"),sQuery(id+"F4.wireOp",EDGE,"E68.trimOffspring")])]}),"instanceName":"45"});
            var Q307;
            Q307=makeQuery(id+"F6.opPattern","COPY",BODY,{"derivedFrom":makeQuery(id+"F5.opExtrude","SWEPT_BODY",BODY,{"disambiguationData":[OSD([sQuery(id+"F4.wireOp",EDGE,"E24"),sQuery(id+"F4.wireOp",EDGE,"E25"),sQuery(id+"F4.wireOp",EDGE,"E27"),sQuery(id+"F4.wireOp",EDGE,"E28"),sQuery(id+"F4.wireOp",EDGE,"E29"),sQuery(id+"F4.wireOp",EDGE,"E30.0.MirrorCS"),sQuery(id+"F4.wireOp",EDGE,"E31.0.MirrorCS"),sQuery(id+"F4.wireOp",EDGE,"E32.0.MirrorCS"),sQuery(id+"F4.wireOp",EDGE,"E33.0.MirrorCS"),sQuery(id+"F4.wireOp",EDGE,"E34.0.MirrorCS"),sQuery(id+"F4.wireOp",EDGE,"E35.filletArc"),sQuery(id+"F4.wireOp",EDGE,"E36.filletArc"),sQuery(id+"F4.wireOp",EDGE,"E37"),sQuery(id+"F4.wireOp",EDGE,"E38"),sQuery(id+"F4.wireOp",EDGE,"E39"),sQuery(id+"F4.wireOp",EDGE,"E40"),sQuery(id+"F4.wireOp",EDGE,"E41"),sQuery(id+"F4.wireOp",EDGE,"E42"),sQuery(id+"F4.wireOp",EDGE,"E43.filletArc"),sQuery(id+"F4.wireOp",EDGE,"E44.filletArc"),sQuery(id+"F4.wireOp",EDGE,"E45.trimOffspring"),sQuery(id+"F4.wireOp",EDGE,"E46.trimOffspring"),sQuery(id+"F4.wireOp",EDGE,"E47"),sQuery(id+"F4.wireOp",EDGE,"E48"),sQuery(id+"F4.wireOp",EDGE,"E49"),sQuery(id+"F4.wireOp",EDGE,"E50"),sQuery(id+"F4.wireOp",EDGE,"E51"),sQuery(id+"F4.wireOp",EDGE,"E52"),sQuery(id+"F4.wireOp",EDGE,"E53"),sQuery(id+"F4.wireOp",EDGE,"E54.filletArc"),sQuery(id+"F4.wireOp",EDGE,"E55.filletArc"),sQuery(id+"F4.wireOp",EDGE,"E56.filletArc"),sQuery(id+"F4.wireOp",EDGE,"E57"),sQuery(id+"F4.wireOp",EDGE,"E58"),sQuery(id+"F4.wireOp",EDGE,"E59"),sQuery(id+"F4.wireOp",EDGE,"E60.trimOffspring"),sQuery(id+"F4.wireOp",EDGE,"E61.0.MirrorCS"),sQuery(id+"F4.wireOp",EDGE,"E61.1.MirrorCS"),sQuery(id+"F4.wireOp",EDGE,"E61.2.MirrorCS"),sQuery(id+"F4.wireOp",EDGE,"E61.4.MirrorCS"),sQuery(id+"F4.wireOp",EDGE,"E61.5.MirrorCS"),sQuery(id+"F4.wireOp",EDGE,"E61.7.MirrorCS"),sQuery(id+"F4.wireOp",EDGE,"E61.10.MirrorCS"),sQuery(id+"F4.wireOp",EDGE,"E62.0.MirrorCS"),sQuery(id+"F4.wireOp",EDGE,"E62.2.MirrorCS"),sQuery(id+"F4.wireOp",EDGE,"E62.3.MirrorCS"),sQuery(id+"F4.wireOp",EDGE,"E62.4.MirrorCS"),sQuery(id+"F4.wireOp",EDGE,"E61.3.MirrorCS"),sQuery(id+"F4.wireOp",EDGE,"E61.6.MirrorCS"),sQuery(id+"F4.wireOp",EDGE,"E63.0.MirrorCS"),sQuery(id+"F4.wireOp",EDGE,"E64.1.MirrorCS"),sQuery(id+"F4.wireOp",EDGE,"E64.2.MirrorCS"),sQuery(id+"F4.wireOp",EDGE,"E64.3.MirrorCS"),sQuery(id+"F4.wireOp",EDGE,"E64.4.MirrorCS"),sQuery(id+"F4.wireOp",EDGE,"E64.5.MirrorCS"),sQuery(id+"F4.wireOp",EDGE,"E64.6.MirrorCS"),sQuery(id+"F4.wireOp",EDGE,"E65.0.MirrorCS"),sQuery(id+"F4.wireOp",EDGE,"E66.0.MirrorCS"),sQuery(id+"F4.wireOp",EDGE,"E67.trimOffspring"),sQuery(id+"F4.wireOp",EDGE,"E68.trimOffspring")])]}),"instanceName":"44"});
            var Q308;
            Q308=makeQuery(id+"F6.opPattern","COPY",BODY,{"derivedFrom":makeQuery(id+"F5.opExtrude","SWEPT_BODY",BODY,{"disambiguationData":[OSD([sQuery(id+"F4.wireOp",EDGE,"E24"),sQuery(id+"F4.wireOp",EDGE,"E25"),sQuery(id+"F4.wireOp",EDGE,"E27"),sQuery(id+"F4.wireOp",EDGE,"E28"),sQuery(id+"F4.wireOp",EDGE,"E29"),sQuery(id+"F4.wireOp",EDGE,"E30.0.MirrorCS"),sQuery(id+"F4.wireOp",EDGE,"E31.0.MirrorCS"),sQuery(id+"F4.wireOp",EDGE,"E32.0.MirrorCS"),sQuery(id+"F4.wireOp",EDGE,"E33.0.MirrorCS"),sQuery(id+"F4.wireOp",EDGE,"E34.0.MirrorCS"),sQuery(id+"F4.wireOp",EDGE,"E35.filletArc"),sQuery(id+"F4.wireOp",EDGE,"E36.filletArc"),sQuery(id+"F4.wireOp",EDGE,"E37"),sQuery(id+"F4.wireOp",EDGE,"E38"),sQuery(id+"F4.wireOp",EDGE,"E39"),sQuery(id+"F4.wireOp",EDGE,"E40"),sQuery(id+"F4.wireOp",EDGE,"E41"),sQuery(id+"F4.wireOp",EDGE,"E42"),sQuery(id+"F4.wireOp",EDGE,"E43.filletArc"),sQuery(id+"F4.wireOp",EDGE,"E44.filletArc"),sQuery(id+"F4.wireOp",EDGE,"E45.trimOffspring"),sQuery(id+"F4.wireOp",EDGE,"E46.trimOffspring"),sQuery(id+"F4.wireOp",EDGE,"E47"),sQuery(id+"F4.wireOp",EDGE,"E48"),sQuery(id+"F4.wireOp",EDGE,"E49"),sQuery(id+"F4.wireOp",EDGE,"E50"),sQuery(id+"F4.wireOp",EDGE,"E51"),sQuery(id+"F4.wireOp",EDGE,"E52"),sQuery(id+"F4.wireOp",EDGE,"E53"),sQuery(id+"F4.wireOp",EDGE,"E54.filletArc"),sQuery(id+"F4.wireOp",EDGE,"E55.filletArc"),sQuery(id+"F4.wireOp",EDGE,"E56.filletArc"),sQuery(id+"F4.wireOp",EDGE,"E57"),sQuery(id+"F4.wireOp",EDGE,"E58"),sQuery(id+"F4.wireOp",EDGE,"E59"),sQuery(id+"F4.wireOp",EDGE,"E60.trimOffspring"),sQuery(id+"F4.wireOp",EDGE,"E61.0.MirrorCS"),sQuery(id+"F4.wireOp",EDGE,"E61.1.MirrorCS"),sQuery(id+"F4.wireOp",EDGE,"E61.2.MirrorCS"),sQuery(id+"F4.wireOp",EDGE,"E61.4.MirrorCS"),sQuery(id+"F4.wireOp",EDGE,"E61.5.MirrorCS"),sQuery(id+"F4.wireOp",EDGE,"E61.7.MirrorCS"),sQuery(id+"F4.wireOp",EDGE,"E61.10.MirrorCS"),sQuery(id+"F4.wireOp",EDGE,"E62.0.MirrorCS"),sQuery(id+"F4.wireOp",EDGE,"E62.2.MirrorCS"),sQuery(id+"F4.wireOp",EDGE,"E62.3.MirrorCS"),sQuery(id+"F4.wireOp",EDGE,"E62.4.MirrorCS"),sQuery(id+"F4.wireOp",EDGE,"E61.3.MirrorCS"),sQuery(id+"F4.wireOp",EDGE,"E61.6.MirrorCS"),sQuery(id+"F4.wireOp",EDGE,"E63.0.MirrorCS"),sQuery(id+"F4.wireOp",EDGE,"E64.1.MirrorCS"),sQuery(id+"F4.wireOp",EDGE,"E64.2.MirrorCS"),sQuery(id+"F4.wireOp",EDGE,"E64.3.MirrorCS"),sQuery(id+"F4.wireOp",EDGE,"E64.4.MirrorCS"),sQuery(id+"F4.wireOp",EDGE,"E64.5.MirrorCS"),sQuery(id+"F4.wireOp",EDGE,"E64.6.MirrorCS"),sQuery(id+"F4.wireOp",EDGE,"E65.0.MirrorCS"),sQuery(id+"F4.wireOp",EDGE,"E66.0.MirrorCS"),sQuery(id+"F4.wireOp",EDGE,"E67.trimOffspring"),sQuery(id+"F4.wireOp",EDGE,"E68.trimOffspring")])]}),"instanceName":"43"});
            var Q309;
            Q309=makeQuery(id+"F6.opPattern","COPY",BODY,{"derivedFrom":makeQuery(id+"F5.opExtrude","SWEPT_BODY",BODY,{"disambiguationData":[OSD([sQuery(id+"F4.wireOp",EDGE,"E24"),sQuery(id+"F4.wireOp",EDGE,"E25"),sQuery(id+"F4.wireOp",EDGE,"E27"),sQuery(id+"F4.wireOp",EDGE,"E28"),sQuery(id+"F4.wireOp",EDGE,"E29"),sQuery(id+"F4.wireOp",EDGE,"E30.0.MirrorCS"),sQuery(id+"F4.wireOp",EDGE,"E31.0.MirrorCS"),sQuery(id+"F4.wireOp",EDGE,"E32.0.MirrorCS"),sQuery(id+"F4.wireOp",EDGE,"E33.0.MirrorCS"),sQuery(id+"F4.wireOp",EDGE,"E34.0.MirrorCS"),sQuery(id+"F4.wireOp",EDGE,"E35.filletArc"),sQuery(id+"F4.wireOp",EDGE,"E36.filletArc"),sQuery(id+"F4.wireOp",EDGE,"E37"),sQuery(id+"F4.wireOp",EDGE,"E38"),sQuery(id+"F4.wireOp",EDGE,"E39"),sQuery(id+"F4.wireOp",EDGE,"E40"),sQuery(id+"F4.wireOp",EDGE,"E41"),sQuery(id+"F4.wireOp",EDGE,"E42"),sQuery(id+"F4.wireOp",EDGE,"E43.filletArc"),sQuery(id+"F4.wireOp",EDGE,"E44.filletArc"),sQuery(id+"F4.wireOp",EDGE,"E45.trimOffspring"),sQuery(id+"F4.wireOp",EDGE,"E46.trimOffspring"),sQuery(id+"F4.wireOp",EDGE,"E47"),sQuery(id+"F4.wireOp",EDGE,"E48"),sQuery(id+"F4.wireOp",EDGE,"E49"),sQuery(id+"F4.wireOp",EDGE,"E50"),sQuery(id+"F4.wireOp",EDGE,"E51"),sQuery(id+"F4.wireOp",EDGE,"E52"),sQuery(id+"F4.wireOp",EDGE,"E53"),sQuery(id+"F4.wireOp",EDGE,"E54.filletArc"),sQuery(id+"F4.wireOp",EDGE,"E55.filletArc"),sQuery(id+"F4.wireOp",EDGE,"E56.filletArc"),sQuery(id+"F4.wireOp",EDGE,"E57"),sQuery(id+"F4.wireOp",EDGE,"E58"),sQuery(id+"F4.wireOp",EDGE,"E59"),sQuery(id+"F4.wireOp",EDGE,"E60.trimOffspring"),sQuery(id+"F4.wireOp",EDGE,"E61.0.MirrorCS"),sQuery(id+"F4.wireOp",EDGE,"E61.1.MirrorCS"),sQuery(id+"F4.wireOp",EDGE,"E61.2.MirrorCS"),sQuery(id+"F4.wireOp",EDGE,"E61.4.MirrorCS"),sQuery(id+"F4.wireOp",EDGE,"E61.5.MirrorCS"),sQuery(id+"F4.wireOp",EDGE,"E61.7.MirrorCS"),sQuery(id+"F4.wireOp",EDGE,"E61.10.MirrorCS"),sQuery(id+"F4.wireOp",EDGE,"E62.0.MirrorCS"),sQuery(id+"F4.wireOp",EDGE,"E62.2.MirrorCS"),sQuery(id+"F4.wireOp",EDGE,"E62.3.MirrorCS"),sQuery(id+"F4.wireOp",EDGE,"E62.4.MirrorCS"),sQuery(id+"F4.wireOp",EDGE,"E61.3.MirrorCS"),sQuery(id+"F4.wireOp",EDGE,"E61.6.MirrorCS"),sQuery(id+"F4.wireOp",EDGE,"E63.0.MirrorCS"),sQuery(id+"F4.wireOp",EDGE,"E64.1.MirrorCS"),sQuery(id+"F4.wireOp",EDGE,"E64.2.MirrorCS"),sQuery(id+"F4.wireOp",EDGE,"E64.3.MirrorCS"),sQuery(id+"F4.wireOp",EDGE,"E64.4.MirrorCS"),sQuery(id+"F4.wireOp",EDGE,"E64.5.MirrorCS"),sQuery(id+"F4.wireOp",EDGE,"E64.6.MirrorCS"),sQuery(id+"F4.wireOp",EDGE,"E65.0.MirrorCS"),sQuery(id+"F4.wireOp",EDGE,"E66.0.MirrorCS"),sQuery(id+"F4.wireOp",EDGE,"E67.trimOffspring"),sQuery(id+"F4.wireOp",EDGE,"E68.trimOffspring")])]}),"instanceName":"42"});
            var Q310;
            Q310=makeQuery(id+"F6.opPattern","COPY",BODY,{"derivedFrom":makeQuery(id+"F5.opExtrude","SWEPT_BODY",BODY,{"disambiguationData":[OSD([sQuery(id+"F4.wireOp",EDGE,"E24"),sQuery(id+"F4.wireOp",EDGE,"E25"),sQuery(id+"F4.wireOp",EDGE,"E27"),sQuery(id+"F4.wireOp",EDGE,"E28"),sQuery(id+"F4.wireOp",EDGE,"E29"),sQuery(id+"F4.wireOp",EDGE,"E30.0.MirrorCS"),sQuery(id+"F4.wireOp",EDGE,"E31.0.MirrorCS"),sQuery(id+"F4.wireOp",EDGE,"E32.0.MirrorCS"),sQuery(id+"F4.wireOp",EDGE,"E33.0.MirrorCS"),sQuery(id+"F4.wireOp",EDGE,"E34.0.MirrorCS"),sQuery(id+"F4.wireOp",EDGE,"E35.filletArc"),sQuery(id+"F4.wireOp",EDGE,"E36.filletArc"),sQuery(id+"F4.wireOp",EDGE,"E37"),sQuery(id+"F4.wireOp",EDGE,"E38"),sQuery(id+"F4.wireOp",EDGE,"E39"),sQuery(id+"F4.wireOp",EDGE,"E40"),sQuery(id+"F4.wireOp",EDGE,"E41"),sQuery(id+"F4.wireOp",EDGE,"E42"),sQuery(id+"F4.wireOp",EDGE,"E43.filletArc"),sQuery(id+"F4.wireOp",EDGE,"E44.filletArc"),sQuery(id+"F4.wireOp",EDGE,"E45.trimOffspring"),sQuery(id+"F4.wireOp",EDGE,"E46.trimOffspring"),sQuery(id+"F4.wireOp",EDGE,"E47"),sQuery(id+"F4.wireOp",EDGE,"E48"),sQuery(id+"F4.wireOp",EDGE,"E49"),sQuery(id+"F4.wireOp",EDGE,"E50"),sQuery(id+"F4.wireOp",EDGE,"E51"),sQuery(id+"F4.wireOp",EDGE,"E52"),sQuery(id+"F4.wireOp",EDGE,"E53"),sQuery(id+"F4.wireOp",EDGE,"E54.filletArc"),sQuery(id+"F4.wireOp",EDGE,"E55.filletArc"),sQuery(id+"F4.wireOp",EDGE,"E56.filletArc"),sQuery(id+"F4.wireOp",EDGE,"E57"),sQuery(id+"F4.wireOp",EDGE,"E58"),sQuery(id+"F4.wireOp",EDGE,"E59"),sQuery(id+"F4.wireOp",EDGE,"E60.trimOffspring"),sQuery(id+"F4.wireOp",EDGE,"E61.0.MirrorCS"),sQuery(id+"F4.wireOp",EDGE,"E61.1.MirrorCS"),sQuery(id+"F4.wireOp",EDGE,"E61.2.MirrorCS"),sQuery(id+"F4.wireOp",EDGE,"E61.4.MirrorCS"),sQuery(id+"F4.wireOp",EDGE,"E61.5.MirrorCS"),sQuery(id+"F4.wireOp",EDGE,"E61.7.MirrorCS"),sQuery(id+"F4.wireOp",EDGE,"E61.10.MirrorCS"),sQuery(id+"F4.wireOp",EDGE,"E62.0.MirrorCS"),sQuery(id+"F4.wireOp",EDGE,"E62.2.MirrorCS"),sQuery(id+"F4.wireOp",EDGE,"E62.3.MirrorCS"),sQuery(id+"F4.wireOp",EDGE,"E62.4.MirrorCS"),sQuery(id+"F4.wireOp",EDGE,"E61.3.MirrorCS"),sQuery(id+"F4.wireOp",EDGE,"E61.6.MirrorCS"),sQuery(id+"F4.wireOp",EDGE,"E63.0.MirrorCS"),sQuery(id+"F4.wireOp",EDGE,"E64.1.MirrorCS"),sQuery(id+"F4.wireOp",EDGE,"E64.2.MirrorCS"),sQuery(id+"F4.wireOp",EDGE,"E64.3.MirrorCS"),sQuery(id+"F4.wireOp",EDGE,"E64.4.MirrorCS"),sQuery(id+"F4.wireOp",EDGE,"E64.5.MirrorCS"),sQuery(id+"F4.wireOp",EDGE,"E64.6.MirrorCS"),sQuery(id+"F4.wireOp",EDGE,"E65.0.MirrorCS"),sQuery(id+"F4.wireOp",EDGE,"E66.0.MirrorCS"),sQuery(id+"F4.wireOp",EDGE,"E67.trimOffspring"),sQuery(id+"F4.wireOp",EDGE,"E68.trimOffspring")])]}),"instanceName":"41"});
            var Q311;
            Q311=makeQuery(id+"F6.opPattern","COPY",BODY,{"derivedFrom":makeQuery(id+"F5.opExtrude","SWEPT_BODY",BODY,{"disambiguationData":[OSD([sQuery(id+"F4.wireOp",EDGE,"E24"),sQuery(id+"F4.wireOp",EDGE,"E25"),sQuery(id+"F4.wireOp",EDGE,"E27"),sQuery(id+"F4.wireOp",EDGE,"E28"),sQuery(id+"F4.wireOp",EDGE,"E29"),sQuery(id+"F4.wireOp",EDGE,"E30.0.MirrorCS"),sQuery(id+"F4.wireOp",EDGE,"E31.0.MirrorCS"),sQuery(id+"F4.wireOp",EDGE,"E32.0.MirrorCS"),sQuery(id+"F4.wireOp",EDGE,"E33.0.MirrorCS"),sQuery(id+"F4.wireOp",EDGE,"E34.0.MirrorCS"),sQuery(id+"F4.wireOp",EDGE,"E35.filletArc"),sQuery(id+"F4.wireOp",EDGE,"E36.filletArc"),sQuery(id+"F4.wireOp",EDGE,"E37"),sQuery(id+"F4.wireOp",EDGE,"E38"),sQuery(id+"F4.wireOp",EDGE,"E39"),sQuery(id+"F4.wireOp",EDGE,"E40"),sQuery(id+"F4.wireOp",EDGE,"E41"),sQuery(id+"F4.wireOp",EDGE,"E42"),sQuery(id+"F4.wireOp",EDGE,"E43.filletArc"),sQuery(id+"F4.wireOp",EDGE,"E44.filletArc"),sQuery(id+"F4.wireOp",EDGE,"E45.trimOffspring"),sQuery(id+"F4.wireOp",EDGE,"E46.trimOffspring"),sQuery(id+"F4.wireOp",EDGE,"E47"),sQuery(id+"F4.wireOp",EDGE,"E48"),sQuery(id+"F4.wireOp",EDGE,"E49"),sQuery(id+"F4.wireOp",EDGE,"E50"),sQuery(id+"F4.wireOp",EDGE,"E51"),sQuery(id+"F4.wireOp",EDGE,"E52"),sQuery(id+"F4.wireOp",EDGE,"E53"),sQuery(id+"F4.wireOp",EDGE,"E54.filletArc"),sQuery(id+"F4.wireOp",EDGE,"E55.filletArc"),sQuery(id+"F4.wireOp",EDGE,"E56.filletArc"),sQuery(id+"F4.wireOp",EDGE,"E57"),sQuery(id+"F4.wireOp",EDGE,"E58"),sQuery(id+"F4.wireOp",EDGE,"E59"),sQuery(id+"F4.wireOp",EDGE,"E60.trimOffspring"),sQuery(id+"F4.wireOp",EDGE,"E61.0.MirrorCS"),sQuery(id+"F4.wireOp",EDGE,"E61.1.MirrorCS"),sQuery(id+"F4.wireOp",EDGE,"E61.2.MirrorCS"),sQuery(id+"F4.wireOp",EDGE,"E61.4.MirrorCS"),sQuery(id+"F4.wireOp",EDGE,"E61.5.MirrorCS"),sQuery(id+"F4.wireOp",EDGE,"E61.7.MirrorCS"),sQuery(id+"F4.wireOp",EDGE,"E61.10.MirrorCS"),sQuery(id+"F4.wireOp",EDGE,"E62.0.MirrorCS"),sQuery(id+"F4.wireOp",EDGE,"E62.2.MirrorCS"),sQuery(id+"F4.wireOp",EDGE,"E62.3.MirrorCS"),sQuery(id+"F4.wireOp",EDGE,"E62.4.MirrorCS"),sQuery(id+"F4.wireOp",EDGE,"E61.3.MirrorCS"),sQuery(id+"F4.wireOp",EDGE,"E61.6.MirrorCS"),sQuery(id+"F4.wireOp",EDGE,"E63.0.MirrorCS"),sQuery(id+"F4.wireOp",EDGE,"E64.1.MirrorCS"),sQuery(id+"F4.wireOp",EDGE,"E64.2.MirrorCS"),sQuery(id+"F4.wireOp",EDGE,"E64.3.MirrorCS"),sQuery(id+"F4.wireOp",EDGE,"E64.4.MirrorCS"),sQuery(id+"F4.wireOp",EDGE,"E64.5.MirrorCS"),sQuery(id+"F4.wireOp",EDGE,"E64.6.MirrorCS"),sQuery(id+"F4.wireOp",EDGE,"E65.0.MirrorCS"),sQuery(id+"F4.wireOp",EDGE,"E66.0.MirrorCS"),sQuery(id+"F4.wireOp",EDGE,"E67.trimOffspring"),sQuery(id+"F4.wireOp",EDGE,"E68.trimOffspring")])]}),"instanceName":"40"});
            var Q312;
            Q312=makeQuery(id+"F6.opPattern","COPY",BODY,{"derivedFrom":makeQuery(id+"F5.opExtrude","SWEPT_BODY",BODY,{"disambiguationData":[OSD([sQuery(id+"F4.wireOp",EDGE,"E24"),sQuery(id+"F4.wireOp",EDGE,"E25"),sQuery(id+"F4.wireOp",EDGE,"E27"),sQuery(id+"F4.wireOp",EDGE,"E28"),sQuery(id+"F4.wireOp",EDGE,"E29"),sQuery(id+"F4.wireOp",EDGE,"E30.0.MirrorCS"),sQuery(id+"F4.wireOp",EDGE,"E31.0.MirrorCS"),sQuery(id+"F4.wireOp",EDGE,"E32.0.MirrorCS"),sQuery(id+"F4.wireOp",EDGE,"E33.0.MirrorCS"),sQuery(id+"F4.wireOp",EDGE,"E34.0.MirrorCS"),sQuery(id+"F4.wireOp",EDGE,"E35.filletArc"),sQuery(id+"F4.wireOp",EDGE,"E36.filletArc"),sQuery(id+"F4.wireOp",EDGE,"E37"),sQuery(id+"F4.wireOp",EDGE,"E38"),sQuery(id+"F4.wireOp",EDGE,"E39"),sQuery(id+"F4.wireOp",EDGE,"E40"),sQuery(id+"F4.wireOp",EDGE,"E41"),sQuery(id+"F4.wireOp",EDGE,"E42"),sQuery(id+"F4.wireOp",EDGE,"E43.filletArc"),sQuery(id+"F4.wireOp",EDGE,"E44.filletArc"),sQuery(id+"F4.wireOp",EDGE,"E45.trimOffspring"),sQuery(id+"F4.wireOp",EDGE,"E46.trimOffspring"),sQuery(id+"F4.wireOp",EDGE,"E47"),sQuery(id+"F4.wireOp",EDGE,"E48"),sQuery(id+"F4.wireOp",EDGE,"E49"),sQuery(id+"F4.wireOp",EDGE,"E50"),sQuery(id+"F4.wireOp",EDGE,"E51"),sQuery(id+"F4.wireOp",EDGE,"E52"),sQuery(id+"F4.wireOp",EDGE,"E53"),sQuery(id+"F4.wireOp",EDGE,"E54.filletArc"),sQuery(id+"F4.wireOp",EDGE,"E55.filletArc"),sQuery(id+"F4.wireOp",EDGE,"E56.filletArc"),sQuery(id+"F4.wireOp",EDGE,"E57"),sQuery(id+"F4.wireOp",EDGE,"E58"),sQuery(id+"F4.wireOp",EDGE,"E59"),sQuery(id+"F4.wireOp",EDGE,"E60.trimOffspring"),sQuery(id+"F4.wireOp",EDGE,"E61.0.MirrorCS"),sQuery(id+"F4.wireOp",EDGE,"E61.1.MirrorCS"),sQuery(id+"F4.wireOp",EDGE,"E61.2.MirrorCS"),sQuery(id+"F4.wireOp",EDGE,"E61.4.MirrorCS"),sQuery(id+"F4.wireOp",EDGE,"E61.5.MirrorCS"),sQuery(id+"F4.wireOp",EDGE,"E61.7.MirrorCS"),sQuery(id+"F4.wireOp",EDGE,"E61.10.MirrorCS"),sQuery(id+"F4.wireOp",EDGE,"E62.0.MirrorCS"),sQuery(id+"F4.wireOp",EDGE,"E62.2.MirrorCS"),sQuery(id+"F4.wireOp",EDGE,"E62.3.MirrorCS"),sQuery(id+"F4.wireOp",EDGE,"E62.4.MirrorCS"),sQuery(id+"F4.wireOp",EDGE,"E61.3.MirrorCS"),sQuery(id+"F4.wireOp",EDGE,"E61.6.MirrorCS"),sQuery(id+"F4.wireOp",EDGE,"E63.0.MirrorCS"),sQuery(id+"F4.wireOp",EDGE,"E64.1.MirrorCS"),sQuery(id+"F4.wireOp",EDGE,"E64.2.MirrorCS"),sQuery(id+"F4.wireOp",EDGE,"E64.3.MirrorCS"),sQuery(id+"F4.wireOp",EDGE,"E64.4.MirrorCS"),sQuery(id+"F4.wireOp",EDGE,"E64.5.MirrorCS"),sQuery(id+"F4.wireOp",EDGE,"E64.6.MirrorCS"),sQuery(id+"F4.wireOp",EDGE,"E65.0.MirrorCS"),sQuery(id+"F4.wireOp",EDGE,"E66.0.MirrorCS"),sQuery(id+"F4.wireOp",EDGE,"E67.trimOffspring"),sQuery(id+"F4.wireOp",EDGE,"E68.trimOffspring")])]}),"instanceName":"38"});
            var Q313;
            Q313=makeQuery(id+"F6.opPattern","COPY",BODY,{"derivedFrom":makeQuery(id+"F5.opExtrude","SWEPT_BODY",BODY,{"disambiguationData":[OSD([sQuery(id+"F4.wireOp",EDGE,"E24"),sQuery(id+"F4.wireOp",EDGE,"E25"),sQuery(id+"F4.wireOp",EDGE,"E27"),sQuery(id+"F4.wireOp",EDGE,"E28"),sQuery(id+"F4.wireOp",EDGE,"E29"),sQuery(id+"F4.wireOp",EDGE,"E30.0.MirrorCS"),sQuery(id+"F4.wireOp",EDGE,"E31.0.MirrorCS"),sQuery(id+"F4.wireOp",EDGE,"E32.0.MirrorCS"),sQuery(id+"F4.wireOp",EDGE,"E33.0.MirrorCS"),sQuery(id+"F4.wireOp",EDGE,"E34.0.MirrorCS"),sQuery(id+"F4.wireOp",EDGE,"E35.filletArc"),sQuery(id+"F4.wireOp",EDGE,"E36.filletArc"),sQuery(id+"F4.wireOp",EDGE,"E37"),sQuery(id+"F4.wireOp",EDGE,"E38"),sQuery(id+"F4.wireOp",EDGE,"E39"),sQuery(id+"F4.wireOp",EDGE,"E40"),sQuery(id+"F4.wireOp",EDGE,"E41"),sQuery(id+"F4.wireOp",EDGE,"E42"),sQuery(id+"F4.wireOp",EDGE,"E43.filletArc"),sQuery(id+"F4.wireOp",EDGE,"E44.filletArc"),sQuery(id+"F4.wireOp",EDGE,"E45.trimOffspring"),sQuery(id+"F4.wireOp",EDGE,"E46.trimOffspring"),sQuery(id+"F4.wireOp",EDGE,"E47"),sQuery(id+"F4.wireOp",EDGE,"E48"),sQuery(id+"F4.wireOp",EDGE,"E49"),sQuery(id+"F4.wireOp",EDGE,"E50"),sQuery(id+"F4.wireOp",EDGE,"E51"),sQuery(id+"F4.wireOp",EDGE,"E52"),sQuery(id+"F4.wireOp",EDGE,"E53"),sQuery(id+"F4.wireOp",EDGE,"E54.filletArc"),sQuery(id+"F4.wireOp",EDGE,"E55.filletArc"),sQuery(id+"F4.wireOp",EDGE,"E56.filletArc"),sQuery(id+"F4.wireOp",EDGE,"E57"),sQuery(id+"F4.wireOp",EDGE,"E58"),sQuery(id+"F4.wireOp",EDGE,"E59"),sQuery(id+"F4.wireOp",EDGE,"E60.trimOffspring"),sQuery(id+"F4.wireOp",EDGE,"E61.0.MirrorCS"),sQuery(id+"F4.wireOp",EDGE,"E61.1.MirrorCS"),sQuery(id+"F4.wireOp",EDGE,"E61.2.MirrorCS"),sQuery(id+"F4.wireOp",EDGE,"E61.4.MirrorCS"),sQuery(id+"F4.wireOp",EDGE,"E61.5.MirrorCS"),sQuery(id+"F4.wireOp",EDGE,"E61.7.MirrorCS"),sQuery(id+"F4.wireOp",EDGE,"E61.10.MirrorCS"),sQuery(id+"F4.wireOp",EDGE,"E62.0.MirrorCS"),sQuery(id+"F4.wireOp",EDGE,"E62.2.MirrorCS"),sQuery(id+"F4.wireOp",EDGE,"E62.3.MirrorCS"),sQuery(id+"F4.wireOp",EDGE,"E62.4.MirrorCS"),sQuery(id+"F4.wireOp",EDGE,"E61.3.MirrorCS"),sQuery(id+"F4.wireOp",EDGE,"E61.6.MirrorCS"),sQuery(id+"F4.wireOp",EDGE,"E63.0.MirrorCS"),sQuery(id+"F4.wireOp",EDGE,"E64.1.MirrorCS"),sQuery(id+"F4.wireOp",EDGE,"E64.2.MirrorCS"),sQuery(id+"F4.wireOp",EDGE,"E64.3.MirrorCS"),sQuery(id+"F4.wireOp",EDGE,"E64.4.MirrorCS"),sQuery(id+"F4.wireOp",EDGE,"E64.5.MirrorCS"),sQuery(id+"F4.wireOp",EDGE,"E64.6.MirrorCS"),sQuery(id+"F4.wireOp",EDGE,"E65.0.MirrorCS"),sQuery(id+"F4.wireOp",EDGE,"E66.0.MirrorCS"),sQuery(id+"F4.wireOp",EDGE,"E67.trimOffspring"),sQuery(id+"F4.wireOp",EDGE,"E68.trimOffspring")])]}),"instanceName":"37"});
            var Q314;
            Q314=makeQuery(id+"F6.opPattern","COPY",BODY,{"derivedFrom":makeQuery(id+"F5.opExtrude","SWEPT_BODY",BODY,{"disambiguationData":[OSD([sQuery(id+"F4.wireOp",EDGE,"E24"),sQuery(id+"F4.wireOp",EDGE,"E25"),sQuery(id+"F4.wireOp",EDGE,"E27"),sQuery(id+"F4.wireOp",EDGE,"E28"),sQuery(id+"F4.wireOp",EDGE,"E29"),sQuery(id+"F4.wireOp",EDGE,"E30.0.MirrorCS"),sQuery(id+"F4.wireOp",EDGE,"E31.0.MirrorCS"),sQuery(id+"F4.wireOp",EDGE,"E32.0.MirrorCS"),sQuery(id+"F4.wireOp",EDGE,"E33.0.MirrorCS"),sQuery(id+"F4.wireOp",EDGE,"E34.0.MirrorCS"),sQuery(id+"F4.wireOp",EDGE,"E35.filletArc"),sQuery(id+"F4.wireOp",EDGE,"E36.filletArc"),sQuery(id+"F4.wireOp",EDGE,"E37"),sQuery(id+"F4.wireOp",EDGE,"E38"),sQuery(id+"F4.wireOp",EDGE,"E39"),sQuery(id+"F4.wireOp",EDGE,"E40"),sQuery(id+"F4.wireOp",EDGE,"E41"),sQuery(id+"F4.wireOp",EDGE,"E42"),sQuery(id+"F4.wireOp",EDGE,"E43.filletArc"),sQuery(id+"F4.wireOp",EDGE,"E44.filletArc"),sQuery(id+"F4.wireOp",EDGE,"E45.trimOffspring"),sQuery(id+"F4.wireOp",EDGE,"E46.trimOffspring"),sQuery(id+"F4.wireOp",EDGE,"E47"),sQuery(id+"F4.wireOp",EDGE,"E48"),sQuery(id+"F4.wireOp",EDGE,"E49"),sQuery(id+"F4.wireOp",EDGE,"E50"),sQuery(id+"F4.wireOp",EDGE,"E51"),sQuery(id+"F4.wireOp",EDGE,"E52"),sQuery(id+"F4.wireOp",EDGE,"E53"),sQuery(id+"F4.wireOp",EDGE,"E54.filletArc"),sQuery(id+"F4.wireOp",EDGE,"E55.filletArc"),sQuery(id+"F4.wireOp",EDGE,"E56.filletArc"),sQuery(id+"F4.wireOp",EDGE,"E57"),sQuery(id+"F4.wireOp",EDGE,"E58"),sQuery(id+"F4.wireOp",EDGE,"E59"),sQuery(id+"F4.wireOp",EDGE,"E60.trimOffspring"),sQuery(id+"F4.wireOp",EDGE,"E61.0.MirrorCS"),sQuery(id+"F4.wireOp",EDGE,"E61.1.MirrorCS"),sQuery(id+"F4.wireOp",EDGE,"E61.2.MirrorCS"),sQuery(id+"F4.wireOp",EDGE,"E61.4.MirrorCS"),sQuery(id+"F4.wireOp",EDGE,"E61.5.MirrorCS"),sQuery(id+"F4.wireOp",EDGE,"E61.7.MirrorCS"),sQuery(id+"F4.wireOp",EDGE,"E61.10.MirrorCS"),sQuery(id+"F4.wireOp",EDGE,"E62.0.MirrorCS"),sQuery(id+"F4.wireOp",EDGE,"E62.2.MirrorCS"),sQuery(id+"F4.wireOp",EDGE,"E62.3.MirrorCS"),sQuery(id+"F4.wireOp",EDGE,"E62.4.MirrorCS"),sQuery(id+"F4.wireOp",EDGE,"E61.3.MirrorCS"),sQuery(id+"F4.wireOp",EDGE,"E61.6.MirrorCS"),sQuery(id+"F4.wireOp",EDGE,"E63.0.MirrorCS"),sQuery(id+"F4.wireOp",EDGE,"E64.1.MirrorCS"),sQuery(id+"F4.wireOp",EDGE,"E64.2.MirrorCS"),sQuery(id+"F4.wireOp",EDGE,"E64.3.MirrorCS"),sQuery(id+"F4.wireOp",EDGE,"E64.4.MirrorCS"),sQuery(id+"F4.wireOp",EDGE,"E64.5.MirrorCS"),sQuery(id+"F4.wireOp",EDGE,"E64.6.MirrorCS"),sQuery(id+"F4.wireOp",EDGE,"E65.0.MirrorCS"),sQuery(id+"F4.wireOp",EDGE,"E66.0.MirrorCS"),sQuery(id+"F4.wireOp",EDGE,"E67.trimOffspring"),sQuery(id+"F4.wireOp",EDGE,"E68.trimOffspring")])]}),"instanceName":"36"});
            var Q315;
            Q315=makeQuery(id+"F6.opPattern","COPY",BODY,{"derivedFrom":makeQuery(id+"F5.opExtrude","SWEPT_BODY",BODY,{"disambiguationData":[OSD([sQuery(id+"F4.wireOp",EDGE,"E24"),sQuery(id+"F4.wireOp",EDGE,"E25"),sQuery(id+"F4.wireOp",EDGE,"E27"),sQuery(id+"F4.wireOp",EDGE,"E28"),sQuery(id+"F4.wireOp",EDGE,"E29"),sQuery(id+"F4.wireOp",EDGE,"E30.0.MirrorCS"),sQuery(id+"F4.wireOp",EDGE,"E31.0.MirrorCS"),sQuery(id+"F4.wireOp",EDGE,"E32.0.MirrorCS"),sQuery(id+"F4.wireOp",EDGE,"E33.0.MirrorCS"),sQuery(id+"F4.wireOp",EDGE,"E34.0.MirrorCS"),sQuery(id+"F4.wireOp",EDGE,"E35.filletArc"),sQuery(id+"F4.wireOp",EDGE,"E36.filletArc"),sQuery(id+"F4.wireOp",EDGE,"E37"),sQuery(id+"F4.wireOp",EDGE,"E38"),sQuery(id+"F4.wireOp",EDGE,"E39"),sQuery(id+"F4.wireOp",EDGE,"E40"),sQuery(id+"F4.wireOp",EDGE,"E41"),sQuery(id+"F4.wireOp",EDGE,"E42"),sQuery(id+"F4.wireOp",EDGE,"E43.filletArc"),sQuery(id+"F4.wireOp",EDGE,"E44.filletArc"),sQuery(id+"F4.wireOp",EDGE,"E45.trimOffspring"),sQuery(id+"F4.wireOp",EDGE,"E46.trimOffspring"),sQuery(id+"F4.wireOp",EDGE,"E47"),sQuery(id+"F4.wireOp",EDGE,"E48"),sQuery(id+"F4.wireOp",EDGE,"E49"),sQuery(id+"F4.wireOp",EDGE,"E50"),sQuery(id+"F4.wireOp",EDGE,"E51"),sQuery(id+"F4.wireOp",EDGE,"E52"),sQuery(id+"F4.wireOp",EDGE,"E53"),sQuery(id+"F4.wireOp",EDGE,"E54.filletArc"),sQuery(id+"F4.wireOp",EDGE,"E55.filletArc"),sQuery(id+"F4.wireOp",EDGE,"E56.filletArc"),sQuery(id+"F4.wireOp",EDGE,"E57"),sQuery(id+"F4.wireOp",EDGE,"E58"),sQuery(id+"F4.wireOp",EDGE,"E59"),sQuery(id+"F4.wireOp",EDGE,"E60.trimOffspring"),sQuery(id+"F4.wireOp",EDGE,"E61.0.MirrorCS"),sQuery(id+"F4.wireOp",EDGE,"E61.1.MirrorCS"),sQuery(id+"F4.wireOp",EDGE,"E61.2.MirrorCS"),sQuery(id+"F4.wireOp",EDGE,"E61.4.MirrorCS"),sQuery(id+"F4.wireOp",EDGE,"E61.5.MirrorCS"),sQuery(id+"F4.wireOp",EDGE,"E61.7.MirrorCS"),sQuery(id+"F4.wireOp",EDGE,"E61.10.MirrorCS"),sQuery(id+"F4.wireOp",EDGE,"E62.0.MirrorCS"),sQuery(id+"F4.wireOp",EDGE,"E62.2.MirrorCS"),sQuery(id+"F4.wireOp",EDGE,"E62.3.MirrorCS"),sQuery(id+"F4.wireOp",EDGE,"E62.4.MirrorCS"),sQuery(id+"F4.wireOp",EDGE,"E61.3.MirrorCS"),sQuery(id+"F4.wireOp",EDGE,"E61.6.MirrorCS"),sQuery(id+"F4.wireOp",EDGE,"E63.0.MirrorCS"),sQuery(id+"F4.wireOp",EDGE,"E64.1.MirrorCS"),sQuery(id+"F4.wireOp",EDGE,"E64.2.MirrorCS"),sQuery(id+"F4.wireOp",EDGE,"E64.3.MirrorCS"),sQuery(id+"F4.wireOp",EDGE,"E64.4.MirrorCS"),sQuery(id+"F4.wireOp",EDGE,"E64.5.MirrorCS"),sQuery(id+"F4.wireOp",EDGE,"E64.6.MirrorCS"),sQuery(id+"F4.wireOp",EDGE,"E65.0.MirrorCS"),sQuery(id+"F4.wireOp",EDGE,"E66.0.MirrorCS"),sQuery(id+"F4.wireOp",EDGE,"E67.trimOffspring"),sQuery(id+"F4.wireOp",EDGE,"E68.trimOffspring")])]}),"instanceName":"35"});
            var Q316;
            Q316=makeQuery(id+"F6.opPattern","COPY",BODY,{"derivedFrom":makeQuery(id+"F5.opExtrude","SWEPT_BODY",BODY,{"disambiguationData":[OSD([sQuery(id+"F4.wireOp",EDGE,"E24"),sQuery(id+"F4.wireOp",EDGE,"E25"),sQuery(id+"F4.wireOp",EDGE,"E27"),sQuery(id+"F4.wireOp",EDGE,"E28"),sQuery(id+"F4.wireOp",EDGE,"E29"),sQuery(id+"F4.wireOp",EDGE,"E30.0.MirrorCS"),sQuery(id+"F4.wireOp",EDGE,"E31.0.MirrorCS"),sQuery(id+"F4.wireOp",EDGE,"E32.0.MirrorCS"),sQuery(id+"F4.wireOp",EDGE,"E33.0.MirrorCS"),sQuery(id+"F4.wireOp",EDGE,"E34.0.MirrorCS"),sQuery(id+"F4.wireOp",EDGE,"E35.filletArc"),sQuery(id+"F4.wireOp",EDGE,"E36.filletArc"),sQuery(id+"F4.wireOp",EDGE,"E37"),sQuery(id+"F4.wireOp",EDGE,"E38"),sQuery(id+"F4.wireOp",EDGE,"E39"),sQuery(id+"F4.wireOp",EDGE,"E40"),sQuery(id+"F4.wireOp",EDGE,"E41"),sQuery(id+"F4.wireOp",EDGE,"E42"),sQuery(id+"F4.wireOp",EDGE,"E43.filletArc"),sQuery(id+"F4.wireOp",EDGE,"E44.filletArc"),sQuery(id+"F4.wireOp",EDGE,"E45.trimOffspring"),sQuery(id+"F4.wireOp",EDGE,"E46.trimOffspring"),sQuery(id+"F4.wireOp",EDGE,"E47"),sQuery(id+"F4.wireOp",EDGE,"E48"),sQuery(id+"F4.wireOp",EDGE,"E49"),sQuery(id+"F4.wireOp",EDGE,"E50"),sQuery(id+"F4.wireOp",EDGE,"E51"),sQuery(id+"F4.wireOp",EDGE,"E52"),sQuery(id+"F4.wireOp",EDGE,"E53"),sQuery(id+"F4.wireOp",EDGE,"E54.filletArc"),sQuery(id+"F4.wireOp",EDGE,"E55.filletArc"),sQuery(id+"F4.wireOp",EDGE,"E56.filletArc"),sQuery(id+"F4.wireOp",EDGE,"E57"),sQuery(id+"F4.wireOp",EDGE,"E58"),sQuery(id+"F4.wireOp",EDGE,"E59"),sQuery(id+"F4.wireOp",EDGE,"E60.trimOffspring"),sQuery(id+"F4.wireOp",EDGE,"E61.0.MirrorCS"),sQuery(id+"F4.wireOp",EDGE,"E61.1.MirrorCS"),sQuery(id+"F4.wireOp",EDGE,"E61.2.MirrorCS"),sQuery(id+"F4.wireOp",EDGE,"E61.4.MirrorCS"),sQuery(id+"F4.wireOp",EDGE,"E61.5.MirrorCS"),sQuery(id+"F4.wireOp",EDGE,"E61.7.MirrorCS"),sQuery(id+"F4.wireOp",EDGE,"E61.10.MirrorCS"),sQuery(id+"F4.wireOp",EDGE,"E62.0.MirrorCS"),sQuery(id+"F4.wireOp",EDGE,"E62.2.MirrorCS"),sQuery(id+"F4.wireOp",EDGE,"E62.3.MirrorCS"),sQuery(id+"F4.wireOp",EDGE,"E62.4.MirrorCS"),sQuery(id+"F4.wireOp",EDGE,"E61.3.MirrorCS"),sQuery(id+"F4.wireOp",EDGE,"E61.6.MirrorCS"),sQuery(id+"F4.wireOp",EDGE,"E63.0.MirrorCS"),sQuery(id+"F4.wireOp",EDGE,"E64.1.MirrorCS"),sQuery(id+"F4.wireOp",EDGE,"E64.2.MirrorCS"),sQuery(id+"F4.wireOp",EDGE,"E64.3.MirrorCS"),sQuery(id+"F4.wireOp",EDGE,"E64.4.MirrorCS"),sQuery(id+"F4.wireOp",EDGE,"E64.5.MirrorCS"),sQuery(id+"F4.wireOp",EDGE,"E64.6.MirrorCS"),sQuery(id+"F4.wireOp",EDGE,"E65.0.MirrorCS"),sQuery(id+"F4.wireOp",EDGE,"E66.0.MirrorCS"),sQuery(id+"F4.wireOp",EDGE,"E67.trimOffspring"),sQuery(id+"F4.wireOp",EDGE,"E68.trimOffspring")])]}),"instanceName":"34"});
            var Q317;
            Q317=makeQuery(id+"F6.opPattern","COPY",BODY,{"derivedFrom":makeQuery(id+"F5.opExtrude","SWEPT_BODY",BODY,{"disambiguationData":[OSD([sQuery(id+"F4.wireOp",EDGE,"E24"),sQuery(id+"F4.wireOp",EDGE,"E25"),sQuery(id+"F4.wireOp",EDGE,"E27"),sQuery(id+"F4.wireOp",EDGE,"E28"),sQuery(id+"F4.wireOp",EDGE,"E29"),sQuery(id+"F4.wireOp",EDGE,"E30.0.MirrorCS"),sQuery(id+"F4.wireOp",EDGE,"E31.0.MirrorCS"),sQuery(id+"F4.wireOp",EDGE,"E32.0.MirrorCS"),sQuery(id+"F4.wireOp",EDGE,"E33.0.MirrorCS"),sQuery(id+"F4.wireOp",EDGE,"E34.0.MirrorCS"),sQuery(id+"F4.wireOp",EDGE,"E35.filletArc"),sQuery(id+"F4.wireOp",EDGE,"E36.filletArc"),sQuery(id+"F4.wireOp",EDGE,"E37"),sQuery(id+"F4.wireOp",EDGE,"E38"),sQuery(id+"F4.wireOp",EDGE,"E39"),sQuery(id+"F4.wireOp",EDGE,"E40"),sQuery(id+"F4.wireOp",EDGE,"E41"),sQuery(id+"F4.wireOp",EDGE,"E42"),sQuery(id+"F4.wireOp",EDGE,"E43.filletArc"),sQuery(id+"F4.wireOp",EDGE,"E44.filletArc"),sQuery(id+"F4.wireOp",EDGE,"E45.trimOffspring"),sQuery(id+"F4.wireOp",EDGE,"E46.trimOffspring"),sQuery(id+"F4.wireOp",EDGE,"E47"),sQuery(id+"F4.wireOp",EDGE,"E48"),sQuery(id+"F4.wireOp",EDGE,"E49"),sQuery(id+"F4.wireOp",EDGE,"E50"),sQuery(id+"F4.wireOp",EDGE,"E51"),sQuery(id+"F4.wireOp",EDGE,"E52"),sQuery(id+"F4.wireOp",EDGE,"E53"),sQuery(id+"F4.wireOp",EDGE,"E54.filletArc"),sQuery(id+"F4.wireOp",EDGE,"E55.filletArc"),sQuery(id+"F4.wireOp",EDGE,"E56.filletArc"),sQuery(id+"F4.wireOp",EDGE,"E57"),sQuery(id+"F4.wireOp",EDGE,"E58"),sQuery(id+"F4.wireOp",EDGE,"E59"),sQuery(id+"F4.wireOp",EDGE,"E60.trimOffspring"),sQuery(id+"F4.wireOp",EDGE,"E61.0.MirrorCS"),sQuery(id+"F4.wireOp",EDGE,"E61.1.MirrorCS"),sQuery(id+"F4.wireOp",EDGE,"E61.2.MirrorCS"),sQuery(id+"F4.wireOp",EDGE,"E61.4.MirrorCS"),sQuery(id+"F4.wireOp",EDGE,"E61.5.MirrorCS"),sQuery(id+"F4.wireOp",EDGE,"E61.7.MirrorCS"),sQuery(id+"F4.wireOp",EDGE,"E61.10.MirrorCS"),sQuery(id+"F4.wireOp",EDGE,"E62.0.MirrorCS"),sQuery(id+"F4.wireOp",EDGE,"E62.2.MirrorCS"),sQuery(id+"F4.wireOp",EDGE,"E62.3.MirrorCS"),sQuery(id+"F4.wireOp",EDGE,"E62.4.MirrorCS"),sQuery(id+"F4.wireOp",EDGE,"E61.3.MirrorCS"),sQuery(id+"F4.wireOp",EDGE,"E61.6.MirrorCS"),sQuery(id+"F4.wireOp",EDGE,"E63.0.MirrorCS"),sQuery(id+"F4.wireOp",EDGE,"E64.1.MirrorCS"),sQuery(id+"F4.wireOp",EDGE,"E64.2.MirrorCS"),sQuery(id+"F4.wireOp",EDGE,"E64.3.MirrorCS"),sQuery(id+"F4.wireOp",EDGE,"E64.4.MirrorCS"),sQuery(id+"F4.wireOp",EDGE,"E64.5.MirrorCS"),sQuery(id+"F4.wireOp",EDGE,"E64.6.MirrorCS"),sQuery(id+"F4.wireOp",EDGE,"E65.0.MirrorCS"),sQuery(id+"F4.wireOp",EDGE,"E66.0.MirrorCS"),sQuery(id+"F4.wireOp",EDGE,"E67.trimOffspring"),sQuery(id+"F4.wireOp",EDGE,"E68.trimOffspring")])]}),"instanceName":"33"});
            var Q318;
            Q318=makeQuery(id+"F6.opPattern","COPY",BODY,{"derivedFrom":makeQuery(id+"F5.opExtrude","SWEPT_BODY",BODY,{"disambiguationData":[OSD([sQuery(id+"F4.wireOp",EDGE,"E24"),sQuery(id+"F4.wireOp",EDGE,"E25"),sQuery(id+"F4.wireOp",EDGE,"E27"),sQuery(id+"F4.wireOp",EDGE,"E28"),sQuery(id+"F4.wireOp",EDGE,"E29"),sQuery(id+"F4.wireOp",EDGE,"E30.0.MirrorCS"),sQuery(id+"F4.wireOp",EDGE,"E31.0.MirrorCS"),sQuery(id+"F4.wireOp",EDGE,"E32.0.MirrorCS"),sQuery(id+"F4.wireOp",EDGE,"E33.0.MirrorCS"),sQuery(id+"F4.wireOp",EDGE,"E34.0.MirrorCS"),sQuery(id+"F4.wireOp",EDGE,"E35.filletArc"),sQuery(id+"F4.wireOp",EDGE,"E36.filletArc"),sQuery(id+"F4.wireOp",EDGE,"E37"),sQuery(id+"F4.wireOp",EDGE,"E38"),sQuery(id+"F4.wireOp",EDGE,"E39"),sQuery(id+"F4.wireOp",EDGE,"E40"),sQuery(id+"F4.wireOp",EDGE,"E41"),sQuery(id+"F4.wireOp",EDGE,"E42"),sQuery(id+"F4.wireOp",EDGE,"E43.filletArc"),sQuery(id+"F4.wireOp",EDGE,"E44.filletArc"),sQuery(id+"F4.wireOp",EDGE,"E45.trimOffspring"),sQuery(id+"F4.wireOp",EDGE,"E46.trimOffspring"),sQuery(id+"F4.wireOp",EDGE,"E47"),sQuery(id+"F4.wireOp",EDGE,"E48"),sQuery(id+"F4.wireOp",EDGE,"E49"),sQuery(id+"F4.wireOp",EDGE,"E50"),sQuery(id+"F4.wireOp",EDGE,"E51"),sQuery(id+"F4.wireOp",EDGE,"E52"),sQuery(id+"F4.wireOp",EDGE,"E53"),sQuery(id+"F4.wireOp",EDGE,"E54.filletArc"),sQuery(id+"F4.wireOp",EDGE,"E55.filletArc"),sQuery(id+"F4.wireOp",EDGE,"E56.filletArc"),sQuery(id+"F4.wireOp",EDGE,"E57"),sQuery(id+"F4.wireOp",EDGE,"E58"),sQuery(id+"F4.wireOp",EDGE,"E59"),sQuery(id+"F4.wireOp",EDGE,"E60.trimOffspring"),sQuery(id+"F4.wireOp",EDGE,"E61.0.MirrorCS"),sQuery(id+"F4.wireOp",EDGE,"E61.1.MirrorCS"),sQuery(id+"F4.wireOp",EDGE,"E61.2.MirrorCS"),sQuery(id+"F4.wireOp",EDGE,"E61.4.MirrorCS"),sQuery(id+"F4.wireOp",EDGE,"E61.5.MirrorCS"),sQuery(id+"F4.wireOp",EDGE,"E61.7.MirrorCS"),sQuery(id+"F4.wireOp",EDGE,"E61.10.MirrorCS"),sQuery(id+"F4.wireOp",EDGE,"E62.0.MirrorCS"),sQuery(id+"F4.wireOp",EDGE,"E62.2.MirrorCS"),sQuery(id+"F4.wireOp",EDGE,"E62.3.MirrorCS"),sQuery(id+"F4.wireOp",EDGE,"E62.4.MirrorCS"),sQuery(id+"F4.wireOp",EDGE,"E61.3.MirrorCS"),sQuery(id+"F4.wireOp",EDGE,"E61.6.MirrorCS"),sQuery(id+"F4.wireOp",EDGE,"E63.0.MirrorCS"),sQuery(id+"F4.wireOp",EDGE,"E64.1.MirrorCS"),sQuery(id+"F4.wireOp",EDGE,"E64.2.MirrorCS"),sQuery(id+"F4.wireOp",EDGE,"E64.3.MirrorCS"),sQuery(id+"F4.wireOp",EDGE,"E64.4.MirrorCS"),sQuery(id+"F4.wireOp",EDGE,"E64.5.MirrorCS"),sQuery(id+"F4.wireOp",EDGE,"E64.6.MirrorCS"),sQuery(id+"F4.wireOp",EDGE,"E65.0.MirrorCS"),sQuery(id+"F4.wireOp",EDGE,"E66.0.MirrorCS"),sQuery(id+"F4.wireOp",EDGE,"E67.trimOffspring"),sQuery(id+"F4.wireOp",EDGE,"E68.trimOffspring")])]}),"instanceName":"32"});
            var Q319;
            Q319=makeQuery(id+"F6.opPattern","COPY",BODY,{"derivedFrom":makeQuery(id+"F5.opExtrude","SWEPT_BODY",BODY,{"disambiguationData":[OSD([sQuery(id+"F4.wireOp",EDGE,"E24"),sQuery(id+"F4.wireOp",EDGE,"E25"),sQuery(id+"F4.wireOp",EDGE,"E27"),sQuery(id+"F4.wireOp",EDGE,"E28"),sQuery(id+"F4.wireOp",EDGE,"E29"),sQuery(id+"F4.wireOp",EDGE,"E30.0.MirrorCS"),sQuery(id+"F4.wireOp",EDGE,"E31.0.MirrorCS"),sQuery(id+"F4.wireOp",EDGE,"E32.0.MirrorCS"),sQuery(id+"F4.wireOp",EDGE,"E33.0.MirrorCS"),sQuery(id+"F4.wireOp",EDGE,"E34.0.MirrorCS"),sQuery(id+"F4.wireOp",EDGE,"E35.filletArc"),sQuery(id+"F4.wireOp",EDGE,"E36.filletArc"),sQuery(id+"F4.wireOp",EDGE,"E37"),sQuery(id+"F4.wireOp",EDGE,"E38"),sQuery(id+"F4.wireOp",EDGE,"E39"),sQuery(id+"F4.wireOp",EDGE,"E40"),sQuery(id+"F4.wireOp",EDGE,"E41"),sQuery(id+"F4.wireOp",EDGE,"E42"),sQuery(id+"F4.wireOp",EDGE,"E43.filletArc"),sQuery(id+"F4.wireOp",EDGE,"E44.filletArc"),sQuery(id+"F4.wireOp",EDGE,"E45.trimOffspring"),sQuery(id+"F4.wireOp",EDGE,"E46.trimOffspring"),sQuery(id+"F4.wireOp",EDGE,"E47"),sQuery(id+"F4.wireOp",EDGE,"E48"),sQuery(id+"F4.wireOp",EDGE,"E49"),sQuery(id+"F4.wireOp",EDGE,"E50"),sQuery(id+"F4.wireOp",EDGE,"E51"),sQuery(id+"F4.wireOp",EDGE,"E52"),sQuery(id+"F4.wireOp",EDGE,"E53"),sQuery(id+"F4.wireOp",EDGE,"E54.filletArc"),sQuery(id+"F4.wireOp",EDGE,"E55.filletArc"),sQuery(id+"F4.wireOp",EDGE,"E56.filletArc"),sQuery(id+"F4.wireOp",EDGE,"E57"),sQuery(id+"F4.wireOp",EDGE,"E58"),sQuery(id+"F4.wireOp",EDGE,"E59"),sQuery(id+"F4.wireOp",EDGE,"E60.trimOffspring"),sQuery(id+"F4.wireOp",EDGE,"E61.0.MirrorCS"),sQuery(id+"F4.wireOp",EDGE,"E61.1.MirrorCS"),sQuery(id+"F4.wireOp",EDGE,"E61.2.MirrorCS"),sQuery(id+"F4.wireOp",EDGE,"E61.4.MirrorCS"),sQuery(id+"F4.wireOp",EDGE,"E61.5.MirrorCS"),sQuery(id+"F4.wireOp",EDGE,"E61.7.MirrorCS"),sQuery(id+"F4.wireOp",EDGE,"E61.10.MirrorCS"),sQuery(id+"F4.wireOp",EDGE,"E62.0.MirrorCS"),sQuery(id+"F4.wireOp",EDGE,"E62.2.MirrorCS"),sQuery(id+"F4.wireOp",EDGE,"E62.3.MirrorCS"),sQuery(id+"F4.wireOp",EDGE,"E62.4.MirrorCS"),sQuery(id+"F4.wireOp",EDGE,"E61.3.MirrorCS"),sQuery(id+"F4.wireOp",EDGE,"E61.6.MirrorCS"),sQuery(id+"F4.wireOp",EDGE,"E63.0.MirrorCS"),sQuery(id+"F4.wireOp",EDGE,"E64.1.MirrorCS"),sQuery(id+"F4.wireOp",EDGE,"E64.2.MirrorCS"),sQuery(id+"F4.wireOp",EDGE,"E64.3.MirrorCS"),sQuery(id+"F4.wireOp",EDGE,"E64.4.MirrorCS"),sQuery(id+"F4.wireOp",EDGE,"E64.5.MirrorCS"),sQuery(id+"F4.wireOp",EDGE,"E64.6.MirrorCS"),sQuery(id+"F4.wireOp",EDGE,"E65.0.MirrorCS"),sQuery(id+"F4.wireOp",EDGE,"E66.0.MirrorCS"),sQuery(id+"F4.wireOp",EDGE,"E67.trimOffspring"),sQuery(id+"F4.wireOp",EDGE,"E68.trimOffspring")])]}),"instanceName":"31"});
            var Q320;
            Q320=makeQuery(id+"F6.opPattern","COPY",BODY,{"derivedFrom":makeQuery(id+"F5.opExtrude","SWEPT_BODY",BODY,{"disambiguationData":[OSD([sQuery(id+"F4.wireOp",EDGE,"E24"),sQuery(id+"F4.wireOp",EDGE,"E25"),sQuery(id+"F4.wireOp",EDGE,"E27"),sQuery(id+"F4.wireOp",EDGE,"E28"),sQuery(id+"F4.wireOp",EDGE,"E29"),sQuery(id+"F4.wireOp",EDGE,"E30.0.MirrorCS"),sQuery(id+"F4.wireOp",EDGE,"E31.0.MirrorCS"),sQuery(id+"F4.wireOp",EDGE,"E32.0.MirrorCS"),sQuery(id+"F4.wireOp",EDGE,"E33.0.MirrorCS"),sQuery(id+"F4.wireOp",EDGE,"E34.0.MirrorCS"),sQuery(id+"F4.wireOp",EDGE,"E35.filletArc"),sQuery(id+"F4.wireOp",EDGE,"E36.filletArc"),sQuery(id+"F4.wireOp",EDGE,"E37"),sQuery(id+"F4.wireOp",EDGE,"E38"),sQuery(id+"F4.wireOp",EDGE,"E39"),sQuery(id+"F4.wireOp",EDGE,"E40"),sQuery(id+"F4.wireOp",EDGE,"E41"),sQuery(id+"F4.wireOp",EDGE,"E42"),sQuery(id+"F4.wireOp",EDGE,"E43.filletArc"),sQuery(id+"F4.wireOp",EDGE,"E44.filletArc"),sQuery(id+"F4.wireOp",EDGE,"E45.trimOffspring"),sQuery(id+"F4.wireOp",EDGE,"E46.trimOffspring"),sQuery(id+"F4.wireOp",EDGE,"E47"),sQuery(id+"F4.wireOp",EDGE,"E48"),sQuery(id+"F4.wireOp",EDGE,"E49"),sQuery(id+"F4.wireOp",EDGE,"E50"),sQuery(id+"F4.wireOp",EDGE,"E51"),sQuery(id+"F4.wireOp",EDGE,"E52"),sQuery(id+"F4.wireOp",EDGE,"E53"),sQuery(id+"F4.wireOp",EDGE,"E54.filletArc"),sQuery(id+"F4.wireOp",EDGE,"E55.filletArc"),sQuery(id+"F4.wireOp",EDGE,"E56.filletArc"),sQuery(id+"F4.wireOp",EDGE,"E57"),sQuery(id+"F4.wireOp",EDGE,"E58"),sQuery(id+"F4.wireOp",EDGE,"E59"),sQuery(id+"F4.wireOp",EDGE,"E60.trimOffspring"),sQuery(id+"F4.wireOp",EDGE,"E61.0.MirrorCS"),sQuery(id+"F4.wireOp",EDGE,"E61.1.MirrorCS"),sQuery(id+"F4.wireOp",EDGE,"E61.2.MirrorCS"),sQuery(id+"F4.wireOp",EDGE,"E61.4.MirrorCS"),sQuery(id+"F4.wireOp",EDGE,"E61.5.MirrorCS"),sQuery(id+"F4.wireOp",EDGE,"E61.7.MirrorCS"),sQuery(id+"F4.wireOp",EDGE,"E61.10.MirrorCS"),sQuery(id+"F4.wireOp",EDGE,"E62.0.MirrorCS"),sQuery(id+"F4.wireOp",EDGE,"E62.2.MirrorCS"),sQuery(id+"F4.wireOp",EDGE,"E62.3.MirrorCS"),sQuery(id+"F4.wireOp",EDGE,"E62.4.MirrorCS"),sQuery(id+"F4.wireOp",EDGE,"E61.3.MirrorCS"),sQuery(id+"F4.wireOp",EDGE,"E61.6.MirrorCS"),sQuery(id+"F4.wireOp",EDGE,"E63.0.MirrorCS"),sQuery(id+"F4.wireOp",EDGE,"E64.1.MirrorCS"),sQuery(id+"F4.wireOp",EDGE,"E64.2.MirrorCS"),sQuery(id+"F4.wireOp",EDGE,"E64.3.MirrorCS"),sQuery(id+"F4.wireOp",EDGE,"E64.4.MirrorCS"),sQuery(id+"F4.wireOp",EDGE,"E64.5.MirrorCS"),sQuery(id+"F4.wireOp",EDGE,"E64.6.MirrorCS"),sQuery(id+"F4.wireOp",EDGE,"E65.0.MirrorCS"),sQuery(id+"F4.wireOp",EDGE,"E66.0.MirrorCS"),sQuery(id+"F4.wireOp",EDGE,"E67.trimOffspring"),sQuery(id+"F4.wireOp",EDGE,"E68.trimOffspring")])]}),"instanceName":"30"});
            var Q321;
            Q321=makeQuery(id+"F6.opPattern","COPY",BODY,{"derivedFrom":makeQuery(id+"F5.opExtrude","SWEPT_BODY",BODY,{"disambiguationData":[OSD([sQuery(id+"F4.wireOp",EDGE,"E24"),sQuery(id+"F4.wireOp",EDGE,"E25"),sQuery(id+"F4.wireOp",EDGE,"E27"),sQuery(id+"F4.wireOp",EDGE,"E28"),sQuery(id+"F4.wireOp",EDGE,"E29"),sQuery(id+"F4.wireOp",EDGE,"E30.0.MirrorCS"),sQuery(id+"F4.wireOp",EDGE,"E31.0.MirrorCS"),sQuery(id+"F4.wireOp",EDGE,"E32.0.MirrorCS"),sQuery(id+"F4.wireOp",EDGE,"E33.0.MirrorCS"),sQuery(id+"F4.wireOp",EDGE,"E34.0.MirrorCS"),sQuery(id+"F4.wireOp",EDGE,"E35.filletArc"),sQuery(id+"F4.wireOp",EDGE,"E36.filletArc"),sQuery(id+"F4.wireOp",EDGE,"E37"),sQuery(id+"F4.wireOp",EDGE,"E38"),sQuery(id+"F4.wireOp",EDGE,"E39"),sQuery(id+"F4.wireOp",EDGE,"E40"),sQuery(id+"F4.wireOp",EDGE,"E41"),sQuery(id+"F4.wireOp",EDGE,"E42"),sQuery(id+"F4.wireOp",EDGE,"E43.filletArc"),sQuery(id+"F4.wireOp",EDGE,"E44.filletArc"),sQuery(id+"F4.wireOp",EDGE,"E45.trimOffspring"),sQuery(id+"F4.wireOp",EDGE,"E46.trimOffspring"),sQuery(id+"F4.wireOp",EDGE,"E47"),sQuery(id+"F4.wireOp",EDGE,"E48"),sQuery(id+"F4.wireOp",EDGE,"E49"),sQuery(id+"F4.wireOp",EDGE,"E50"),sQuery(id+"F4.wireOp",EDGE,"E51"),sQuery(id+"F4.wireOp",EDGE,"E52"),sQuery(id+"F4.wireOp",EDGE,"E53"),sQuery(id+"F4.wireOp",EDGE,"E54.filletArc"),sQuery(id+"F4.wireOp",EDGE,"E55.filletArc"),sQuery(id+"F4.wireOp",EDGE,"E56.filletArc"),sQuery(id+"F4.wireOp",EDGE,"E57"),sQuery(id+"F4.wireOp",EDGE,"E58"),sQuery(id+"F4.wireOp",EDGE,"E59"),sQuery(id+"F4.wireOp",EDGE,"E60.trimOffspring"),sQuery(id+"F4.wireOp",EDGE,"E61.0.MirrorCS"),sQuery(id+"F4.wireOp",EDGE,"E61.1.MirrorCS"),sQuery(id+"F4.wireOp",EDGE,"E61.2.MirrorCS"),sQuery(id+"F4.wireOp",EDGE,"E61.4.MirrorCS"),sQuery(id+"F4.wireOp",EDGE,"E61.5.MirrorCS"),sQuery(id+"F4.wireOp",EDGE,"E61.7.MirrorCS"),sQuery(id+"F4.wireOp",EDGE,"E61.10.MirrorCS"),sQuery(id+"F4.wireOp",EDGE,"E62.0.MirrorCS"),sQuery(id+"F4.wireOp",EDGE,"E62.2.MirrorCS"),sQuery(id+"F4.wireOp",EDGE,"E62.3.MirrorCS"),sQuery(id+"F4.wireOp",EDGE,"E62.4.MirrorCS"),sQuery(id+"F4.wireOp",EDGE,"E61.3.MirrorCS"),sQuery(id+"F4.wireOp",EDGE,"E61.6.MirrorCS"),sQuery(id+"F4.wireOp",EDGE,"E63.0.MirrorCS"),sQuery(id+"F4.wireOp",EDGE,"E64.1.MirrorCS"),sQuery(id+"F4.wireOp",EDGE,"E64.2.MirrorCS"),sQuery(id+"F4.wireOp",EDGE,"E64.3.MirrorCS"),sQuery(id+"F4.wireOp",EDGE,"E64.4.MirrorCS"),sQuery(id+"F4.wireOp",EDGE,"E64.5.MirrorCS"),sQuery(id+"F4.wireOp",EDGE,"E64.6.MirrorCS"),sQuery(id+"F4.wireOp",EDGE,"E65.0.MirrorCS"),sQuery(id+"F4.wireOp",EDGE,"E66.0.MirrorCS"),sQuery(id+"F4.wireOp",EDGE,"E67.trimOffspring"),sQuery(id+"F4.wireOp",EDGE,"E68.trimOffspring")])]}),"instanceName":"29"});
            var Q322;
            Q322=makeQuery(id+"F6.opPattern","COPY",BODY,{"derivedFrom":makeQuery(id+"F5.opExtrude","SWEPT_BODY",BODY,{"disambiguationData":[OSD([sQuery(id+"F4.wireOp",EDGE,"E24"),sQuery(id+"F4.wireOp",EDGE,"E25"),sQuery(id+"F4.wireOp",EDGE,"E27"),sQuery(id+"F4.wireOp",EDGE,"E28"),sQuery(id+"F4.wireOp",EDGE,"E29"),sQuery(id+"F4.wireOp",EDGE,"E30.0.MirrorCS"),sQuery(id+"F4.wireOp",EDGE,"E31.0.MirrorCS"),sQuery(id+"F4.wireOp",EDGE,"E32.0.MirrorCS"),sQuery(id+"F4.wireOp",EDGE,"E33.0.MirrorCS"),sQuery(id+"F4.wireOp",EDGE,"E34.0.MirrorCS"),sQuery(id+"F4.wireOp",EDGE,"E35.filletArc"),sQuery(id+"F4.wireOp",EDGE,"E36.filletArc"),sQuery(id+"F4.wireOp",EDGE,"E37"),sQuery(id+"F4.wireOp",EDGE,"E38"),sQuery(id+"F4.wireOp",EDGE,"E39"),sQuery(id+"F4.wireOp",EDGE,"E40"),sQuery(id+"F4.wireOp",EDGE,"E41"),sQuery(id+"F4.wireOp",EDGE,"E42"),sQuery(id+"F4.wireOp",EDGE,"E43.filletArc"),sQuery(id+"F4.wireOp",EDGE,"E44.filletArc"),sQuery(id+"F4.wireOp",EDGE,"E45.trimOffspring"),sQuery(id+"F4.wireOp",EDGE,"E46.trimOffspring"),sQuery(id+"F4.wireOp",EDGE,"E47"),sQuery(id+"F4.wireOp",EDGE,"E48"),sQuery(id+"F4.wireOp",EDGE,"E49"),sQuery(id+"F4.wireOp",EDGE,"E50"),sQuery(id+"F4.wireOp",EDGE,"E51"),sQuery(id+"F4.wireOp",EDGE,"E52"),sQuery(id+"F4.wireOp",EDGE,"E53"),sQuery(id+"F4.wireOp",EDGE,"E54.filletArc"),sQuery(id+"F4.wireOp",EDGE,"E55.filletArc"),sQuery(id+"F4.wireOp",EDGE,"E56.filletArc"),sQuery(id+"F4.wireOp",EDGE,"E57"),sQuery(id+"F4.wireOp",EDGE,"E58"),sQuery(id+"F4.wireOp",EDGE,"E59"),sQuery(id+"F4.wireOp",EDGE,"E60.trimOffspring"),sQuery(id+"F4.wireOp",EDGE,"E61.0.MirrorCS"),sQuery(id+"F4.wireOp",EDGE,"E61.1.MirrorCS"),sQuery(id+"F4.wireOp",EDGE,"E61.2.MirrorCS"),sQuery(id+"F4.wireOp",EDGE,"E61.4.MirrorCS"),sQuery(id+"F4.wireOp",EDGE,"E61.5.MirrorCS"),sQuery(id+"F4.wireOp",EDGE,"E61.7.MirrorCS"),sQuery(id+"F4.wireOp",EDGE,"E61.10.MirrorCS"),sQuery(id+"F4.wireOp",EDGE,"E62.0.MirrorCS"),sQuery(id+"F4.wireOp",EDGE,"E62.2.MirrorCS"),sQuery(id+"F4.wireOp",EDGE,"E62.3.MirrorCS"),sQuery(id+"F4.wireOp",EDGE,"E62.4.MirrorCS"),sQuery(id+"F4.wireOp",EDGE,"E61.3.MirrorCS"),sQuery(id+"F4.wireOp",EDGE,"E61.6.MirrorCS"),sQuery(id+"F4.wireOp",EDGE,"E63.0.MirrorCS"),sQuery(id+"F4.wireOp",EDGE,"E64.1.MirrorCS"),sQuery(id+"F4.wireOp",EDGE,"E64.2.MirrorCS"),sQuery(id+"F4.wireOp",EDGE,"E64.3.MirrorCS"),sQuery(id+"F4.wireOp",EDGE,"E64.4.MirrorCS"),sQuery(id+"F4.wireOp",EDGE,"E64.5.MirrorCS"),sQuery(id+"F4.wireOp",EDGE,"E64.6.MirrorCS"),sQuery(id+"F4.wireOp",EDGE,"E65.0.MirrorCS"),sQuery(id+"F4.wireOp",EDGE,"E66.0.MirrorCS"),sQuery(id+"F4.wireOp",EDGE,"E67.trimOffspring"),sQuery(id+"F4.wireOp",EDGE,"E68.trimOffspring")])]}),"instanceName":"28"});
            var Q323;
            Q323=makeQuery(id+"F6.opPattern","COPY",BODY,{"derivedFrom":makeQuery(id+"F5.opExtrude","SWEPT_BODY",BODY,{"disambiguationData":[OSD([sQuery(id+"F4.wireOp",EDGE,"E24"),sQuery(id+"F4.wireOp",EDGE,"E25"),sQuery(id+"F4.wireOp",EDGE,"E27"),sQuery(id+"F4.wireOp",EDGE,"E28"),sQuery(id+"F4.wireOp",EDGE,"E29"),sQuery(id+"F4.wireOp",EDGE,"E30.0.MirrorCS"),sQuery(id+"F4.wireOp",EDGE,"E31.0.MirrorCS"),sQuery(id+"F4.wireOp",EDGE,"E32.0.MirrorCS"),sQuery(id+"F4.wireOp",EDGE,"E33.0.MirrorCS"),sQuery(id+"F4.wireOp",EDGE,"E34.0.MirrorCS"),sQuery(id+"F4.wireOp",EDGE,"E35.filletArc"),sQuery(id+"F4.wireOp",EDGE,"E36.filletArc"),sQuery(id+"F4.wireOp",EDGE,"E37"),sQuery(id+"F4.wireOp",EDGE,"E38"),sQuery(id+"F4.wireOp",EDGE,"E39"),sQuery(id+"F4.wireOp",EDGE,"E40"),sQuery(id+"F4.wireOp",EDGE,"E41"),sQuery(id+"F4.wireOp",EDGE,"E42"),sQuery(id+"F4.wireOp",EDGE,"E43.filletArc"),sQuery(id+"F4.wireOp",EDGE,"E44.filletArc"),sQuery(id+"F4.wireOp",EDGE,"E45.trimOffspring"),sQuery(id+"F4.wireOp",EDGE,"E46.trimOffspring"),sQuery(id+"F4.wireOp",EDGE,"E47"),sQuery(id+"F4.wireOp",EDGE,"E48"),sQuery(id+"F4.wireOp",EDGE,"E49"),sQuery(id+"F4.wireOp",EDGE,"E50"),sQuery(id+"F4.wireOp",EDGE,"E51"),sQuery(id+"F4.wireOp",EDGE,"E52"),sQuery(id+"F4.wireOp",EDGE,"E53"),sQuery(id+"F4.wireOp",EDGE,"E54.filletArc"),sQuery(id+"F4.wireOp",EDGE,"E55.filletArc"),sQuery(id+"F4.wireOp",EDGE,"E56.filletArc"),sQuery(id+"F4.wireOp",EDGE,"E57"),sQuery(id+"F4.wireOp",EDGE,"E58"),sQuery(id+"F4.wireOp",EDGE,"E59"),sQuery(id+"F4.wireOp",EDGE,"E60.trimOffspring"),sQuery(id+"F4.wireOp",EDGE,"E61.0.MirrorCS"),sQuery(id+"F4.wireOp",EDGE,"E61.1.MirrorCS"),sQuery(id+"F4.wireOp",EDGE,"E61.2.MirrorCS"),sQuery(id+"F4.wireOp",EDGE,"E61.4.MirrorCS"),sQuery(id+"F4.wireOp",EDGE,"E61.5.MirrorCS"),sQuery(id+"F4.wireOp",EDGE,"E61.7.MirrorCS"),sQuery(id+"F4.wireOp",EDGE,"E61.10.MirrorCS"),sQuery(id+"F4.wireOp",EDGE,"E62.0.MirrorCS"),sQuery(id+"F4.wireOp",EDGE,"E62.2.MirrorCS"),sQuery(id+"F4.wireOp",EDGE,"E62.3.MirrorCS"),sQuery(id+"F4.wireOp",EDGE,"E62.4.MirrorCS"),sQuery(id+"F4.wireOp",EDGE,"E61.3.MirrorCS"),sQuery(id+"F4.wireOp",EDGE,"E61.6.MirrorCS"),sQuery(id+"F4.wireOp",EDGE,"E63.0.MirrorCS"),sQuery(id+"F4.wireOp",EDGE,"E64.1.MirrorCS"),sQuery(id+"F4.wireOp",EDGE,"E64.2.MirrorCS"),sQuery(id+"F4.wireOp",EDGE,"E64.3.MirrorCS"),sQuery(id+"F4.wireOp",EDGE,"E64.4.MirrorCS"),sQuery(id+"F4.wireOp",EDGE,"E64.5.MirrorCS"),sQuery(id+"F4.wireOp",EDGE,"E64.6.MirrorCS"),sQuery(id+"F4.wireOp",EDGE,"E65.0.MirrorCS"),sQuery(id+"F4.wireOp",EDGE,"E66.0.MirrorCS"),sQuery(id+"F4.wireOp",EDGE,"E67.trimOffspring"),sQuery(id+"F4.wireOp",EDGE,"E68.trimOffspring")])]}),"instanceName":"27"});
            var Q324;
            Q324=makeQuery(id+"F6.opPattern","COPY",BODY,{"derivedFrom":makeQuery(id+"F5.opExtrude","SWEPT_BODY",BODY,{"disambiguationData":[OSD([sQuery(id+"F4.wireOp",EDGE,"E24"),sQuery(id+"F4.wireOp",EDGE,"E25"),sQuery(id+"F4.wireOp",EDGE,"E27"),sQuery(id+"F4.wireOp",EDGE,"E28"),sQuery(id+"F4.wireOp",EDGE,"E29"),sQuery(id+"F4.wireOp",EDGE,"E30.0.MirrorCS"),sQuery(id+"F4.wireOp",EDGE,"E31.0.MirrorCS"),sQuery(id+"F4.wireOp",EDGE,"E32.0.MirrorCS"),sQuery(id+"F4.wireOp",EDGE,"E33.0.MirrorCS"),sQuery(id+"F4.wireOp",EDGE,"E34.0.MirrorCS"),sQuery(id+"F4.wireOp",EDGE,"E35.filletArc"),sQuery(id+"F4.wireOp",EDGE,"E36.filletArc"),sQuery(id+"F4.wireOp",EDGE,"E37"),sQuery(id+"F4.wireOp",EDGE,"E38"),sQuery(id+"F4.wireOp",EDGE,"E39"),sQuery(id+"F4.wireOp",EDGE,"E40"),sQuery(id+"F4.wireOp",EDGE,"E41"),sQuery(id+"F4.wireOp",EDGE,"E42"),sQuery(id+"F4.wireOp",EDGE,"E43.filletArc"),sQuery(id+"F4.wireOp",EDGE,"E44.filletArc"),sQuery(id+"F4.wireOp",EDGE,"E45.trimOffspring"),sQuery(id+"F4.wireOp",EDGE,"E46.trimOffspring"),sQuery(id+"F4.wireOp",EDGE,"E47"),sQuery(id+"F4.wireOp",EDGE,"E48"),sQuery(id+"F4.wireOp",EDGE,"E49"),sQuery(id+"F4.wireOp",EDGE,"E50"),sQuery(id+"F4.wireOp",EDGE,"E51"),sQuery(id+"F4.wireOp",EDGE,"E52"),sQuery(id+"F4.wireOp",EDGE,"E53"),sQuery(id+"F4.wireOp",EDGE,"E54.filletArc"),sQuery(id+"F4.wireOp",EDGE,"E55.filletArc"),sQuery(id+"F4.wireOp",EDGE,"E56.filletArc"),sQuery(id+"F4.wireOp",EDGE,"E57"),sQuery(id+"F4.wireOp",EDGE,"E58"),sQuery(id+"F4.wireOp",EDGE,"E59"),sQuery(id+"F4.wireOp",EDGE,"E60.trimOffspring"),sQuery(id+"F4.wireOp",EDGE,"E61.0.MirrorCS"),sQuery(id+"F4.wireOp",EDGE,"E61.1.MirrorCS"),sQuery(id+"F4.wireOp",EDGE,"E61.2.MirrorCS"),sQuery(id+"F4.wireOp",EDGE,"E61.4.MirrorCS"),sQuery(id+"F4.wireOp",EDGE,"E61.5.MirrorCS"),sQuery(id+"F4.wireOp",EDGE,"E61.7.MirrorCS"),sQuery(id+"F4.wireOp",EDGE,"E61.10.MirrorCS"),sQuery(id+"F4.wireOp",EDGE,"E62.0.MirrorCS"),sQuery(id+"F4.wireOp",EDGE,"E62.2.MirrorCS"),sQuery(id+"F4.wireOp",EDGE,"E62.3.MirrorCS"),sQuery(id+"F4.wireOp",EDGE,"E62.4.MirrorCS"),sQuery(id+"F4.wireOp",EDGE,"E61.3.MirrorCS"),sQuery(id+"F4.wireOp",EDGE,"E61.6.MirrorCS"),sQuery(id+"F4.wireOp",EDGE,"E63.0.MirrorCS"),sQuery(id+"F4.wireOp",EDGE,"E64.1.MirrorCS"),sQuery(id+"F4.wireOp",EDGE,"E64.2.MirrorCS"),sQuery(id+"F4.wireOp",EDGE,"E64.3.MirrorCS"),sQuery(id+"F4.wireOp",EDGE,"E64.4.MirrorCS"),sQuery(id+"F4.wireOp",EDGE,"E64.5.MirrorCS"),sQuery(id+"F4.wireOp",EDGE,"E64.6.MirrorCS"),sQuery(id+"F4.wireOp",EDGE,"E65.0.MirrorCS"),sQuery(id+"F4.wireOp",EDGE,"E66.0.MirrorCS"),sQuery(id+"F4.wireOp",EDGE,"E67.trimOffspring"),sQuery(id+"F4.wireOp",EDGE,"E68.trimOffspring")])]}),"instanceName":"26"});
            var Q325;
            Q325=makeQuery(id+"F6.opPattern","COPY",BODY,{"derivedFrom":makeQuery(id+"F5.opExtrude","SWEPT_BODY",BODY,{"disambiguationData":[OSD([sQuery(id+"F4.wireOp",EDGE,"E24"),sQuery(id+"F4.wireOp",EDGE,"E25"),sQuery(id+"F4.wireOp",EDGE,"E27"),sQuery(id+"F4.wireOp",EDGE,"E28"),sQuery(id+"F4.wireOp",EDGE,"E29"),sQuery(id+"F4.wireOp",EDGE,"E30.0.MirrorCS"),sQuery(id+"F4.wireOp",EDGE,"E31.0.MirrorCS"),sQuery(id+"F4.wireOp",EDGE,"E32.0.MirrorCS"),sQuery(id+"F4.wireOp",EDGE,"E33.0.MirrorCS"),sQuery(id+"F4.wireOp",EDGE,"E34.0.MirrorCS"),sQuery(id+"F4.wireOp",EDGE,"E35.filletArc"),sQuery(id+"F4.wireOp",EDGE,"E36.filletArc"),sQuery(id+"F4.wireOp",EDGE,"E37"),sQuery(id+"F4.wireOp",EDGE,"E38"),sQuery(id+"F4.wireOp",EDGE,"E39"),sQuery(id+"F4.wireOp",EDGE,"E40"),sQuery(id+"F4.wireOp",EDGE,"E41"),sQuery(id+"F4.wireOp",EDGE,"E42"),sQuery(id+"F4.wireOp",EDGE,"E43.filletArc"),sQuery(id+"F4.wireOp",EDGE,"E44.filletArc"),sQuery(id+"F4.wireOp",EDGE,"E45.trimOffspring"),sQuery(id+"F4.wireOp",EDGE,"E46.trimOffspring"),sQuery(id+"F4.wireOp",EDGE,"E47"),sQuery(id+"F4.wireOp",EDGE,"E48"),sQuery(id+"F4.wireOp",EDGE,"E49"),sQuery(id+"F4.wireOp",EDGE,"E50"),sQuery(id+"F4.wireOp",EDGE,"E51"),sQuery(id+"F4.wireOp",EDGE,"E52"),sQuery(id+"F4.wireOp",EDGE,"E53"),sQuery(id+"F4.wireOp",EDGE,"E54.filletArc"),sQuery(id+"F4.wireOp",EDGE,"E55.filletArc"),sQuery(id+"F4.wireOp",EDGE,"E56.filletArc"),sQuery(id+"F4.wireOp",EDGE,"E57"),sQuery(id+"F4.wireOp",EDGE,"E58"),sQuery(id+"F4.wireOp",EDGE,"E59"),sQuery(id+"F4.wireOp",EDGE,"E60.trimOffspring"),sQuery(id+"F4.wireOp",EDGE,"E61.0.MirrorCS"),sQuery(id+"F4.wireOp",EDGE,"E61.1.MirrorCS"),sQuery(id+"F4.wireOp",EDGE,"E61.2.MirrorCS"),sQuery(id+"F4.wireOp",EDGE,"E61.4.MirrorCS"),sQuery(id+"F4.wireOp",EDGE,"E61.5.MirrorCS"),sQuery(id+"F4.wireOp",EDGE,"E61.7.MirrorCS"),sQuery(id+"F4.wireOp",EDGE,"E61.10.MirrorCS"),sQuery(id+"F4.wireOp",EDGE,"E62.0.MirrorCS"),sQuery(id+"F4.wireOp",EDGE,"E62.2.MirrorCS"),sQuery(id+"F4.wireOp",EDGE,"E62.3.MirrorCS"),sQuery(id+"F4.wireOp",EDGE,"E62.4.MirrorCS"),sQuery(id+"F4.wireOp",EDGE,"E61.3.MirrorCS"),sQuery(id+"F4.wireOp",EDGE,"E61.6.MirrorCS"),sQuery(id+"F4.wireOp",EDGE,"E63.0.MirrorCS"),sQuery(id+"F4.wireOp",EDGE,"E64.1.MirrorCS"),sQuery(id+"F4.wireOp",EDGE,"E64.2.MirrorCS"),sQuery(id+"F4.wireOp",EDGE,"E64.3.MirrorCS"),sQuery(id+"F4.wireOp",EDGE,"E64.4.MirrorCS"),sQuery(id+"F4.wireOp",EDGE,"E64.5.MirrorCS"),sQuery(id+"F4.wireOp",EDGE,"E64.6.MirrorCS"),sQuery(id+"F4.wireOp",EDGE,"E65.0.MirrorCS"),sQuery(id+"F4.wireOp",EDGE,"E66.0.MirrorCS"),sQuery(id+"F4.wireOp",EDGE,"E67.trimOffspring"),sQuery(id+"F4.wireOp",EDGE,"E68.trimOffspring")])]}),"instanceName":"25"});
            var Q326;
            Q326=makeQuery(id+"F6.opPattern","COPY",BODY,{"derivedFrom":makeQuery(id+"F5.opExtrude","SWEPT_BODY",BODY,{"disambiguationData":[OSD([sQuery(id+"F4.wireOp",EDGE,"E24"),sQuery(id+"F4.wireOp",EDGE,"E25"),sQuery(id+"F4.wireOp",EDGE,"E27"),sQuery(id+"F4.wireOp",EDGE,"E28"),sQuery(id+"F4.wireOp",EDGE,"E29"),sQuery(id+"F4.wireOp",EDGE,"E30.0.MirrorCS"),sQuery(id+"F4.wireOp",EDGE,"E31.0.MirrorCS"),sQuery(id+"F4.wireOp",EDGE,"E32.0.MirrorCS"),sQuery(id+"F4.wireOp",EDGE,"E33.0.MirrorCS"),sQuery(id+"F4.wireOp",EDGE,"E34.0.MirrorCS"),sQuery(id+"F4.wireOp",EDGE,"E35.filletArc"),sQuery(id+"F4.wireOp",EDGE,"E36.filletArc"),sQuery(id+"F4.wireOp",EDGE,"E37"),sQuery(id+"F4.wireOp",EDGE,"E38"),sQuery(id+"F4.wireOp",EDGE,"E39"),sQuery(id+"F4.wireOp",EDGE,"E40"),sQuery(id+"F4.wireOp",EDGE,"E41"),sQuery(id+"F4.wireOp",EDGE,"E42"),sQuery(id+"F4.wireOp",EDGE,"E43.filletArc"),sQuery(id+"F4.wireOp",EDGE,"E44.filletArc"),sQuery(id+"F4.wireOp",EDGE,"E45.trimOffspring"),sQuery(id+"F4.wireOp",EDGE,"E46.trimOffspring"),sQuery(id+"F4.wireOp",EDGE,"E47"),sQuery(id+"F4.wireOp",EDGE,"E48"),sQuery(id+"F4.wireOp",EDGE,"E49"),sQuery(id+"F4.wireOp",EDGE,"E50"),sQuery(id+"F4.wireOp",EDGE,"E51"),sQuery(id+"F4.wireOp",EDGE,"E52"),sQuery(id+"F4.wireOp",EDGE,"E53"),sQuery(id+"F4.wireOp",EDGE,"E54.filletArc"),sQuery(id+"F4.wireOp",EDGE,"E55.filletArc"),sQuery(id+"F4.wireOp",EDGE,"E56.filletArc"),sQuery(id+"F4.wireOp",EDGE,"E57"),sQuery(id+"F4.wireOp",EDGE,"E58"),sQuery(id+"F4.wireOp",EDGE,"E59"),sQuery(id+"F4.wireOp",EDGE,"E60.trimOffspring"),sQuery(id+"F4.wireOp",EDGE,"E61.0.MirrorCS"),sQuery(id+"F4.wireOp",EDGE,"E61.1.MirrorCS"),sQuery(id+"F4.wireOp",EDGE,"E61.2.MirrorCS"),sQuery(id+"F4.wireOp",EDGE,"E61.4.MirrorCS"),sQuery(id+"F4.wireOp",EDGE,"E61.5.MirrorCS"),sQuery(id+"F4.wireOp",EDGE,"E61.7.MirrorCS"),sQuery(id+"F4.wireOp",EDGE,"E61.10.MirrorCS"),sQuery(id+"F4.wireOp",EDGE,"E62.0.MirrorCS"),sQuery(id+"F4.wireOp",EDGE,"E62.2.MirrorCS"),sQuery(id+"F4.wireOp",EDGE,"E62.3.MirrorCS"),sQuery(id+"F4.wireOp",EDGE,"E62.4.MirrorCS"),sQuery(id+"F4.wireOp",EDGE,"E61.3.MirrorCS"),sQuery(id+"F4.wireOp",EDGE,"E61.6.MirrorCS"),sQuery(id+"F4.wireOp",EDGE,"E63.0.MirrorCS"),sQuery(id+"F4.wireOp",EDGE,"E64.1.MirrorCS"),sQuery(id+"F4.wireOp",EDGE,"E64.2.MirrorCS"),sQuery(id+"F4.wireOp",EDGE,"E64.3.MirrorCS"),sQuery(id+"F4.wireOp",EDGE,"E64.4.MirrorCS"),sQuery(id+"F4.wireOp",EDGE,"E64.5.MirrorCS"),sQuery(id+"F4.wireOp",EDGE,"E64.6.MirrorCS"),sQuery(id+"F4.wireOp",EDGE,"E65.0.MirrorCS"),sQuery(id+"F4.wireOp",EDGE,"E66.0.MirrorCS"),sQuery(id+"F4.wireOp",EDGE,"E67.trimOffspring"),sQuery(id+"F4.wireOp",EDGE,"E68.trimOffspring")])]}),"instanceName":"24"});
            var Q327;
            Q327=makeQuery(id+"F6.opPattern","COPY",BODY,{"derivedFrom":makeQuery(id+"F5.opExtrude","SWEPT_BODY",BODY,{"disambiguationData":[OSD([sQuery(id+"F4.wireOp",EDGE,"E24"),sQuery(id+"F4.wireOp",EDGE,"E25"),sQuery(id+"F4.wireOp",EDGE,"E27"),sQuery(id+"F4.wireOp",EDGE,"E28"),sQuery(id+"F4.wireOp",EDGE,"E29"),sQuery(id+"F4.wireOp",EDGE,"E30.0.MirrorCS"),sQuery(id+"F4.wireOp",EDGE,"E31.0.MirrorCS"),sQuery(id+"F4.wireOp",EDGE,"E32.0.MirrorCS"),sQuery(id+"F4.wireOp",EDGE,"E33.0.MirrorCS"),sQuery(id+"F4.wireOp",EDGE,"E34.0.MirrorCS"),sQuery(id+"F4.wireOp",EDGE,"E35.filletArc"),sQuery(id+"F4.wireOp",EDGE,"E36.filletArc"),sQuery(id+"F4.wireOp",EDGE,"E37"),sQuery(id+"F4.wireOp",EDGE,"E38"),sQuery(id+"F4.wireOp",EDGE,"E39"),sQuery(id+"F4.wireOp",EDGE,"E40"),sQuery(id+"F4.wireOp",EDGE,"E41"),sQuery(id+"F4.wireOp",EDGE,"E42"),sQuery(id+"F4.wireOp",EDGE,"E43.filletArc"),sQuery(id+"F4.wireOp",EDGE,"E44.filletArc"),sQuery(id+"F4.wireOp",EDGE,"E45.trimOffspring"),sQuery(id+"F4.wireOp",EDGE,"E46.trimOffspring"),sQuery(id+"F4.wireOp",EDGE,"E47"),sQuery(id+"F4.wireOp",EDGE,"E48"),sQuery(id+"F4.wireOp",EDGE,"E49"),sQuery(id+"F4.wireOp",EDGE,"E50"),sQuery(id+"F4.wireOp",EDGE,"E51"),sQuery(id+"F4.wireOp",EDGE,"E52"),sQuery(id+"F4.wireOp",EDGE,"E53"),sQuery(id+"F4.wireOp",EDGE,"E54.filletArc"),sQuery(id+"F4.wireOp",EDGE,"E55.filletArc"),sQuery(id+"F4.wireOp",EDGE,"E56.filletArc"),sQuery(id+"F4.wireOp",EDGE,"E57"),sQuery(id+"F4.wireOp",EDGE,"E58"),sQuery(id+"F4.wireOp",EDGE,"E59"),sQuery(id+"F4.wireOp",EDGE,"E60.trimOffspring"),sQuery(id+"F4.wireOp",EDGE,"E61.0.MirrorCS"),sQuery(id+"F4.wireOp",EDGE,"E61.1.MirrorCS"),sQuery(id+"F4.wireOp",EDGE,"E61.2.MirrorCS"),sQuery(id+"F4.wireOp",EDGE,"E61.4.MirrorCS"),sQuery(id+"F4.wireOp",EDGE,"E61.5.MirrorCS"),sQuery(id+"F4.wireOp",EDGE,"E61.7.MirrorCS"),sQuery(id+"F4.wireOp",EDGE,"E61.10.MirrorCS"),sQuery(id+"F4.wireOp",EDGE,"E62.0.MirrorCS"),sQuery(id+"F4.wireOp",EDGE,"E62.2.MirrorCS"),sQuery(id+"F4.wireOp",EDGE,"E62.3.MirrorCS"),sQuery(id+"F4.wireOp",EDGE,"E62.4.MirrorCS"),sQuery(id+"F4.wireOp",EDGE,"E61.3.MirrorCS"),sQuery(id+"F4.wireOp",EDGE,"E61.6.MirrorCS"),sQuery(id+"F4.wireOp",EDGE,"E63.0.MirrorCS"),sQuery(id+"F4.wireOp",EDGE,"E64.1.MirrorCS"),sQuery(id+"F4.wireOp",EDGE,"E64.2.MirrorCS"),sQuery(id+"F4.wireOp",EDGE,"E64.3.MirrorCS"),sQuery(id+"F4.wireOp",EDGE,"E64.4.MirrorCS"),sQuery(id+"F4.wireOp",EDGE,"E64.5.MirrorCS"),sQuery(id+"F4.wireOp",EDGE,"E64.6.MirrorCS"),sQuery(id+"F4.wireOp",EDGE,"E65.0.MirrorCS"),sQuery(id+"F4.wireOp",EDGE,"E66.0.MirrorCS"),sQuery(id+"F4.wireOp",EDGE,"E67.trimOffspring"),sQuery(id+"F4.wireOp",EDGE,"E68.trimOffspring")])]}),"instanceName":"23"});
            var Q328;
            Q328=makeQuery(id+"F6.opPattern","COPY",BODY,{"derivedFrom":makeQuery(id+"F5.opExtrude","SWEPT_BODY",BODY,{"disambiguationData":[OSD([sQuery(id+"F4.wireOp",EDGE,"E24"),sQuery(id+"F4.wireOp",EDGE,"E25"),sQuery(id+"F4.wireOp",EDGE,"E27"),sQuery(id+"F4.wireOp",EDGE,"E28"),sQuery(id+"F4.wireOp",EDGE,"E29"),sQuery(id+"F4.wireOp",EDGE,"E30.0.MirrorCS"),sQuery(id+"F4.wireOp",EDGE,"E31.0.MirrorCS"),sQuery(id+"F4.wireOp",EDGE,"E32.0.MirrorCS"),sQuery(id+"F4.wireOp",EDGE,"E33.0.MirrorCS"),sQuery(id+"F4.wireOp",EDGE,"E34.0.MirrorCS"),sQuery(id+"F4.wireOp",EDGE,"E35.filletArc"),sQuery(id+"F4.wireOp",EDGE,"E36.filletArc"),sQuery(id+"F4.wireOp",EDGE,"E37"),sQuery(id+"F4.wireOp",EDGE,"E38"),sQuery(id+"F4.wireOp",EDGE,"E39"),sQuery(id+"F4.wireOp",EDGE,"E40"),sQuery(id+"F4.wireOp",EDGE,"E41"),sQuery(id+"F4.wireOp",EDGE,"E42"),sQuery(id+"F4.wireOp",EDGE,"E43.filletArc"),sQuery(id+"F4.wireOp",EDGE,"E44.filletArc"),sQuery(id+"F4.wireOp",EDGE,"E45.trimOffspring"),sQuery(id+"F4.wireOp",EDGE,"E46.trimOffspring"),sQuery(id+"F4.wireOp",EDGE,"E47"),sQuery(id+"F4.wireOp",EDGE,"E48"),sQuery(id+"F4.wireOp",EDGE,"E49"),sQuery(id+"F4.wireOp",EDGE,"E50"),sQuery(id+"F4.wireOp",EDGE,"E51"),sQuery(id+"F4.wireOp",EDGE,"E52"),sQuery(id+"F4.wireOp",EDGE,"E53"),sQuery(id+"F4.wireOp",EDGE,"E54.filletArc"),sQuery(id+"F4.wireOp",EDGE,"E55.filletArc"),sQuery(id+"F4.wireOp",EDGE,"E56.filletArc"),sQuery(id+"F4.wireOp",EDGE,"E57"),sQuery(id+"F4.wireOp",EDGE,"E58"),sQuery(id+"F4.wireOp",EDGE,"E59"),sQuery(id+"F4.wireOp",EDGE,"E60.trimOffspring"),sQuery(id+"F4.wireOp",EDGE,"E61.0.MirrorCS"),sQuery(id+"F4.wireOp",EDGE,"E61.1.MirrorCS"),sQuery(id+"F4.wireOp",EDGE,"E61.2.MirrorCS"),sQuery(id+"F4.wireOp",EDGE,"E61.4.MirrorCS"),sQuery(id+"F4.wireOp",EDGE,"E61.5.MirrorCS"),sQuery(id+"F4.wireOp",EDGE,"E61.7.MirrorCS"),sQuery(id+"F4.wireOp",EDGE,"E61.10.MirrorCS"),sQuery(id+"F4.wireOp",EDGE,"E62.0.MirrorCS"),sQuery(id+"F4.wireOp",EDGE,"E62.2.MirrorCS"),sQuery(id+"F4.wireOp",EDGE,"E62.3.MirrorCS"),sQuery(id+"F4.wireOp",EDGE,"E62.4.MirrorCS"),sQuery(id+"F4.wireOp",EDGE,"E61.3.MirrorCS"),sQuery(id+"F4.wireOp",EDGE,"E61.6.MirrorCS"),sQuery(id+"F4.wireOp",EDGE,"E63.0.MirrorCS"),sQuery(id+"F4.wireOp",EDGE,"E64.1.MirrorCS"),sQuery(id+"F4.wireOp",EDGE,"E64.2.MirrorCS"),sQuery(id+"F4.wireOp",EDGE,"E64.3.MirrorCS"),sQuery(id+"F4.wireOp",EDGE,"E64.4.MirrorCS"),sQuery(id+"F4.wireOp",EDGE,"E64.5.MirrorCS"),sQuery(id+"F4.wireOp",EDGE,"E64.6.MirrorCS"),sQuery(id+"F4.wireOp",EDGE,"E65.0.MirrorCS"),sQuery(id+"F4.wireOp",EDGE,"E66.0.MirrorCS"),sQuery(id+"F4.wireOp",EDGE,"E67.trimOffspring"),sQuery(id+"F4.wireOp",EDGE,"E68.trimOffspring")])]}),"instanceName":"22"});
            var Q329;
            Q329=makeQuery(id+"F6.opPattern","COPY",BODY,{"derivedFrom":makeQuery(id+"F5.opExtrude","SWEPT_BODY",BODY,{"disambiguationData":[OSD([sQuery(id+"F4.wireOp",EDGE,"E24"),sQuery(id+"F4.wireOp",EDGE,"E25"),sQuery(id+"F4.wireOp",EDGE,"E27"),sQuery(id+"F4.wireOp",EDGE,"E28"),sQuery(id+"F4.wireOp",EDGE,"E29"),sQuery(id+"F4.wireOp",EDGE,"E30.0.MirrorCS"),sQuery(id+"F4.wireOp",EDGE,"E31.0.MirrorCS"),sQuery(id+"F4.wireOp",EDGE,"E32.0.MirrorCS"),sQuery(id+"F4.wireOp",EDGE,"E33.0.MirrorCS"),sQuery(id+"F4.wireOp",EDGE,"E34.0.MirrorCS"),sQuery(id+"F4.wireOp",EDGE,"E35.filletArc"),sQuery(id+"F4.wireOp",EDGE,"E36.filletArc"),sQuery(id+"F4.wireOp",EDGE,"E37"),sQuery(id+"F4.wireOp",EDGE,"E38"),sQuery(id+"F4.wireOp",EDGE,"E39"),sQuery(id+"F4.wireOp",EDGE,"E40"),sQuery(id+"F4.wireOp",EDGE,"E41"),sQuery(id+"F4.wireOp",EDGE,"E42"),sQuery(id+"F4.wireOp",EDGE,"E43.filletArc"),sQuery(id+"F4.wireOp",EDGE,"E44.filletArc"),sQuery(id+"F4.wireOp",EDGE,"E45.trimOffspring"),sQuery(id+"F4.wireOp",EDGE,"E46.trimOffspring"),sQuery(id+"F4.wireOp",EDGE,"E47"),sQuery(id+"F4.wireOp",EDGE,"E48"),sQuery(id+"F4.wireOp",EDGE,"E49"),sQuery(id+"F4.wireOp",EDGE,"E50"),sQuery(id+"F4.wireOp",EDGE,"E51"),sQuery(id+"F4.wireOp",EDGE,"E52"),sQuery(id+"F4.wireOp",EDGE,"E53"),sQuery(id+"F4.wireOp",EDGE,"E54.filletArc"),sQuery(id+"F4.wireOp",EDGE,"E55.filletArc"),sQuery(id+"F4.wireOp",EDGE,"E56.filletArc"),sQuery(id+"F4.wireOp",EDGE,"E57"),sQuery(id+"F4.wireOp",EDGE,"E58"),sQuery(id+"F4.wireOp",EDGE,"E59"),sQuery(id+"F4.wireOp",EDGE,"E60.trimOffspring"),sQuery(id+"F4.wireOp",EDGE,"E61.0.MirrorCS"),sQuery(id+"F4.wireOp",EDGE,"E61.1.MirrorCS"),sQuery(id+"F4.wireOp",EDGE,"E61.2.MirrorCS"),sQuery(id+"F4.wireOp",EDGE,"E61.4.MirrorCS"),sQuery(id+"F4.wireOp",EDGE,"E61.5.MirrorCS"),sQuery(id+"F4.wireOp",EDGE,"E61.7.MirrorCS"),sQuery(id+"F4.wireOp",EDGE,"E61.10.MirrorCS"),sQuery(id+"F4.wireOp",EDGE,"E62.0.MirrorCS"),sQuery(id+"F4.wireOp",EDGE,"E62.2.MirrorCS"),sQuery(id+"F4.wireOp",EDGE,"E62.3.MirrorCS"),sQuery(id+"F4.wireOp",EDGE,"E62.4.MirrorCS"),sQuery(id+"F4.wireOp",EDGE,"E61.3.MirrorCS"),sQuery(id+"F4.wireOp",EDGE,"E61.6.MirrorCS"),sQuery(id+"F4.wireOp",EDGE,"E63.0.MirrorCS"),sQuery(id+"F4.wireOp",EDGE,"E64.1.MirrorCS"),sQuery(id+"F4.wireOp",EDGE,"E64.2.MirrorCS"),sQuery(id+"F4.wireOp",EDGE,"E64.3.MirrorCS"),sQuery(id+"F4.wireOp",EDGE,"E64.4.MirrorCS"),sQuery(id+"F4.wireOp",EDGE,"E64.5.MirrorCS"),sQuery(id+"F4.wireOp",EDGE,"E64.6.MirrorCS"),sQuery(id+"F4.wireOp",EDGE,"E65.0.MirrorCS"),sQuery(id+"F4.wireOp",EDGE,"E66.0.MirrorCS"),sQuery(id+"F4.wireOp",EDGE,"E67.trimOffspring"),sQuery(id+"F4.wireOp",EDGE,"E68.trimOffspring")])]}),"instanceName":"21"});
            var Q330;
            Q330=makeQuery(id+"F6.opPattern","COPY",BODY,{"derivedFrom":makeQuery(id+"F5.opExtrude","SWEPT_BODY",BODY,{"disambiguationData":[OSD([sQuery(id+"F4.wireOp",EDGE,"E24"),sQuery(id+"F4.wireOp",EDGE,"E25"),sQuery(id+"F4.wireOp",EDGE,"E27"),sQuery(id+"F4.wireOp",EDGE,"E28"),sQuery(id+"F4.wireOp",EDGE,"E29"),sQuery(id+"F4.wireOp",EDGE,"E30.0.MirrorCS"),sQuery(id+"F4.wireOp",EDGE,"E31.0.MirrorCS"),sQuery(id+"F4.wireOp",EDGE,"E32.0.MirrorCS"),sQuery(id+"F4.wireOp",EDGE,"E33.0.MirrorCS"),sQuery(id+"F4.wireOp",EDGE,"E34.0.MirrorCS"),sQuery(id+"F4.wireOp",EDGE,"E35.filletArc"),sQuery(id+"F4.wireOp",EDGE,"E36.filletArc"),sQuery(id+"F4.wireOp",EDGE,"E37"),sQuery(id+"F4.wireOp",EDGE,"E38"),sQuery(id+"F4.wireOp",EDGE,"E39"),sQuery(id+"F4.wireOp",EDGE,"E40"),sQuery(id+"F4.wireOp",EDGE,"E41"),sQuery(id+"F4.wireOp",EDGE,"E42"),sQuery(id+"F4.wireOp",EDGE,"E43.filletArc"),sQuery(id+"F4.wireOp",EDGE,"E44.filletArc"),sQuery(id+"F4.wireOp",EDGE,"E45.trimOffspring"),sQuery(id+"F4.wireOp",EDGE,"E46.trimOffspring"),sQuery(id+"F4.wireOp",EDGE,"E47"),sQuery(id+"F4.wireOp",EDGE,"E48"),sQuery(id+"F4.wireOp",EDGE,"E49"),sQuery(id+"F4.wireOp",EDGE,"E50"),sQuery(id+"F4.wireOp",EDGE,"E51"),sQuery(id+"F4.wireOp",EDGE,"E52"),sQuery(id+"F4.wireOp",EDGE,"E53"),sQuery(id+"F4.wireOp",EDGE,"E54.filletArc"),sQuery(id+"F4.wireOp",EDGE,"E55.filletArc"),sQuery(id+"F4.wireOp",EDGE,"E56.filletArc"),sQuery(id+"F4.wireOp",EDGE,"E57"),sQuery(id+"F4.wireOp",EDGE,"E58"),sQuery(id+"F4.wireOp",EDGE,"E59"),sQuery(id+"F4.wireOp",EDGE,"E60.trimOffspring"),sQuery(id+"F4.wireOp",EDGE,"E61.0.MirrorCS"),sQuery(id+"F4.wireOp",EDGE,"E61.1.MirrorCS"),sQuery(id+"F4.wireOp",EDGE,"E61.2.MirrorCS"),sQuery(id+"F4.wireOp",EDGE,"E61.4.MirrorCS"),sQuery(id+"F4.wireOp",EDGE,"E61.5.MirrorCS"),sQuery(id+"F4.wireOp",EDGE,"E61.7.MirrorCS"),sQuery(id+"F4.wireOp",EDGE,"E61.10.MirrorCS"),sQuery(id+"F4.wireOp",EDGE,"E62.0.MirrorCS"),sQuery(id+"F4.wireOp",EDGE,"E62.2.MirrorCS"),sQuery(id+"F4.wireOp",EDGE,"E62.3.MirrorCS"),sQuery(id+"F4.wireOp",EDGE,"E62.4.MirrorCS"),sQuery(id+"F4.wireOp",EDGE,"E61.3.MirrorCS"),sQuery(id+"F4.wireOp",EDGE,"E61.6.MirrorCS"),sQuery(id+"F4.wireOp",EDGE,"E63.0.MirrorCS"),sQuery(id+"F4.wireOp",EDGE,"E64.1.MirrorCS"),sQuery(id+"F4.wireOp",EDGE,"E64.2.MirrorCS"),sQuery(id+"F4.wireOp",EDGE,"E64.3.MirrorCS"),sQuery(id+"F4.wireOp",EDGE,"E64.4.MirrorCS"),sQuery(id+"F4.wireOp",EDGE,"E64.5.MirrorCS"),sQuery(id+"F4.wireOp",EDGE,"E64.6.MirrorCS"),sQuery(id+"F4.wireOp",EDGE,"E65.0.MirrorCS"),sQuery(id+"F4.wireOp",EDGE,"E66.0.MirrorCS"),sQuery(id+"F4.wireOp",EDGE,"E67.trimOffspring"),sQuery(id+"F4.wireOp",EDGE,"E68.trimOffspring")])]}),"instanceName":"20"});
            var Q331;
            Q331=makeQuery(id+"F6.opPattern","COPY",BODY,{"derivedFrom":makeQuery(id+"F5.opExtrude","SWEPT_BODY",BODY,{"disambiguationData":[OSD([sQuery(id+"F4.wireOp",EDGE,"E24"),sQuery(id+"F4.wireOp",EDGE,"E25"),sQuery(id+"F4.wireOp",EDGE,"E27"),sQuery(id+"F4.wireOp",EDGE,"E28"),sQuery(id+"F4.wireOp",EDGE,"E29"),sQuery(id+"F4.wireOp",EDGE,"E30.0.MirrorCS"),sQuery(id+"F4.wireOp",EDGE,"E31.0.MirrorCS"),sQuery(id+"F4.wireOp",EDGE,"E32.0.MirrorCS"),sQuery(id+"F4.wireOp",EDGE,"E33.0.MirrorCS"),sQuery(id+"F4.wireOp",EDGE,"E34.0.MirrorCS"),sQuery(id+"F4.wireOp",EDGE,"E35.filletArc"),sQuery(id+"F4.wireOp",EDGE,"E36.filletArc"),sQuery(id+"F4.wireOp",EDGE,"E37"),sQuery(id+"F4.wireOp",EDGE,"E38"),sQuery(id+"F4.wireOp",EDGE,"E39"),sQuery(id+"F4.wireOp",EDGE,"E40"),sQuery(id+"F4.wireOp",EDGE,"E41"),sQuery(id+"F4.wireOp",EDGE,"E42"),sQuery(id+"F4.wireOp",EDGE,"E43.filletArc"),sQuery(id+"F4.wireOp",EDGE,"E44.filletArc"),sQuery(id+"F4.wireOp",EDGE,"E45.trimOffspring"),sQuery(id+"F4.wireOp",EDGE,"E46.trimOffspring"),sQuery(id+"F4.wireOp",EDGE,"E47"),sQuery(id+"F4.wireOp",EDGE,"E48"),sQuery(id+"F4.wireOp",EDGE,"E49"),sQuery(id+"F4.wireOp",EDGE,"E50"),sQuery(id+"F4.wireOp",EDGE,"E51"),sQuery(id+"F4.wireOp",EDGE,"E52"),sQuery(id+"F4.wireOp",EDGE,"E53"),sQuery(id+"F4.wireOp",EDGE,"E54.filletArc"),sQuery(id+"F4.wireOp",EDGE,"E55.filletArc"),sQuery(id+"F4.wireOp",EDGE,"E56.filletArc"),sQuery(id+"F4.wireOp",EDGE,"E57"),sQuery(id+"F4.wireOp",EDGE,"E58"),sQuery(id+"F4.wireOp",EDGE,"E59"),sQuery(id+"F4.wireOp",EDGE,"E60.trimOffspring"),sQuery(id+"F4.wireOp",EDGE,"E61.0.MirrorCS"),sQuery(id+"F4.wireOp",EDGE,"E61.1.MirrorCS"),sQuery(id+"F4.wireOp",EDGE,"E61.2.MirrorCS"),sQuery(id+"F4.wireOp",EDGE,"E61.4.MirrorCS"),sQuery(id+"F4.wireOp",EDGE,"E61.5.MirrorCS"),sQuery(id+"F4.wireOp",EDGE,"E61.7.MirrorCS"),sQuery(id+"F4.wireOp",EDGE,"E61.10.MirrorCS"),sQuery(id+"F4.wireOp",EDGE,"E62.0.MirrorCS"),sQuery(id+"F4.wireOp",EDGE,"E62.2.MirrorCS"),sQuery(id+"F4.wireOp",EDGE,"E62.3.MirrorCS"),sQuery(id+"F4.wireOp",EDGE,"E62.4.MirrorCS"),sQuery(id+"F4.wireOp",EDGE,"E61.3.MirrorCS"),sQuery(id+"F4.wireOp",EDGE,"E61.6.MirrorCS"),sQuery(id+"F4.wireOp",EDGE,"E63.0.MirrorCS"),sQuery(id+"F4.wireOp",EDGE,"E64.1.MirrorCS"),sQuery(id+"F4.wireOp",EDGE,"E64.2.MirrorCS"),sQuery(id+"F4.wireOp",EDGE,"E64.3.MirrorCS"),sQuery(id+"F4.wireOp",EDGE,"E64.4.MirrorCS"),sQuery(id+"F4.wireOp",EDGE,"E64.5.MirrorCS"),sQuery(id+"F4.wireOp",EDGE,"E64.6.MirrorCS"),sQuery(id+"F4.wireOp",EDGE,"E65.0.MirrorCS"),sQuery(id+"F4.wireOp",EDGE,"E66.0.MirrorCS"),sQuery(id+"F4.wireOp",EDGE,"E67.trimOffspring"),sQuery(id+"F4.wireOp",EDGE,"E68.trimOffspring")])]}),"instanceName":"19"});
            var Q332;
            Q332=makeQuery(id+"F6.opPattern","COPY",BODY,{"derivedFrom":makeQuery(id+"F5.opExtrude","SWEPT_BODY",BODY,{"disambiguationData":[OSD([sQuery(id+"F4.wireOp",EDGE,"E24"),sQuery(id+"F4.wireOp",EDGE,"E25"),sQuery(id+"F4.wireOp",EDGE,"E27"),sQuery(id+"F4.wireOp",EDGE,"E28"),sQuery(id+"F4.wireOp",EDGE,"E29"),sQuery(id+"F4.wireOp",EDGE,"E30.0.MirrorCS"),sQuery(id+"F4.wireOp",EDGE,"E31.0.MirrorCS"),sQuery(id+"F4.wireOp",EDGE,"E32.0.MirrorCS"),sQuery(id+"F4.wireOp",EDGE,"E33.0.MirrorCS"),sQuery(id+"F4.wireOp",EDGE,"E34.0.MirrorCS"),sQuery(id+"F4.wireOp",EDGE,"E35.filletArc"),sQuery(id+"F4.wireOp",EDGE,"E36.filletArc"),sQuery(id+"F4.wireOp",EDGE,"E37"),sQuery(id+"F4.wireOp",EDGE,"E38"),sQuery(id+"F4.wireOp",EDGE,"E39"),sQuery(id+"F4.wireOp",EDGE,"E40"),sQuery(id+"F4.wireOp",EDGE,"E41"),sQuery(id+"F4.wireOp",EDGE,"E42"),sQuery(id+"F4.wireOp",EDGE,"E43.filletArc"),sQuery(id+"F4.wireOp",EDGE,"E44.filletArc"),sQuery(id+"F4.wireOp",EDGE,"E45.trimOffspring"),sQuery(id+"F4.wireOp",EDGE,"E46.trimOffspring"),sQuery(id+"F4.wireOp",EDGE,"E47"),sQuery(id+"F4.wireOp",EDGE,"E48"),sQuery(id+"F4.wireOp",EDGE,"E49"),sQuery(id+"F4.wireOp",EDGE,"E50"),sQuery(id+"F4.wireOp",EDGE,"E51"),sQuery(id+"F4.wireOp",EDGE,"E52"),sQuery(id+"F4.wireOp",EDGE,"E53"),sQuery(id+"F4.wireOp",EDGE,"E54.filletArc"),sQuery(id+"F4.wireOp",EDGE,"E55.filletArc"),sQuery(id+"F4.wireOp",EDGE,"E56.filletArc"),sQuery(id+"F4.wireOp",EDGE,"E57"),sQuery(id+"F4.wireOp",EDGE,"E58"),sQuery(id+"F4.wireOp",EDGE,"E59"),sQuery(id+"F4.wireOp",EDGE,"E60.trimOffspring"),sQuery(id+"F4.wireOp",EDGE,"E61.0.MirrorCS"),sQuery(id+"F4.wireOp",EDGE,"E61.1.MirrorCS"),sQuery(id+"F4.wireOp",EDGE,"E61.2.MirrorCS"),sQuery(id+"F4.wireOp",EDGE,"E61.4.MirrorCS"),sQuery(id+"F4.wireOp",EDGE,"E61.5.MirrorCS"),sQuery(id+"F4.wireOp",EDGE,"E61.7.MirrorCS"),sQuery(id+"F4.wireOp",EDGE,"E61.10.MirrorCS"),sQuery(id+"F4.wireOp",EDGE,"E62.0.MirrorCS"),sQuery(id+"F4.wireOp",EDGE,"E62.2.MirrorCS"),sQuery(id+"F4.wireOp",EDGE,"E62.3.MirrorCS"),sQuery(id+"F4.wireOp",EDGE,"E62.4.MirrorCS"),sQuery(id+"F4.wireOp",EDGE,"E61.3.MirrorCS"),sQuery(id+"F4.wireOp",EDGE,"E61.6.MirrorCS"),sQuery(id+"F4.wireOp",EDGE,"E63.0.MirrorCS"),sQuery(id+"F4.wireOp",EDGE,"E64.1.MirrorCS"),sQuery(id+"F4.wireOp",EDGE,"E64.2.MirrorCS"),sQuery(id+"F4.wireOp",EDGE,"E64.3.MirrorCS"),sQuery(id+"F4.wireOp",EDGE,"E64.4.MirrorCS"),sQuery(id+"F4.wireOp",EDGE,"E64.5.MirrorCS"),sQuery(id+"F4.wireOp",EDGE,"E64.6.MirrorCS"),sQuery(id+"F4.wireOp",EDGE,"E65.0.MirrorCS"),sQuery(id+"F4.wireOp",EDGE,"E66.0.MirrorCS"),sQuery(id+"F4.wireOp",EDGE,"E67.trimOffspring"),sQuery(id+"F4.wireOp",EDGE,"E68.trimOffspring")])]}),"instanceName":"18"});
            var Q333;
            Q333=makeQuery(id+"F6.opPattern","COPY",BODY,{"derivedFrom":makeQuery(id+"F5.opExtrude","SWEPT_BODY",BODY,{"disambiguationData":[OSD([sQuery(id+"F4.wireOp",EDGE,"E24"),sQuery(id+"F4.wireOp",EDGE,"E25"),sQuery(id+"F4.wireOp",EDGE,"E27"),sQuery(id+"F4.wireOp",EDGE,"E28"),sQuery(id+"F4.wireOp",EDGE,"E29"),sQuery(id+"F4.wireOp",EDGE,"E30.0.MirrorCS"),sQuery(id+"F4.wireOp",EDGE,"E31.0.MirrorCS"),sQuery(id+"F4.wireOp",EDGE,"E32.0.MirrorCS"),sQuery(id+"F4.wireOp",EDGE,"E33.0.MirrorCS"),sQuery(id+"F4.wireOp",EDGE,"E34.0.MirrorCS"),sQuery(id+"F4.wireOp",EDGE,"E35.filletArc"),sQuery(id+"F4.wireOp",EDGE,"E36.filletArc"),sQuery(id+"F4.wireOp",EDGE,"E37"),sQuery(id+"F4.wireOp",EDGE,"E38"),sQuery(id+"F4.wireOp",EDGE,"E39"),sQuery(id+"F4.wireOp",EDGE,"E40"),sQuery(id+"F4.wireOp",EDGE,"E41"),sQuery(id+"F4.wireOp",EDGE,"E42"),sQuery(id+"F4.wireOp",EDGE,"E43.filletArc"),sQuery(id+"F4.wireOp",EDGE,"E44.filletArc"),sQuery(id+"F4.wireOp",EDGE,"E45.trimOffspring"),sQuery(id+"F4.wireOp",EDGE,"E46.trimOffspring"),sQuery(id+"F4.wireOp",EDGE,"E47"),sQuery(id+"F4.wireOp",EDGE,"E48"),sQuery(id+"F4.wireOp",EDGE,"E49"),sQuery(id+"F4.wireOp",EDGE,"E50"),sQuery(id+"F4.wireOp",EDGE,"E51"),sQuery(id+"F4.wireOp",EDGE,"E52"),sQuery(id+"F4.wireOp",EDGE,"E53"),sQuery(id+"F4.wireOp",EDGE,"E54.filletArc"),sQuery(id+"F4.wireOp",EDGE,"E55.filletArc"),sQuery(id+"F4.wireOp",EDGE,"E56.filletArc"),sQuery(id+"F4.wireOp",EDGE,"E57"),sQuery(id+"F4.wireOp",EDGE,"E58"),sQuery(id+"F4.wireOp",EDGE,"E59"),sQuery(id+"F4.wireOp",EDGE,"E60.trimOffspring"),sQuery(id+"F4.wireOp",EDGE,"E61.0.MirrorCS"),sQuery(id+"F4.wireOp",EDGE,"E61.1.MirrorCS"),sQuery(id+"F4.wireOp",EDGE,"E61.2.MirrorCS"),sQuery(id+"F4.wireOp",EDGE,"E61.4.MirrorCS"),sQuery(id+"F4.wireOp",EDGE,"E61.5.MirrorCS"),sQuery(id+"F4.wireOp",EDGE,"E61.7.MirrorCS"),sQuery(id+"F4.wireOp",EDGE,"E61.10.MirrorCS"),sQuery(id+"F4.wireOp",EDGE,"E62.0.MirrorCS"),sQuery(id+"F4.wireOp",EDGE,"E62.2.MirrorCS"),sQuery(id+"F4.wireOp",EDGE,"E62.3.MirrorCS"),sQuery(id+"F4.wireOp",EDGE,"E62.4.MirrorCS"),sQuery(id+"F4.wireOp",EDGE,"E61.3.MirrorCS"),sQuery(id+"F4.wireOp",EDGE,"E61.6.MirrorCS"),sQuery(id+"F4.wireOp",EDGE,"E63.0.MirrorCS"),sQuery(id+"F4.wireOp",EDGE,"E64.1.MirrorCS"),sQuery(id+"F4.wireOp",EDGE,"E64.2.MirrorCS"),sQuery(id+"F4.wireOp",EDGE,"E64.3.MirrorCS"),sQuery(id+"F4.wireOp",EDGE,"E64.4.MirrorCS"),sQuery(id+"F4.wireOp",EDGE,"E64.5.MirrorCS"),sQuery(id+"F4.wireOp",EDGE,"E64.6.MirrorCS"),sQuery(id+"F4.wireOp",EDGE,"E65.0.MirrorCS"),sQuery(id+"F4.wireOp",EDGE,"E66.0.MirrorCS"),sQuery(id+"F4.wireOp",EDGE,"E67.trimOffspring"),sQuery(id+"F4.wireOp",EDGE,"E68.trimOffspring")])]}),"instanceName":"17"});
            var Q334;
            Q334=makeQuery(id+"F6.opPattern","COPY",BODY,{"derivedFrom":makeQuery(id+"F5.opExtrude","SWEPT_BODY",BODY,{"disambiguationData":[OSD([sQuery(id+"F4.wireOp",EDGE,"E24"),sQuery(id+"F4.wireOp",EDGE,"E25"),sQuery(id+"F4.wireOp",EDGE,"E27"),sQuery(id+"F4.wireOp",EDGE,"E28"),sQuery(id+"F4.wireOp",EDGE,"E29"),sQuery(id+"F4.wireOp",EDGE,"E30.0.MirrorCS"),sQuery(id+"F4.wireOp",EDGE,"E31.0.MirrorCS"),sQuery(id+"F4.wireOp",EDGE,"E32.0.MirrorCS"),sQuery(id+"F4.wireOp",EDGE,"E33.0.MirrorCS"),sQuery(id+"F4.wireOp",EDGE,"E34.0.MirrorCS"),sQuery(id+"F4.wireOp",EDGE,"E35.filletArc"),sQuery(id+"F4.wireOp",EDGE,"E36.filletArc"),sQuery(id+"F4.wireOp",EDGE,"E37"),sQuery(id+"F4.wireOp",EDGE,"E38"),sQuery(id+"F4.wireOp",EDGE,"E39"),sQuery(id+"F4.wireOp",EDGE,"E40"),sQuery(id+"F4.wireOp",EDGE,"E41"),sQuery(id+"F4.wireOp",EDGE,"E42"),sQuery(id+"F4.wireOp",EDGE,"E43.filletArc"),sQuery(id+"F4.wireOp",EDGE,"E44.filletArc"),sQuery(id+"F4.wireOp",EDGE,"E45.trimOffspring"),sQuery(id+"F4.wireOp",EDGE,"E46.trimOffspring"),sQuery(id+"F4.wireOp",EDGE,"E47"),sQuery(id+"F4.wireOp",EDGE,"E48"),sQuery(id+"F4.wireOp",EDGE,"E49"),sQuery(id+"F4.wireOp",EDGE,"E50"),sQuery(id+"F4.wireOp",EDGE,"E51"),sQuery(id+"F4.wireOp",EDGE,"E52"),sQuery(id+"F4.wireOp",EDGE,"E53"),sQuery(id+"F4.wireOp",EDGE,"E54.filletArc"),sQuery(id+"F4.wireOp",EDGE,"E55.filletArc"),sQuery(id+"F4.wireOp",EDGE,"E56.filletArc"),sQuery(id+"F4.wireOp",EDGE,"E57"),sQuery(id+"F4.wireOp",EDGE,"E58"),sQuery(id+"F4.wireOp",EDGE,"E59"),sQuery(id+"F4.wireOp",EDGE,"E60.trimOffspring"),sQuery(id+"F4.wireOp",EDGE,"E61.0.MirrorCS"),sQuery(id+"F4.wireOp",EDGE,"E61.1.MirrorCS"),sQuery(id+"F4.wireOp",EDGE,"E61.2.MirrorCS"),sQuery(id+"F4.wireOp",EDGE,"E61.4.MirrorCS"),sQuery(id+"F4.wireOp",EDGE,"E61.5.MirrorCS"),sQuery(id+"F4.wireOp",EDGE,"E61.7.MirrorCS"),sQuery(id+"F4.wireOp",EDGE,"E61.10.MirrorCS"),sQuery(id+"F4.wireOp",EDGE,"E62.0.MirrorCS"),sQuery(id+"F4.wireOp",EDGE,"E62.2.MirrorCS"),sQuery(id+"F4.wireOp",EDGE,"E62.3.MirrorCS"),sQuery(id+"F4.wireOp",EDGE,"E62.4.MirrorCS"),sQuery(id+"F4.wireOp",EDGE,"E61.3.MirrorCS"),sQuery(id+"F4.wireOp",EDGE,"E61.6.MirrorCS"),sQuery(id+"F4.wireOp",EDGE,"E63.0.MirrorCS"),sQuery(id+"F4.wireOp",EDGE,"E64.1.MirrorCS"),sQuery(id+"F4.wireOp",EDGE,"E64.2.MirrorCS"),sQuery(id+"F4.wireOp",EDGE,"E64.3.MirrorCS"),sQuery(id+"F4.wireOp",EDGE,"E64.4.MirrorCS"),sQuery(id+"F4.wireOp",EDGE,"E64.5.MirrorCS"),sQuery(id+"F4.wireOp",EDGE,"E64.6.MirrorCS"),sQuery(id+"F4.wireOp",EDGE,"E65.0.MirrorCS"),sQuery(id+"F4.wireOp",EDGE,"E66.0.MirrorCS"),sQuery(id+"F4.wireOp",EDGE,"E67.trimOffspring"),sQuery(id+"F4.wireOp",EDGE,"E68.trimOffspring")])]}),"instanceName":"16"});
            var Q335;
            Q335=makeQuery(id+"F6.opPattern","COPY",BODY,{"derivedFrom":makeQuery(id+"F5.opExtrude","SWEPT_BODY",BODY,{"disambiguationData":[OSD([sQuery(id+"F4.wireOp",EDGE,"E24"),sQuery(id+"F4.wireOp",EDGE,"E25"),sQuery(id+"F4.wireOp",EDGE,"E27"),sQuery(id+"F4.wireOp",EDGE,"E28"),sQuery(id+"F4.wireOp",EDGE,"E29"),sQuery(id+"F4.wireOp",EDGE,"E30.0.MirrorCS"),sQuery(id+"F4.wireOp",EDGE,"E31.0.MirrorCS"),sQuery(id+"F4.wireOp",EDGE,"E32.0.MirrorCS"),sQuery(id+"F4.wireOp",EDGE,"E33.0.MirrorCS"),sQuery(id+"F4.wireOp",EDGE,"E34.0.MirrorCS"),sQuery(id+"F4.wireOp",EDGE,"E35.filletArc"),sQuery(id+"F4.wireOp",EDGE,"E36.filletArc"),sQuery(id+"F4.wireOp",EDGE,"E37"),sQuery(id+"F4.wireOp",EDGE,"E38"),sQuery(id+"F4.wireOp",EDGE,"E39"),sQuery(id+"F4.wireOp",EDGE,"E40"),sQuery(id+"F4.wireOp",EDGE,"E41"),sQuery(id+"F4.wireOp",EDGE,"E42"),sQuery(id+"F4.wireOp",EDGE,"E43.filletArc"),sQuery(id+"F4.wireOp",EDGE,"E44.filletArc"),sQuery(id+"F4.wireOp",EDGE,"E45.trimOffspring"),sQuery(id+"F4.wireOp",EDGE,"E46.trimOffspring"),sQuery(id+"F4.wireOp",EDGE,"E47"),sQuery(id+"F4.wireOp",EDGE,"E48"),sQuery(id+"F4.wireOp",EDGE,"E49"),sQuery(id+"F4.wireOp",EDGE,"E50"),sQuery(id+"F4.wireOp",EDGE,"E51"),sQuery(id+"F4.wireOp",EDGE,"E52"),sQuery(id+"F4.wireOp",EDGE,"E53"),sQuery(id+"F4.wireOp",EDGE,"E54.filletArc"),sQuery(id+"F4.wireOp",EDGE,"E55.filletArc"),sQuery(id+"F4.wireOp",EDGE,"E56.filletArc"),sQuery(id+"F4.wireOp",EDGE,"E57"),sQuery(id+"F4.wireOp",EDGE,"E58"),sQuery(id+"F4.wireOp",EDGE,"E59"),sQuery(id+"F4.wireOp",EDGE,"E60.trimOffspring"),sQuery(id+"F4.wireOp",EDGE,"E61.0.MirrorCS"),sQuery(id+"F4.wireOp",EDGE,"E61.1.MirrorCS"),sQuery(id+"F4.wireOp",EDGE,"E61.2.MirrorCS"),sQuery(id+"F4.wireOp",EDGE,"E61.4.MirrorCS"),sQuery(id+"F4.wireOp",EDGE,"E61.5.MirrorCS"),sQuery(id+"F4.wireOp",EDGE,"E61.7.MirrorCS"),sQuery(id+"F4.wireOp",EDGE,"E61.10.MirrorCS"),sQuery(id+"F4.wireOp",EDGE,"E62.0.MirrorCS"),sQuery(id+"F4.wireOp",EDGE,"E62.2.MirrorCS"),sQuery(id+"F4.wireOp",EDGE,"E62.3.MirrorCS"),sQuery(id+"F4.wireOp",EDGE,"E62.4.MirrorCS"),sQuery(id+"F4.wireOp",EDGE,"E61.3.MirrorCS"),sQuery(id+"F4.wireOp",EDGE,"E61.6.MirrorCS"),sQuery(id+"F4.wireOp",EDGE,"E63.0.MirrorCS"),sQuery(id+"F4.wireOp",EDGE,"E64.1.MirrorCS"),sQuery(id+"F4.wireOp",EDGE,"E64.2.MirrorCS"),sQuery(id+"F4.wireOp",EDGE,"E64.3.MirrorCS"),sQuery(id+"F4.wireOp",EDGE,"E64.4.MirrorCS"),sQuery(id+"F4.wireOp",EDGE,"E64.5.MirrorCS"),sQuery(id+"F4.wireOp",EDGE,"E64.6.MirrorCS"),sQuery(id+"F4.wireOp",EDGE,"E65.0.MirrorCS"),sQuery(id+"F4.wireOp",EDGE,"E66.0.MirrorCS"),sQuery(id+"F4.wireOp",EDGE,"E67.trimOffspring"),sQuery(id+"F4.wireOp",EDGE,"E68.trimOffspring")])]}),"instanceName":"15"});
            var Q336;
            Q336=makeQuery(id+"F6.opPattern","COPY",BODY,{"derivedFrom":makeQuery(id+"F5.opExtrude","SWEPT_BODY",BODY,{"disambiguationData":[OSD([sQuery(id+"F4.wireOp",EDGE,"E24"),sQuery(id+"F4.wireOp",EDGE,"E25"),sQuery(id+"F4.wireOp",EDGE,"E27"),sQuery(id+"F4.wireOp",EDGE,"E28"),sQuery(id+"F4.wireOp",EDGE,"E29"),sQuery(id+"F4.wireOp",EDGE,"E30.0.MirrorCS"),sQuery(id+"F4.wireOp",EDGE,"E31.0.MirrorCS"),sQuery(id+"F4.wireOp",EDGE,"E32.0.MirrorCS"),sQuery(id+"F4.wireOp",EDGE,"E33.0.MirrorCS"),sQuery(id+"F4.wireOp",EDGE,"E34.0.MirrorCS"),sQuery(id+"F4.wireOp",EDGE,"E35.filletArc"),sQuery(id+"F4.wireOp",EDGE,"E36.filletArc"),sQuery(id+"F4.wireOp",EDGE,"E37"),sQuery(id+"F4.wireOp",EDGE,"E38"),sQuery(id+"F4.wireOp",EDGE,"E39"),sQuery(id+"F4.wireOp",EDGE,"E40"),sQuery(id+"F4.wireOp",EDGE,"E41"),sQuery(id+"F4.wireOp",EDGE,"E42"),sQuery(id+"F4.wireOp",EDGE,"E43.filletArc"),sQuery(id+"F4.wireOp",EDGE,"E44.filletArc"),sQuery(id+"F4.wireOp",EDGE,"E45.trimOffspring"),sQuery(id+"F4.wireOp",EDGE,"E46.trimOffspring"),sQuery(id+"F4.wireOp",EDGE,"E47"),sQuery(id+"F4.wireOp",EDGE,"E48"),sQuery(id+"F4.wireOp",EDGE,"E49"),sQuery(id+"F4.wireOp",EDGE,"E50"),sQuery(id+"F4.wireOp",EDGE,"E51"),sQuery(id+"F4.wireOp",EDGE,"E52"),sQuery(id+"F4.wireOp",EDGE,"E53"),sQuery(id+"F4.wireOp",EDGE,"E54.filletArc"),sQuery(id+"F4.wireOp",EDGE,"E55.filletArc"),sQuery(id+"F4.wireOp",EDGE,"E56.filletArc"),sQuery(id+"F4.wireOp",EDGE,"E57"),sQuery(id+"F4.wireOp",EDGE,"E58"),sQuery(id+"F4.wireOp",EDGE,"E59"),sQuery(id+"F4.wireOp",EDGE,"E60.trimOffspring"),sQuery(id+"F4.wireOp",EDGE,"E61.0.MirrorCS"),sQuery(id+"F4.wireOp",EDGE,"E61.1.MirrorCS"),sQuery(id+"F4.wireOp",EDGE,"E61.2.MirrorCS"),sQuery(id+"F4.wireOp",EDGE,"E61.4.MirrorCS"),sQuery(id+"F4.wireOp",EDGE,"E61.5.MirrorCS"),sQuery(id+"F4.wireOp",EDGE,"E61.7.MirrorCS"),sQuery(id+"F4.wireOp",EDGE,"E61.10.MirrorCS"),sQuery(id+"F4.wireOp",EDGE,"E62.0.MirrorCS"),sQuery(id+"F4.wireOp",EDGE,"E62.2.MirrorCS"),sQuery(id+"F4.wireOp",EDGE,"E62.3.MirrorCS"),sQuery(id+"F4.wireOp",EDGE,"E62.4.MirrorCS"),sQuery(id+"F4.wireOp",EDGE,"E61.3.MirrorCS"),sQuery(id+"F4.wireOp",EDGE,"E61.6.MirrorCS"),sQuery(id+"F4.wireOp",EDGE,"E63.0.MirrorCS"),sQuery(id+"F4.wireOp",EDGE,"E64.1.MirrorCS"),sQuery(id+"F4.wireOp",EDGE,"E64.2.MirrorCS"),sQuery(id+"F4.wireOp",EDGE,"E64.3.MirrorCS"),sQuery(id+"F4.wireOp",EDGE,"E64.4.MirrorCS"),sQuery(id+"F4.wireOp",EDGE,"E64.5.MirrorCS"),sQuery(id+"F4.wireOp",EDGE,"E64.6.MirrorCS"),sQuery(id+"F4.wireOp",EDGE,"E65.0.MirrorCS"),sQuery(id+"F4.wireOp",EDGE,"E66.0.MirrorCS"),sQuery(id+"F4.wireOp",EDGE,"E67.trimOffspring"),sQuery(id+"F4.wireOp",EDGE,"E68.trimOffspring")])]}),"instanceName":"14"});
            var Q337;
            Q337=makeQuery(id+"F6.opPattern","COPY",BODY,{"derivedFrom":makeQuery(id+"F5.opExtrude","SWEPT_BODY",BODY,{"disambiguationData":[OSD([sQuery(id+"F4.wireOp",EDGE,"E24"),sQuery(id+"F4.wireOp",EDGE,"E25"),sQuery(id+"F4.wireOp",EDGE,"E27"),sQuery(id+"F4.wireOp",EDGE,"E28"),sQuery(id+"F4.wireOp",EDGE,"E29"),sQuery(id+"F4.wireOp",EDGE,"E30.0.MirrorCS"),sQuery(id+"F4.wireOp",EDGE,"E31.0.MirrorCS"),sQuery(id+"F4.wireOp",EDGE,"E32.0.MirrorCS"),sQuery(id+"F4.wireOp",EDGE,"E33.0.MirrorCS"),sQuery(id+"F4.wireOp",EDGE,"E34.0.MirrorCS"),sQuery(id+"F4.wireOp",EDGE,"E35.filletArc"),sQuery(id+"F4.wireOp",EDGE,"E36.filletArc"),sQuery(id+"F4.wireOp",EDGE,"E37"),sQuery(id+"F4.wireOp",EDGE,"E38"),sQuery(id+"F4.wireOp",EDGE,"E39"),sQuery(id+"F4.wireOp",EDGE,"E40"),sQuery(id+"F4.wireOp",EDGE,"E41"),sQuery(id+"F4.wireOp",EDGE,"E42"),sQuery(id+"F4.wireOp",EDGE,"E43.filletArc"),sQuery(id+"F4.wireOp",EDGE,"E44.filletArc"),sQuery(id+"F4.wireOp",EDGE,"E45.trimOffspring"),sQuery(id+"F4.wireOp",EDGE,"E46.trimOffspring"),sQuery(id+"F4.wireOp",EDGE,"E47"),sQuery(id+"F4.wireOp",EDGE,"E48"),sQuery(id+"F4.wireOp",EDGE,"E49"),sQuery(id+"F4.wireOp",EDGE,"E50"),sQuery(id+"F4.wireOp",EDGE,"E51"),sQuery(id+"F4.wireOp",EDGE,"E52"),sQuery(id+"F4.wireOp",EDGE,"E53"),sQuery(id+"F4.wireOp",EDGE,"E54.filletArc"),sQuery(id+"F4.wireOp",EDGE,"E55.filletArc"),sQuery(id+"F4.wireOp",EDGE,"E56.filletArc"),sQuery(id+"F4.wireOp",EDGE,"E57"),sQuery(id+"F4.wireOp",EDGE,"E58"),sQuery(id+"F4.wireOp",EDGE,"E59"),sQuery(id+"F4.wireOp",EDGE,"E60.trimOffspring"),sQuery(id+"F4.wireOp",EDGE,"E61.0.MirrorCS"),sQuery(id+"F4.wireOp",EDGE,"E61.1.MirrorCS"),sQuery(id+"F4.wireOp",EDGE,"E61.2.MirrorCS"),sQuery(id+"F4.wireOp",EDGE,"E61.4.MirrorCS"),sQuery(id+"F4.wireOp",EDGE,"E61.5.MirrorCS"),sQuery(id+"F4.wireOp",EDGE,"E61.7.MirrorCS"),sQuery(id+"F4.wireOp",EDGE,"E61.10.MirrorCS"),sQuery(id+"F4.wireOp",EDGE,"E62.0.MirrorCS"),sQuery(id+"F4.wireOp",EDGE,"E62.2.MirrorCS"),sQuery(id+"F4.wireOp",EDGE,"E62.3.MirrorCS"),sQuery(id+"F4.wireOp",EDGE,"E62.4.MirrorCS"),sQuery(id+"F4.wireOp",EDGE,"E61.3.MirrorCS"),sQuery(id+"F4.wireOp",EDGE,"E61.6.MirrorCS"),sQuery(id+"F4.wireOp",EDGE,"E63.0.MirrorCS"),sQuery(id+"F4.wireOp",EDGE,"E64.1.MirrorCS"),sQuery(id+"F4.wireOp",EDGE,"E64.2.MirrorCS"),sQuery(id+"F4.wireOp",EDGE,"E64.3.MirrorCS"),sQuery(id+"F4.wireOp",EDGE,"E64.4.MirrorCS"),sQuery(id+"F4.wireOp",EDGE,"E64.5.MirrorCS"),sQuery(id+"F4.wireOp",EDGE,"E64.6.MirrorCS"),sQuery(id+"F4.wireOp",EDGE,"E65.0.MirrorCS"),sQuery(id+"F4.wireOp",EDGE,"E66.0.MirrorCS"),sQuery(id+"F4.wireOp",EDGE,"E67.trimOffspring"),sQuery(id+"F4.wireOp",EDGE,"E68.trimOffspring")])]}),"instanceName":"13"});
            var Q338;
            Q338=makeQuery(id+"F6.opPattern","COPY",BODY,{"derivedFrom":makeQuery(id+"F5.opExtrude","SWEPT_BODY",BODY,{"disambiguationData":[OSD([sQuery(id+"F4.wireOp",EDGE,"E24"),sQuery(id+"F4.wireOp",EDGE,"E25"),sQuery(id+"F4.wireOp",EDGE,"E27"),sQuery(id+"F4.wireOp",EDGE,"E28"),sQuery(id+"F4.wireOp",EDGE,"E29"),sQuery(id+"F4.wireOp",EDGE,"E30.0.MirrorCS"),sQuery(id+"F4.wireOp",EDGE,"E31.0.MirrorCS"),sQuery(id+"F4.wireOp",EDGE,"E32.0.MirrorCS"),sQuery(id+"F4.wireOp",EDGE,"E33.0.MirrorCS"),sQuery(id+"F4.wireOp",EDGE,"E34.0.MirrorCS"),sQuery(id+"F4.wireOp",EDGE,"E35.filletArc"),sQuery(id+"F4.wireOp",EDGE,"E36.filletArc"),sQuery(id+"F4.wireOp",EDGE,"E37"),sQuery(id+"F4.wireOp",EDGE,"E38"),sQuery(id+"F4.wireOp",EDGE,"E39"),sQuery(id+"F4.wireOp",EDGE,"E40"),sQuery(id+"F4.wireOp",EDGE,"E41"),sQuery(id+"F4.wireOp",EDGE,"E42"),sQuery(id+"F4.wireOp",EDGE,"E43.filletArc"),sQuery(id+"F4.wireOp",EDGE,"E44.filletArc"),sQuery(id+"F4.wireOp",EDGE,"E45.trimOffspring"),sQuery(id+"F4.wireOp",EDGE,"E46.trimOffspring"),sQuery(id+"F4.wireOp",EDGE,"E47"),sQuery(id+"F4.wireOp",EDGE,"E48"),sQuery(id+"F4.wireOp",EDGE,"E49"),sQuery(id+"F4.wireOp",EDGE,"E50"),sQuery(id+"F4.wireOp",EDGE,"E51"),sQuery(id+"F4.wireOp",EDGE,"E52"),sQuery(id+"F4.wireOp",EDGE,"E53"),sQuery(id+"F4.wireOp",EDGE,"E54.filletArc"),sQuery(id+"F4.wireOp",EDGE,"E55.filletArc"),sQuery(id+"F4.wireOp",EDGE,"E56.filletArc"),sQuery(id+"F4.wireOp",EDGE,"E57"),sQuery(id+"F4.wireOp",EDGE,"E58"),sQuery(id+"F4.wireOp",EDGE,"E59"),sQuery(id+"F4.wireOp",EDGE,"E60.trimOffspring"),sQuery(id+"F4.wireOp",EDGE,"E61.0.MirrorCS"),sQuery(id+"F4.wireOp",EDGE,"E61.1.MirrorCS"),sQuery(id+"F4.wireOp",EDGE,"E61.2.MirrorCS"),sQuery(id+"F4.wireOp",EDGE,"E61.4.MirrorCS"),sQuery(id+"F4.wireOp",EDGE,"E61.5.MirrorCS"),sQuery(id+"F4.wireOp",EDGE,"E61.7.MirrorCS"),sQuery(id+"F4.wireOp",EDGE,"E61.10.MirrorCS"),sQuery(id+"F4.wireOp",EDGE,"E62.0.MirrorCS"),sQuery(id+"F4.wireOp",EDGE,"E62.2.MirrorCS"),sQuery(id+"F4.wireOp",EDGE,"E62.3.MirrorCS"),sQuery(id+"F4.wireOp",EDGE,"E62.4.MirrorCS"),sQuery(id+"F4.wireOp",EDGE,"E61.3.MirrorCS"),sQuery(id+"F4.wireOp",EDGE,"E61.6.MirrorCS"),sQuery(id+"F4.wireOp",EDGE,"E63.0.MirrorCS"),sQuery(id+"F4.wireOp",EDGE,"E64.1.MirrorCS"),sQuery(id+"F4.wireOp",EDGE,"E64.2.MirrorCS"),sQuery(id+"F4.wireOp",EDGE,"E64.3.MirrorCS"),sQuery(id+"F4.wireOp",EDGE,"E64.4.MirrorCS"),sQuery(id+"F4.wireOp",EDGE,"E64.5.MirrorCS"),sQuery(id+"F4.wireOp",EDGE,"E64.6.MirrorCS"),sQuery(id+"F4.wireOp",EDGE,"E65.0.MirrorCS"),sQuery(id+"F4.wireOp",EDGE,"E66.0.MirrorCS"),sQuery(id+"F4.wireOp",EDGE,"E67.trimOffspring"),sQuery(id+"F4.wireOp",EDGE,"E68.trimOffspring")])]}),"instanceName":"12"});
            var Q339;
            Q339=makeQuery(id+"F6.opPattern","COPY",BODY,{"derivedFrom":makeQuery(id+"F5.opExtrude","SWEPT_BODY",BODY,{"disambiguationData":[OSD([sQuery(id+"F4.wireOp",EDGE,"E24"),sQuery(id+"F4.wireOp",EDGE,"E25"),sQuery(id+"F4.wireOp",EDGE,"E27"),sQuery(id+"F4.wireOp",EDGE,"E28"),sQuery(id+"F4.wireOp",EDGE,"E29"),sQuery(id+"F4.wireOp",EDGE,"E30.0.MirrorCS"),sQuery(id+"F4.wireOp",EDGE,"E31.0.MirrorCS"),sQuery(id+"F4.wireOp",EDGE,"E32.0.MirrorCS"),sQuery(id+"F4.wireOp",EDGE,"E33.0.MirrorCS"),sQuery(id+"F4.wireOp",EDGE,"E34.0.MirrorCS"),sQuery(id+"F4.wireOp",EDGE,"E35.filletArc"),sQuery(id+"F4.wireOp",EDGE,"E36.filletArc"),sQuery(id+"F4.wireOp",EDGE,"E37"),sQuery(id+"F4.wireOp",EDGE,"E38"),sQuery(id+"F4.wireOp",EDGE,"E39"),sQuery(id+"F4.wireOp",EDGE,"E40"),sQuery(id+"F4.wireOp",EDGE,"E41"),sQuery(id+"F4.wireOp",EDGE,"E42"),sQuery(id+"F4.wireOp",EDGE,"E43.filletArc"),sQuery(id+"F4.wireOp",EDGE,"E44.filletArc"),sQuery(id+"F4.wireOp",EDGE,"E45.trimOffspring"),sQuery(id+"F4.wireOp",EDGE,"E46.trimOffspring"),sQuery(id+"F4.wireOp",EDGE,"E47"),sQuery(id+"F4.wireOp",EDGE,"E48"),sQuery(id+"F4.wireOp",EDGE,"E49"),sQuery(id+"F4.wireOp",EDGE,"E50"),sQuery(id+"F4.wireOp",EDGE,"E51"),sQuery(id+"F4.wireOp",EDGE,"E52"),sQuery(id+"F4.wireOp",EDGE,"E53"),sQuery(id+"F4.wireOp",EDGE,"E54.filletArc"),sQuery(id+"F4.wireOp",EDGE,"E55.filletArc"),sQuery(id+"F4.wireOp",EDGE,"E56.filletArc"),sQuery(id+"F4.wireOp",EDGE,"E57"),sQuery(id+"F4.wireOp",EDGE,"E58"),sQuery(id+"F4.wireOp",EDGE,"E59"),sQuery(id+"F4.wireOp",EDGE,"E60.trimOffspring"),sQuery(id+"F4.wireOp",EDGE,"E61.0.MirrorCS"),sQuery(id+"F4.wireOp",EDGE,"E61.1.MirrorCS"),sQuery(id+"F4.wireOp",EDGE,"E61.2.MirrorCS"),sQuery(id+"F4.wireOp",EDGE,"E61.4.MirrorCS"),sQuery(id+"F4.wireOp",EDGE,"E61.5.MirrorCS"),sQuery(id+"F4.wireOp",EDGE,"E61.7.MirrorCS"),sQuery(id+"F4.wireOp",EDGE,"E61.10.MirrorCS"),sQuery(id+"F4.wireOp",EDGE,"E62.0.MirrorCS"),sQuery(id+"F4.wireOp",EDGE,"E62.2.MirrorCS"),sQuery(id+"F4.wireOp",EDGE,"E62.3.MirrorCS"),sQuery(id+"F4.wireOp",EDGE,"E62.4.MirrorCS"),sQuery(id+"F4.wireOp",EDGE,"E61.3.MirrorCS"),sQuery(id+"F4.wireOp",EDGE,"E61.6.MirrorCS"),sQuery(id+"F4.wireOp",EDGE,"E63.0.MirrorCS"),sQuery(id+"F4.wireOp",EDGE,"E64.1.MirrorCS"),sQuery(id+"F4.wireOp",EDGE,"E64.2.MirrorCS"),sQuery(id+"F4.wireOp",EDGE,"E64.3.MirrorCS"),sQuery(id+"F4.wireOp",EDGE,"E64.4.MirrorCS"),sQuery(id+"F4.wireOp",EDGE,"E64.5.MirrorCS"),sQuery(id+"F4.wireOp",EDGE,"E64.6.MirrorCS"),sQuery(id+"F4.wireOp",EDGE,"E65.0.MirrorCS"),sQuery(id+"F4.wireOp",EDGE,"E66.0.MirrorCS"),sQuery(id+"F4.wireOp",EDGE,"E67.trimOffspring"),sQuery(id+"F4.wireOp",EDGE,"E68.trimOffspring")])]}),"instanceName":"11"});
            var Q340;
            Q340=makeQuery(id+"F6.opPattern","COPY",BODY,{"derivedFrom":makeQuery(id+"F5.opExtrude","SWEPT_BODY",BODY,{"disambiguationData":[OSD([sQuery(id+"F4.wireOp",EDGE,"E24"),sQuery(id+"F4.wireOp",EDGE,"E25"),sQuery(id+"F4.wireOp",EDGE,"E27"),sQuery(id+"F4.wireOp",EDGE,"E28"),sQuery(id+"F4.wireOp",EDGE,"E29"),sQuery(id+"F4.wireOp",EDGE,"E30.0.MirrorCS"),sQuery(id+"F4.wireOp",EDGE,"E31.0.MirrorCS"),sQuery(id+"F4.wireOp",EDGE,"E32.0.MirrorCS"),sQuery(id+"F4.wireOp",EDGE,"E33.0.MirrorCS"),sQuery(id+"F4.wireOp",EDGE,"E34.0.MirrorCS"),sQuery(id+"F4.wireOp",EDGE,"E35.filletArc"),sQuery(id+"F4.wireOp",EDGE,"E36.filletArc"),sQuery(id+"F4.wireOp",EDGE,"E37"),sQuery(id+"F4.wireOp",EDGE,"E38"),sQuery(id+"F4.wireOp",EDGE,"E39"),sQuery(id+"F4.wireOp",EDGE,"E40"),sQuery(id+"F4.wireOp",EDGE,"E41"),sQuery(id+"F4.wireOp",EDGE,"E42"),sQuery(id+"F4.wireOp",EDGE,"E43.filletArc"),sQuery(id+"F4.wireOp",EDGE,"E44.filletArc"),sQuery(id+"F4.wireOp",EDGE,"E45.trimOffspring"),sQuery(id+"F4.wireOp",EDGE,"E46.trimOffspring"),sQuery(id+"F4.wireOp",EDGE,"E47"),sQuery(id+"F4.wireOp",EDGE,"E48"),sQuery(id+"F4.wireOp",EDGE,"E49"),sQuery(id+"F4.wireOp",EDGE,"E50"),sQuery(id+"F4.wireOp",EDGE,"E51"),sQuery(id+"F4.wireOp",EDGE,"E52"),sQuery(id+"F4.wireOp",EDGE,"E53"),sQuery(id+"F4.wireOp",EDGE,"E54.filletArc"),sQuery(id+"F4.wireOp",EDGE,"E55.filletArc"),sQuery(id+"F4.wireOp",EDGE,"E56.filletArc"),sQuery(id+"F4.wireOp",EDGE,"E57"),sQuery(id+"F4.wireOp",EDGE,"E58"),sQuery(id+"F4.wireOp",EDGE,"E59"),sQuery(id+"F4.wireOp",EDGE,"E60.trimOffspring"),sQuery(id+"F4.wireOp",EDGE,"E61.0.MirrorCS"),sQuery(id+"F4.wireOp",EDGE,"E61.1.MirrorCS"),sQuery(id+"F4.wireOp",EDGE,"E61.2.MirrorCS"),sQuery(id+"F4.wireOp",EDGE,"E61.4.MirrorCS"),sQuery(id+"F4.wireOp",EDGE,"E61.5.MirrorCS"),sQuery(id+"F4.wireOp",EDGE,"E61.7.MirrorCS"),sQuery(id+"F4.wireOp",EDGE,"E61.10.MirrorCS"),sQuery(id+"F4.wireOp",EDGE,"E62.0.MirrorCS"),sQuery(id+"F4.wireOp",EDGE,"E62.2.MirrorCS"),sQuery(id+"F4.wireOp",EDGE,"E62.3.MirrorCS"),sQuery(id+"F4.wireOp",EDGE,"E62.4.MirrorCS"),sQuery(id+"F4.wireOp",EDGE,"E61.3.MirrorCS"),sQuery(id+"F4.wireOp",EDGE,"E61.6.MirrorCS"),sQuery(id+"F4.wireOp",EDGE,"E63.0.MirrorCS"),sQuery(id+"F4.wireOp",EDGE,"E64.1.MirrorCS"),sQuery(id+"F4.wireOp",EDGE,"E64.2.MirrorCS"),sQuery(id+"F4.wireOp",EDGE,"E64.3.MirrorCS"),sQuery(id+"F4.wireOp",EDGE,"E64.4.MirrorCS"),sQuery(id+"F4.wireOp",EDGE,"E64.5.MirrorCS"),sQuery(id+"F4.wireOp",EDGE,"E64.6.MirrorCS"),sQuery(id+"F4.wireOp",EDGE,"E65.0.MirrorCS"),sQuery(id+"F4.wireOp",EDGE,"E66.0.MirrorCS"),sQuery(id+"F4.wireOp",EDGE,"E67.trimOffspring"),sQuery(id+"F4.wireOp",EDGE,"E68.trimOffspring")])]}),"instanceName":"10"});
            var Q341;
            Q341=makeQuery(id+"F6.opPattern","COPY",BODY,{"derivedFrom":makeQuery(id+"F5.opExtrude","SWEPT_BODY",BODY,{"disambiguationData":[OSD([sQuery(id+"F4.wireOp",EDGE,"E24"),sQuery(id+"F4.wireOp",EDGE,"E25"),sQuery(id+"F4.wireOp",EDGE,"E27"),sQuery(id+"F4.wireOp",EDGE,"E28"),sQuery(id+"F4.wireOp",EDGE,"E29"),sQuery(id+"F4.wireOp",EDGE,"E30.0.MirrorCS"),sQuery(id+"F4.wireOp",EDGE,"E31.0.MirrorCS"),sQuery(id+"F4.wireOp",EDGE,"E32.0.MirrorCS"),sQuery(id+"F4.wireOp",EDGE,"E33.0.MirrorCS"),sQuery(id+"F4.wireOp",EDGE,"E34.0.MirrorCS"),sQuery(id+"F4.wireOp",EDGE,"E35.filletArc"),sQuery(id+"F4.wireOp",EDGE,"E36.filletArc"),sQuery(id+"F4.wireOp",EDGE,"E37"),sQuery(id+"F4.wireOp",EDGE,"E38"),sQuery(id+"F4.wireOp",EDGE,"E39"),sQuery(id+"F4.wireOp",EDGE,"E40"),sQuery(id+"F4.wireOp",EDGE,"E41"),sQuery(id+"F4.wireOp",EDGE,"E42"),sQuery(id+"F4.wireOp",EDGE,"E43.filletArc"),sQuery(id+"F4.wireOp",EDGE,"E44.filletArc"),sQuery(id+"F4.wireOp",EDGE,"E45.trimOffspring"),sQuery(id+"F4.wireOp",EDGE,"E46.trimOffspring"),sQuery(id+"F4.wireOp",EDGE,"E47"),sQuery(id+"F4.wireOp",EDGE,"E48"),sQuery(id+"F4.wireOp",EDGE,"E49"),sQuery(id+"F4.wireOp",EDGE,"E50"),sQuery(id+"F4.wireOp",EDGE,"E51"),sQuery(id+"F4.wireOp",EDGE,"E52"),sQuery(id+"F4.wireOp",EDGE,"E53"),sQuery(id+"F4.wireOp",EDGE,"E54.filletArc"),sQuery(id+"F4.wireOp",EDGE,"E55.filletArc"),sQuery(id+"F4.wireOp",EDGE,"E56.filletArc"),sQuery(id+"F4.wireOp",EDGE,"E57"),sQuery(id+"F4.wireOp",EDGE,"E58"),sQuery(id+"F4.wireOp",EDGE,"E59"),sQuery(id+"F4.wireOp",EDGE,"E60.trimOffspring"),sQuery(id+"F4.wireOp",EDGE,"E61.0.MirrorCS"),sQuery(id+"F4.wireOp",EDGE,"E61.1.MirrorCS"),sQuery(id+"F4.wireOp",EDGE,"E61.2.MirrorCS"),sQuery(id+"F4.wireOp",EDGE,"E61.4.MirrorCS"),sQuery(id+"F4.wireOp",EDGE,"E61.5.MirrorCS"),sQuery(id+"F4.wireOp",EDGE,"E61.7.MirrorCS"),sQuery(id+"F4.wireOp",EDGE,"E61.10.MirrorCS"),sQuery(id+"F4.wireOp",EDGE,"E62.0.MirrorCS"),sQuery(id+"F4.wireOp",EDGE,"E62.2.MirrorCS"),sQuery(id+"F4.wireOp",EDGE,"E62.3.MirrorCS"),sQuery(id+"F4.wireOp",EDGE,"E62.4.MirrorCS"),sQuery(id+"F4.wireOp",EDGE,"E61.3.MirrorCS"),sQuery(id+"F4.wireOp",EDGE,"E61.6.MirrorCS"),sQuery(id+"F4.wireOp",EDGE,"E63.0.MirrorCS"),sQuery(id+"F4.wireOp",EDGE,"E64.1.MirrorCS"),sQuery(id+"F4.wireOp",EDGE,"E64.2.MirrorCS"),sQuery(id+"F4.wireOp",EDGE,"E64.3.MirrorCS"),sQuery(id+"F4.wireOp",EDGE,"E64.4.MirrorCS"),sQuery(id+"F4.wireOp",EDGE,"E64.5.MirrorCS"),sQuery(id+"F4.wireOp",EDGE,"E64.6.MirrorCS"),sQuery(id+"F4.wireOp",EDGE,"E65.0.MirrorCS"),sQuery(id+"F4.wireOp",EDGE,"E66.0.MirrorCS"),sQuery(id+"F4.wireOp",EDGE,"E67.trimOffspring"),sQuery(id+"F4.wireOp",EDGE,"E68.trimOffspring")])]}),"instanceName":"9"});
            var Q342;
            Q342=makeQuery(id+"F6.opPattern","COPY",BODY,{"derivedFrom":makeQuery(id+"F5.opExtrude","SWEPT_BODY",BODY,{"disambiguationData":[OSD([sQuery(id+"F4.wireOp",EDGE,"E24"),sQuery(id+"F4.wireOp",EDGE,"E25"),sQuery(id+"F4.wireOp",EDGE,"E27"),sQuery(id+"F4.wireOp",EDGE,"E28"),sQuery(id+"F4.wireOp",EDGE,"E29"),sQuery(id+"F4.wireOp",EDGE,"E30.0.MirrorCS"),sQuery(id+"F4.wireOp",EDGE,"E31.0.MirrorCS"),sQuery(id+"F4.wireOp",EDGE,"E32.0.MirrorCS"),sQuery(id+"F4.wireOp",EDGE,"E33.0.MirrorCS"),sQuery(id+"F4.wireOp",EDGE,"E34.0.MirrorCS"),sQuery(id+"F4.wireOp",EDGE,"E35.filletArc"),sQuery(id+"F4.wireOp",EDGE,"E36.filletArc"),sQuery(id+"F4.wireOp",EDGE,"E37"),sQuery(id+"F4.wireOp",EDGE,"E38"),sQuery(id+"F4.wireOp",EDGE,"E39"),sQuery(id+"F4.wireOp",EDGE,"E40"),sQuery(id+"F4.wireOp",EDGE,"E41"),sQuery(id+"F4.wireOp",EDGE,"E42"),sQuery(id+"F4.wireOp",EDGE,"E43.filletArc"),sQuery(id+"F4.wireOp",EDGE,"E44.filletArc"),sQuery(id+"F4.wireOp",EDGE,"E45.trimOffspring"),sQuery(id+"F4.wireOp",EDGE,"E46.trimOffspring"),sQuery(id+"F4.wireOp",EDGE,"E47"),sQuery(id+"F4.wireOp",EDGE,"E48"),sQuery(id+"F4.wireOp",EDGE,"E49"),sQuery(id+"F4.wireOp",EDGE,"E50"),sQuery(id+"F4.wireOp",EDGE,"E51"),sQuery(id+"F4.wireOp",EDGE,"E52"),sQuery(id+"F4.wireOp",EDGE,"E53"),sQuery(id+"F4.wireOp",EDGE,"E54.filletArc"),sQuery(id+"F4.wireOp",EDGE,"E55.filletArc"),sQuery(id+"F4.wireOp",EDGE,"E56.filletArc"),sQuery(id+"F4.wireOp",EDGE,"E57"),sQuery(id+"F4.wireOp",EDGE,"E58"),sQuery(id+"F4.wireOp",EDGE,"E59"),sQuery(id+"F4.wireOp",EDGE,"E60.trimOffspring"),sQuery(id+"F4.wireOp",EDGE,"E61.0.MirrorCS"),sQuery(id+"F4.wireOp",EDGE,"E61.1.MirrorCS"),sQuery(id+"F4.wireOp",EDGE,"E61.2.MirrorCS"),sQuery(id+"F4.wireOp",EDGE,"E61.4.MirrorCS"),sQuery(id+"F4.wireOp",EDGE,"E61.5.MirrorCS"),sQuery(id+"F4.wireOp",EDGE,"E61.7.MirrorCS"),sQuery(id+"F4.wireOp",EDGE,"E61.10.MirrorCS"),sQuery(id+"F4.wireOp",EDGE,"E62.0.MirrorCS"),sQuery(id+"F4.wireOp",EDGE,"E62.2.MirrorCS"),sQuery(id+"F4.wireOp",EDGE,"E62.3.MirrorCS"),sQuery(id+"F4.wireOp",EDGE,"E62.4.MirrorCS"),sQuery(id+"F4.wireOp",EDGE,"E61.3.MirrorCS"),sQuery(id+"F4.wireOp",EDGE,"E61.6.MirrorCS"),sQuery(id+"F4.wireOp",EDGE,"E63.0.MirrorCS"),sQuery(id+"F4.wireOp",EDGE,"E64.1.MirrorCS"),sQuery(id+"F4.wireOp",EDGE,"E64.2.MirrorCS"),sQuery(id+"F4.wireOp",EDGE,"E64.3.MirrorCS"),sQuery(id+"F4.wireOp",EDGE,"E64.4.MirrorCS"),sQuery(id+"F4.wireOp",EDGE,"E64.5.MirrorCS"),sQuery(id+"F4.wireOp",EDGE,"E64.6.MirrorCS"),sQuery(id+"F4.wireOp",EDGE,"E65.0.MirrorCS"),sQuery(id+"F4.wireOp",EDGE,"E66.0.MirrorCS"),sQuery(id+"F4.wireOp",EDGE,"E67.trimOffspring"),sQuery(id+"F4.wireOp",EDGE,"E68.trimOffspring")])]}),"instanceName":"8"});
            var Q343;
            Q343=makeQuery(id+"F6.opPattern","COPY",BODY,{"derivedFrom":makeQuery(id+"F5.opExtrude","SWEPT_BODY",BODY,{"disambiguationData":[OSD([sQuery(id+"F4.wireOp",EDGE,"E24"),sQuery(id+"F4.wireOp",EDGE,"E25"),sQuery(id+"F4.wireOp",EDGE,"E27"),sQuery(id+"F4.wireOp",EDGE,"E28"),sQuery(id+"F4.wireOp",EDGE,"E29"),sQuery(id+"F4.wireOp",EDGE,"E30.0.MirrorCS"),sQuery(id+"F4.wireOp",EDGE,"E31.0.MirrorCS"),sQuery(id+"F4.wireOp",EDGE,"E32.0.MirrorCS"),sQuery(id+"F4.wireOp",EDGE,"E33.0.MirrorCS"),sQuery(id+"F4.wireOp",EDGE,"E34.0.MirrorCS"),sQuery(id+"F4.wireOp",EDGE,"E35.filletArc"),sQuery(id+"F4.wireOp",EDGE,"E36.filletArc"),sQuery(id+"F4.wireOp",EDGE,"E37"),sQuery(id+"F4.wireOp",EDGE,"E38"),sQuery(id+"F4.wireOp",EDGE,"E39"),sQuery(id+"F4.wireOp",EDGE,"E40"),sQuery(id+"F4.wireOp",EDGE,"E41"),sQuery(id+"F4.wireOp",EDGE,"E42"),sQuery(id+"F4.wireOp",EDGE,"E43.filletArc"),sQuery(id+"F4.wireOp",EDGE,"E44.filletArc"),sQuery(id+"F4.wireOp",EDGE,"E45.trimOffspring"),sQuery(id+"F4.wireOp",EDGE,"E46.trimOffspring"),sQuery(id+"F4.wireOp",EDGE,"E47"),sQuery(id+"F4.wireOp",EDGE,"E48"),sQuery(id+"F4.wireOp",EDGE,"E49"),sQuery(id+"F4.wireOp",EDGE,"E50"),sQuery(id+"F4.wireOp",EDGE,"E51"),sQuery(id+"F4.wireOp",EDGE,"E52"),sQuery(id+"F4.wireOp",EDGE,"E53"),sQuery(id+"F4.wireOp",EDGE,"E54.filletArc"),sQuery(id+"F4.wireOp",EDGE,"E55.filletArc"),sQuery(id+"F4.wireOp",EDGE,"E56.filletArc"),sQuery(id+"F4.wireOp",EDGE,"E57"),sQuery(id+"F4.wireOp",EDGE,"E58"),sQuery(id+"F4.wireOp",EDGE,"E59"),sQuery(id+"F4.wireOp",EDGE,"E60.trimOffspring"),sQuery(id+"F4.wireOp",EDGE,"E61.0.MirrorCS"),sQuery(id+"F4.wireOp",EDGE,"E61.1.MirrorCS"),sQuery(id+"F4.wireOp",EDGE,"E61.2.MirrorCS"),sQuery(id+"F4.wireOp",EDGE,"E61.4.MirrorCS"),sQuery(id+"F4.wireOp",EDGE,"E61.5.MirrorCS"),sQuery(id+"F4.wireOp",EDGE,"E61.7.MirrorCS"),sQuery(id+"F4.wireOp",EDGE,"E61.10.MirrorCS"),sQuery(id+"F4.wireOp",EDGE,"E62.0.MirrorCS"),sQuery(id+"F4.wireOp",EDGE,"E62.2.MirrorCS"),sQuery(id+"F4.wireOp",EDGE,"E62.3.MirrorCS"),sQuery(id+"F4.wireOp",EDGE,"E62.4.MirrorCS"),sQuery(id+"F4.wireOp",EDGE,"E61.3.MirrorCS"),sQuery(id+"F4.wireOp",EDGE,"E61.6.MirrorCS"),sQuery(id+"F4.wireOp",EDGE,"E63.0.MirrorCS"),sQuery(id+"F4.wireOp",EDGE,"E64.1.MirrorCS"),sQuery(id+"F4.wireOp",EDGE,"E64.2.MirrorCS"),sQuery(id+"F4.wireOp",EDGE,"E64.3.MirrorCS"),sQuery(id+"F4.wireOp",EDGE,"E64.4.MirrorCS"),sQuery(id+"F4.wireOp",EDGE,"E64.5.MirrorCS"),sQuery(id+"F4.wireOp",EDGE,"E64.6.MirrorCS"),sQuery(id+"F4.wireOp",EDGE,"E65.0.MirrorCS"),sQuery(id+"F4.wireOp",EDGE,"E66.0.MirrorCS"),sQuery(id+"F4.wireOp",EDGE,"E67.trimOffspring"),sQuery(id+"F4.wireOp",EDGE,"E68.trimOffspring")])]}),"instanceName":"7"});
            var Q344;
            Q344=makeQuery(id+"F6.opPattern","COPY",BODY,{"derivedFrom":makeQuery(id+"F5.opExtrude","SWEPT_BODY",BODY,{"disambiguationData":[OSD([sQuery(id+"F4.wireOp",EDGE,"E24"),sQuery(id+"F4.wireOp",EDGE,"E25"),sQuery(id+"F4.wireOp",EDGE,"E27"),sQuery(id+"F4.wireOp",EDGE,"E28"),sQuery(id+"F4.wireOp",EDGE,"E29"),sQuery(id+"F4.wireOp",EDGE,"E30.0.MirrorCS"),sQuery(id+"F4.wireOp",EDGE,"E31.0.MirrorCS"),sQuery(id+"F4.wireOp",EDGE,"E32.0.MirrorCS"),sQuery(id+"F4.wireOp",EDGE,"E33.0.MirrorCS"),sQuery(id+"F4.wireOp",EDGE,"E34.0.MirrorCS"),sQuery(id+"F4.wireOp",EDGE,"E35.filletArc"),sQuery(id+"F4.wireOp",EDGE,"E36.filletArc"),sQuery(id+"F4.wireOp",EDGE,"E37"),sQuery(id+"F4.wireOp",EDGE,"E38"),sQuery(id+"F4.wireOp",EDGE,"E39"),sQuery(id+"F4.wireOp",EDGE,"E40"),sQuery(id+"F4.wireOp",EDGE,"E41"),sQuery(id+"F4.wireOp",EDGE,"E42"),sQuery(id+"F4.wireOp",EDGE,"E43.filletArc"),sQuery(id+"F4.wireOp",EDGE,"E44.filletArc"),sQuery(id+"F4.wireOp",EDGE,"E45.trimOffspring"),sQuery(id+"F4.wireOp",EDGE,"E46.trimOffspring"),sQuery(id+"F4.wireOp",EDGE,"E47"),sQuery(id+"F4.wireOp",EDGE,"E48"),sQuery(id+"F4.wireOp",EDGE,"E49"),sQuery(id+"F4.wireOp",EDGE,"E50"),sQuery(id+"F4.wireOp",EDGE,"E51"),sQuery(id+"F4.wireOp",EDGE,"E52"),sQuery(id+"F4.wireOp",EDGE,"E53"),sQuery(id+"F4.wireOp",EDGE,"E54.filletArc"),sQuery(id+"F4.wireOp",EDGE,"E55.filletArc"),sQuery(id+"F4.wireOp",EDGE,"E56.filletArc"),sQuery(id+"F4.wireOp",EDGE,"E57"),sQuery(id+"F4.wireOp",EDGE,"E58"),sQuery(id+"F4.wireOp",EDGE,"E59"),sQuery(id+"F4.wireOp",EDGE,"E60.trimOffspring"),sQuery(id+"F4.wireOp",EDGE,"E61.0.MirrorCS"),sQuery(id+"F4.wireOp",EDGE,"E61.1.MirrorCS"),sQuery(id+"F4.wireOp",EDGE,"E61.2.MirrorCS"),sQuery(id+"F4.wireOp",EDGE,"E61.4.MirrorCS"),sQuery(id+"F4.wireOp",EDGE,"E61.5.MirrorCS"),sQuery(id+"F4.wireOp",EDGE,"E61.7.MirrorCS"),sQuery(id+"F4.wireOp",EDGE,"E61.10.MirrorCS"),sQuery(id+"F4.wireOp",EDGE,"E62.0.MirrorCS"),sQuery(id+"F4.wireOp",EDGE,"E62.2.MirrorCS"),sQuery(id+"F4.wireOp",EDGE,"E62.3.MirrorCS"),sQuery(id+"F4.wireOp",EDGE,"E62.4.MirrorCS"),sQuery(id+"F4.wireOp",EDGE,"E61.3.MirrorCS"),sQuery(id+"F4.wireOp",EDGE,"E61.6.MirrorCS"),sQuery(id+"F4.wireOp",EDGE,"E63.0.MirrorCS"),sQuery(id+"F4.wireOp",EDGE,"E64.1.MirrorCS"),sQuery(id+"F4.wireOp",EDGE,"E64.2.MirrorCS"),sQuery(id+"F4.wireOp",EDGE,"E64.3.MirrorCS"),sQuery(id+"F4.wireOp",EDGE,"E64.4.MirrorCS"),sQuery(id+"F4.wireOp",EDGE,"E64.5.MirrorCS"),sQuery(id+"F4.wireOp",EDGE,"E64.6.MirrorCS"),sQuery(id+"F4.wireOp",EDGE,"E65.0.MirrorCS"),sQuery(id+"F4.wireOp",EDGE,"E66.0.MirrorCS"),sQuery(id+"F4.wireOp",EDGE,"E67.trimOffspring"),sQuery(id+"F4.wireOp",EDGE,"E68.trimOffspring")])]}),"instanceName":"6"});
            var Q345;
            Q345=makeQuery(id+"F6.opPattern","COPY",BODY,{"derivedFrom":makeQuery(id+"F5.opExtrude","SWEPT_BODY",BODY,{"disambiguationData":[OSD([sQuery(id+"F4.wireOp",EDGE,"E24"),sQuery(id+"F4.wireOp",EDGE,"E25"),sQuery(id+"F4.wireOp",EDGE,"E27"),sQuery(id+"F4.wireOp",EDGE,"E28"),sQuery(id+"F4.wireOp",EDGE,"E29"),sQuery(id+"F4.wireOp",EDGE,"E30.0.MirrorCS"),sQuery(id+"F4.wireOp",EDGE,"E31.0.MirrorCS"),sQuery(id+"F4.wireOp",EDGE,"E32.0.MirrorCS"),sQuery(id+"F4.wireOp",EDGE,"E33.0.MirrorCS"),sQuery(id+"F4.wireOp",EDGE,"E34.0.MirrorCS"),sQuery(id+"F4.wireOp",EDGE,"E35.filletArc"),sQuery(id+"F4.wireOp",EDGE,"E36.filletArc"),sQuery(id+"F4.wireOp",EDGE,"E37"),sQuery(id+"F4.wireOp",EDGE,"E38"),sQuery(id+"F4.wireOp",EDGE,"E39"),sQuery(id+"F4.wireOp",EDGE,"E40"),sQuery(id+"F4.wireOp",EDGE,"E41"),sQuery(id+"F4.wireOp",EDGE,"E42"),sQuery(id+"F4.wireOp",EDGE,"E43.filletArc"),sQuery(id+"F4.wireOp",EDGE,"E44.filletArc"),sQuery(id+"F4.wireOp",EDGE,"E45.trimOffspring"),sQuery(id+"F4.wireOp",EDGE,"E46.trimOffspring"),sQuery(id+"F4.wireOp",EDGE,"E47"),sQuery(id+"F4.wireOp",EDGE,"E48"),sQuery(id+"F4.wireOp",EDGE,"E49"),sQuery(id+"F4.wireOp",EDGE,"E50"),sQuery(id+"F4.wireOp",EDGE,"E51"),sQuery(id+"F4.wireOp",EDGE,"E52"),sQuery(id+"F4.wireOp",EDGE,"E53"),sQuery(id+"F4.wireOp",EDGE,"E54.filletArc"),sQuery(id+"F4.wireOp",EDGE,"E55.filletArc"),sQuery(id+"F4.wireOp",EDGE,"E56.filletArc"),sQuery(id+"F4.wireOp",EDGE,"E57"),sQuery(id+"F4.wireOp",EDGE,"E58"),sQuery(id+"F4.wireOp",EDGE,"E59"),sQuery(id+"F4.wireOp",EDGE,"E60.trimOffspring"),sQuery(id+"F4.wireOp",EDGE,"E61.0.MirrorCS"),sQuery(id+"F4.wireOp",EDGE,"E61.1.MirrorCS"),sQuery(id+"F4.wireOp",EDGE,"E61.2.MirrorCS"),sQuery(id+"F4.wireOp",EDGE,"E61.4.MirrorCS"),sQuery(id+"F4.wireOp",EDGE,"E61.5.MirrorCS"),sQuery(id+"F4.wireOp",EDGE,"E61.7.MirrorCS"),sQuery(id+"F4.wireOp",EDGE,"E61.10.MirrorCS"),sQuery(id+"F4.wireOp",EDGE,"E62.0.MirrorCS"),sQuery(id+"F4.wireOp",EDGE,"E62.2.MirrorCS"),sQuery(id+"F4.wireOp",EDGE,"E62.3.MirrorCS"),sQuery(id+"F4.wireOp",EDGE,"E62.4.MirrorCS"),sQuery(id+"F4.wireOp",EDGE,"E61.3.MirrorCS"),sQuery(id+"F4.wireOp",EDGE,"E61.6.MirrorCS"),sQuery(id+"F4.wireOp",EDGE,"E63.0.MirrorCS"),sQuery(id+"F4.wireOp",EDGE,"E64.1.MirrorCS"),sQuery(id+"F4.wireOp",EDGE,"E64.2.MirrorCS"),sQuery(id+"F4.wireOp",EDGE,"E64.3.MirrorCS"),sQuery(id+"F4.wireOp",EDGE,"E64.4.MirrorCS"),sQuery(id+"F4.wireOp",EDGE,"E64.5.MirrorCS"),sQuery(id+"F4.wireOp",EDGE,"E64.6.MirrorCS"),sQuery(id+"F4.wireOp",EDGE,"E65.0.MirrorCS"),sQuery(id+"F4.wireOp",EDGE,"E66.0.MirrorCS"),sQuery(id+"F4.wireOp",EDGE,"E67.trimOffspring"),sQuery(id+"F4.wireOp",EDGE,"E68.trimOffspring")])]}),"instanceName":"5"});
            var Q346;
            Q346=makeQuery(id+"F6.opPattern","COPY",BODY,{"derivedFrom":makeQuery(id+"F5.opExtrude","SWEPT_BODY",BODY,{"disambiguationData":[OSD([sQuery(id+"F4.wireOp",EDGE,"E24"),sQuery(id+"F4.wireOp",EDGE,"E25"),sQuery(id+"F4.wireOp",EDGE,"E27"),sQuery(id+"F4.wireOp",EDGE,"E28"),sQuery(id+"F4.wireOp",EDGE,"E29"),sQuery(id+"F4.wireOp",EDGE,"E30.0.MirrorCS"),sQuery(id+"F4.wireOp",EDGE,"E31.0.MirrorCS"),sQuery(id+"F4.wireOp",EDGE,"E32.0.MirrorCS"),sQuery(id+"F4.wireOp",EDGE,"E33.0.MirrorCS"),sQuery(id+"F4.wireOp",EDGE,"E34.0.MirrorCS"),sQuery(id+"F4.wireOp",EDGE,"E35.filletArc"),sQuery(id+"F4.wireOp",EDGE,"E36.filletArc"),sQuery(id+"F4.wireOp",EDGE,"E37"),sQuery(id+"F4.wireOp",EDGE,"E38"),sQuery(id+"F4.wireOp",EDGE,"E39"),sQuery(id+"F4.wireOp",EDGE,"E40"),sQuery(id+"F4.wireOp",EDGE,"E41"),sQuery(id+"F4.wireOp",EDGE,"E42"),sQuery(id+"F4.wireOp",EDGE,"E43.filletArc"),sQuery(id+"F4.wireOp",EDGE,"E44.filletArc"),sQuery(id+"F4.wireOp",EDGE,"E45.trimOffspring"),sQuery(id+"F4.wireOp",EDGE,"E46.trimOffspring"),sQuery(id+"F4.wireOp",EDGE,"E47"),sQuery(id+"F4.wireOp",EDGE,"E48"),sQuery(id+"F4.wireOp",EDGE,"E49"),sQuery(id+"F4.wireOp",EDGE,"E50"),sQuery(id+"F4.wireOp",EDGE,"E51"),sQuery(id+"F4.wireOp",EDGE,"E52"),sQuery(id+"F4.wireOp",EDGE,"E53"),sQuery(id+"F4.wireOp",EDGE,"E54.filletArc"),sQuery(id+"F4.wireOp",EDGE,"E55.filletArc"),sQuery(id+"F4.wireOp",EDGE,"E56.filletArc"),sQuery(id+"F4.wireOp",EDGE,"E57"),sQuery(id+"F4.wireOp",EDGE,"E58"),sQuery(id+"F4.wireOp",EDGE,"E59"),sQuery(id+"F4.wireOp",EDGE,"E60.trimOffspring"),sQuery(id+"F4.wireOp",EDGE,"E61.0.MirrorCS"),sQuery(id+"F4.wireOp",EDGE,"E61.1.MirrorCS"),sQuery(id+"F4.wireOp",EDGE,"E61.2.MirrorCS"),sQuery(id+"F4.wireOp",EDGE,"E61.4.MirrorCS"),sQuery(id+"F4.wireOp",EDGE,"E61.5.MirrorCS"),sQuery(id+"F4.wireOp",EDGE,"E61.7.MirrorCS"),sQuery(id+"F4.wireOp",EDGE,"E61.10.MirrorCS"),sQuery(id+"F4.wireOp",EDGE,"E62.0.MirrorCS"),sQuery(id+"F4.wireOp",EDGE,"E62.2.MirrorCS"),sQuery(id+"F4.wireOp",EDGE,"E62.3.MirrorCS"),sQuery(id+"F4.wireOp",EDGE,"E62.4.MirrorCS"),sQuery(id+"F4.wireOp",EDGE,"E61.3.MirrorCS"),sQuery(id+"F4.wireOp",EDGE,"E61.6.MirrorCS"),sQuery(id+"F4.wireOp",EDGE,"E63.0.MirrorCS"),sQuery(id+"F4.wireOp",EDGE,"E64.1.MirrorCS"),sQuery(id+"F4.wireOp",EDGE,"E64.2.MirrorCS"),sQuery(id+"F4.wireOp",EDGE,"E64.3.MirrorCS"),sQuery(id+"F4.wireOp",EDGE,"E64.4.MirrorCS"),sQuery(id+"F4.wireOp",EDGE,"E64.5.MirrorCS"),sQuery(id+"F4.wireOp",EDGE,"E64.6.MirrorCS"),sQuery(id+"F4.wireOp",EDGE,"E65.0.MirrorCS"),sQuery(id+"F4.wireOp",EDGE,"E66.0.MirrorCS"),sQuery(id+"F4.wireOp",EDGE,"E67.trimOffspring"),sQuery(id+"F4.wireOp",EDGE,"E68.trimOffspring")])]}),"instanceName":"4"});
            var Q347;
            Q347=makeQuery(id+"F6.opPattern","COPY",BODY,{"derivedFrom":makeQuery(id+"F5.opExtrude","SWEPT_BODY",BODY,{"disambiguationData":[OSD([sQuery(id+"F4.wireOp",EDGE,"E24"),sQuery(id+"F4.wireOp",EDGE,"E25"),sQuery(id+"F4.wireOp",EDGE,"E27"),sQuery(id+"F4.wireOp",EDGE,"E28"),sQuery(id+"F4.wireOp",EDGE,"E29"),sQuery(id+"F4.wireOp",EDGE,"E30.0.MirrorCS"),sQuery(id+"F4.wireOp",EDGE,"E31.0.MirrorCS"),sQuery(id+"F4.wireOp",EDGE,"E32.0.MirrorCS"),sQuery(id+"F4.wireOp",EDGE,"E33.0.MirrorCS"),sQuery(id+"F4.wireOp",EDGE,"E34.0.MirrorCS"),sQuery(id+"F4.wireOp",EDGE,"E35.filletArc"),sQuery(id+"F4.wireOp",EDGE,"E36.filletArc"),sQuery(id+"F4.wireOp",EDGE,"E37"),sQuery(id+"F4.wireOp",EDGE,"E38"),sQuery(id+"F4.wireOp",EDGE,"E39"),sQuery(id+"F4.wireOp",EDGE,"E40"),sQuery(id+"F4.wireOp",EDGE,"E41"),sQuery(id+"F4.wireOp",EDGE,"E42"),sQuery(id+"F4.wireOp",EDGE,"E43.filletArc"),sQuery(id+"F4.wireOp",EDGE,"E44.filletArc"),sQuery(id+"F4.wireOp",EDGE,"E45.trimOffspring"),sQuery(id+"F4.wireOp",EDGE,"E46.trimOffspring"),sQuery(id+"F4.wireOp",EDGE,"E47"),sQuery(id+"F4.wireOp",EDGE,"E48"),sQuery(id+"F4.wireOp",EDGE,"E49"),sQuery(id+"F4.wireOp",EDGE,"E50"),sQuery(id+"F4.wireOp",EDGE,"E51"),sQuery(id+"F4.wireOp",EDGE,"E52"),sQuery(id+"F4.wireOp",EDGE,"E53"),sQuery(id+"F4.wireOp",EDGE,"E54.filletArc"),sQuery(id+"F4.wireOp",EDGE,"E55.filletArc"),sQuery(id+"F4.wireOp",EDGE,"E56.filletArc"),sQuery(id+"F4.wireOp",EDGE,"E57"),sQuery(id+"F4.wireOp",EDGE,"E58"),sQuery(id+"F4.wireOp",EDGE,"E59"),sQuery(id+"F4.wireOp",EDGE,"E60.trimOffspring"),sQuery(id+"F4.wireOp",EDGE,"E61.0.MirrorCS"),sQuery(id+"F4.wireOp",EDGE,"E61.1.MirrorCS"),sQuery(id+"F4.wireOp",EDGE,"E61.2.MirrorCS"),sQuery(id+"F4.wireOp",EDGE,"E61.4.MirrorCS"),sQuery(id+"F4.wireOp",EDGE,"E61.5.MirrorCS"),sQuery(id+"F4.wireOp",EDGE,"E61.7.MirrorCS"),sQuery(id+"F4.wireOp",EDGE,"E61.10.MirrorCS"),sQuery(id+"F4.wireOp",EDGE,"E62.0.MirrorCS"),sQuery(id+"F4.wireOp",EDGE,"E62.2.MirrorCS"),sQuery(id+"F4.wireOp",EDGE,"E62.3.MirrorCS"),sQuery(id+"F4.wireOp",EDGE,"E62.4.MirrorCS"),sQuery(id+"F4.wireOp",EDGE,"E61.3.MirrorCS"),sQuery(id+"F4.wireOp",EDGE,"E61.6.MirrorCS"),sQuery(id+"F4.wireOp",EDGE,"E63.0.MirrorCS"),sQuery(id+"F4.wireOp",EDGE,"E64.1.MirrorCS"),sQuery(id+"F4.wireOp",EDGE,"E64.2.MirrorCS"),sQuery(id+"F4.wireOp",EDGE,"E64.3.MirrorCS"),sQuery(id+"F4.wireOp",EDGE,"E64.4.MirrorCS"),sQuery(id+"F4.wireOp",EDGE,"E64.5.MirrorCS"),sQuery(id+"F4.wireOp",EDGE,"E64.6.MirrorCS"),sQuery(id+"F4.wireOp",EDGE,"E65.0.MirrorCS"),sQuery(id+"F4.wireOp",EDGE,"E66.0.MirrorCS"),sQuery(id+"F4.wireOp",EDGE,"E67.trimOffspring"),sQuery(id+"F4.wireOp",EDGE,"E68.trimOffspring")])]}),"instanceName":"3"});
            var Q348;
            Q348=makeQuery(id+"F6.opPattern","COPY",BODY,{"derivedFrom":makeQuery(id+"F5.opExtrude","SWEPT_BODY",BODY,{"disambiguationData":[OSD([sQuery(id+"F4.wireOp",EDGE,"E24"),sQuery(id+"F4.wireOp",EDGE,"E25"),sQuery(id+"F4.wireOp",EDGE,"E27"),sQuery(id+"F4.wireOp",EDGE,"E28"),sQuery(id+"F4.wireOp",EDGE,"E29"),sQuery(id+"F4.wireOp",EDGE,"E30.0.MirrorCS"),sQuery(id+"F4.wireOp",EDGE,"E31.0.MirrorCS"),sQuery(id+"F4.wireOp",EDGE,"E32.0.MirrorCS"),sQuery(id+"F4.wireOp",EDGE,"E33.0.MirrorCS"),sQuery(id+"F4.wireOp",EDGE,"E34.0.MirrorCS"),sQuery(id+"F4.wireOp",EDGE,"E35.filletArc"),sQuery(id+"F4.wireOp",EDGE,"E36.filletArc"),sQuery(id+"F4.wireOp",EDGE,"E37"),sQuery(id+"F4.wireOp",EDGE,"E38"),sQuery(id+"F4.wireOp",EDGE,"E39"),sQuery(id+"F4.wireOp",EDGE,"E40"),sQuery(id+"F4.wireOp",EDGE,"E41"),sQuery(id+"F4.wireOp",EDGE,"E42"),sQuery(id+"F4.wireOp",EDGE,"E43.filletArc"),sQuery(id+"F4.wireOp",EDGE,"E44.filletArc"),sQuery(id+"F4.wireOp",EDGE,"E45.trimOffspring"),sQuery(id+"F4.wireOp",EDGE,"E46.trimOffspring"),sQuery(id+"F4.wireOp",EDGE,"E47"),sQuery(id+"F4.wireOp",EDGE,"E48"),sQuery(id+"F4.wireOp",EDGE,"E49"),sQuery(id+"F4.wireOp",EDGE,"E50"),sQuery(id+"F4.wireOp",EDGE,"E51"),sQuery(id+"F4.wireOp",EDGE,"E52"),sQuery(id+"F4.wireOp",EDGE,"E53"),sQuery(id+"F4.wireOp",EDGE,"E54.filletArc"),sQuery(id+"F4.wireOp",EDGE,"E55.filletArc"),sQuery(id+"F4.wireOp",EDGE,"E56.filletArc"),sQuery(id+"F4.wireOp",EDGE,"E57"),sQuery(id+"F4.wireOp",EDGE,"E58"),sQuery(id+"F4.wireOp",EDGE,"E59"),sQuery(id+"F4.wireOp",EDGE,"E60.trimOffspring"),sQuery(id+"F4.wireOp",EDGE,"E61.0.MirrorCS"),sQuery(id+"F4.wireOp",EDGE,"E61.1.MirrorCS"),sQuery(id+"F4.wireOp",EDGE,"E61.2.MirrorCS"),sQuery(id+"F4.wireOp",EDGE,"E61.4.MirrorCS"),sQuery(id+"F4.wireOp",EDGE,"E61.5.MirrorCS"),sQuery(id+"F4.wireOp",EDGE,"E61.7.MirrorCS"),sQuery(id+"F4.wireOp",EDGE,"E61.10.MirrorCS"),sQuery(id+"F4.wireOp",EDGE,"E62.0.MirrorCS"),sQuery(id+"F4.wireOp",EDGE,"E62.2.MirrorCS"),sQuery(id+"F4.wireOp",EDGE,"E62.3.MirrorCS"),sQuery(id+"F4.wireOp",EDGE,"E62.4.MirrorCS"),sQuery(id+"F4.wireOp",EDGE,"E61.3.MirrorCS"),sQuery(id+"F4.wireOp",EDGE,"E61.6.MirrorCS"),sQuery(id+"F4.wireOp",EDGE,"E63.0.MirrorCS"),sQuery(id+"F4.wireOp",EDGE,"E64.1.MirrorCS"),sQuery(id+"F4.wireOp",EDGE,"E64.2.MirrorCS"),sQuery(id+"F4.wireOp",EDGE,"E64.3.MirrorCS"),sQuery(id+"F4.wireOp",EDGE,"E64.4.MirrorCS"),sQuery(id+"F4.wireOp",EDGE,"E64.5.MirrorCS"),sQuery(id+"F4.wireOp",EDGE,"E64.6.MirrorCS"),sQuery(id+"F4.wireOp",EDGE,"E65.0.MirrorCS"),sQuery(id+"F4.wireOp",EDGE,"E66.0.MirrorCS"),sQuery(id+"F4.wireOp",EDGE,"E67.trimOffspring"),sQuery(id+"F4.wireOp",EDGE,"E68.trimOffspring")])]}),"instanceName":"2"});
            var Q349;
            Q349=makeQuery(id+"F6.opPattern","COPY",BODY,{"derivedFrom":makeQuery(id+"F5.opExtrude","SWEPT_BODY",BODY,{"disambiguationData":[OSD([sQuery(id+"F4.wireOp",EDGE,"E24"),sQuery(id+"F4.wireOp",EDGE,"E25"),sQuery(id+"F4.wireOp",EDGE,"E27"),sQuery(id+"F4.wireOp",EDGE,"E28"),sQuery(id+"F4.wireOp",EDGE,"E29"),sQuery(id+"F4.wireOp",EDGE,"E30.0.MirrorCS"),sQuery(id+"F4.wireOp",EDGE,"E31.0.MirrorCS"),sQuery(id+"F4.wireOp",EDGE,"E32.0.MirrorCS"),sQuery(id+"F4.wireOp",EDGE,"E33.0.MirrorCS"),sQuery(id+"F4.wireOp",EDGE,"E34.0.MirrorCS"),sQuery(id+"F4.wireOp",EDGE,"E35.filletArc"),sQuery(id+"F4.wireOp",EDGE,"E36.filletArc"),sQuery(id+"F4.wireOp",EDGE,"E37"),sQuery(id+"F4.wireOp",EDGE,"E38"),sQuery(id+"F4.wireOp",EDGE,"E39"),sQuery(id+"F4.wireOp",EDGE,"E40"),sQuery(id+"F4.wireOp",EDGE,"E41"),sQuery(id+"F4.wireOp",EDGE,"E42"),sQuery(id+"F4.wireOp",EDGE,"E43.filletArc"),sQuery(id+"F4.wireOp",EDGE,"E44.filletArc"),sQuery(id+"F4.wireOp",EDGE,"E45.trimOffspring"),sQuery(id+"F4.wireOp",EDGE,"E46.trimOffspring"),sQuery(id+"F4.wireOp",EDGE,"E47"),sQuery(id+"F4.wireOp",EDGE,"E48"),sQuery(id+"F4.wireOp",EDGE,"E49"),sQuery(id+"F4.wireOp",EDGE,"E50"),sQuery(id+"F4.wireOp",EDGE,"E51"),sQuery(id+"F4.wireOp",EDGE,"E52"),sQuery(id+"F4.wireOp",EDGE,"E53"),sQuery(id+"F4.wireOp",EDGE,"E54.filletArc"),sQuery(id+"F4.wireOp",EDGE,"E55.filletArc"),sQuery(id+"F4.wireOp",EDGE,"E56.filletArc"),sQuery(id+"F4.wireOp",EDGE,"E57"),sQuery(id+"F4.wireOp",EDGE,"E58"),sQuery(id+"F4.wireOp",EDGE,"E59"),sQuery(id+"F4.wireOp",EDGE,"E60.trimOffspring"),sQuery(id+"F4.wireOp",EDGE,"E61.0.MirrorCS"),sQuery(id+"F4.wireOp",EDGE,"E61.1.MirrorCS"),sQuery(id+"F4.wireOp",EDGE,"E61.2.MirrorCS"),sQuery(id+"F4.wireOp",EDGE,"E61.4.MirrorCS"),sQuery(id+"F4.wireOp",EDGE,"E61.5.MirrorCS"),sQuery(id+"F4.wireOp",EDGE,"E61.7.MirrorCS"),sQuery(id+"F4.wireOp",EDGE,"E61.10.MirrorCS"),sQuery(id+"F4.wireOp",EDGE,"E62.0.MirrorCS"),sQuery(id+"F4.wireOp",EDGE,"E62.2.MirrorCS"),sQuery(id+"F4.wireOp",EDGE,"E62.3.MirrorCS"),sQuery(id+"F4.wireOp",EDGE,"E62.4.MirrorCS"),sQuery(id+"F4.wireOp",EDGE,"E61.3.MirrorCS"),sQuery(id+"F4.wireOp",EDGE,"E61.6.MirrorCS"),sQuery(id+"F4.wireOp",EDGE,"E63.0.MirrorCS"),sQuery(id+"F4.wireOp",EDGE,"E64.1.MirrorCS"),sQuery(id+"F4.wireOp",EDGE,"E64.2.MirrorCS"),sQuery(id+"F4.wireOp",EDGE,"E64.3.MirrorCS"),sQuery(id+"F4.wireOp",EDGE,"E64.4.MirrorCS"),sQuery(id+"F4.wireOp",EDGE,"E64.5.MirrorCS"),sQuery(id+"F4.wireOp",EDGE,"E64.6.MirrorCS"),sQuery(id+"F4.wireOp",EDGE,"E65.0.MirrorCS"),sQuery(id+"F4.wireOp",EDGE,"E66.0.MirrorCS"),sQuery(id+"F4.wireOp",EDGE,"E67.trimOffspring"),sQuery(id+"F4.wireOp",EDGE,"E68.trimOffspring")])]}),"instanceName":"39"});
            var Q350;
            Q350=makeQuery(id+"F2.opRevolve","SWEPT_BODY",BODY,{"disambiguationData":[OSD([sQuery(id+"F0.wireOp",EDGE,"E0"),sQuery(id+"F0.wireOp",EDGE,"E1"),sQuery(id+"F0.wireOp",EDGE,"E2"),sQuery(id+"F0.wireOp",EDGE,"E3"),sQuery(id+"F0.wireOp",EDGE,"E4"),sQuery(id+"F0.wireOp",EDGE,"E5"),sQuery(id+"F0.wireOp",EDGE,"E6.bottom"),sQuery(id+"F0.wireOp",EDGE,"E6.top"),sQuery(id+"F0.wireOp",EDGE,"E6.right"),sQuery(id+"F0.wireOp",EDGE,"E7.bottom"),sQuery(id+"F0.wireOp",EDGE,"E7.top"),sQuery(id+"F0.wireOp",EDGE,"E7.right"),sQuery(id+"F0.wireOp",EDGE,"E8.bottom"),sQuery(id+"F0.wireOp",EDGE,"E8.top"),sQuery(id+"F0.wireOp",EDGE,"E8.right"),sQuery(id+"F0.wireOp",EDGE,"E10.trimOffspring"),sQuery(id+"F0.wireOp",EDGE,"E11.trimOffspring"),sQuery(id+"F0.wireOp",EDGE,"E12.trimOffspring")])]});
            booleanBodies(context, id + "F7", {"operationType" : BooleanOperationType.SUBTRACTION, "tools" : qUnion([Q0, Q1, Q2, Q3, Q4, Q5, Q6, Q7, Q8, Q9, Q10, Q11, Q12, Q13, Q14, Q15, Q16, Q17, Q18, Q19, Q20, Q21, Q22, Q23, Q24, Q25, Q26, Q27, Q28, Q29, Q30, Q31, Q32, Q33, Q34, Q35, Q36, Q37, Q38, Q39, Q40, Q41, Q42, Q43, Q44, Q45, Q46, Q47, Q48, Q49, Q50, Q51, Q52, Q53, Q54, Q55, Q56, Q57, Q58, Q59, Q60, Q61, Q62, Q63, Q64, Q65, Q66, Q67, Q68, Q69, Q70, Q71, Q72, Q73, Q74, Q75, Q76, Q77, Q78, Q79, Q80, Q81, Q82, Q83, Q84, Q85, Q86, Q87, Q88, Q89, Q90, Q91, Q92, Q93, Q94, Q95, Q96, Q97, Q98, Q99, Q100, Q101, Q102, Q103, Q104, Q105, Q106, Q107, Q108, Q109, Q110, Q111, Q112, Q113, Q114, Q115, Q116, Q117, Q118, Q119, Q120, Q121, Q122, Q123, Q124, Q125, Q126, Q127, Q128, Q129, Q130, Q131, Q132, Q133, Q134, Q135, Q136, Q137, Q138, Q139, Q140, Q141, Q142, Q143, Q144, Q145, Q146, Q147, Q148, Q149, Q150, Q151, Q152, Q153, Q154, Q155, Q156, Q157, Q158, Q159, Q160, Q161, Q162, Q163, Q164, Q165, Q166, Q167, Q168, Q169, Q170, Q171, Q172, Q173, Q174, Q175, Q176, Q177, Q178, Q179, Q180, Q181, Q182, Q183, Q184, Q185, Q186, Q187, Q188, Q189, Q190, Q191, Q192, Q193, Q194, Q195, Q196, Q197, Q198, Q199, Q200, Q201, Q202, Q203, Q204, Q205, Q206, Q207, Q208, Q209, Q210, Q211, Q212, Q213, Q214, Q215, Q216, Q217, Q218, Q219, Q220, Q221, Q222, Q223, Q224, Q225, Q226, Q227, Q228, Q229, Q230, Q231, Q232, Q233, Q234, Q235, Q236, Q237, Q238, Q239, Q240, Q241, Q242, Q243, Q244, Q245, Q246, Q247, Q248, Q249, Q250, Q251, Q252, Q253, Q254, Q255, Q256, Q257, Q258, Q259, Q260, Q261, Q262, Q263, Q264, Q265, Q266, Q267, Q268, Q269, Q270, Q271, Q272, Q273, Q274, Q275, Q276, Q277, Q278, Q279, Q280, Q281, Q282, Q283, Q284, Q285, Q286, Q287, Q288, Q289, Q290, Q291, Q292, Q293, Q294, Q295, Q296, Q297, Q298, Q299, Q300, Q301, Q302, Q303, Q304, Q305, Q306, Q307, Q308, Q309, Q310, Q311, Q312, Q313, Q314, Q315, Q316, Q317, Q318, Q319, Q320, Q321, Q322, Q323, Q324, Q325, Q326, Q327, Q328, Q329, Q330, Q331, Q332, Q333, Q334, Q335, Q336, Q337, Q338, Q339, Q340, Q341, Q342, Q343, Q344, Q345, Q346, Q347, Q348, Q349]), "targets" : qUnion([Q350])});
        }
        {
            var Q0;
            Q0=qCreatedBy(makeId("Front.planeOp"),FACE);
            var sketch = newSketch(context, id + "F8", { "sketchPlane" : qUnion([Q0])});
            skCircle(sketch, "E90", {"center": v(0, 0) * mm, "radius": 165.1 * mm});
            skCircle(sketch, "E91", {"center": v(0, 0) * mm, "radius": 152.4 * mm});
            skSolve(sketch);
        }
        {
            var Q0;
            Q0=qCreatedBy(makeId("Front.planeOp"),FACE);
            cPlane(context, id + "F9", {"entities" : qUnion([Q0]), "cplaneType" : CPlaneType.OFFSET, "offset" : 152.4 * mm, "width" : 152.4 * mm, "height" : 152.4 * mm});
        }
        {
            var Q0;
            Q0=qCreatedBy(id+"F9.planeOp",FACE);
            var sketch = newSketch(context, id + "F10", { "sketchPlane" : qUnion([Q0])});
            skCircle(sketch, "E92.0", {"center": v(0, 0) * mm, "radius": 165.1 * mm});
            skCircle(sketch, "E93.0", {"center": v(0, 0) * mm, "radius": 152.4 * mm});
            skSolve(sketch);
        }
        {
            var Q0;
            Q0=makeQuery(id+"F10.imprint","IMPRINT",FACE,{"disambiguationData":[TD([[makeQuery(id+"F10.imprint","IMPRINT",EDGE,{"derivedFrom":sQuery(id+"F10.wireOp",EDGE,"E92.0")}),1.0]])]});
            var Q1;
            Q1=makeQuery(id+"F2.opRevolve","SWEPT_FACE",FACE,{"disambiguationData":[OSD([sQuery(id+"F0.wireOp",EDGE,"E1")])]});
            extrude(context, id + "F11", {"entities" : qUnion([Q0]), "operationType" : NewBodyOperationType.REMOVE, "endBound" : BoundingType.UP_TO_SURFACE, "oppositeDirection" : true, "endBoundEntityFace" : qUnion([Q1]), "depth" : 25.4 * mm});
        }
        {
            var Q0;
            {var subQ0=sQuery(id+"F0.wireOp",EDGE,"E3");var subQ1=sQuery(id+"F0.wireOp",EDGE,"E12.trimOffspring");Q0=makeQuery(id+"F7.opBoolean","SPLIT",EDGE,{"disambiguationData":[TD([makeQuery(id+"F5.opExtrude","SWEPT_FACE",FACE,{"disambiguationData":[OSD([sQuery(id+"F4.wireOp",EDGE,"E86.0.MirrorCS")])]})])],"derivedFrom":makeQuery(id+"F2.opRevolve","SWEPT_EDGE",EDGE,{"disambiguationData":[OSD([subQ0,subQ1])]})});}
            var Q1;
            {var subQ0=sQuery(id+"F0.wireOp",EDGE,"E1");var subQ1=sQuery(id+"F0.wireOp",EDGE,"E2");Q1=makeQuery(id+"F7.opBoolean","SPLIT",EDGE,{"disambiguationData":[TD([makeQuery(id+"F6.opPattern","COPY",FACE,{"derivedFrom":makeQuery(id+"F5.opExtrude","SWEPT_FACE",FACE,{"disambiguationData":[OSD([sQuery(id+"F4.wireOp",EDGE,"E72")])]}),"instanceName":"47"})])],"derivedFrom":makeQuery(id+"F2.opRevolve","SWEPT_EDGE",EDGE,{"disambiguationData":[OSD([subQ0,subQ1])]})});}
            fillet(context, id + "F12", {"entities" : qUnion([Q0, Q1]), "radius" : 15.24 * mm, "tangentPropagation" : true, "allowEdgeOverflow" : false});
        }
    });
